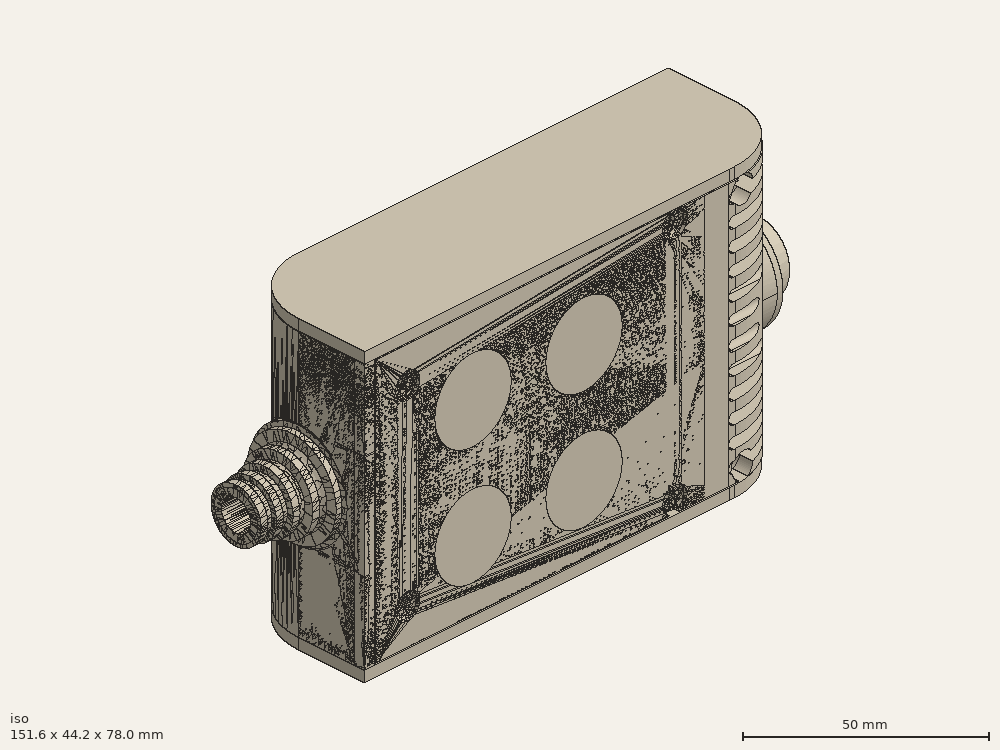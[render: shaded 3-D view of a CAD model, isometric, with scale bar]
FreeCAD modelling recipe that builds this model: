
FCSTD DOCUMENT  (FreeCAD 0.19R0.19.2)
Label: enclosure_193FCStd
License: All rights reserved
LicenseURL: http://en.wikipedia.org/wiki/All_rights_reserved
objects: Part::Revolution×152, Part::MultiFuse×146, Part::Feature×146, Sketcher::SketchObject×84, Part::Cut×70, Part::Cylinder×70, Part::Extrusion×67, Part::Fillet×58, Part::Box×36, App::MeasureDistance×4, PartDesign::Body×2, Image::ImagePlane×1
note: 831 computed .brp shape members not serialized (recipe doc carries the construction recipe); baked Part::Feature solids carry a one-line shape summary decoded from their .brp

FEATURE [Sketcher::SketchObject] Sketch  label="topSketch"
  FullyConstrained = true
  sketch-geometry (20):
    g0: LineSegment StartX=5.21097e-06 StartY=3 StartZ=0 EndX=5.21097e-06 EndY=19 EndZ=0
    g1: ArcOfCircle CenterX=19 CenterY=19 CenterZ=0 NormalX=0 NormalY=0 NormalZ=1 AngleXU=0 Radius=19 StartAngle=1.5708 EndAngle=3.14159
    g2: ArcOfCircle CenterX=19 CenterY=19 CenterZ=0 NormalX=0 NormalY=0 NormalZ=1 AngleXU=0 Radius=16 StartAngle=1.5708 EndAngle=3.14159
    g3: LineSegment StartX=114 StartY=35 StartZ=0 EndX=19 EndY=35 EndZ=0
    g4: LineSegment StartX=5.21097e-06 StartY=3 StartZ=0 EndX=5.21097e-06 EndY=0 EndZ=0
    g5: LineSegment StartX=3 StartY=0 StartZ=0 EndX=5.21097e-06 EndY=0 EndZ=0
    g6: LineSegment StartX=3 StartY=19 StartZ=0 EndX=3 EndY=0 EndZ=0
    g7: LineSegment StartX=19 StartY=38 StartZ=0 EndX=124 EndY=38 EndZ=0
    g8: Circle CenterX=119 CenterY=35 CenterZ=0 NormalX=0 NormalY=0 NormalZ=1 AngleXU=0 Radius=1
    g9: Circle CenterX=121 CenterY=35 CenterZ=0 NormalX=0 NormalY=0 NormalZ=1 AngleXU=0 Radius=1
    g10: Circle CenterX=121 CenterY=33 CenterZ=0 NormalX=0 NormalY=0 NormalZ=1 AngleXU=0 Radius=1
    g11: BSplineCurve PolesCount=3 KnotsCount=2 Degree=2 IsPeriodic=0
    g12: GeomPoint X=119 Y=35 Z=0
    g13: GeomPoint X=121 Y=33 Z=0
    g14: LineSegment StartX=119 StartY=35 StartZ=0 EndX=114 EndY=35 EndZ=0
    g15: ArcOfCircle CenterX=105 CenterY=19 CenterZ=0 NormalX=0 NormalY=0 NormalZ=1 AngleXU=0 Radius=19 StartAngle=5.7297 EndAngle=6.28319
    g16: ArcOfCircle CenterX=105 CenterY=19 CenterZ=0 NormalX=0 NormalY=0 NormalZ=1 AngleXU=0 Radius=16 StartAngle=5.60905 EndAngle=6.28319
    g17: LineSegment StartX=121 StartY=33 StartZ=0 EndX=121 EndY=19 EndZ=0
    g18: LineSegment StartX=124 StartY=38 StartZ=0 EndX=124 EndY=19 EndZ=0
    g19: LineSegment StartX=117.5 StartY=9.01251 StartZ=0 EndX=121.163 EndY=9.0125 EndZ=0
  constraints (46):
    c: Vertical(g0)
    c: Block(g0)
    c: Coincident(g1,g0)
    c: Block(g1)
    c: Coincident(g2,g1)
    c: Block(g2)
    c: Coincident(g3,g2)
    c: Horizontal(g3)
    c: Tangent(g3,g2)
    c: Coincident(g4,g0)
    c: Distance(g4) = 3
    c: Vertical(g4)
    c: Coincident(g5,g4)
    c: Horizontal(g5)
    c: Coincident(g6,g2)
    c: Coincident(g6,g5)
    c: Vertical(g6)
    c: Horizontal(g7)
    c: Distance(g7) = 105
    c: Coincident(g7,g1)
    c: Block(g3)
    c: Weight(g8) = 1
    c: Equal(g8,g9)
    c: Equal(g8,g10)
    c: InternalAlignment(g8,g11)
    c: InternalAlignment(g9,g11)
    c: InternalAlignment(g10,g11)
    c: InternalAlignment(g12,g11)
    c: InternalAlignment(g13,g11)
    c: Block(g11)
    c: Coincident(g14,g11)
    c: Coincident(g14,g3)
    c: Horizontal(g14)
    c: Block(g15)
    c: Coincident(g16,g15)
    c: Block(g16)
    c: Coincident(g17,g11)
    c: Coincident(g17,g16)
    c: Vertical(g17)
    c: Distance(g17) = 14
    c: Coincident(g18,g7)
    c: Coincident(g18,g15)
    c: Vertical(g18)
    c: Distance(g18) = 19
    c: Coincident(g19,g16)
    c: Coincident(g19,g15)
FEATURE [Sketcher::SketchObject] Sketch001  label="bottomSketch"
  FullyConstrained = true
  sketch-geometry (32):
    g0: LineSegment StartX=3.3 StartY=-6.03275e-07 StartZ=0 EndX=98 EndY=-6.03275e-07 EndZ=0
    g1: ArcOfCircle CenterX=98 CenterY=19 CenterZ=0 NormalX=0 NormalY=0 NormalZ=1 AngleXU=0 Radius=19 StartAngle=4.71239 EndAngle=5.71103
    g2: LineSegment StartX=6.3 StartY=8 StartZ=0 EndX=3.3 EndY=8 EndZ=0
    g3: LineSegment StartX=3.3 StartY=8 StartZ=0 EndX=3.3 EndY=-6.03275e-07 EndZ=0
    g4: ArcOfCircle CenterX=8.3 CenterY=5 CenterZ=0 NormalX=0 NormalY=0 NormalZ=1 AngleXU=0 Radius=2 StartAngle=3.14159 EndAngle=4.71239
    g5: LineSegment StartX=6.3 StartY=8 StartZ=0 EndX=6.3 EndY=5 EndZ=0
    g6: ArcOfCircle CenterX=98 CenterY=19 CenterZ=0 NormalX=0 NormalY=0 NormalZ=1 AngleXU=0 Radius=12.7 StartAngle=4.71239 EndAngle=6.28319
    g7: LineSegment StartX=94.7 StartY=3 StartZ=0 EndX=8.3 EndY=3 EndZ=0
    g8-g12: Circle x5 (B-spline internal-alignment scaffolding for g13; pole/knot coordinates omitted)
    g13: BSplineCurve PolesCount=5 KnotsCount=3 Degree=3 IsPeriodic=0
    g14: GeomPoint X=98 Y=6.3 Z=0
    g15: GeomPoint X=96.3938 Y=4.71946 Z=0
    g16: GeomPoint X=94.7 Y=3 Z=0
    g17-g23: Circle x7 (B-spline internal-alignment scaffolding for g24; pole/knot coordinates omitted)
    g24: BSplineCurve PolesCount=7 KnotsCount=5 Degree=3 IsPeriodic=0
    g25-g29: GeomPoint x5 (B-spline internal-alignment scaffolding for g24; pole/knot coordinates omitted)
    g30: ArcOfCircle CenterX=98 CenterY=19 CenterZ=0 NormalX=0 NormalY=0 NormalZ=1 AngleXU=0 Radius=15.7 StartAngle=5.81226 EndAngle=6.28319
    g31: LineSegment StartX=110.7 StartY=19 StartZ=0 EndX=113.7 EndY=19 EndZ=0
  constraints (41):
    c: Horizontal(g0)
    c: Coincident(g1,g0)
    c: Block(g1)
    c: Horizontal(g2)
    c: Distance(g2) = 3
    c: Coincident(g3,g2)
    c: Vertical(g3)
    c: Coincident(g3,g0)
    c: Block(g4)
    c: Block(g2)
    c: Coincident(g5,g2)
    c: Coincident(g5,g4)
    c: Vertical(g5)
    c: Coincident(g6,g1)
    c: Block(g6)
    c: Coincident(g7,g4)
    c: Horizontal(g7)
    c: Block(g0)
    c: Block(g7)
    c: Block(g3)
    c: Coincident(g13,g6)
    c: Weight(g8) = 1
    c: Equal(g8, g9-g12) x4
    c: Coincident(g13,g7)
    c: InternalAlignment(g8-g12 -> g13) x5
    c: InternalAlignment(g14,g13)
    c: InternalAlignment(g15,g13)
    c: InternalAlignment(g16,g13)
    c: Block(g13)
    c: Weight(g17) = 1
    c: Equal(g17, g18-g23) x6
    c: Coincident(g24,g1)
    c: InternalAlignment(g17-g23 -> g24) x7
    c: InternalAlignment(g25-g29 -> g24) x5
    c: Block(g24)
    c: Coincident(g30,g24)
    c: Coincident(g31,g6)
    c: Coincident(g31,g30)
    c: Horizontal(g31)
    c: Block(g31)
    c: Block(g30)
FEATURE [Part::Extrusion] Extrude  label="top"
  Base = -> Sketch
  Dir = (0,0,1)
  DirMode = 2
  FaceMakerClass = Part::FaceMakerBullseye
  LengthFwd = 72
  LengthRev = 0
  Solid = true
  Symmetric = false
FEATURE [Part::Extrusion] Extrude001  label="bottom"
  Base = -> Sketch001
  Dir = (0,0,1)
  DirMode = 2
  FaceMakerClass = Part::FaceMakerBullseye
  LengthFwd = 71.4
  LengthRev = 0
  Placement = pos=(0,0,0.3) rot=(0,0,1;0rad)
  Solid = true
  Symmetric = false
FEATURE [Sketcher::SketchObject] Sketch002  label="topSketch001"
  FullyConstrained = true
  sketch-geometry (8):
    g0: ArcOfCircle CenterX=19 CenterY=19.0975 CenterZ=0 NormalX=0 NormalY=0 NormalZ=1 AngleXU=0 Radius=18.9025 StartAngle=1.5708 EndAngle=3.14674
    g1: LineSegment StartX=0.0977805 StartY=19.0003 StartZ=0 EndX=0.0977805 EndY=0.000251602 EndZ=0
    g2: LineSegment StartX=19 StartY=38 StartZ=0 EndX=124 EndY=38 EndZ=0
    g3: LineSegment StartX=0.0977805 StartY=0.000251602 StartZ=0 EndX=105.098 EndY=0.000251602 EndZ=0
    g4: LineSegment StartX=124 StartY=38 StartZ=0 EndX=125.616 EndY=38 EndZ=0
    g5: LineSegment StartX=105.098 StartY=0.000251602 StartZ=0 EndX=106.713 EndY=0.000251602 EndZ=0
    g6: ArcOfCircle CenterX=106.616 CenterY=19 CenterZ=0 NormalX=0 NormalY=0 NormalZ=1 AngleXU=0 Radius=19 StartAngle=4.71754 EndAngle=6.28319
    g7: LineSegment StartX=125.616 StartY=38 StartZ=0 EndX=125.616 EndY=19 EndZ=0
  constraints (21):
    c: Block(g0)
    c: Coincident(g1,g0)
    c: Vertical(g1)
    c: Horizontal(g2)
    c: Distance(g2) = 105
    c: Coincident(g2,g0)
    c: Distance(g1) = 19
    c: Coincident(g3,g1)
    c: Horizontal(g3)
    c: Distance(g3) = 105
    c: Coincident(g4,g2)
    c: Horizontal(g4)
    c: Distance(g4) = 1.61553
    c: Horizontal(g5)
    c: Equal(g4,g5) = 1.61553
    c: Coincident(g5,g3)
    c: Block(g6)
    c: Coincident(g6,g5)
    c: Coincident(g7,g4)
    c: Coincident(g7,g6)
    c: Vertical(g7)
FEATURE [Part::Extrusion] Extrude002  label="sideA"
  Base = -> Sketch002
  Dir = (0,0,1)
  DirMode = 2
  FaceMakerClass = Part::FaceMakerBullseye
  LengthFwd = 3
  LengthRev = 0
  Placement = pos=(0,0,-3) rot=(0,0,1;0rad)
  Solid = true
  Symmetric = false
FEATURE [Sketcher::SketchObject] Sketch003  label="topSketch002"
  FullyConstrained = true
  sketch-geometry (6):
    g0: LineSegment StartX=19 StartY=38 StartZ=0 EndX=117 EndY=38 EndZ=0
    g1: ArcOfCircle CenterX=19 CenterY=19 CenterZ=0 NormalX=0 NormalY=0 NormalZ=1 AngleXU=0 Radius=19 StartAngle=1.5708 EndAngle=3.14159
    g2: LineSegment StartX=117 StartY=38 StartZ=0 EndX=117 EndY=19 EndZ=0
    g3: LineSegment StartX=98 StartY=1.0161e-12 StartZ=0 EndX=5.22862e-06 EndY=1.0161e-12 EndZ=0
    g4: LineSegment StartX=5.22862e-06 StartY=19 StartZ=0 EndX=5.22862e-06 EndY=1.0161e-12 EndZ=0
    g5: ArcOfCircle CenterX=98 CenterY=19 CenterZ=0 NormalX=0 NormalY=0 NormalZ=1 AngleXU=0 Radius=19 StartAngle=4.71239 EndAngle=6.28319
  constraints (16):
    c: Horizontal(g0)
    c: Distance(g0) = 98
    c: Coincident(g1,g0)
    c: Block(g1)
    c: Coincident(g2,g0)
    c: Vertical(g2)
    c: Distance(g2) = 19
    c: Horizontal(g3)
    c: Coincident(g4,g1)
    c: Vertical(g4)
    c: Coincident(g3,g4)
    c: Block(g3)
    c: Coincident(g5,g2)
    c: Coincident(g5,g3)
    c: Block(g0)
    c: Block(g5)
FEATURE [Sketcher::SketchObject] Sketch004
  FullyConstrained = true
  MapMode = 3
  Placement = pos=(0,0,0) rot=(1,0,0;1.5708rad)
  Support = -> [Extrude]
  sketch-geometry (8):
    g0: Circle CenterX=80.351 CenterY=-67.6202 CenterZ=0 NormalX=0 NormalY=0 NormalZ=1 AngleXU=0 Radius=2
    g1: Circle CenterX=80.351 CenterY=-67.6202 CenterZ=0 NormalX=0 NormalY=0 NormalZ=1 AngleXU=0 Radius=3
    g2: Circle CenterX=80.351 CenterY=-4.92017 CenterZ=0 NormalX=0 NormalY=0 NormalZ=1 AngleXU=0 Radius=2
    g3: Circle CenterX=80.351 CenterY=-4.92017 CenterZ=0 NormalX=0 NormalY=0 NormalZ=1 AngleXU=0 Radius=3
    g4: Circle CenterX=23.851 CenterY=-4.92017 CenterZ=0 NormalX=0 NormalY=0 NormalZ=1 AngleXU=0 Radius=2
    g5: Circle CenterX=23.851 CenterY=-4.92017 CenterZ=0 NormalX=0 NormalY=0 NormalZ=1 AngleXU=0 Radius=3
    g6: Circle CenterX=23.851 CenterY=-67.6202 CenterZ=0 NormalX=0 NormalY=0 NormalZ=1 AngleXU=0 Radius=2
    g7: Circle CenterX=23.851 CenterY=-67.6202 CenterZ=0 NormalX=0 NormalY=0 NormalZ=1 AngleXU=0 Radius=3
  constraints (8):
    c: Block(g3)
    c: Block(g2)
    c: Block(g1)
    c: Block(g0)
    c: Block(g6)
    c: Block(g7)
    c: Block(g4)
    c: Block(g5)
FEATURE [Part::Extrusion] Extrude004
  Base = -> Sketch004
  Dir = (0,-1,2e-16)
  DirMode = 2
  FaceMakerClass = Part::FaceMakerBullseye
  LengthFwd = 6
  LengthRev = 0
  Placement = pos=(0,9,0) rot=(0,0,1;0rad)
  Solid = true
  Symmetric = false
FEATURE [Sketcher::SketchObject] Sketch005
  FullyConstrained = true
  MapMode = 3
  Placement = pos=(0,0,0) rot=(1,0,0;1.5708rad)
  Support = -> [Extrude]
  sketch-geometry (8):
    g0: Circle CenterX=80.351 CenterY=-67.6202 CenterZ=0 NormalX=0 NormalY=0 NormalZ=1 AngleXU=0 Radius=3
    g1: Circle CenterX=80.351 CenterY=-4.92017 CenterZ=0 NormalX=0 NormalY=0 NormalZ=1 AngleXU=0 Radius=3
    g2: Circle CenterX=23.851 CenterY=-4.92017 CenterZ=0 NormalX=0 NormalY=0 NormalZ=1 AngleXU=0 Radius=3
    g3: Circle CenterX=23.851 CenterY=-67.6202 CenterZ=0 NormalX=0 NormalY=0 NormalZ=1 AngleXU=0 Radius=3
    g4: Circle CenterX=23.851 CenterY=-67.6202 CenterZ=0 NormalX=0 NormalY=0 NormalZ=1 AngleXU=0 Radius=5
    g5: Circle CenterX=80.351 CenterY=-67.6202 CenterZ=0 NormalX=0 NormalY=0 NormalZ=1 AngleXU=0 Radius=5
    g6: Circle CenterX=23.851 CenterY=-4.92017 CenterZ=0 NormalX=0 NormalY=0 NormalZ=1 AngleXU=0 Radius=5
    g7: Circle CenterX=80.351 CenterY=-4.92017 CenterZ=0 NormalX=0 NormalY=0 NormalZ=1 AngleXU=0 Radius=5
  constraints (8):
    c: Block(g1)
    c: Block(g0)
    c: Block(g3)
    c: Block(g2)
    c: Block(g5)
    c: Block(g4)
    c: Block(g6)
    c: Block(g7)
FEATURE [Part::Extrusion] Extrude005
  Base = -> Sketch005
  Dir = (0,-1,2e-16)
  DirMode = 2
  FaceMakerClass = Part::FaceMakerBullseye
  LengthFwd = 2
  LengthRev = 0
  Solid = true
  Symmetric = false
FEATURE [Sketcher::SketchObject] Sketch006
  FullyConstrained = true
  MapMode = 3
  Placement = pos=(0,0,0) rot=(1,0,0;1.5708rad)
  sketch-geometry (8):
    g0: Circle CenterX=80.351 CenterY=-67.6202 CenterZ=0 NormalX=0 NormalY=0 NormalZ=1 AngleXU=0 Radius=3
    g1: Circle CenterX=80.351 CenterY=-4.92017 CenterZ=0 NormalX=0 NormalY=0 NormalZ=1 AngleXU=0 Radius=3
    g2: Circle CenterX=23.851 CenterY=-4.92017 CenterZ=0 NormalX=0 NormalY=0 NormalZ=1 AngleXU=0 Radius=3
    g3: Circle CenterX=23.851 CenterY=-67.6202 CenterZ=0 NormalX=0 NormalY=0 NormalZ=1 AngleXU=0 Radius=3
    g4: Circle CenterX=23.851 CenterY=-67.6202 CenterZ=0 NormalX=0 NormalY=0 NormalZ=1 AngleXU=0 Radius=5
    g5: Circle CenterX=80.351 CenterY=-67.6202 CenterZ=0 NormalX=0 NormalY=0 NormalZ=1 AngleXU=0 Radius=5
    g6: Circle CenterX=23.851 CenterY=-4.92017 CenterZ=0 NormalX=0 NormalY=0 NormalZ=1 AngleXU=0 Radius=5
    g7: Circle CenterX=80.351 CenterY=-4.92017 CenterZ=0 NormalX=0 NormalY=0 NormalZ=1 AngleXU=0 Radius=5
  constraints (8):
    c: Block(g1)
    c: Block(g0)
    c: Block(g3)
    c: Block(g2)
    c: Block(g5)
    c: Block(g4)
    c: Block(g6)
    c: Block(g7)
FEATURE [Part::Extrusion] Extrude007
  Base = -> Sketch006
  Dir = (0,-1,2e-16)
  DirMode = 2
  FaceMakerClass = Part::FaceMakerBullseye
  LengthFwd = 2
  LengthRev = 0
  Solid = true
  Symmetric = false
FEATURE [Part::Fillet] Fillet
  Base = -> Extrude007
  Edges = 4 edges r=1.99: [Edge6,Edge12,Edge18,Edge24]
FEATURE [Part::Cut] Cut
  Base = -> Extrude005
  Placement = pos=(0,5,0) rot=(0,0,1;0rad)
  Tool = -> Fillet
FEATURE [Part::MultiFuse] Fusion  label="pCBScrews"
  Placement = pos=(-2.5,0,72.3) rot=(0,0,1;0rad)
  Shapes = -> [Extrude004,Cut]
FEATURE [App::MeasureDistance] Distance  label="Distance: 0.69 mm"
  Distance = 0.685967
  P1 = (24.0138,2.9647,0.3)
  P2 = (23.8901,3,-0.373787)
FEATURE [App::MeasureDistance] Distance001  label="Distance: 0.53 mm"
  Distance = 0.533607
  P1 = (80.2939,3,72.2334)
  P2 = (80.281,2.99661,71.7)
FEATURE [Part::Fillet] Fillet001
  Base = -> Extrude001
  Edges = 1 edges r=2.4: [Edge17]
FEATURE [Part::Fillet] Fillet002  label="bottom001"
  Base = -> Fillet001
  Edges = 1 edges r=2.4: [Edge36]
FEATURE [Part::Fillet] Fillet003  label="top001"
  Base = -> Extrude
  Edges = 1 edges r=2: [Edge1]
FEATURE [Sketcher::SketchObject] Sketch007
  FullyConstrained = true
  sketch-geometry (16):
    g0: LineSegment StartX=4 StartY=0 StartZ=0 EndX=4 EndY=2.4 EndZ=0
    g1: LineSegment StartX=4 StartY=2.4 StartZ=0 EndX=7 EndY=2.4 EndZ=0
    g2: LineSegment StartX=4 StartY=0 StartZ=0 EndX=5.7 EndY=0 EndZ=0
    g3: LineSegment StartX=5.7 StartY=0 StartZ=0 EndX=5.7 EndY=-5.6 EndZ=0
    g4-g8: Circle x5 (B-spline internal-alignment scaffolding for g9; pole/knot coordinates omitted)
    g9: BSplineCurve PolesCount=5 KnotsCount=3 Degree=3 IsPeriodic=0
    g10: GeomPoint X=7 Y=2.4 Z=0
    g11: GeomPoint X=10.4582 Y=-1.55472 Z=0
    g12: GeomPoint X=14 Y=-5.6 Z=0
    g13: LineSegment StartX=14 StartY=-5.6 StartZ=0 EndX=14 EndY=-14.1 EndZ=0
    g14: LineSegment StartX=14 StartY=-14.1 StartZ=0 EndX=6.5 EndY=-14.1 EndZ=0
    g15: LineSegment StartX=5.7 StartY=-5.6 StartZ=0 EndX=6.5 EndY=-14.1 EndZ=0
  constraints (28):
    c: Distance(g0) = 2.4
    c: Vertical(g0)
    c: Block(g0)
    c: Coincident(g1,g0)
    c: Horizontal(g1)
    c: Distance(g1) = 3
    c: Coincident(g2,g0)
    c: Horizontal(g2)
    c: Distance(g2) = 1.7
    c: Coincident(g3,g2)
    c: Vertical(g3)
    c: Distance(g3) = 5.6
    c: Coincident(g9,g1)
    c: Weight(g4) = 1
    c: Equal(g4, g5-g8) x4
    c: InternalAlignment(g4-g8 -> g9) x5
    c: InternalAlignment(g10,g9)
    c: InternalAlignment(g11,g9)
    c: InternalAlignment(g12,g9)
    c: Block(g9)
    c: Coincident(g13,g9)
    c: Vertical(g13)
    c: Distance(g13) = 8.5
    c: Coincident(g14,g13)
    c: Horizontal(g14)
    c: Distance(g14) = 7.5
    c: Coincident(g15,g3)
    c: Coincident(g15,g14)
FEATURE [Part::Feature] Face
  shape: bbox 10 x 16.5 x 2e-07 mm, 1 faces, 0 solids (baked)
FEATURE [Part::Revolution] Revolve  label="plugHousing"
  Angle = 360
  Axis = (0,1,0)
  Base = (0,0,0)
  FaceMakerClass = Part::FaceMakerBullseye
  Placement = pos=(0,0,36.15) rot=(0,0,1;0rad)
  Solid = false
  Source = -> Face
  Symmetric = false
FEATURE [Part::Feature] Face001
  shape: bbox 10 x 16.5 x 2e-07 mm, 1 faces, 0 solids (baked)
FEATURE [Part::Revolution] Revolve001  label="plugHousing001"
  Angle = 360
  Axis = (0,1,0)
  Base = (0,0,0)
  FaceMakerClass = Part::FaceMakerBullseye
  Placement = pos=(0,0,36.15) rot=(0,0,1;0rad)
  Solid = false
  Source = -> Face001
  Symmetric = false
FEATURE [Part::MultiFuse] Fusion001  label="plugHousing002"
  Placement = pos=(0,0,0) rot=(0,0,1;1.5708rad)
  Shapes = -> [Revolve001,Revolve]
FEATURE [Part::Feature] Face002
  shape: bbox 10 x 16.5 x 2e-07 mm, 1 faces, 0 solids (baked)
FEATURE [Part::Revolution] Revolve003  label="plugHousing005"
  Angle = 360
  Axis = (0,1,0)
  Base = (0,0,0)
  FaceMakerClass = Part::FaceMakerBullseye
  Placement = pos=(0,0,36.15) rot=(0,0,1;0rad)
  Solid = false
  Source = -> Face002
  Symmetric = false
FEATURE [Part::Feature] Face003
  shape: bbox 10 x 16.5 x 2e-07 mm, 1 faces, 0 solids (baked)
FEATURE [Part::Revolution] Revolve002  label="plugHousing003"
  Angle = 360
  Axis = (0,1,0)
  Base = (0,0,0)
  FaceMakerClass = Part::FaceMakerBullseye
  Placement = pos=(0,0,36.15) rot=(0,0,1;0rad)
  Solid = false
  Source = -> Face003
  Symmetric = false
FEATURE [Part::MultiFuse] Fusion002  label="plugHousing004"
  Placement = pos=(0,0,0) rot=(0,0,1;1.5708rad)
  Shapes = -> [Revolve002,Revolve003]
FEATURE [Part::MultiFuse] Fusion003  label="plugHousing006"
  Placement = pos=(0,19,0) rot=(0,0,1;3.14159rad)
  Shapes = -> [Fusion002,Fusion001]
FEATURE [Part::Feature] Face004
  shape: bbox 10 x 16.5 x 2e-07 mm, 1 faces, 0 solids (baked)
FEATURE [Part::Revolution] Revolve006  label="plugHousing010"
  Angle = 360
  Axis = (0,1,0)
  Base = (0,0,0)
  FaceMakerClass = Part::FaceMakerBullseye
  Placement = pos=(0,0,36.15) rot=(0,0,1;0rad)
  Solid = false
  Source = -> Face004
  Symmetric = false
FEATURE [Part::Feature] Face005
  shape: bbox 10 x 16.5 x 2e-07 mm, 1 faces, 0 solids (baked)
FEATURE [Part::Revolution] Revolve007  label="plugHousing011"
  Angle = 360
  Axis = (0,1,0)
  Base = (0,0,0)
  FaceMakerClass = Part::FaceMakerBullseye
  Placement = pos=(0,0,36.15) rot=(0,0,1;0rad)
  Solid = false
  Source = -> Face005
  Symmetric = false
FEATURE [Part::Feature] Face006
  shape: bbox 10 x 16.5 x 2e-07 mm, 1 faces, 0 solids (baked)
FEATURE [Part::Revolution] Revolve004  label="plugHousing007"
  Angle = 360
  Axis = (0,1,0)
  Base = (0,0,0)
  FaceMakerClass = Part::FaceMakerBullseye
  Placement = pos=(0,0,36.15) rot=(0,0,1;0rad)
  Solid = false
  Source = -> Face006
  Symmetric = false
FEATURE [Part::MultiFuse] Fusion004  label="plugHousing009"
  Placement = pos=(0,0,0) rot=(0,0,1;1.5708rad)
  Shapes = -> [Revolve004,Revolve007]
FEATURE [Part::Feature] Face007
  shape: bbox 10 x 16.5 x 2e-07 mm, 1 faces, 0 solids (baked)
FEATURE [Part::Revolution] Revolve005  label="plugHousing008"
  Angle = 360
  Axis = (0,1,0)
  Base = (0,0,0)
  FaceMakerClass = Part::FaceMakerBullseye
  Placement = pos=(0,0,36.15) rot=(0,0,1;0rad)
  Solid = false
  Source = -> Face007
  Symmetric = false
FEATURE [Part::MultiFuse] Fusion005  label="plugHousing012"
  Placement = pos=(0,0,0) rot=(0,0,1;1.5708rad)
  Shapes = -> [Revolve006,Revolve005]
FEATURE [Part::MultiFuse] Fusion006  label="plugHousing013"
  Placement = pos=(0,19,0) rot=(0,0,1;3.14159rad)
  Shapes = -> [Fusion005,Fusion004]
FEATURE [Part::MultiFuse] Fusion007  label="plugHousing014"
  Placement = pos=(122.621,0,-0.15) rot=(0,0,1;0rad)
  Shapes = -> [Fusion003,Fusion006]
FEATURE [Part::Cylinder] Cylinder002
  Angle = 360
  AttacherType = Attacher::AttachEngine3D
  Height = 20
  Placement = pos=(0,0,36.15) rot=(0,0,1;0rad)
  Radius = 4
FEATURE [Part::Cylinder] Cylinder003
  Angle = 360
  AttacherType = Attacher::AttachEngine3D
  Height = 10
  Placement = pos=(0,0,36.15) rot=(0,0,1;0rad)
  Radius = 4
FEATURE [Part::MultiFuse] Fusion009  label="removeToCreateHoleForPlugHousing"
  Placement = pos=(70,19,36.15) rot=(0,1,0;1.5708rad)
  Shapes = -> [Cylinder002,Cylinder003]
FEATURE [Part::Cylinder] Cylinder004
  Angle = 360
  AttacherType = Attacher::AttachEngine3D
  Height = 20
  Placement = pos=(0,0,36.15) rot=(0,0,1;0rad)
  Radius = 4
FEATURE [Part::Cylinder] Cylinder005
  Angle = 360
  AttacherType = Attacher::AttachEngine3D
  Height = 10
  Placement = pos=(0,0,36.15) rot=(0,0,1;0rad)
  Radius = 4
FEATURE [Part::MultiFuse] Fusion010  label="removeToCreateHoleForPlugHousing001"
  Placement = pos=(70,19,36.15) rot=(0,1,0;1.5708rad)
  Shapes = -> [Cylinder004,Cylinder005]
FEATURE [Part::Cut] Cut001
  Base = -> Fillet003
  Tool = -> Fusion010
FEATURE [Part::Cut] Cut002  label="Bottom"
  Base = -> Fillet002
  Tool = -> Fusion009
FEATURE [Part::Feature] Face008
  shape: bbox 10 x 16.5 x 2e-07 mm, 1 faces, 0 solids (baked)
FEATURE [Part::Revolution] Revolve011  label="plugHousing021"
  Angle = 360
  Axis = (0,1,0)
  Base = (0,0,0)
  FaceMakerClass = Part::FaceMakerBullseye
  Placement = pos=(0,0,36.15) rot=(0,0,1;0rad)
  Solid = false
  Source = -> Face008
  Symmetric = false
FEATURE [Part::Feature] Face009
  shape: bbox 10 x 16.5 x 2e-07 mm, 1 faces, 0 solids (baked)
FEATURE [Part::Revolution] Revolve012  label="plugHousing022"
  Angle = 360
  Axis = (0,1,0)
  Base = (0,0,0)
  FaceMakerClass = Part::FaceMakerBullseye
  Placement = pos=(0,0,36.15) rot=(0,0,1;0rad)
  Solid = false
  Source = -> Face009
  Symmetric = false
FEATURE [Part::Feature] Face010 .. Face013  x4 (patterned run collapsed; names and placements below)
  shape: bbox 10 x 16.5 x 2e-07 mm, 1 faces, 0 solids (baked)
FEATURE [Part::Revolution] Revolve015  label="plugHousing027"
  Angle = 360
  Axis = (0,1,0)
  Base = (0,0,0)
  FaceMakerClass = Part::FaceMakerBullseye
  Placement = pos=(0,0,36.15) rot=(0,0,1;0rad)
  Solid = false
  Source = -> Face013
  Symmetric = false
FEATURE [Part::Feature] Face014
  shape: bbox 10 x 16.5 x 2e-07 mm, 1 faces, 0 solids (baked)
FEATURE [Part::Feature] Face015
  shape: bbox 10 x 16.5 x 2e-07 mm, 1 faces, 0 solids (baked)
FEATURE [Part::Feature] Face016
  shape: bbox 10 x 16.5 x 2e-07 mm, 1 faces, 0 solids (baked)
FEATURE [Part::Revolution] Revolve019  label="plugHousing033"
  Angle = 360
  Axis = (0,1,0)
  Base = (0,0,0)
  FaceMakerClass = Part::FaceMakerBullseye
  Placement = pos=(0,0,36.15) rot=(0,0,1;0rad)
  Solid = false
  Source = -> Face016
  Symmetric = false
FEATURE [Part::Feature] Face017
  shape: bbox 10 x 16.5 x 2e-07 mm, 1 faces, 0 solids (baked)
FEATURE [Part::Revolution] Revolve020  label="plugHousing034"
  Angle = 360
  Axis = (0,1,0)
  Base = (0,0,0)
  FaceMakerClass = Part::FaceMakerBullseye
  Placement = pos=(0,0,36.15) rot=(0,0,1;0rad)
  Solid = false
  Source = -> Face017
  Symmetric = false
FEATURE [Part::Feature] Face018
  shape: bbox 10 x 16.5 x 2e-07 mm, 1 faces, 0 solids (baked)
FEATURE [Part::Revolution] Revolve016  label="plugHousing030"
  Angle = 360
  Axis = (0,1,0)
  Base = (0,0,0)
  FaceMakerClass = Part::FaceMakerBullseye
  Placement = pos=(0,0,36.15) rot=(0,0,1;0rad)
  Solid = false
  Source = -> Face018
  Symmetric = false
FEATURE [Part::MultiFuse] Fusion020  label="plugHousing038"
  Placement = pos=(0,0,0) rot=(0,0,1;1.5708rad)
  Shapes = -> [Revolve016,Revolve020]
FEATURE [Part::Feature] Face019
  shape: bbox 10 x 16.5 x 2e-07 mm, 1 faces, 0 solids (baked)
FEATURE [Part::Feature] Face020
  shape: bbox 10 x 16.5 x 2e-07 mm, 1 faces, 0 solids (baked)
FEATURE [Part::Revolution] Revolve017  label="plugHousing031"
  Angle = 360
  Axis = (0,1,0)
  Base = (0,0,0)
  FaceMakerClass = Part::FaceMakerBullseye
  Placement = pos=(0,0,36.15) rot=(0,0,1;0rad)
  Solid = false
  Source = -> Face020
  Symmetric = false
FEATURE [Part::MultiFuse] Fusion021  label="plugHousing039"
  Placement = pos=(0,0,0) rot=(0,0,1;1.5708rad)
  Shapes = -> [Revolve019,Revolve017]
FEATURE [Part::MultiFuse] Fusion023  label="plugHousing041"
  Placement = pos=(0,19,0) rot=(0,0,1;3.14159rad)
  Shapes = -> [Fusion021,Fusion020]
FEATURE [Part::Revolution] Revolve022  label="plugHousing043"
  Angle = 360
  Axis = (0,1,0)
  Base = (0,0,0)
  FaceMakerClass = Part::FaceMakerBullseye
  Placement = pos=(0,0,36.15) rot=(0,0,1;0rad)
  Solid = false
  Source = -> Face019
  Symmetric = false
FEATURE [Part::Feature] Face021
  shape: bbox 10 x 16.5 x 2e-07 mm, 1 faces, 0 solids (baked)
FEATURE [Part::Revolution] Revolve023  label="plugHousing044"
  Angle = 360
  Axis = (0,1,0)
  Base = (0,0,0)
  FaceMakerClass = Part::FaceMakerBullseye
  Placement = pos=(0,0,36.15) rot=(0,0,1;0rad)
  Solid = false
  Source = -> Face021
  Symmetric = false
FEATURE [Part::Feature] Face022
  shape: bbox 10 x 16.5 x 2e-07 mm, 1 faces, 0 solids (baked)
FEATURE [Part::Revolution] Revolve018  label="plugHousing032"
  Angle = 360
  Axis = (0,1,0)
  Base = (0,0,0)
  FaceMakerClass = Part::FaceMakerBullseye
  Placement = pos=(0,0,36.15) rot=(0,0,1;0rad)
  Solid = false
  Source = -> Face022
  Symmetric = false
FEATURE [Part::MultiFuse] Fusion022  label="plugHousing040"
  Placement = pos=(0,0,0) rot=(0,0,1;1.5708rad)
  Shapes = -> [Revolve018,Revolve023]
FEATURE [Part::Feature] Face023
  shape: bbox 10 x 16.5 x 2e-07 mm, 1 faces, 0 solids (baked)
FEATURE [Part::Revolution] Revolve021  label="plugHousing035"
  Angle = 360
  Axis = (0,1,0)
  Base = (0,0,0)
  FaceMakerClass = Part::FaceMakerBullseye
  Placement = pos=(0,0,36.15) rot=(0,0,1;0rad)
  Solid = false
  Source = -> Face023
  Symmetric = false
FEATURE [Part::MultiFuse] Fusion018  label="plugHousing036"
  Placement = pos=(0,0,0) rot=(0,0,1;1.5708rad)
  Shapes = -> [Revolve022,Revolve021]
FEATURE [Part::MultiFuse] Fusion019  label="plugHousing037"
  Placement = pos=(0,19,0) rot=(0,0,1;3.14159rad)
  Shapes = -> [Fusion018,Fusion022]
FEATURE [Part::MultiFuse] Fusion024  label="plugHousing042"
  Placement = pos=(122.621,0,-0.15) rot=(0,0,1;0rad)
  Shapes = -> [Fusion023,Fusion019]
FEATURE [Part::Cylinder] Cylinder006
  Angle = 360
  AttacherType = Attacher::AttachEngine3D
  Height = 20
  Placement = pos=(0,0,36.15) rot=(0,0,1;0rad)
  Radius = 14.3
FEATURE [Part::Cylinder] Cylinder007
  Angle = 360
  AttacherType = Attacher::AttachEngine3D
  Height = 10
  Placement = pos=(0,0,36.15) rot=(0,0,1;0rad)
  Radius = 4
FEATURE [Part::MultiFuse] Fusion026  label="removeToCreteHoleForPlugHousing"
  Placement = pos=(70,19,36) rot=(0,1,0;1.5708rad)
  Shapes = -> [Cylinder006,Cylinder007]
FEATURE [Part::Box] Box001  label="Cube001"
  AttacherType = Attacher::AttachEngine3D
  Height = 28
  Length = 3
  Placement = pos=(110.7,19,22) rot=(0,0,1;0rad)
  Width = 15.7
FEATURE [Part::Cut] Cut003  label="top002"
  Base = -> Cut001
  Tool = -> Fusion007
FEATURE [Part::Revolution] Revolve008  label="plugHousing015"
  Angle = 360
  Axis = (0,1,0)
  Base = (0,0,0)
  FaceMakerClass = Part::FaceMakerBullseye
  Placement = pos=(0,0,36.15) rot=(0,0,1;0rad)
  Solid = false
  Source = -> Face010
  Symmetric = false
FEATURE [Part::MultiFuse] Fusion013  label="plugHousing020"
  Placement = pos=(0,0,0) rot=(0,0,1;1.5708rad)
  Shapes = -> [Revolve008,Revolve012]
FEATURE [Part::Cut] Cut004  label="top003"
  Base = -> Cut003
  Placement = pos=(1,0,0) rot=(0,0,1;0rad)
  Tool = -> Fusion026
FEATURE [Part::Cylinder] Cylinder008
  Angle = 360
  AttacherType = Attacher::AttachEngine3D
  Height = 20
  Placement = pos=(0,0,36.15) rot=(0,0,1;0rad)
  Radius = 10.3
FEATURE [Part::Cylinder] Cylinder009
  Angle = 360
  AttacherType = Attacher::AttachEngine3D
  Height = 10
  Placement = pos=(0,0,36.15) rot=(0,0,1;0rad)
  Radius = 4
FEATURE [Part::MultiFuse] Fusion027  label="removeToCreteHoleForPlugHousing001"
  Placement = pos=(70,19,36) rot=(0,1,0;1.5708rad)
  Shapes = -> [Cylinder008,Cylinder009]
FEATURE [Part::Cut] Cut005  label="plugHousingTab"
  Base = -> Box001
  Tool = -> Fusion027
FEATURE [Part::MultiFuse] Fusion028  label="plugHousing045"
  Shapes = -> [Fusion024,Cut005]
FEATURE [Part::Box] Box002  label="Cube002"
  AttacherType = Attacher::AttachEngine3D
  Height = 28.8
  Length = 3
  Placement = pos=(107.3,28,21.6) rot=(0,0,1;0rad)
  Width = 7
FEATURE [Part::Box] Box003  label="Cube003"
  AttacherType = Attacher::AttachEngine3D
  Height = 3
  Length = 6.4
  Placement = pos=(107.3,28,18.6) rot=(0,0,1;0rad)
  Width = 7
FEATURE [Part::Box] Box004  label="Cube004"
  AttacherType = Attacher::AttachEngine3D
  Height = 3
  Length = 6.4
  Placement = pos=(107.3,28,50.4) rot=(0,0,1;0rad)
  Width = 7
FEATURE [Part::MultiFuse] Fusion029  label="plugHousingBracketHolder"
  Shapes = -> [Box004,Box002,Box003]
FEATURE [Part::Cylinder] Cylinder010
  Angle = 360
  AttacherType = Attacher::AttachEngine3D
  Height = 20
  Placement = pos=(0,0,36.15) rot=(0,0,1;0rad)
  Radius = 14.3
FEATURE [Part::Cylinder] Cylinder011
  Angle = 360
  AttacherType = Attacher::AttachEngine3D
  Height = 10
  Placement = pos=(0,0,36.15) rot=(0,0,1;0rad)
  Radius = 4
FEATURE [Part::MultiFuse] Fusion030  label="removeToCreteHoleForPlugHousing002"
  Placement = pos=(70,19,36) rot=(0,1,0;1.5708rad)
  Shapes = -> [Cylinder010,Cylinder011]
FEATURE [Part::Cut] Cut006  label="plugHousingBracketHolder001"
  Base = -> Fusion029
  Tool = -> Fusion030
FEATURE [Part::Cylinder] Cylinder012
  Angle = 360
  AttacherType = Attacher::AttachEngine3D
  Height = 20
  Placement = pos=(0,0,36.15) rot=(0,0,1;0rad)
  Radius = 7
FEATURE [Part::Cylinder] Cylinder013
  Angle = 360
  AttacherType = Attacher::AttachEngine3D
  Height = 10
  Placement = pos=(0,0,36.15) rot=(0,0,1;0rad)
  Radius = 4
FEATURE [Part::MultiFuse] Fusion032  label="removeToCreteHoleForPlugHousing003"
  Placement = pos=(70,19,36) rot=(0,1,0;1.5708rad)
  Shapes = -> [Cylinder012,Cylinder013]
FEATURE [Part::Cut] Cut007  label="bottom002"
  Base = -> Cut002
  Tool = -> Fusion032
FEATURE [Sketcher::SketchObject] Sketch008
  FullyConstrained = true
  sketch-geometry (54):
    g0: LineSegment StartX=-4.2 StartY=0 StartZ=0 EndX=-6.2 EndY=0 EndZ=0
    g1: LineSegment StartX=-14 StartY=-18 StartZ=0 EndX=-14 EndY=-26.5 EndZ=0
    g2: LineSegment StartX=-4.2 StartY=0 StartZ=0 EndX=-4.2 EndY=-13.4877 EndZ=0
    g3: Circle CenterX=-4.2 CenterY=-13.4877 CenterZ=0 NormalX=0 NormalY=0 NormalZ=1 AngleXU=0 Radius=1
    g4: Circle CenterX=-4.2 CenterY=-26.5 CenterZ=0 NormalX=0 NormalY=0 NormalZ=1 AngleXU=0 Radius=1
    g5: Circle CenterX=-8.2 CenterY=-26.5 CenterZ=0 NormalX=0 NormalY=0 NormalZ=1 AngleXU=0 Radius=1
    g6: BSplineCurve PolesCount=3 KnotsCount=2 Degree=2 IsPeriodic=0
    g7: GeomPoint X=-4.2 Y=-13.4877 Z=0
    g8: GeomPoint X=-8.2 Y=-26.5 Z=0
    g9: LineSegment StartX=-14 StartY=-26.5 StartZ=0 EndX=-8.2 EndY=-26.5 EndZ=0
    g10: LineSegment StartX=-10.15 StartY=-12 StartZ=0 EndX=-10.15 EndY=-14 EndZ=0
    g11: LineSegment StartX=-12.8401 StartY=-16 StartZ=0 EndX=-10.1571 EndY=-16 EndZ=0
    g12: LineSegment StartX=-10.15 StartY=-14 StartZ=0 EndX=-8.70761 EndY=-14 EndZ=0
    g13: LineSegment StartX=-12.8401 StartY=-16 StartZ=0 EndX=-12.8401 EndY=-17.6958 EndZ=0
    g14: LineSegment StartX=-10.15 StartY=-12 StartZ=0 EndX=-7.79258 EndY=-12 EndZ=0
    g15: Circle CenterX=-6.2215 CenterY=-2 CenterZ=0 NormalX=0 NormalY=0 NormalZ=1 AngleXU=0 Radius=1
    g16: Circle CenterX=-6.22762 CenterY=-2.58724 CenterZ=0 NormalX=0 NormalY=0 NormalZ=1 AngleXU=0 Radius=1
    g17: Circle CenterX=-6.32538 CenterY=-4 CenterZ=0 NormalX=0 NormalY=0 NormalZ=1 AngleXU=0 Radius=1
    g18: BSplineCurve PolesCount=3 KnotsCount=2 Degree=2 IsPeriodic=0
    g19: GeomPoint X=-6.2215 Y=-2 Z=0
    g20: GeomPoint X=-6.32538 Y=-4 Z=0
    g21: Circle CenterX=-6.48644 CenterY=-5.99526 CenterZ=0 NormalX=0 NormalY=0 NormalZ=1 AngleXU=0 Radius=1
    g22: Circle CenterX=-6.58486 CenterY=-6.99526 CenterZ=0 NormalX=0 NormalY=0 NormalZ=1 AngleXU=0 Radius=1
    g23: Circle CenterX=-6.77343 CenterY=-8 CenterZ=0 NormalX=0 NormalY=0 NormalZ=1 AngleXU=0 Radius=1
    g24: BSplineCurve PolesCount=3 KnotsCount=2 Degree=2 IsPeriodic=0
    g25: GeomPoint X=-6.48644 Y=-5.99526 Z=0
    g26: GeomPoint X=-6.77343 Y=-8 Z=0
    g27: Circle CenterX=-7.19003 CenterY=-10 CenterZ=0 NormalX=0 NormalY=0 NormalZ=1 AngleXU=0 Radius=1
    g28: Circle CenterX=-7.44407 CenterY=-11.0915 CenterZ=0 NormalX=0 NormalY=0 NormalZ=1 AngleXU=0 Radius=1
    g29: Circle CenterX=-7.79258 CenterY=-12 CenterZ=0 NormalX=0 NormalY=0 NormalZ=1 AngleXU=0 Radius=1
    g30: BSplineCurve PolesCount=3 KnotsCount=2 Degree=2 IsPeriodic=0
    g31: GeomPoint X=-7.19003 Y=-10 Z=0
    g32: GeomPoint X=-7.79258 Y=-12 Z=0
    g33: Circle CenterX=-8.70761 CenterY=-14 CenterZ=0 NormalX=0 NormalY=0 NormalZ=1 AngleXU=0 Radius=1
    g34: Circle CenterX=-9.33087 CenterY=-15.1837 CenterZ=0 NormalX=0 NormalY=0 NormalZ=1 AngleXU=0 Radius=1
    g35: Circle CenterX=-10.1571 CenterY=-16 CenterZ=0 NormalX=0 NormalY=0 NormalZ=1 AngleXU=0 Radius=1
    g36: BSplineCurve PolesCount=3 KnotsCount=2 Degree=2 IsPeriodic=0
    g37: GeomPoint X=-8.70761 Y=-14 Z=0
    g38: GeomPoint X=-10.1571 Y=-16 Z=0
    g39: Circle CenterX=-12.8401 CenterY=-17.6958 CenterZ=0 NormalX=0 NormalY=0 NormalZ=1 AngleXU=0 Radius=1
    g40: Circle CenterX=-13.3521 CenterY=-17.9027 CenterZ=0 NormalX=0 NormalY=0 NormalZ=1 AngleXU=0 Radius=1
    g41: Circle CenterX=-14 CenterY=-18 CenterZ=0 NormalX=0 NormalY=0 NormalZ=1 AngleXU=0 Radius=1
    g42: BSplineCurve PolesCount=3 KnotsCount=2 Degree=2 IsPeriodic=0
    g43: GeomPoint X=-12.8401 Y=-17.6958 Z=0
    g44: GeomPoint X=-14 Y=-18 Z=0
    g45: LineSegment StartX=-6.2 StartY=0 StartZ=0 EndX=-7.2 EndY=0 EndZ=0
    g46: LineSegment StartX=-7.2 StartY=0 StartZ=0 EndX=-7.2 EndY=-2 EndZ=0
    g47: LineSegment StartX=-7.2 StartY=-2 StartZ=0 EndX=-6.2215 EndY=-2 EndZ=0
    g48: LineSegment StartX=-6.32538 StartY=-4 StartZ=0 EndX=-7.65538 EndY=-4 EndZ=0
    g49: LineSegment StartX=-7.65538 StartY=-4 StartZ=0 EndX=-7.65538 EndY=-5.99526 EndZ=0
    g50: LineSegment StartX=-7.65538 StartY=-5.99526 StartZ=0 EndX=-6.48644 EndY=-5.99526 EndZ=0
    g51: LineSegment StartX=-6.77343 StartY=-8 StartZ=0 EndX=-8.43343 EndY=-8 EndZ=0
    g52: LineSegment StartX=-8.43343 StartY=-8 StartZ=0 EndX=-8.43343 EndY=-10 EndZ=0
    g53: LineSegment StartX=-8.43343 StartY=-10 StartZ=0 EndX=-7.19003 EndY=-10 EndZ=0
  constraints (112):
    c: Horizontal(g0)
    c: Distance(g0) = 2
    c: Block(g0)
    c: Vertical(g1)
    c: Coincident(g2,g0)
    c: Vertical(g2)
    c: Block(g2)
    c: Coincident(g6,g2)
    c: Weight(g3) = 1
    c: Equal(g3,g4)
    c: Equal(g3,g5)
    c: InternalAlignment(g3,g6)
    c: InternalAlignment(g4,g6)
    c: InternalAlignment(g5,g6)
    c: InternalAlignment(g7,g6)
    c: InternalAlignment(g8,g6)
    c: Block(g6)
    c: Coincident(g9,g1)
    c: Coincident(g9,g6)
    c: Horizontal(g9)
    c: Vertical(g10)
    c: Block(g10)
    c: Horizontal(g11)
    c: Block(g11)
    c: Coincident(g12,g10)
    c: Horizontal(g12)
    c: Block(g12)
    c: Coincident(g13,g11)
    c: Vertical(g13)
    c: Block(g13)
    c: Coincident(g14,g10)
    c: Horizontal(g14)
    c: Block(g14)
    c: Block(g9)
    c: Block(g1)
    c: Weight(g15) = 1
    c: Equal(g15,g16)
    c: Equal(g15,g17)
    c: InternalAlignment(g15,g18)
    c: InternalAlignment(g16,g18)
    c: InternalAlignment(g17,g18)
    c: InternalAlignment(g19,g18)
    c: InternalAlignment(g20,g18)
    c: Weight(g21) = 1
    c: Equal(g21,g22)
    c: Equal(g21,g23)
    c: InternalAlignment(g21,g24)
    c: InternalAlignment(g22,g24)
    c: InternalAlignment(g23,g24)
    c: InternalAlignment(g25,g24)
    c: InternalAlignment(g26,g24)
    c: Weight(g27) = 1
    c: Equal(g27,g28)
    c: Equal(g27,g29)
    c: Coincident(g30,g14)
    c: InternalAlignment(g27,g30)
    c: InternalAlignment(g28,g30)
    c: InternalAlignment(g29,g30)
    c: InternalAlignment(g31,g30)
    c: InternalAlignment(g32,g30)
    c: Coincident(g36,g12)
    c: Weight(g33) = 1
    c: Equal(g33,g34)
    c: Equal(g33,g35)
    c: Coincident(g36,g11)
    c: InternalAlignment(g33,g36)
    c: InternalAlignment(g34,g36)
    c: InternalAlignment(g35,g36)
    c: InternalAlignment(g37,g36)
    c: InternalAlignment(g38,g36)
    c: Coincident(g42,g13)
    c: Weight(g39) = 1
    c: Equal(g39,g40)
    c: Equal(g39,g41)
    c: Coincident(g42,g1)
    c: InternalAlignment(g39,g42)
    c: InternalAlignment(g40,g42)
    c: InternalAlignment(g41,g42)
    c: InternalAlignment(g43,g42)
    c: InternalAlignment(g44,g42)
    c: Block(g18)
    c: Block(g24)
    c: Block(g30)
    c: Block(g36)
    c: Block(g42)
    c: Horizontal(g45)
    c: Coincident(g45,g0)
    c: Vertical(g46)
    c: Coincident(g46,g45)
    c: Coincident(g47,g46)
    c: Coincident(g47,g18)
    c: Horizontal(g47)
    c: Block(g46)
    c: Coincident(g48,g18)
    c: Horizontal(g48)
    c: Distance(g48) = 1.33
    c: Vertical(g49)
    c: Coincident(g49,g48)
    c: Coincident(g50,g49)
    c: Coincident(g50,g24)
    c: Horizontal(g50)
    c: Tangent(g50,g22)
    c: Horizontal(g51)
    c: Coincident(g51,g24)
    c: Block(g51)
    c: Vertical(g52)
    c: Block(g52)
    c: Coincident(g52,g51)
    c: Coincident(g53,g52)
    c: Coincident(g53,g30)
    c: Horizontal(g53)
    c: Distance(g1) = 8.5
FEATURE [Part::Feature] Face024
  shape: bbox 9.8 x 26.5 x 2e-07 mm, 1 faces, 0 solids (baked)
FEATURE [Part::Revolution] Revolve024
  Angle = 360
  Axis = (0,1,0)
  Base = (0,0,0)
  FaceMakerClass = Part::FaceMakerBullseye
  Placement = pos=(0,0,0) rot=(0,0,1;1.5708rad)
  Solid = false
  Source = -> Face024
  Symmetric = false
FEATURE [Part::Feature] Face025
  shape: bbox 9.8 x 26.5 x 2e-07 mm, 1 faces, 0 solids (baked)
FEATURE [Part::Revolution] Revolve025
  Angle = 360
  Axis = (0,1,0)
  Base = (0,0,0)
  FaceMakerClass = Part::FaceMakerBullseye
  Placement = pos=(0,0,0) rot=(0,0,1;1.5708rad)
  Solid = false
  Source = -> Face025
  Symmetric = false
FEATURE [Part::MultiFuse] Fusion033
  Placement = pos=(-18,19,36) rot=(0,0,1;0rad)
  Shapes = -> [Revolve025,Revolve024]
FEATURE [Part::Cylinder] Cylinder014
  Angle = 360
  AttacherType = Attacher::AttachEngine3D
  Height = 20
  Placement = pos=(0,0,36.15) rot=(0,0,1;0rad)
  Radius = 14.3
FEATURE [Part::Cylinder] Cylinder015
  Angle = 360
  AttacherType = Attacher::AttachEngine3D
  Height = 10
  Placement = pos=(0,0,36.15) rot=(0,0,1;0rad)
  Radius = 4
FEATURE [Part::MultiFuse] Fusion034  label="removeToCreteHoleForPlugHousing004"
  Placement = pos=(-42,19,36) rot=(0,1,0;1.5708rad)
  Shapes = -> [Cylinder014,Cylinder015]
FEATURE [Part::Cut] Cut008  label="top004"
  Base = -> Cut004
  Placement = pos=(-1,0,0) rot=(0,0,1;0rad)
  Tool = -> Fusion034
FEATURE [Part::Box] Box005  label="Cube005"
  AttacherType = Attacher::AttachEngine3D
  Height = 28
  Length = 3
  Placement = pos=(110.7,19,22) rot=(0,0,1;0rad)
  Width = 15.7
FEATURE [Part::Cylinder] Cylinder016
  Angle = 360
  AttacherType = Attacher::AttachEngine3D
  Height = 10
  Placement = pos=(0,0,36.15) rot=(0,0,1;0rad)
  Radius = 4
FEATURE [Part::Cylinder] Cylinder017
  Angle = 360
  AttacherType = Attacher::AttachEngine3D
  Height = 20
  Placement = pos=(0,0,36.15) rot=(0,0,1;0rad)
  Radius = 10.3
FEATURE [Part::MultiFuse] Fusion035  label="removeToCreteHoleForPlugHousing005"
  Placement = pos=(70,19,36) rot=(0,1,0;1.5708rad)
  Shapes = -> [Cylinder017,Cylinder016]
FEATURE [Part::Cut] Cut009  label="plugHousingTab001"
  Base = -> Box005
  Placement = pos=(-107.4,-14,0) rot=(0,0,1;0rad)
  Tool = -> Fusion035
FEATURE [Part::Box] Box006  label="Cube006"
  AttacherType = Attacher::AttachEngine3D
  Height = 28
  Length = 3
  Placement = pos=(110.7,19,22) rot=(0,0,1;0rad)
  Width = 15.7
FEATURE [Part::Cylinder] Cylinder018
  Angle = 360
  AttacherType = Attacher::AttachEngine3D
  Height = 10
  Placement = pos=(0,0,36.15) rot=(0,0,1;0rad)
  Radius = 4
FEATURE [Part::Cylinder] Cylinder019
  Angle = 360
  AttacherType = Attacher::AttachEngine3D
  Height = 20
  Placement = pos=(0,0,36.15) rot=(0,0,1;0rad)
  Radius = 10.3
FEATURE [Part::MultiFuse] Fusion036  label="removeToCreteHoleForPlugHousing006"
  Placement = pos=(70,19,36) rot=(0,1,0;1.5708rad)
  Shapes = -> [Cylinder019,Cylinder018]
FEATURE [Part::Cut] Cut010  label="plugHousingTab002"
  Base = -> Box006
  Placement = pos=(-107.4,-14,0) rot=(0,0,1;0rad)
  Tool = -> Fusion036
FEATURE [Part::MultiFuse] Fusion037
  Placement = pos=(9.6,23,0) rot=(0,0,1;3.14159rad)
  Shapes = -> [Cut009,Cut010]
FEATURE [Part::Box] Box  label="Cube"
  AttacherType = Attacher::AttachEngine3D
  Height = 10
  Length = 3
  Placement = pos=(3.3,4,12) rot=(0,0,1;0rad)
  Width = 10
FEATURE [Part::Fillet] Fillet004
  Base = -> Fusion028
  Edges = 1 edges r=2: [Edge25]
FEATURE [Part::Fillet] Fillet005  label="plugHousing046"
  Base = -> Fillet004
  Edges = 1 edges r=2: [Edge8]
FEATURE [Part::Fillet] Fillet006
  Base = -> Box
  Edges = 1 edges r=2: [Edge11]
FEATURE [Part::Box] Box007  label="Cube007"
  AttacherType = Attacher::AttachEngine3D
  Height = 10
  Length = 3
  Placement = pos=(3.3,4,50) rot=(0,0,1;0rad)
  Width = 10
FEATURE [Part::Fillet] Fillet007
  Base = -> Box007
  Edges = 1 edges r=2: [Edge12]
FEATURE [Part::Box] Box008  label="Cube008"
  AttacherType = Attacher::AttachEngine3D
  Height = 28
  Length = 4
  Placement = pos=(5,0,22) rot=(0,0,1;0rad)
  Width = 10
FEATURE [Part::Fillet] Fillet008
  Base = -> Box008
  Edges = 1 edges r=1: [Edge7]
FEATURE [Part::Fillet] Fillet009
  Base = -> Fillet008
  Edges = 1 edges r=2: [Edge5]
FEATURE [Part::Fillet] Fillet010
  Base = -> Fillet009
  Edges = 1 edges r=2: [Edge2]
FEATURE [Sketcher::SketchObject] Sketch009  label="topSketch003"
  FullyConstrained = true
  sketch-geometry (4):
    g0: LineSegment StartX=16.8446 StartY=31.512 StartZ=0 EndX=16.3251 EndY=34.4666 EndZ=0
    g1: ArcOfCircle CenterX=19 CenterY=19.2524 CenterZ=0 NormalX=0 NormalY=0 NormalZ=1 AngleXU=0 Radius=15.4476 StartAngle=1.74483 EndAngle=2.72717
    g2: ArcOfCircle CenterX=19 CenterY=19.2524 CenterZ=0 NormalX=0 NormalY=0 NormalZ=1 AngleXU=0 Radius=12.4476 StartAngle=1.74483 EndAngle=2.73189
    g3: LineSegment StartX=4.86004 StartY=25.4725 StartZ=0 EndX=7.58253 EndY=24.2107 EndZ=0
  constraints (7):
    c: Block(g0)
    c: Coincident(g1,g0)
    c: Coincident(g2,g0)
    c: Coincident(g3,g1)
    c: Coincident(g3,g2)
    c: Block(g1)
    c: Block(g2)
FEATURE [Part::Extrusion] Extrude008
  Base = -> Sketch009
  Dir = (0,0,1)
  DirMode = 2
  FaceMakerClass = Part::FaceMakerBullseye
  LengthFwd = 10
  LengthRev = 0
  Placement = pos=(0,0,31) rot=(0,0,1;0rad)
  Solid = true
  Symmetric = false
FEATURE [Part::Cylinder] Cylinder020
  Angle = 360
  AttacherType = Attacher::AttachEngine3D
  Height = 20
  Placement = pos=(0,0,36.15) rot=(0,0,1;0rad)
  Radius = 8.2
FEATURE [Part::Cylinder] Cylinder021
  Angle = 360
  AttacherType = Attacher::AttachEngine3D
  Height = 10
  Placement = pos=(0,0,36.15) rot=(0,0,1;0rad)
  Radius = 4
FEATURE [Part::MultiFuse] Fusion038  label="removeToCreteHoleForPlugHousing007"
  Placement = pos=(-42,19,36) rot=(0,1,0;1.5708rad)
  Shapes = -> [Cylinder020,Cylinder021]
FEATURE [Part::Cut] Cut011
  Base = -> Extrude008
  Tool = -> Fusion038
FEATURE [Part::Fillet] Fillet011
  Base = -> Cut011
  Edges = 1 edges r=2: [Edge1]
FEATURE [Part::Fillet] Fillet012
  Base = -> Fillet011
  Edges = 1 edges r=2.5: [Edge1]
FEATURE [Part::Fillet] Fillet013
  Base = -> Fillet012
  Edges = 1 edges r=2.5: [Edge2]
FEATURE [Part::Box] Box010  label="Cube010"
  AttacherType = Attacher::AttachEngine3D
  Height = 16
  Length = 8
  Placement = pos=(12.7,31.52,28) rot=(0,0,1;0rad)
  Width = 4
FEATURE [Sketcher::SketchObject] Sketch010  label="topSketch004"
  FullyConstrained = true
  sketch-geometry (4):
    g0: LineSegment StartX=16.8446 StartY=31.512 StartZ=0 EndX=16.3251 EndY=34.4666 EndZ=0
    g1: ArcOfCircle CenterX=19 CenterY=19.2524 CenterZ=0 NormalX=0 NormalY=0 NormalZ=1 AngleXU=0 Radius=15.4476 StartAngle=1.74483 EndAngle=2.72717
    g2: ArcOfCircle CenterX=19 CenterY=19.2524 CenterZ=0 NormalX=0 NormalY=0 NormalZ=1 AngleXU=0 Radius=12.4476 StartAngle=1.74483 EndAngle=2.73189
    g3: LineSegment StartX=4.86004 StartY=25.4725 StartZ=0 EndX=7.58253 EndY=24.2107 EndZ=0
  constraints (7):
    c: Block(g0)
    c: Coincident(g1,g0)
    c: Coincident(g2,g0)
    c: Coincident(g3,g1)
    c: Coincident(g3,g2)
    c: Block(g1)
    c: Block(g2)
FEATURE [Part::Cylinder] Cylinder022
  Angle = 360
  AttacherType = Attacher::AttachEngine3D
  Height = 10
  Placement = pos=(0,0,36.15) rot=(0,0,1;0rad)
  Radius = 4
FEATURE [Sketcher::SketchObject] Sketch011  label="topSketch005"
  FullyConstrained = true
  sketch-geometry (4):
    g0: LineSegment StartX=16.8446 StartY=31.512 StartZ=0 EndX=16.3251 EndY=34.4666 EndZ=0
    g1: ArcOfCircle CenterX=19 CenterY=19.2524 CenterZ=0 NormalX=0 NormalY=0 NormalZ=1 AngleXU=0 Radius=15.4476 StartAngle=1.74483 EndAngle=2.72717
    g2: ArcOfCircle CenterX=19 CenterY=19.2524 CenterZ=0 NormalX=0 NormalY=0 NormalZ=1 AngleXU=0 Radius=12.4476 StartAngle=1.74483 EndAngle=2.73189
    g3: LineSegment StartX=4.86004 StartY=25.4725 StartZ=0 EndX=7.58253 EndY=24.2107 EndZ=0
  constraints (7):
    c: Block(g0)
    c: Coincident(g1,g0)
    c: Coincident(g2,g0)
    c: Coincident(g3,g1)
    c: Coincident(g3,g2)
    c: Block(g1)
    c: Block(g2)
FEATURE [Part::Extrusion] Extrude010
  Base = -> Sketch011
  Dir = (0,0,1)
  DirMode = 2
  FaceMakerClass = Part::FaceMakerBullseye
  LengthFwd = 10.6
  LengthRev = 0
  Placement = pos=(0,0,31) rot=(0,0,1;0rad)
  Solid = true
  Symmetric = false
FEATURE [Part::Cylinder] Cylinder023
  Angle = 360
  AttacherType = Attacher::AttachEngine3D
  Height = 20
  Placement = pos=(0,0,36.15) rot=(0,0,1;0rad)
  Radius = 8.2
FEATURE [Part::MultiFuse] Fusion039  label="removeToCreteHoleForPlugHousing008"
  Placement = pos=(-42,19,36) rot=(0,1,0;1.5708rad)
  Shapes = -> [Cylinder023,Cylinder022]
FEATURE [Part::Cut] Cut012
  Base = -> Extrude010
  Placement = pos=(0,0,-0.3) rot=(0,0,1;0rad)
  Tool = -> Fusion039
FEATURE [Part::Cut] Cut013
  Base = -> Box010
  Tool = -> Cut012
FEATURE [Part::Fillet] Fillet014
  Base = -> Cut013
  Edges = 1 edges r=0.7: [Edge13]
FEATURE [Part::Fillet] Fillet015
  Base = -> Fillet014
  Edges = 1 edges r=0.7: [Edge13]
FEATURE [Part::Fillet] Fillet016
  Base = -> Fillet015
  Edges = 1 edges r=0.7: [Edge16]
FEATURE [Part::Fillet] Fillet017
  Base = -> Fillet016
  Edges = 1 edges r=0.7: [Edge11]
FEATURE [Part::Fillet] Fillet018
  Base = -> Fillet017
  Edges = 1 edges r=0.7: [Edge10]
FEATURE [Part::Fillet] Fillet019
  Base = -> Fillet018
  Edges = 1 edges r=1.2: [Edge5]
FEATURE [Part::Fillet] Fillet020
  Base = -> Fillet019
  Edges = 1 edges r=1.2: [Edge12]
FEATURE [Part::Fillet] Fillet021
  Base = -> Fillet020
  Edges = 1 edges r=2: [Edge1]
  Placement = pos=(0.3,0,0) rot=(0,0,1;0rad)
FEATURE [Part::MultiFuse] Fusion040  label="top005"
  Shapes = -> [Cut008,Fillet021]
FEATURE [Part::MultiFuse] Fusion041  label="wireHolder"
  Shapes = -> [Fusion033,Fillet013]
FEATURE [Part::MultiFuse] Fusion042
  Shapes = -> [Fillet007,Fusion041]
FEATURE [Part::MultiFuse] Fusion043  label="wireHolder001"
  Shapes = -> [Fusion042,Fillet010]
FEATURE [Part::MultiFuse] Fusion044  label="wireHolder002"
  Shapes = -> [Fillet006,Fusion037,Fusion043]
FEATURE [Part::Feature] Face026
  shape: bbox 11 x 6 x 2e-07 mm, 1 faces, 0 solids (baked)
FEATURE [Part::Revolution] Revolve026
  Angle = 360
  Axis = (0,1,0)
  Base = (0,0,0)
  FaceMakerClass = Part::FaceMakerBullseye
  Placement = pos=(30.3,-1,19.7) rot=(0,0,1;0rad)
  Solid = false
  Source = -> Face026
  Symmetric = false
FEATURE [Sketcher::SketchObject] Sketch013  label="topSketch006"
  FullyConstrained = true
  sketch-geometry (13):
    g0: LineSegment StartX=117 StartY=19 StartZ=0 EndX=117 EndY=38 EndZ=0
    g1: ArcOfCircle CenterX=98 CenterY=19 CenterZ=0 NormalX=0 NormalY=0 NormalZ=1 AngleXU=0 Radius=19 StartAngle=5.7297 EndAngle=6.28319
    g2: LineSegment StartX=0 StartY=3 StartZ=0 EndX=0 EndY=19 EndZ=0
    g3: LineSegment StartX=19 StartY=38 StartZ=0 EndX=117 EndY=38 EndZ=0
    g4: ArcOfCircle CenterX=19 CenterY=19 CenterZ=0 NormalX=0 NormalY=0 NormalZ=1 AngleXU=0 Radius=19 StartAngle=1.5708 EndAngle=3.14159
    g5: ArcOfCircle CenterX=19 CenterY=19 CenterZ=0 NormalX=0 NormalY=0 NormalZ=1 AngleXU=0 Radius=16 StartAngle=1.5708 EndAngle=3.14159
    g6: ArcOfCircle CenterX=98 CenterY=19 CenterZ=0 NormalX=0 NormalY=0 NormalZ=1 AngleXU=0 Radius=16 StartAngle=5.60905 EndAngle=6.28319
    g7: LineSegment StartX=114 StartY=19 StartZ=0 EndX=114 EndY=35 EndZ=0
    g8: LineSegment StartX=110.5 StartY=9.01251 StartZ=0 EndX=114.163 EndY=9.01251 EndZ=0
    g9: LineSegment StartX=114 StartY=35 StartZ=0 EndX=19 EndY=35 EndZ=0
    g10: LineSegment StartX=0 StartY=3 StartZ=0 EndX=0 EndY=0 EndZ=0
    g11: LineSegment StartX=3 StartY=0 StartZ=0 EndX=0 EndY=0 EndZ=0
    g12: LineSegment StartX=3 StartY=19 StartZ=0 EndX=3 EndY=0 EndZ=0
  constraints (33):
    c: Vertical(g0)
    c: Distance(g0) = 19
    c: Block(g0)
    c: Coincident(g1,g0)
    c: Block(g1)
    c: Vertical(g2)
    c: Block(g2)
    c: Coincident(g3,g0)
    c: Horizontal(g3)
    c: Distance(g3) = 98
    c: Coincident(g4,g3)
    c: Coincident(g4,g2)
    c: Block(g4)
    c: Coincident(g5,g4)
    c: Coincident(g6,g1)
    c: Block(g6)
    c: Block(g5)
    c: Coincident(g7,g6)
    c: Vertical(g7)
    c: Coincident(g8,g6)
    c: Coincident(g8,g1)
    c: Coincident(g9,g7)
    c: Coincident(g9,g5)
    c: Horizontal(g9)
    c: Tangent(g9,g5)
    c: Coincident(g10,g2)
    c: Distance(g10) = 3
    c: Vertical(g10)
    c: Coincident(g11,g10)
    c: Horizontal(g11)
    c: Coincident(g12,g5)
    c: Coincident(g12,g11)
    c: Vertical(g12)
FEATURE [Part::Extrusion] Extrude011  label="top006"
  Base = -> Sketch013
  Dir = (0,0,1)
  DirMode = 2
  FaceMakerClass = Part::FaceMakerBullseye
  LengthFwd = 72
  LengthRev = 0
  Solid = true
  Symmetric = false
FEATURE [Sketcher::SketchObject] Sketch014
  FullyConstrained = true
  MapMode = 3
  Placement = pos=(0,0,0) rot=(1,0,0;1.5708rad)
  Support = -> [Extrude011]
  sketch-geometry (8):
    g0: Circle CenterX=80.351 CenterY=-67.6202 CenterZ=0 NormalX=0 NormalY=0 NormalZ=1 AngleXU=0 Radius=2
    g1: Circle CenterX=80.351 CenterY=-67.6202 CenterZ=0 NormalX=0 NormalY=0 NormalZ=1 AngleXU=0 Radius=3
    g2: Circle CenterX=80.351 CenterY=-4.92017 CenterZ=0 NormalX=0 NormalY=0 NormalZ=1 AngleXU=0 Radius=2
    g3: Circle CenterX=80.351 CenterY=-4.92017 CenterZ=0 NormalX=0 NormalY=0 NormalZ=1 AngleXU=0 Radius=3
    g4: Circle CenterX=23.851 CenterY=-4.92017 CenterZ=0 NormalX=0 NormalY=0 NormalZ=1 AngleXU=0 Radius=2
    g5: Circle CenterX=23.851 CenterY=-4.92017 CenterZ=0 NormalX=0 NormalY=0 NormalZ=1 AngleXU=0 Radius=3
    g6: Circle CenterX=23.851 CenterY=-67.6202 CenterZ=0 NormalX=0 NormalY=0 NormalZ=1 AngleXU=0 Radius=2
    g7: Circle CenterX=23.851 CenterY=-67.6202 CenterZ=0 NormalX=0 NormalY=0 NormalZ=1 AngleXU=0 Radius=3
  constraints (8):
    c: Block(g3)
    c: Block(g2)
    c: Block(g1)
    c: Block(g0)
    c: Block(g6)
    c: Block(g7)
    c: Block(g4)
    c: Block(g5)
FEATURE [Part::Feature] Face027
  shape: bbox 11 x 6 x 2e-07 mm, 1 faces, 0 solids (baked)
FEATURE [Part::Revolution] Revolve027
  Angle = 360
  Axis = (0,1,0)
  Base = (0,0,0)
  FaceMakerClass = Part::FaceMakerBullseye
  Placement = pos=(30.3,-1,51.7) rot=(0,0,1;0rad)
  Solid = false
  Source = -> Face027
  Symmetric = false
FEATURE [Part::Feature] Face028
  shape: bbox 11 x 6 x 2e-07 mm, 1 faces, 0 solids (baked)
FEATURE [Part::Revolution] Revolve028
  Angle = 360
  Axis = (0,1,0)
  Base = (0,0,0)
  FaceMakerClass = Part::FaceMakerBullseye
  Placement = pos=(62.3,-1,19.7) rot=(0,0,1;0rad)
  Solid = false
  Source = -> Face028
  Symmetric = false
FEATURE [Part::Feature] Face029
  shape: bbox 11 x 6 x 2e-07 mm, 1 faces, 0 solids (baked)
FEATURE [Part::Revolution] Revolve029
  Angle = 360
  Axis = (0,1,0)
  Base = (0,0,0)
  FaceMakerClass = Part::FaceMakerBullseye
  Placement = pos=(62.3,-1,51.7) rot=(0,0,1;0rad)
  Solid = false
  Source = -> Face029
  Symmetric = false
FEATURE [Part::Feature] Wire
  shape: bbox 11 x 5.2 x 2e-07 mm, 0 faces, 0 solids (baked)
FEATURE [Part::Revolution] Revolve030
  Angle = 360
  Axis = (0,1,0)
  Base = (0,0,0)
  FaceMakerClass = Part::FaceMakerBullseye
  Placement = pos=(30.3,38,19.7) rot=(0,0,1;0rad)
  Solid = true
  Source = -> Wire
  Symmetric = false
FEATURE [Part::Feature] Wire001
  shape: bbox 11 x 5.2 x 2e-07 mm, 0 faces, 0 solids (baked)
FEATURE [Part::Revolution] Revolve031
  Angle = 360
  Axis = (0,1,0)
  Base = (0,0,0)
  FaceMakerClass = Part::FaceMakerBullseye
  Placement = pos=(30.3,38,51.7) rot=(0,0,1;0rad)
  Solid = true
  Source = -> Wire001
  Symmetric = false
FEATURE [Part::Feature] Wire002
  shape: bbox 11 x 5.2 x 2e-07 mm, 0 faces, 0 solids (baked)
FEATURE [Part::Revolution] Revolve032
  Angle = 360
  Axis = (0,1,0)
  Base = (0,0,0)
  FaceMakerClass = Part::FaceMakerBullseye
  Placement = pos=(62.3,38,51.7) rot=(0,0,1;0rad)
  Solid = true
  Source = -> Wire002
  Symmetric = false
FEATURE [Part::Feature] Wire003
  shape: bbox 11 x 5.2 x 2e-07 mm, 0 faces, 0 solids (baked)
FEATURE [Part::Revolution] Revolve033
  Angle = 360
  Axis = (0,1,0)
  Base = (0,0,0)
  FaceMakerClass = Part::FaceMakerBullseye
  Placement = pos=(62.3,38,19.7) rot=(0,0,1;0rad)
  Solid = true
  Source = -> Wire003
  Symmetric = false
FEATURE [Part::MultiFuse] Fusion045  label="altRandScrewHousing"
  Shapes = -> [Revolve029,Revolve027,Revolve028,Revolve026]
FEATURE [Part::MultiFuse] Fusion046  label="fanScrewHousing"
  Shapes = -> [Revolve033,Revolve032,Revolve031,Revolve030]
FEATURE [Sketcher::SketchObject] Sketch015
  FullyConstrained = true
  sketch-geometry (17):
    g0: Circle CenterX=-3.5 CenterY=23.5 CenterZ=0 NormalX=0 NormalY=0 NormalZ=1 AngleXU=0 Radius=1
    g1: Circle CenterX=-1 CenterY=15.25 CenterZ=0 NormalX=0 NormalY=0 NormalZ=1 AngleXU=0 Radius=1
    g2: Circle CenterX=-3.5 CenterY=7 CenterZ=0 NormalX=0 NormalY=0 NormalZ=1 AngleXU=0 Radius=1
    g3: BSplineCurve PolesCount=3 KnotsCount=2 Degree=2 IsPeriodic=0
    g4: GeomPoint X=-3.5 Y=23.5 Z=0
    g5: GeomPoint X=-3.5 Y=7 Z=0
    g6: Circle CenterX=-4.8 CenterY=30.5 CenterZ=0 NormalX=0 NormalY=0 NormalZ=1 AngleXU=0 Radius=1
    g7: Circle CenterX=-3.5 CenterY=30.5 CenterZ=0 NormalX=0 NormalY=0 NormalZ=1 AngleXU=0 Radius=1
    g8: Circle CenterX=-3.5 CenterY=29.2 CenterZ=0 NormalX=0 NormalY=0 NormalZ=1 AngleXU=0 Radius=1
    g9: BSplineCurve PolesCount=3 KnotsCount=2 Degree=2 IsPeriodic=0
    g10: GeomPoint X=-4.8 Y=30.5 Z=0
    g11: GeomPoint X=-3.5 Y=29.2 Z=0
    g12: LineSegment StartX=-3.5 StartY=29.2 StartZ=0 EndX=-3.5 EndY=23.5 EndZ=0
    g13: LineSegment StartX=-4.8 StartY=30.5 StartZ=0 EndX=0 EndY=30.5 EndZ=0
    g14: LineSegment StartX=-3.5 StartY=0.3 StartZ=0 EndX=0 EndY=0.3 EndZ=0
    g15: LineSegment StartX=-3.5 StartY=0.3 StartZ=0 EndX=-3.5 EndY=7 EndZ=0
    g16: LineSegment StartX=0 StartY=0.3 StartZ=0 EndX=0 EndY=30.5 EndZ=0
  constraints (33):
    c: Weight(g0) = 1
    c: Equal(g0,g1)
    c: Equal(g0,g2)
    c: InternalAlignment(g0,g3)
    c: InternalAlignment(g1,g3)
    c: InternalAlignment(g2,g3)
    c: InternalAlignment(g4,g3)
    c: InternalAlignment(g5,g3)
    c: Block(g3)
    c: Weight(g6) = 1
    c: Equal(g6,g7)
    c: Equal(g6,g8)
    c: InternalAlignment(g6,g9)
    c: InternalAlignment(g7,g9)
    c: InternalAlignment(g8,g9)
    c: InternalAlignment(g10,g9)
    c: InternalAlignment(g11,g9)
    c: Block(g9)
    c: Coincident(g12,g9)
    c: Coincident(g12,g3)
    c: Vertical(g12)
    c: Coincident(g13,g9)
    c: Horizontal(g13)
    c: Distance(g13) = 4.8
    c: Horizontal(g14)
    c: Block(g14)
    c: Coincident(g15,g14)
    c: Coincident(g15,g3)
    c: Vertical(g15)
    c: Coincident(g16,g14)
    c: Coincident(g16,g13)
    c: Vertical(g16)
    c: Tangent(g16,g1)
FEATURE [Sketcher::SketchObject] Sketch016
  FullyConstrained = true
  sketch-geometry (16):
    g0: Circle CenterX=-3.5 CenterY=23.5 CenterZ=0 NormalX=0 NormalY=0 NormalZ=1 AngleXU=0 Radius=1
    g1: Circle CenterX=-1 CenterY=15.25 CenterZ=0 NormalX=0 NormalY=0 NormalZ=1 AngleXU=0 Radius=1
    g2: Circle CenterX=-3.5 CenterY=7 CenterZ=0 NormalX=0 NormalY=0 NormalZ=1 AngleXU=0 Radius=1
    g3: BSplineCurve PolesCount=3 KnotsCount=2 Degree=2 IsPeriodic=0
    g4: GeomPoint X=-3.5 Y=23.5 Z=0
    g5: GeomPoint X=-3.5 Y=7 Z=0
    g6: LineSegment StartX=-3.5 StartY=28.2 StartZ=0 EndX=-3.5 EndY=23.5 EndZ=0
    g7: LineSegment StartX=0 StartY=29.5 StartZ=0 EndX=0 EndY=30 EndZ=0
    g8: LineSegment StartX=-3.5 StartY=28.2 StartZ=0 EndX=-3.5 EndY=30 EndZ=0
    g9: LineSegment StartX=0 StartY=30 StartZ=0 EndX=0 EndY=30.5 EndZ=0
    g10: LineSegment StartX=0 StartY=30.5 StartZ=0 EndX=-3.5 EndY=30.5 EndZ=0
    g11: LineSegment StartX=-3.5 StartY=30.5 StartZ=0 EndX=-3.5 EndY=30 EndZ=0
    g12: LineSegment StartX=0 StartY=29.5 StartZ=0 EndX=0 EndY=5 EndZ=0
    g13: LineSegment StartX=-3.5 StartY=0.3 StartZ=0 EndX=-3.5 EndY=7 EndZ=0
    g14: LineSegment StartX=-3.5 StartY=0.3 StartZ=0 EndX=0 EndY=0.3 EndZ=0
    g15: LineSegment StartX=0 StartY=5 StartZ=0 EndX=0 EndY=0.3 EndZ=0
  constraints (39):
    c: Weight(g0) = 1
    c: Equal(g0,g1)
    c: Equal(g0,g2)
    c: InternalAlignment(g0,g3)
    c: InternalAlignment(g1,g3)
    c: InternalAlignment(g2,g3)
    c: InternalAlignment(g4,g3)
    c: InternalAlignment(g5,g3)
    c: Block(g3)
    c: Coincident(g6,g3)
    c: Vertical(g6)
    c: Vertical(g7)
    c: Distance(g7) = 0.5
    c: Coincident(g8,g6)
    c: Vertical(g8)
    c: Block(g6)
    c: Block(g7)
    c: Vertical(g9)
    c: Equal(g7,g9) = 0.5
    c: Block(g9)
    c: Coincident(g9,g7)
    c: Horizontal(g10)
    c: Coincident(g10,g9)
    c: Coincident(g11,g10)
    c: Coincident(g11,g8)
    c: Vertical(g11)
    c: Block(g11)
    c: Coincident(g12,g7)
    c: Vertical(g12)
    c: Coincident(g13,g3)
    c: Vertical(g13)
    c: Distance(g13) = 6.7
    c: Coincident(g14,g13)
    c: Horizontal(g14)
    c: Block(g14)
    c: Coincident(g15,g12)
    c: Coincident(g15,g14)
    c: Vertical(g15)
    c: Block(g15)
FEATURE [Sketcher::SketchObject] Sketch017
  FullyConstrained = true
  sketch-geometry (11):
    g0: LineSegment StartX=-3.5 StartY=1e-16 StartZ=0 EndX=-1.6 EndY=1e-16 EndZ=0
    g1: LineSegment StartX=-1.6 StartY=1e-16 StartZ=0 EndX=-1.6 EndY=1.5 EndZ=0
    g2: LineSegment StartX=-3.5 StartY=1.5 StartZ=0 EndX=-1.6 EndY=1.5 EndZ=0
    g3: LineSegment StartX=-3.5 StartY=1e-16 StartZ=0 EndX=-4.8 EndY=1e-16 EndZ=0
    g4: Circle CenterX=-3.5 CenterY=1.3 CenterZ=0 NormalX=0 NormalY=0 NormalZ=1 AngleXU=0 Radius=1
    g5: Circle CenterX=-3.5 CenterY=1e-16 CenterZ=0 NormalX=0 NormalY=0 NormalZ=1 AngleXU=0 Radius=1
    g6: Circle CenterX=-4.8 CenterY=1e-16 CenterZ=0 NormalX=0 NormalY=0 NormalZ=1 AngleXU=0 Radius=1
    g7: BSplineCurve PolesCount=3 KnotsCount=2 Degree=2 IsPeriodic=0
    g8: GeomPoint X=-3.5 Y=1.3 Z=0
    g9: GeomPoint X=-4.8 Y=1e-16 Z=0
    g10: LineSegment StartX=-3.5 StartY=1.3 StartZ=0 EndX=-3.5 EndY=1.5 EndZ=0
  constraints (24):
    c: Horizontal(g0)
    c: Distance(g0) = 1.9
    c: Block(g0)
    c: Coincident(g1,g0)
    c: Vertical(g1)
    c: Coincident(g2,g1)
    c: Horizontal(g2)
    c: Coincident(g3,g0)
    c: Horizontal(g3)
    c: Distance(g3) = 1.3
    c: Weight(g4) = 1
    c: Equal(g4,g5)
    c: Coincident(g5,g0)
    c: Equal(g4,g6)
    c: Coincident(g7,g3)
    c: InternalAlignment(g4,g7)
    c: InternalAlignment(g5,g7)
    c: InternalAlignment(g6,g7)
    c: InternalAlignment(g8,g7)
    c: InternalAlignment(g9,g7)
    c: Coincident(g10,g7)
    c: Coincident(g10,g2)
    c: Vertical(g10)
    c: Block(g10)
FEATURE [Part::Feature] Face035
  shape: bbox 3.2 x 1.5 x 2e-07 mm, 1 faces, 0 solids (baked)
FEATURE [Part::Revolution] Revolve039  label="backCaseScrewRetainer"
  Angle = 360
  Axis = (0,1,0)
  Base = (0,0,0)
  FaceMakerClass = Part::FaceMakerBullseye
  Placement = pos=(12.5,3,62) rot=(0,0,1;0rad)
  Solid = false
  Source = -> Face035
  Symmetric = false
FEATURE [Part::Feature] Face036
  shape: bbox 3.2 x 1.5 x 2e-07 mm, 1 faces, 0 solids (baked)
FEATURE [Part::Feature] Face039
  shape: bbox 4.8 x 30.2 x 2e-07 mm, 1 faces, 0 solids (baked)
FEATURE [Part::Revolution] Revolve043  label="frontCaseScrewPost002"
  Angle = 360
  Axis = (0,1,0)
  Base = (0,0,0)
  FaceMakerClass = Part::FaceMakerBullseye
  Placement = pos=(89.5,4.5,3.5) rot=(0,0,1;0rad)
  Solid = false
  Source = -> Face039
  Symmetric = false
FEATURE [Part::Feature] Face042
  shape: bbox 4.8 x 30.2 x 2e-07 mm, 1 faces, 0 solids (baked)
FEATURE [Part::Revolution] Revolve046  label="frontCaseScrewPost003"
  Angle = 360
  Axis = (0,1,0)
  Base = (0,0,0)
  FaceMakerClass = Part::FaceMakerBullseye
  Placement = pos=(89.5,4.5,68.5) rot=(0,0,1;0rad)
  Solid = false
  Source = -> Face042
  Symmetric = false
FEATURE [Part::Feature] Face043
  shape: bbox 3.2 x 1.5 x 2e-07 mm, 1 faces, 0 solids (baked)
FEATURE [Part::Revolution] Revolve047  label="frontCaseScrewRetainer002"
  Angle = 360
  Axis = (0,1,0)
  Base = (0,0,0)
  FaceMakerClass = Part::FaceMakerBullseye
  Placement = pos=(89.5,3,68.5) rot=(0,0,1;0rad)
  Solid = false
  Source = -> Face043
  Symmetric = false
FEATURE [Part::Feature] Face044
  shape: bbox 3.2 x 1.5 x 2e-07 mm, 1 faces, 0 solids (baked)
FEATURE [Part::Revolution] Revolve048  label="frontCaseScrewRetainer003"
  Angle = 360
  Axis = (0,1,0)
  Base = (0,0,0)
  FaceMakerClass = Part::FaceMakerBullseye
  Placement = pos=(89.5,3,3.5) rot=(0,0,1;0rad)
  Solid = false
  Source = -> Face044
  Symmetric = false
FEATURE [App::MeasureDistance] Distance002  label="Distance: 1.67 mm"
  Distance = 1.66921
  P1 = (99.2361,4.7524,71.7)
  P2 = (99.2347,6.42161,71.7)
FEATURE [Sketcher::SketchObject] Sketch018
  FullyConstrained = true
  sketch-geometry (7):
    g0: LineSegment StartX=0 StartY=0 StartZ=0 EndX=0 EndY=6 EndZ=0
    g1: Circle CenterX=0 CenterY=0 CenterZ=0 NormalX=0 NormalY=0 NormalZ=1 AngleXU=0 Radius=1
    g2: Circle CenterX=8 CenterY=6 CenterZ=0 NormalX=0 NormalY=0 NormalZ=1 AngleXU=0 Radius=1
    g3: BSplineCurve PolesCount=3 KnotsCount=2 Degree=2 IsPeriodic=0
    g4: GeomPoint X=0 Y=0 Z=0
    g5: GeomPoint X=8 Y=6 Z=0
    g6: LineSegment StartX=0 StartY=6 StartZ=0 EndX=8 EndY=6 EndZ=0
  constraints (14):
    c: Coincident(g0,g-1)
    c: Distance(g0) = 6
    c: Vertical(g0)
    c: Coincident(g3,g0)
    c: Weight(g1) = 1
    c: Equal(g1,g2)
    c: InternalAlignment(g1,g3)
    c: InternalAlignment(g2,g3)
    c: InternalAlignment(g4,g3)
    c: InternalAlignment(g5,g3)
    c: Block(g3)
    c: Coincident(g6,g0)
    c: Coincident(g6,g3)
    c: Horizontal(g6)
FEATURE [Part::Extrusion] Extrude012  label="caseScrewPillarBracket"
  Base = -> Sketch018
  Dir = (0,0,1)
  DirMode = 2
  FaceMakerClass = Part::FaceMakerBullseye
  LengthFwd = 2.4
  LengthRev = 0
  Placement = pos=(15.76,29,8.8) rot=(0,1,0;0rad)
  Solid = true
  Symmetric = false
FEATURE [Sketcher::SketchObject] Sketch019
  FullyConstrained = true
  sketch-geometry (7):
    g0: LineSegment StartX=0 StartY=0 StartZ=0 EndX=0 EndY=6 EndZ=0
    g1: Circle CenterX=0 CenterY=0 CenterZ=0 NormalX=0 NormalY=0 NormalZ=1 AngleXU=0 Radius=1
    g2: Circle CenterX=8 CenterY=6 CenterZ=0 NormalX=0 NormalY=0 NormalZ=1 AngleXU=0 Radius=1
    g3: BSplineCurve PolesCount=3 KnotsCount=2 Degree=2 IsPeriodic=0
    g4: GeomPoint X=0 Y=0 Z=0
    g5: GeomPoint X=8 Y=6 Z=0
    g6: LineSegment StartX=0 StartY=6 StartZ=0 EndX=8 EndY=6 EndZ=0
  constraints (14):
    c: Coincident(g0,g-1)
    c: Distance(g0) = 6
    c: Vertical(g0)
    c: Coincident(g3,g0)
    c: Weight(g1) = 1
    c: Equal(g1,g2)
    c: InternalAlignment(g1,g3)
    c: InternalAlignment(g2,g3)
    c: InternalAlignment(g4,g3)
    c: InternalAlignment(g5,g3)
    c: Block(g3)
    c: Coincident(g6,g0)
    c: Coincident(g6,g3)
    c: Horizontal(g6)
FEATURE [Part::Extrusion] Extrude013  label="caseScrewPillarBracket001"
  Base = -> Sketch019
  Dir = (0,0,1)
  DirMode = 2
  FaceMakerClass = Part::FaceMakerBullseye
  LengthFwd = 2.4
  LengthRev = 0
  Placement = pos=(15.76,29,60.8) rot=(0,0,1;0rad)
  Solid = true
  Symmetric = false
FEATURE [Sketcher::SketchObject] Sketch020
  FullyConstrained = true
  sketch-geometry (7):
    g0: LineSegment StartX=0 StartY=0 StartZ=0 EndX=0 EndY=6 EndZ=0
    g1: Circle CenterX=0 CenterY=0 CenterZ=0 NormalX=0 NormalY=0 NormalZ=1 AngleXU=0 Radius=1
    g2: Circle CenterX=8 CenterY=6 CenterZ=0 NormalX=0 NormalY=0 NormalZ=1 AngleXU=0 Radius=1
    g3: BSplineCurve PolesCount=3 KnotsCount=2 Degree=2 IsPeriodic=0
    g4: GeomPoint X=0 Y=0 Z=0
    g5: GeomPoint X=8 Y=6 Z=0
    g6: LineSegment StartX=0 StartY=6 StartZ=0 EndX=8 EndY=6 EndZ=0
  constraints (14):
    c: Coincident(g0,g-1)
    c: Distance(g0) = 6
    c: Vertical(g0)
    c: Coincident(g3,g0)
    c: Weight(g1) = 1
    c: Equal(g1,g2)
    c: InternalAlignment(g1,g3)
    c: InternalAlignment(g2,g3)
    c: InternalAlignment(g4,g3)
    c: InternalAlignment(g5,g3)
    c: Block(g3)
    c: Coincident(g6,g0)
    c: Coincident(g6,g3)
    c: Horizontal(g6)
FEATURE [Part::Extrusion] Extrude014  label="caseScrewPillarBracket002"
  Base = -> Sketch020
  Dir = (0,0,1)
  DirMode = 2
  FaceMakerClass = Part::FaceMakerBullseye
  LengthFwd = 2.4
  LengthRev = 0
  Placement = pos=(13.7,29,13.26) rot=(0,-1,0;1.5708rad)
  Solid = true
  Symmetric = false
FEATURE [Sketcher::SketchObject] Sketch021
  FullyConstrained = true
  sketch-geometry (7):
    g0: LineSegment StartX=0 StartY=0 StartZ=0 EndX=0 EndY=6 EndZ=0
    g1: Circle CenterX=0 CenterY=0 CenterZ=0 NormalX=0 NormalY=0 NormalZ=1 AngleXU=0 Radius=1
    g2: Circle CenterX=8 CenterY=6 CenterZ=0 NormalX=0 NormalY=0 NormalZ=1 AngleXU=0 Radius=1
    g3: BSplineCurve PolesCount=3 KnotsCount=2 Degree=2 IsPeriodic=0
    g4: GeomPoint X=0 Y=0 Z=0
    g5: GeomPoint X=8 Y=6 Z=0
    g6: LineSegment StartX=0 StartY=6 StartZ=0 EndX=8 EndY=6 EndZ=0
  constraints (14):
    c: Coincident(g0,g-1)
    c: Distance(g0) = 6
    c: Vertical(g0)
    c: Coincident(g3,g0)
    c: Weight(g1) = 1
    c: Equal(g1,g2)
    c: InternalAlignment(g1,g3)
    c: InternalAlignment(g2,g3)
    c: InternalAlignment(g4,g3)
    c: InternalAlignment(g5,g3)
    c: Block(g3)
    c: Coincident(g6,g0)
    c: Coincident(g6,g3)
    c: Horizontal(g6)
FEATURE [Part::Extrusion] Extrude015  label="caseScrewPillarBracket003"
  Base = -> Sketch021
  Dir = (0,0,1)
  DirMode = 2
  FaceMakerClass = Part::FaceMakerBullseye
  LengthFwd = 2.4
  LengthRev = 0
  Placement = pos=(11.3,29,58.74) rot=(0,1,0;1.5708rad)
  Solid = true
  Symmetric = false
FEATURE [Sketcher::SketchObject] Sketch022
  FullyConstrained = true
  sketch-geometry (7):
    g0: LineSegment StartX=0 StartY=0 StartZ=0 EndX=0 EndY=6 EndZ=0
    g1: Circle CenterX=0 CenterY=0 CenterZ=0 NormalX=0 NormalY=0 NormalZ=1 AngleXU=0 Radius=1
    g2: Circle CenterX=8 CenterY=6 CenterZ=0 NormalX=0 NormalY=0 NormalZ=1 AngleXU=0 Radius=1
    g3: BSplineCurve PolesCount=3 KnotsCount=2 Degree=2 IsPeriodic=0
    g4: GeomPoint X=0 Y=0 Z=0
    g5: GeomPoint X=8 Y=6 Z=0
    g6: LineSegment StartX=0 StartY=6 StartZ=0 EndX=8 EndY=6 EndZ=0
  constraints (14):
    c: Coincident(g0,g-1)
    c: Distance(g0) = 6
    c: Vertical(g0)
    c: Coincident(g3,g0)
    c: Weight(g1) = 1
    c: Equal(g1,g2)
    c: InternalAlignment(g1,g3)
    c: InternalAlignment(g2,g3)
    c: InternalAlignment(g4,g3)
    c: InternalAlignment(g5,g3)
    c: Block(g3)
    c: Coincident(g6,g0)
    c: Coincident(g6,g3)
    c: Horizontal(g6)
FEATURE [Part::Extrusion] Extrude016  label="caseScrewPillarBracket004"
  Base = -> Sketch022
  Dir = (0,0,1)
  DirMode = 2
  FaceMakerClass = Part::FaceMakerBullseye
  LengthFwd = 2.4
  LengthRev = 0
  Placement = pos=(88.3,29,65.23) rot=(0,1,0;1.5708rad)
  Solid = true
  Symmetric = false
FEATURE [Sketcher::SketchObject] Sketch023
  FullyConstrained = true
  sketch-geometry (7):
    g0: LineSegment StartX=0 StartY=0 StartZ=0 EndX=0 EndY=6 EndZ=0
    g1: Circle CenterX=0 CenterY=0 CenterZ=0 NormalX=0 NormalY=0 NormalZ=1 AngleXU=0 Radius=1
    g2: Circle CenterX=8 CenterY=6 CenterZ=0 NormalX=0 NormalY=0 NormalZ=1 AngleXU=0 Radius=1
    g3: BSplineCurve PolesCount=3 KnotsCount=2 Degree=2 IsPeriodic=0
    g4: GeomPoint X=0 Y=0 Z=0
    g5: GeomPoint X=8 Y=6 Z=0
    g6: LineSegment StartX=0 StartY=6 StartZ=0 EndX=8 EndY=6 EndZ=0
  constraints (14):
    c: Coincident(g0,g-1)
    c: Distance(g0) = 6
    c: Vertical(g0)
    c: Coincident(g3,g0)
    c: Weight(g1) = 1
    c: Equal(g1,g2)
    c: InternalAlignment(g1,g3)
    c: InternalAlignment(g2,g3)
    c: InternalAlignment(g4,g3)
    c: InternalAlignment(g5,g3)
    c: Block(g3)
    c: Coincident(g6,g0)
    c: Coincident(g6,g3)
    c: Horizontal(g6)
FEATURE [Part::Extrusion] Extrude017  label="caseScrewPillarBracket005"
  Base = -> Sketch023
  Dir = (0,0,1)
  DirMode = 2
  FaceMakerClass = Part::FaceMakerBullseye
  LengthFwd = 2.4
  LengthRev = 0
  Placement = pos=(90.7,29,6.77) rot=(0,-1,0;1.5708rad)
  Solid = true
  Symmetric = false
FEATURE [Sketcher::SketchObject] Sketch024
  FullyConstrained = true
  sketch-geometry (7):
    g0: LineSegment StartX=0 StartY=0 StartZ=0 EndX=0 EndY=6 EndZ=0
    g1: Circle CenterX=0 CenterY=0 CenterZ=0 NormalX=0 NormalY=0 NormalZ=1 AngleXU=0 Radius=1
    g2: Circle CenterX=8 CenterY=6 CenterZ=0 NormalX=0 NormalY=0 NormalZ=1 AngleXU=0 Radius=1
    g3: BSplineCurve PolesCount=3 KnotsCount=2 Degree=2 IsPeriodic=0
    g4: GeomPoint X=0 Y=0 Z=0
    g5: GeomPoint X=8 Y=6 Z=0
    g6: LineSegment StartX=0 StartY=6 StartZ=0 EndX=8 EndY=6 EndZ=0
  constraints (14):
    c: Coincident(g0,g-1)
    c: Distance(g0) = 6
    c: Vertical(g0)
    c: Coincident(g3,g0)
    c: Weight(g1) = 1
    c: Equal(g1,g2)
    c: InternalAlignment(g1,g3)
    c: InternalAlignment(g2,g3)
    c: InternalAlignment(g4,g3)
    c: InternalAlignment(g5,g3)
    c: Block(g3)
    c: Coincident(g6,g0)
    c: Coincident(g6,g3)
    c: Horizontal(g6)
FEATURE [Part::Extrusion] Extrude018  label="caseScrewPillarBracket006"
  Base = -> Sketch024
  Dir = (0,0,1)
  DirMode = 2
  FaceMakerClass = Part::FaceMakerBullseye
  LengthFwd = 2.4
  LengthRev = 0
  Placement = pos=(103.7,29,6.77) rot=(0,-1,0;1.5708rad)
  Solid = true
  Symmetric = false
FEATURE [Sketcher::SketchObject] Sketch025
  FullyConstrained = true
  sketch-geometry (7):
    g0: LineSegment StartX=0 StartY=0 StartZ=0 EndX=0 EndY=6 EndZ=0
    g1: Circle CenterX=0 CenterY=0 CenterZ=0 NormalX=0 NormalY=0 NormalZ=1 AngleXU=0 Radius=1
    g2: Circle CenterX=8 CenterY=6 CenterZ=0 NormalX=0 NormalY=0 NormalZ=1 AngleXU=0 Radius=1
    g3: BSplineCurve PolesCount=3 KnotsCount=2 Degree=2 IsPeriodic=0
    g4: GeomPoint X=0 Y=0 Z=0
    g5: GeomPoint X=8 Y=6 Z=0
    g6: LineSegment StartX=0 StartY=6 StartZ=0 EndX=8 EndY=6 EndZ=0
  constraints (14):
    c: Coincident(g0,g-1)
    c: Distance(g0) = 6
    c: Vertical(g0)
    c: Coincident(g3,g0)
    c: Weight(g1) = 1
    c: Equal(g1,g2)
    c: InternalAlignment(g1,g3)
    c: InternalAlignment(g2,g3)
    c: InternalAlignment(g4,g3)
    c: InternalAlignment(g5,g3)
    c: Block(g3)
    c: Coincident(g6,g0)
    c: Coincident(g6,g3)
    c: Horizontal(g6)
FEATURE [Part::Extrusion] Extrude019  label="caseScrewPillarBracket007"
  Base = -> Sketch025
  Dir = (0,0,1)
  DirMode = 2
  FaceMakerClass = Part::FaceMakerBullseye
  LengthFwd = 2.4
  LengthRev = 0
  Placement = pos=(101.3,29,65.23) rot=(0,1,0;1.5708rad)
  Solid = true
  Symmetric = false
FEATURE [Part::Box] Box011  label="frontCaseScrewPillarBracket"
  AttacherType = Attacher::AttachEngine3D
  Height = 2.4
  Length = 16
  Placement = pos=(87,28,2.3) rot=(0,0,1;0rad)
  Width = 7
FEATURE [Part::Box] Box012  label="frontCaseScrewPillarBracket001"
  AttacherType = Attacher::AttachEngine3D
  Height = 2.4
  Length = 16
  Placement = pos=(87,28,67.3) rot=(0,0,1;0rad)
  Width = 7
FEATURE [Sketcher::SketchObject] Sketch026
  FullyConstrained = true
  sketch-geometry (17):
    g0: Circle CenterX=-3.5 CenterY=23.5 CenterZ=0 NormalX=0 NormalY=0 NormalZ=1 AngleXU=0 Radius=1
    g1: Circle CenterX=-1 CenterY=15.25 CenterZ=0 NormalX=0 NormalY=0 NormalZ=1 AngleXU=0 Radius=1
    g2: Circle CenterX=-3.5 CenterY=7 CenterZ=0 NormalX=0 NormalY=0 NormalZ=1 AngleXU=0 Radius=1
    g3: BSplineCurve PolesCount=3 KnotsCount=2 Degree=2 IsPeriodic=0
    g4: GeomPoint X=-3.5 Y=23.5 Z=0
    g5: GeomPoint X=-3.5 Y=7 Z=0
    g6: Circle CenterX=-4.8 CenterY=30.5 CenterZ=0 NormalX=0 NormalY=0 NormalZ=1 AngleXU=0 Radius=1
    g7: Circle CenterX=-3.5 CenterY=30.5 CenterZ=0 NormalX=0 NormalY=0 NormalZ=1 AngleXU=0 Radius=1
    g8: Circle CenterX=-3.5 CenterY=29.2 CenterZ=0 NormalX=0 NormalY=0 NormalZ=1 AngleXU=0 Radius=1
    g9: BSplineCurve PolesCount=3 KnotsCount=2 Degree=2 IsPeriodic=0
    g10: GeomPoint X=-4.8 Y=30.5 Z=0
    g11: GeomPoint X=-3.5 Y=29.2 Z=0
    g12: LineSegment StartX=-3.5 StartY=29.2 StartZ=0 EndX=-3.5 EndY=23.5 EndZ=0
    g13: LineSegment StartX=-4.8 StartY=30.5 StartZ=0 EndX=0 EndY=30.5 EndZ=0
    g14: LineSegment StartX=-3.5 StartY=5 StartZ=0 EndX=-3.5 EndY=7 EndZ=0
    g15: LineSegment StartX=0 StartY=5 StartZ=0 EndX=0 EndY=30.5 EndZ=0
    g16: LineSegment StartX=-3.5 StartY=5 StartZ=0 EndX=0 EndY=5 EndZ=0
  constraints (33):
    c: Weight(g0) = 1
    c: Equal(g0,g1)
    c: Equal(g0,g2)
    c: InternalAlignment(g0,g3)
    c: InternalAlignment(g1,g3)
    c: InternalAlignment(g2,g3)
    c: InternalAlignment(g4,g3)
    c: InternalAlignment(g5,g3)
    c: Block(g3)
    c: Weight(g6) = 1
    c: Equal(g6,g7)
    c: Equal(g6,g8)
    c: InternalAlignment(g6,g9)
    c: InternalAlignment(g7,g9)
    c: InternalAlignment(g8,g9)
    c: InternalAlignment(g10,g9)
    c: InternalAlignment(g11,g9)
    c: Block(g9)
    c: Coincident(g12,g9)
    c: Coincident(g12,g3)
    c: Vertical(g12)
    c: Coincident(g13,g9)
    c: Horizontal(g13)
    c: Distance(g13) = 4.8
    c: Coincident(g14,g3)
    c: Vertical(g14)
    c: Coincident(g15,g13)
    c: Vertical(g15)
    c: Tangent(g15,g1)
    c: Distance(g14) = 2
    c: Coincident(g16,g14)
    c: Horizontal(g16)
    c: Coincident(g15,g16)
FEATURE [Part::Feature] Face050
  shape: bbox 4.8 x 25.5 x 2e-07 mm, 1 faces, 0 solids (baked)
FEATURE [Part::Revolution] Revolve054  label="moreFrontCaseScrewPost001"
  Angle = 360
  Axis = (0,1,0)
  Base = (0,0,0)
  FaceMakerClass = Part::FaceMakerBullseye
  Placement = pos=(102.5,4.5,3.5) rot=(0,0,1;0rad)
  Solid = false
  Source = -> Face050
  Symmetric = false
FEATURE [Part::Feature] Face051
  shape: bbox 4.8 x 25.5 x 2e-07 mm, 1 faces, 0 solids (baked)
FEATURE [Part::Revolution] Revolve055  label="moreFrontCaseScrewPost002"
  Angle = 360
  Axis = (0,1,0)
  Base = (0,0,0)
  FaceMakerClass = Part::FaceMakerBullseye
  Placement = pos=(102.5,4.5,68.5) rot=(0,0,1;0rad)
  Solid = false
  Source = -> Face051
  Symmetric = false
FEATURE [Sketcher::SketchObject] Sketch027
  FullyConstrained = true
  sketch-geometry (10):
    g0: LineSegment StartX=-1.6 StartY=4.7 StartZ=0 EndX=-1.6 EndY=1.7 EndZ=0
    g1: LineSegment StartX=-3.5 StartY=4.7 StartZ=0 EndX=-1.6 EndY=4.7 EndZ=0
    g2: LineSegment StartX=-1.6 StartY=1.7 StartZ=0 EndX=-1.6 EndY=1.5 EndZ=0
    g3: LineSegment StartX=-1.6 StartY=1.5 StartZ=0 EndX=-5.2 EndY=1.5 EndZ=0
    g4: Circle CenterX=-3.5 CenterY=4.7 CenterZ=0 NormalX=0 NormalY=0 NormalZ=1 AngleXU=0 Radius=1
    g5: Circle CenterX=-3.59627 CenterY=2.99743 CenterZ=0 NormalX=0 NormalY=0 NormalZ=1 AngleXU=0 Radius=1
    g6: Circle CenterX=-5.2 CenterY=1.5 CenterZ=0 NormalX=0 NormalY=0 NormalZ=1 AngleXU=0 Radius=1
    g7: BSplineCurve PolesCount=3 KnotsCount=2 Degree=2 IsPeriodic=0
    g8: GeomPoint X=-3.5 Y=4.7 Z=0
    g9: GeomPoint X=-5.2 Y=1.5 Z=0
  constraints (23):
    c: Vertical(g0)
    c: Distance(g0) = 3
    c: Coincident(g1,g0)
    c: Horizontal(g1)
    c: Block(g0)
    c: Block(g1)
    c: Coincident(g2,g0)
    c: Vertical(g2)
    c: Distance(g2) = 0.2
    c: Coincident(g3,g2)
    c: Horizontal(g3)
    c: Block(g3)
    c: Coincident(g7,g1)
    c: Weight(g4) = 1
    c: Equal(g4,g5)
    c: Equal(g4,g6)
    c: Coincident(g7,g3)
    c: InternalAlignment(g4,g7)
    c: InternalAlignment(g5,g7)
    c: InternalAlignment(g6,g7)
    c: InternalAlignment(g8,g7)
    c: InternalAlignment(g9,g7)
    c: Block(g7)
FEATURE [Sketcher::SketchObject] Sketch028
  FullyConstrained = true
  sketch-geometry (18):
    g0: LineSegment StartX=0 StartY=3e-16 StartZ=0 EndX=0 EndY=1.7 EndZ=0
    g1: LineSegment StartX=-3.5 StartY=0 StartZ=0 EndX=-3.5 EndY=0.9 EndZ=0
    g2: Circle CenterX=-2.7 CenterY=1.7 CenterZ=0 NormalX=0 NormalY=0 NormalZ=1 AngleXU=0 Radius=1
    g3: Circle CenterX=-3.5 CenterY=1.7 CenterZ=0 NormalX=0 NormalY=0 NormalZ=1 AngleXU=0 Radius=1
    g4: Circle CenterX=-3.5 CenterY=0.9 CenterZ=0 NormalX=0 NormalY=0 NormalZ=1 AngleXU=0 Radius=1
    g5: BSplineCurve PolesCount=3 KnotsCount=2 Degree=2 IsPeriodic=0
    g6: GeomPoint X=-2.7 Y=1.7 Z=0
    g7: GeomPoint X=-3.5 Y=0.9 Z=0
    g8: LineSegment StartX=-3.5 StartY=0 StartZ=0 EndX=-3.5 EndY=-7 EndZ=0
    g9: LineSegment StartX=0 StartY=3e-16 StartZ=0 EndX=0 EndY=-7 EndZ=0
    g10: LineSegment StartX=-3.5 StartY=-7 StartZ=0 EndX=0 EndY=-7 EndZ=0
    g11: LineSegment StartX=-2.7 StartY=1.7 StartZ=0 EndX=-1.6 EndY=1.7 EndZ=0
    g12: LineSegment StartX=0 StartY=1.7 StartZ=0 EndX=0 EndY=4.5 EndZ=0
    g13: LineSegment StartX=0 StartY=4.5 StartZ=0 EndX=0 EndY=10.8 EndZ=0
    g14: LineSegment StartX=0 StartY=10.8 StartZ=0 EndX=-2 EndY=10.8 EndZ=0
    g15: LineSegment StartX=-1.6 StartY=4.7 StartZ=0 EndX=-1.6 EndY=1.7 EndZ=0
    g16: LineSegment StartX=-1.6 StartY=4.7 StartZ=0 EndX=-2 EndY=4.7 EndZ=0
    g17: LineSegment StartX=-2 StartY=4.7 StartZ=0 EndX=-2 EndY=10.8 EndZ=0
  constraints (44):
    c: Vertical(g0)
    c: Vertical(g1)
    c: Distance(g1) = 0.9
    c: Block(g0)
    c: Distance(g0) = 1.7
    c: Weight(g2) = 1
    c: Equal(g2,g3)
    c: Equal(g2,g4)
    c: Coincident(g5,g1)
    c: InternalAlignment(g2,g5)
    c: InternalAlignment(g3,g5)
    c: InternalAlignment(g4,g5)
    c: InternalAlignment(g6,g5)
    c: InternalAlignment(g7,g5)
    c: Block(g5)
    c: Coincident(g8,g1)
    c: Vertical(g8)
    c: Distance(g8) = 7
    c: Vertical(g9)
    c: Equal(g8,g9) = 7
    c: Coincident(g9,g0)
    c: Coincident(g10,g8)
    c: Coincident(g10,g9)
    c: Horizontal(g10)
    c: Coincident(g11,g5)
    c: Horizontal(g11)
    c: Coincident(g12,g0)
    c: Vertical(g12)
    c: Distance(g12) = 2.8
    c: Coincident(g13,g12)
    c: Vertical(g13)
    c: Distance(g13) = 6.3
    c: Coincident(g14,g13)
    c: Horizontal(g14)
    c: Distance(g14) = 2
    c: Vertical(g15)
    c: Distance(g15) = 3
    c: Block(g11)
    c: Coincident(g15,g11)
    c: Coincident(g16,g15)
    c: Horizontal(g16)
    c: Coincident(g17,g16)
    c: Coincident(g17,g14)
    c: Vertical(g17)
FEATURE [Part::Revolution] Revolve040  label="backCaseScrewRetainer001"
  Angle = 360
  Axis = (0,1,0)
  Base = (0,0,0)
  FaceMakerClass = Part::FaceMakerBullseye
  Placement = pos=(12.5,3,10) rot=(0,0,1;0rad)
  Solid = false
  Source = -> Face036
  Symmetric = false
FEATURE [Part::Feature] Face055
  shape: bbox 3.5 x 30.2 x 2e-07 mm, 1 faces, 0 solids (baked)
FEATURE [Part::Revolution] Revolve059  label="backCaseScrewPost"
  Angle = 360
  Axis = (0,1,0)
  Base = (0,0,0)
  FaceMakerClass = Part::FaceMakerBullseye
  Placement = pos=(12.5,4.5,10) rot=(0,0,1;0rad)
  Solid = false
  Source = -> Face055
  Symmetric = false
FEATURE [Part::Feature] Face056
  shape: bbox 3.5 x 30.2 x 2e-07 mm, 1 faces, 0 solids (baked)
FEATURE [Part::Revolution] Revolve060  label="backCaseScrewPost001"
  Angle = 360
  Axis = (0,1,0)
  Base = (0,0,0)
  FaceMakerClass = Part::FaceMakerBullseye
  Placement = pos=(12.5,4.5,62) rot=(0,0,1;0rad)
  Solid = false
  Source = -> Face056
  Symmetric = false
FEATURE [Part::Feature] Face057
  shape: bbox 3.5 x 17.8 x 2e-07 mm, 1 faces, 0 solids (baked)
FEATURE [Part::Revolution] Revolve061  label="removeToCreateScrewAndThreadedInsertHole"
  Angle = 360
  Axis = (0,1,0)
  Base = (0,0,0)
  FaceMakerClass = Part::FaceMakerBullseye
  Placement = pos=(12.5,0,10) rot=(0,0,1;0rad)
  Solid = false
  Source = -> Face057
  Symmetric = false
FEATURE [Part::Feature] Face058
  shape: bbox 3.5 x 17.8 x 2e-07 mm, 1 faces, 0 solids (baked)
FEATURE [Part::Revolution] Revolve062  label="removeToCreateScrewAndThreadedInsertHole001"
  Angle = 360
  Axis = (0,1,0)
  Base = (0,0,0)
  FaceMakerClass = Part::FaceMakerBullseye
  Placement = pos=(12.5,0,62) rot=(0,0,1;0rad)
  Solid = false
  Source = -> Face058
  Symmetric = false
FEATURE [Part::Feature] Face059
  shape: bbox 3.5 x 17.8 x 2e-07 mm, 1 faces, 0 solids (baked)
FEATURE [Part::Revolution] Revolve063  label="removeToCreateScrewAndThreadedInsertHole002"
  Angle = 360
  Axis = (0,1,0)
  Base = (0,0,0)
  FaceMakerClass = Part::FaceMakerBullseye
  Placement = pos=(89.5,0,68.5) rot=(0,0,1;0rad)
  Solid = false
  Source = -> Face059
  Symmetric = false
FEATURE [Part::Feature] Face060
  shape: bbox 3.5 x 17.8 x 2e-07 mm, 1 faces, 0 solids (baked)
FEATURE [Part::Revolution] Revolve064  label="removeToCreateScrewAndThreadedInsertHole003"
  Angle = 360
  Axis = (0,1,0)
  Base = (0,0,0)
  FaceMakerClass = Part::FaceMakerBullseye
  Placement = pos=(89.5,0,3.5) rot=(0,0,1;0rad)
  Solid = false
  Source = -> Face060
  Symmetric = false
FEATURE [Part::Feature] Face061
  shape: bbox 3.5 x 17.8 x 2e-07 mm, 1 faces, 0 solids (baked)
FEATURE [Part::Revolution] Revolve065  label="removeToCreateScrewAndThreadedInsertHole004"
  Angle = 360
  Axis = (0,1,0)
  Base = (0,0,0)
  FaceMakerClass = Part::FaceMakerBullseye
  Placement = pos=(102.5,4.7,3.5) rot=(0,0,1;0rad)
  Solid = false
  Source = -> Face061
  Symmetric = false
FEATURE [Part::Feature] Face062
  shape: bbox 3.5 x 17.8 x 2e-07 mm, 1 faces, 0 solids (baked)
FEATURE [Part::Revolution] Revolve066  label="removeToCreateScrewAndThreadedInsertHole005"
  Angle = 360
  Axis = (0,1,0)
  Base = (0,0,0)
  FaceMakerClass = Part::FaceMakerBullseye
  Placement = pos=(102.5,4.7,68.5) rot=(0,0,1;0rad)
  Solid = false
  Source = -> Face062
  Symmetric = false
FEATURE [Part::MultiFuse] Fusion047  label="makeHoles"
  Shapes = -> [Revolve066,Revolve065,Revolve064,Revolve063,Revolve062,Revolve061]
FEATURE [Part::Feature] Face063
  shape: bbox 3.6 x 3.2 x 2e-07 mm, 1 faces, 0 solids (baked)
FEATURE [Part::Revolution] Revolve067  label="moreFrontCaseScrewRetainer002"
  Angle = 360
  Axis = (0,1,0)
  Base = (0,0,0)
  FaceMakerClass = Part::FaceMakerBullseye
  Placement = pos=(102.5,4.5,68.5) rot=(0,0,1;0rad)
  Solid = false
  Source = -> Face063
  Symmetric = false
FEATURE [Part::Feature] Face064
  shape: bbox 3.6 x 3.2 x 2e-07 mm, 1 faces, 0 solids (baked)
FEATURE [Part::Revolution] Revolve068  label="moreFrontCaseScrewRetainer003"
  Angle = 360
  Axis = (0,1,0)
  Base = (0,0,0)
  FaceMakerClass = Part::FaceMakerBullseye
  Placement = pos=(102.5,4.5,3.5) rot=(0,0,1;0rad)
  Solid = false
  Source = -> Face064
  Symmetric = false
FEATURE [Part::Feature] Face065
  shape: bbox 3.5 x 17.8 x 2e-07 mm, 1 faces, 0 solids (baked)
FEATURE [Part::Revolution] Revolve069  label="removeToCreateScrewAndThreadedInsertHole006"
  Angle = 360
  Axis = (0,1,0)
  Base = (0,0,0)
  FaceMakerClass = Part::FaceMakerBullseye
  Placement = pos=(12.5,0,10) rot=(0,0,1;0rad)
  Solid = false
  Source = -> Face065
  Symmetric = false
FEATURE [Part::Feature] Face066
  shape: bbox 3.5 x 17.8 x 2e-07 mm, 1 faces, 0 solids (baked)
FEATURE [Part::Revolution] Revolve070  label="removeToCreateScrewAndThreadedInsertHole007"
  Angle = 360
  Axis = (0,1,0)
  Base = (0,0,0)
  FaceMakerClass = Part::FaceMakerBullseye
  Placement = pos=(12.5,0,62) rot=(0,0,1;0rad)
  Solid = false
  Source = -> Face066
  Symmetric = false
FEATURE [Part::Feature] Face067
  shape: bbox 3.5 x 17.8 x 2e-07 mm, 1 faces, 0 solids (baked)
FEATURE [Part::Revolution] Revolve071  label="removeToCreateScrewAndThreadedInsertHole008"
  Angle = 360
  Axis = (0,1,0)
  Base = (0,0,0)
  FaceMakerClass = Part::FaceMakerBullseye
  Placement = pos=(89.5,0,68.5) rot=(0,0,1;0rad)
  Solid = false
  Source = -> Face067
  Symmetric = false
FEATURE [Part::Feature] Face068
  shape: bbox 3.5 x 17.8 x 2e-07 mm, 1 faces, 0 solids (baked)
FEATURE [Part::Revolution] Revolve072  label="removeToCreateScrewAndThreadedInsertHole009"
  Angle = 360
  Axis = (0,1,0)
  Base = (0,0,0)
  FaceMakerClass = Part::FaceMakerBullseye
  Placement = pos=(89.5,0,3.5) rot=(0,0,1;0rad)
  Solid = false
  Source = -> Face068
  Symmetric = false
FEATURE [Part::Feature] Face069
  shape: bbox 3.5 x 17.8 x 2e-07 mm, 1 faces, 0 solids (baked)
FEATURE [Part::Feature] Face070
  shape: bbox 3.5 x 17.8 x 2e-07 mm, 1 faces, 0 solids (baked)
FEATURE [Part::Revolution] Revolve073  label="removeToCreateScrewAndThreadedInsertHole010"
  Angle = 360
  Axis = (0,1,0)
  Base = (0,0,0)
  FaceMakerClass = Part::FaceMakerBullseye
  Placement = pos=(102.5,4.7,3.5) rot=(0,0,1;0rad)
  Solid = false
  Source = -> Face069
  Symmetric = false
FEATURE [Part::Revolution] Revolve074  label="removeToCreateScrewAndThreadedInsertHole011"
  Angle = 360
  Axis = (0,1,0)
  Base = (0,0,0)
  FaceMakerClass = Part::FaceMakerBullseye
  Placement = pos=(102.5,4.7,68.5) rot=(0,0,1;0rad)
  Solid = false
  Source = -> Face070
  Symmetric = false
FEATURE [Part::MultiFuse] Fusion048  label="makeHoles001"
  Shapes = -> [Revolve074,Revolve073,Revolve072,Revolve071,Revolve070,Revolve069]
FEATURE [Part::MultiFuse] Fusion049  label="caseScrewRetainers"
  Shapes = -> [Revolve067,Revolve068,Revolve048,Revolve047,Revolve039,Revolve040]
FEATURE [Part::Cut] Cut015  label="caseScrewRetainers001"
  Base = -> Fusion049
  Tool = -> Fusion048
FEATURE [Part::MultiFuse] Fusion050  label="casePillars"
  Shapes = -> [Revolve055,Revolve054,Revolve043,Revolve046,Revolve059,Revolve060]
FEATURE [Part::Feature] Face071 .. Face076  x6 (patterned run collapsed; names and placements below)
  shape: bbox 3.5 x 17.8 x 2e-07 mm, 1 faces, 0 solids (baked)
FEATURE [Part::Revolution] Revolve075  label="removeToCreateScrewAndThreadedInsertHole012"
  Angle = 360
  Axis = (0,1,0)
  Base = (0,0,0)
  FaceMakerClass = Part::FaceMakerBullseye
  Placement = pos=(12.5,0,10) rot=(0,0,1;0rad)
  Solid = false
  Source = -> Face071
  Symmetric = false
FEATURE [Part::Revolution] Revolve076  label="removeToCreateScrewAndThreadedInsertHole013"
  Angle = 360
  Axis = (0,1,0)
  Base = (0,0,0)
  FaceMakerClass = Part::FaceMakerBullseye
  Placement = pos=(12.5,0,62) rot=(0,0,1;0rad)
  Solid = false
  Source = -> Face072
  Symmetric = false
FEATURE [Part::Revolution] Revolve077  label="removeToCreateScrewAndThreadedInsertHole014"
  Angle = 360
  Axis = (0,1,0)
  Base = (0,0,0)
  FaceMakerClass = Part::FaceMakerBullseye
  Placement = pos=(89.5,0,68.5) rot=(0,0,1;0rad)
  Solid = false
  Source = -> Face073
  Symmetric = false
FEATURE [Part::Revolution] Revolve078  label="removeToCreateScrewAndThreadedInsertHole015"
  Angle = 360
  Axis = (0,1,0)
  Base = (0,0,0)
  FaceMakerClass = Part::FaceMakerBullseye
  Placement = pos=(89.5,0,3.5) rot=(0,0,1;0rad)
  Solid = false
  Source = -> Face074
  Symmetric = false
FEATURE [Part::Revolution] Revolve079  label="removeToCreateScrewAndThreadedInsertHole016"
  Angle = 360
  Axis = (0,1,0)
  Base = (0,0,0)
  FaceMakerClass = Part::FaceMakerBullseye
  Placement = pos=(102.5,4.7,3.5) rot=(0,0,1;0rad)
  Solid = false
  Source = -> Face075
  Symmetric = false
FEATURE [Part::Revolution] Revolve080  label="removeToCreateScrewAndThreadedInsertHole017"
  Angle = 360
  Axis = (0,1,0)
  Base = (0,0,0)
  FaceMakerClass = Part::FaceMakerBullseye
  Placement = pos=(102.5,4.7,68.5) rot=(0,0,1;0rad)
  Solid = false
  Source = -> Face076
  Symmetric = false
FEATURE [Part::MultiFuse] Fusion051  label="makeHoles002"
  Shapes = -> [Revolve080,Revolve079,Revolve078,Revolve077,Revolve076,Revolve075]
FEATURE [Part::Cut] Cut016  label="caesPillars"
  Base = -> Fusion050
  Tool = -> Fusion051
FEATURE [Part::Revolution] Revolve009  label="plugHousing016"
  Angle = 360
  Axis = (0,1,0)
  Base = (0,0,0)
  FaceMakerClass = Part::FaceMakerBullseye
  Placement = pos=(0,0,36.15) rot=(0,0,1;0rad)
  Solid = false
  Source = -> Face012
  Symmetric = false
FEATURE [Part::MultiFuse] Fusion014  label="plugHousing023"
  Placement = pos=(0,0,0) rot=(0,0,1;1.5708rad)
  Shapes = -> [Revolve011,Revolve009]
FEATURE [Part::Revolution] Revolve010  label="plugHousing017"
  Angle = 360
  Axis = (0,1,0)
  Base = (0,0,0)
  FaceMakerClass = Part::FaceMakerBullseye
  Placement = pos=(0,0,36.15) rot=(0,0,1;0rad)
  Solid = false
  Source = -> Face014
  Symmetric = false
FEATURE [Part::MultiFuse] Fusion015  label="plugHousing024"
  Placement = pos=(0,0,0) rot=(0,0,1;1.5708rad)
  Shapes = -> [Revolve010,Revolve015]
FEATURE [Part::Revolution] Revolve014  label="plugHousing026"
  Angle = 360
  Axis = (0,1,0)
  Base = (0,0,0)
  FaceMakerClass = Part::FaceMakerBullseye
  Placement = pos=(0,0,36.15) rot=(0,0,1;0rad)
  Solid = false
  Source = -> Face011
  Symmetric = false
FEATURE [Part::Revolution] Revolve013  label="plugHousing025"
  Angle = 360
  Axis = (0,1,0)
  Base = (0,0,0)
  FaceMakerClass = Part::FaceMakerBullseye
  Placement = pos=(0,0,36.15) rot=(0,0,1;0rad)
  Solid = false
  Source = -> Face015
  Symmetric = false
FEATURE [Part::MultiFuse] Fusion016  label="plugHousing028"
  Placement = pos=(0,19,0) rot=(0,0,1;3.14159rad)
  Shapes = -> [Fusion014,Fusion013]
FEATURE [Part::MultiFuse] Fusion011  label="plugHousing018"
  Placement = pos=(0,0,0) rot=(0,0,1;1.5708rad)
  Shapes = -> [Revolve014,Revolve013]
FEATURE [Part::MultiFuse] Fusion012  label="plugHousing019"
  Placement = pos=(0,19,0) rot=(0,0,1;3.14159rad)
  Shapes = -> [Fusion011,Fusion015]
FEATURE [Part::MultiFuse] Fusion017  label="plugHousing029"
  Placement = pos=(122.621,0,-0.15) rot=(0,0,1;0rad)
  Shapes = -> [Fusion016,Fusion012]
FEATURE [Part::MultiFuse] Fusion052  label="casePillarRetainers"
  Shapes = -> [Extrude012,Extrude013,Extrude014,Extrude015,Extrude016,Extrude017,Extrude018,Extrude019,Box011,Box012]
FEATURE [Part::Feature] Face077
  shape: bbox 3.5 x 17.8 x 2e-07 mm, 1 faces, 0 solids (baked)
FEATURE [Part::Revolution] Revolve081  label="removeToCreateScrewAndThreadedInsertHole018"
  Angle = 360
  Axis = (0,1,0)
  Base = (0,0,0)
  FaceMakerClass = Part::FaceMakerBullseye
  Placement = pos=(62.3,30.3,19.7) rot=(0,0,1;0rad)
  Solid = false
  Source = -> Face077
  Symmetric = false
FEATURE [Part::Feature] Face078
  shape: bbox 3.5 x 17.8 x 2e-07 mm, 1 faces, 0 solids (baked)
FEATURE [Part::Revolution] Revolve082  label="removeToCreateScrewAndThreadedInsertHole019"
  Angle = 360
  Axis = (0,1,0)
  Base = (0,0,0)
  FaceMakerClass = Part::FaceMakerBullseye
  Placement = pos=(62.3,30.3,51.7) rot=(0,0,1;0rad)
  Solid = false
  Source = -> Face078
  Symmetric = false
FEATURE [Part::Feature] Face079
  shape: bbox 3.5 x 17.8 x 2e-07 mm, 1 faces, 0 solids (baked)
FEATURE [Part::Revolution] Revolve083  label="removeToCreateScrewAndThreadedInsertHole020"
  Angle = 360
  Axis = (0,1,0)
  Base = (0,0,0)
  FaceMakerClass = Part::FaceMakerBullseye
  Placement = pos=(30.3,30.3,19.7) rot=(0,0,1;0rad)
  Solid = false
  Source = -> Face079
  Symmetric = false
FEATURE [Part::Feature] Face080
  shape: bbox 3.5 x 17.8 x 2e-07 mm, 1 faces, 0 solids (baked)
FEATURE [Part::Revolution] Revolve084  label="removeToCreateScrewAndThreadedInsertHole021"
  Angle = 360
  Axis = (0,1,0)
  Base = (0,0,0)
  FaceMakerClass = Part::FaceMakerBullseye
  Placement = pos=(30.3,30.3,51.7) rot=(0,0,1;0rad)
  Solid = false
  Source = -> Face080
  Symmetric = false
FEATURE [Part::MultiFuse] Fusion053  label="createThreadedInsertHolesForFan"
  Shapes = -> [Revolve081,Revolve082,Revolve083,Revolve084]
FEATURE [Part::Cut] Cut017  label="fanScrewHousing001"
  Base = -> Fusion046
  Tool = -> Fusion053
FEATURE [Part::Feature] Face081
  shape: bbox 3.5 x 17.8 x 2e-07 mm, 1 faces, 0 solids (baked)
FEATURE [Part::Revolution] Revolve085  label="removeToCreateScrewAndThreadedInsertHole022"
  Angle = 360
  Axis = (0,1,0)
  Base = (0,0,0)
  FaceMakerClass = Part::FaceMakerBullseye
  Placement = pos=(62.3,30.3,19.7) rot=(0,0,1;0rad)
  Solid = false
  Source = -> Face081
  Symmetric = false
FEATURE [Part::Feature] Face082
  shape: bbox 3.5 x 17.8 x 2e-07 mm, 1 faces, 0 solids (baked)
FEATURE [Part::Revolution] Revolve086  label="removeToCreateScrewAndThreadedInsertHole023"
  Angle = 360
  Axis = (0,1,0)
  Base = (0,0,0)
  FaceMakerClass = Part::FaceMakerBullseye
  Placement = pos=(62.3,30.3,51.7) rot=(0,0,1;0rad)
  Solid = false
  Source = -> Face082
  Symmetric = false
FEATURE [Part::Feature] Face083
  shape: bbox 3.5 x 17.8 x 2e-07 mm, 1 faces, 0 solids (baked)
FEATURE [Part::Revolution] Revolve087  label="removeToCreateScrewAndThreadedInsertHole024"
  Angle = 360
  Axis = (0,1,0)
  Base = (0,0,0)
  FaceMakerClass = Part::FaceMakerBullseye
  Placement = pos=(30.3,30.3,19.7) rot=(0,0,1;0rad)
  Solid = false
  Source = -> Face083
  Symmetric = false
FEATURE [Part::Feature] Face084
  shape: bbox 3.5 x 17.8 x 2e-07 mm, 1 faces, 0 solids (baked)
FEATURE [Part::Revolution] Revolve088  label="removeToCreateScrewAndThreadedInsertHole025"
  Angle = 360
  Axis = (0,1,0)
  Base = (0,0,0)
  FaceMakerClass = Part::FaceMakerBullseye
  Placement = pos=(30.3,30.3,51.7) rot=(0,0,1;0rad)
  Solid = false
  Source = -> Face084
  Symmetric = false
FEATURE [Part::MultiFuse] Fusion054  label="createThreadedInsertHolesForFan001"
  Shapes = -> [Revolve085,Revolve086,Revolve087,Revolve088]
FEATURE [Part::Cut] Cut018  label="top007"
  Base = -> Fusion040
  Tool = -> Fusion054
FEATURE [Sketcher::SketchObject] Sketch029
  FullyConstrained = false
  Placement = pos=(0,0,0) rot=(1,0,0;1.5708rad)
  sketch-geometry (24):
    g0: ArcOfCircle CenterX=-4 CenterY=-10.5 CenterZ=0 NormalX=0 NormalY=0 NormalZ=1 AngleXU=0 Radius=1.5 StartAngle=6e-16 EndAngle=3.14159
    g1: ArcOfCircle CenterX=-34.2 CenterY=-10.5 CenterZ=0 NormalX=0 NormalY=0 NormalZ=1 AngleXU=0 Radius=1.5 StartAngle=0 EndAngle=3.14159
    g2: ArcOfCircle CenterX=-34.2 CenterY=-27.7 CenterZ=0 NormalX=0 NormalY=0 NormalZ=1 AngleXU=0 Radius=1.5 StartAngle=3.14159 EndAngle=6.28319
    g3: ArcOfCircle CenterX=-4 CenterY=-27.7 CenterZ=0 NormalX=0 NormalY=0 NormalZ=1 AngleXU=0 Radius=1.5 StartAngle=3.1416 EndAngle=6.28319
    g4: ArcOfCircle CenterX=-10 CenterY=-4.3 CenterZ=0 NormalX=0 NormalY=0 NormalZ=1 AngleXU=0 Radius=1.5 StartAngle=2e-16 EndAngle=3.14159
    g5: ArcOfCircle CenterX=-16.1 CenterY=-1.8 CenterZ=0 NormalX=0 NormalY=0 NormalZ=1 AngleXU=0 Radius=1.5 StartAngle=5e-16 EndAngle=3.14159
    g6: ArcOfCircle CenterX=-22.1 CenterY=-1.8 CenterZ=0 NormalX=0 NormalY=0 NormalZ=1 AngleXU=0 Radius=1.5 StartAngle=5e-16 EndAngle=3.14159
    g7: ArcOfCircle CenterX=-28.2 CenterY=-4.3 CenterZ=0 NormalX=0 NormalY=0 NormalZ=1 AngleXU=0 Radius=1.5 StartAngle=2e-16 EndAngle=3.14159
    g8: ArcOfCircle CenterX=-10 CenterY=-33.9 CenterZ=0 NormalX=0 NormalY=0 NormalZ=1 AngleXU=0 Radius=1.5 StartAngle=3.14159 EndAngle=6.28319
    g9: ArcOfCircle CenterX=-16.1 CenterY=-36.4 CenterZ=0 NormalX=0 NormalY=0 NormalZ=1 AngleXU=0 Radius=1.5 StartAngle=3.14159 EndAngle=6.28319
    g10: ArcOfCircle CenterX=-22.1 CenterY=-36.4 CenterZ=0 NormalX=0 NormalY=0 NormalZ=1 AngleXU=0 Radius=1.5 StartAngle=3.14159 EndAngle=6.28319
    g11: ArcOfCircle CenterX=-28.2 CenterY=-33.9 CenterZ=0 NormalX=0 NormalY=0 NormalZ=1 AngleXU=0 Radius=1.5 StartAngle=3.14159 EndAngle=6.28319
    g12: LineSegment StartX=-35.7 StartY=-10.5 StartZ=0 EndX=-35.7 EndY=-27.7 EndZ=0
    g13: LineSegment StartX=-32.7 StartY=-10.5 StartZ=0 EndX=-32.7 EndY=-27.7 EndZ=0
    g14: LineSegment StartX=-29.7 StartY=-33.9 StartZ=0 EndX=-29.7 EndY=-4.3 EndZ=0
    g15: LineSegment StartX=-26.7 StartY=-33.9 StartZ=0 EndX=-26.7 EndY=-4.3 EndZ=0
    g16: LineSegment StartX=-2.5 StartY=-10.5 StartZ=0 EndX=-2.5 EndY=-27.7 EndZ=0
    g17: LineSegment StartX=-8.5 StartY=-4.3 StartZ=0 EndX=-8.5 EndY=-33.9 EndZ=0
    g18: LineSegment StartX=-5.5 StartY=-10.5 StartZ=0 EndX=-5.5 EndY=-27.7 EndZ=0
    g19: LineSegment StartX=-11.5 StartY=-4.3 StartZ=0 EndX=-11.5 EndY=-33.9 EndZ=0
    g20: LineSegment StartX=-14.6 StartY=-1.8 StartZ=0 EndX=-14.6 EndY=-36.4 EndZ=0
    g21: LineSegment StartX=-17.6 StartY=-1.8 StartZ=0 EndX=-17.6 EndY=-36.4 EndZ=0
    g22: LineSegment StartX=-20.6 StartY=-36.4 StartZ=0 EndX=-20.6 EndY=-1.8 EndZ=0
    g23: LineSegment StartX=-23.6 StartY=-1.8 StartZ=0 EndX=-23.6 EndY=-36.4 EndZ=0
  constraints (48):
    c: Block(g0)
    c: Block(g1)
    c: Block(g2)
    c: Block(g3)
    c: Block(g4)
    c: Block(g5)
    c: Block(g6)
    c: Block(g7)
    c: Block(g8)
    c: Block(g9)
    c: Block(g10)
    c: Block(g11)
    c: Coincident(g12,g1)
    c: Coincident(g12,g2)
    c: Vertical(g12)
    c: Coincident(g13,g1)
    c: Coincident(g13,g2)
    c: Vertical(g13)
    c: Coincident(g14,g11)
    c: Coincident(g14,g7)
    c: Vertical(g14)
    c: Coincident(g15,g11)
    c: Coincident(g15,g7)
    c: Vertical(g15)
    c: Coincident(g16,g0)
    c: Coincident(g16,g3)
    c: Vertical(g16)
    c: Coincident(g17,g4)
    c: Coincident(g17,g8)
    c: Vertical(g17)
    c: Coincident(g18,g0)
    c: Coincident(g18,g3)
    c: Vertical(g18)
    c: Coincident(g19,g4)
    c: Coincident(g19,g8)
    c: Vertical(g19)
    c: Coincident(g20,g5)
    c: Coincident(g20,g9)
    c: Vertical(g20)
    c: Coincident(g21,g5)
    c: Coincident(g21,g9)
    c: Vertical(g21)
    c: Coincident(g22,g10)
    c: Coincident(g22,g6)
    c: Vertical(g22)
    c: Coincident(g23,g6)
    c: Coincident(g23,g10)
    c: Vertical(g23)
FEATURE [Part::Extrusion] Extrude020  label="removeToCreateFanGrillHoles"
  Base = -> Sketch029
  Dir = (0,-1,6e-16)
  DirMode = 2
  FaceMakerClass = Part::FaceMakerBullseye
  LengthFwd = 10
  LengthRev = 0
  Placement = pos=(65.4,44,54.82) rot=(0,0,1;0rad)
  Solid = true
  Symmetric = false
FEATURE [Part::MultiFuse] Fusion055  label="top008"
  Shapes = -> [Cut017,Cut018]
FEATURE [Part::Cut] Cut019  label="top009"
  Base = -> Fusion055
  Tool = -> Extrude020
FEATURE [App::MeasureDistance] Distance003  label="Distance: 71.95 mm"
  Distance = 71.9513
  P1 = (117,38,72)
  P2 = (117,38,0.0487319)
FEATURE [Sketcher::SketchObject] Sketch030
  FullyConstrained = true
  Placement = pos=(117,19,0) rot=(0.57735,0.57735,0.57735;2.0944rad)
  sketch-geometry (48):
    g0: LineSegment StartX=-49.19 StartY=69.25 StartZ=0 EndX=-49.19 EndY=66.25 EndZ=0
    g1: LineSegment StartX=-49.19 StartY=63.5 StartZ=0 EndX=-49.19 EndY=60.5 EndZ=0
    g2: LineSegment StartX=-49.19 StartY=57.75 StartZ=0 EndX=-49.19 EndY=54.75 EndZ=0
    g3: LineSegment StartX=-49.19 StartY=52 StartZ=0 EndX=-49.19 EndY=49 EndZ=0
    g4: LineSegment StartX=-49.19 StartY=46.25 StartZ=0 EndX=-49.19 EndY=43.25 EndZ=0
    g5: LineSegment StartX=-49.19 StartY=40.5 StartZ=0 EndX=-49.19 EndY=37.5 EndZ=0
    g6: LineSegment StartX=-49.19 StartY=34.5 StartZ=0 EndX=-49.19 EndY=31.5 EndZ=0
    g7: LineSegment StartX=-49.19 StartY=28.75 StartZ=0 EndX=-49.19 EndY=25.75 EndZ=0
    g8: LineSegment StartX=-49.19 StartY=23 StartZ=0 EndX=-49.19 EndY=20 EndZ=0
    g9: LineSegment StartX=-49.19 StartY=17.25 StartZ=0 EndX=-49.19 EndY=14.25 EndZ=0
    g10: LineSegment StartX=-49.19 StartY=11.5 StartZ=0 EndX=-49.19 EndY=8.5 EndZ=0
    g11: LineSegment StartX=-49.19 StartY=5.75 StartZ=0 EndX=-49.19 EndY=2.75 EndZ=0
    g12: ArcOfCircle CenterX=-1.5 CenterY=67.75 CenterZ=0 NormalX=0 NormalY=0 NormalZ=1 AngleXU=0 Radius=1.5 StartAngle=4.71239 EndAngle=7.85398
    g13: ArcOfCircle CenterX=-1.5 CenterY=62 CenterZ=0 NormalX=0 NormalY=0 NormalZ=1 AngleXU=0 Radius=1.5 StartAngle=4.71239 EndAngle=7.85398
    g14: ArcOfCircle CenterX=-1.5 CenterY=56.25 CenterZ=0 NormalX=0 NormalY=0 NormalZ=1 AngleXU=0 Radius=1.5 StartAngle=4.71239 EndAngle=7.85398
    g15: ArcOfCircle CenterX=-11.49 CenterY=50.5 CenterZ=0 NormalX=0 NormalY=0 NormalZ=1 AngleXU=0 Radius=1.5 StartAngle=4.71239 EndAngle=7.85398
    g16: ArcOfCircle CenterX=-16.28 CenterY=44.75 CenterZ=0 NormalX=0 NormalY=0 NormalZ=1 AngleXU=0 Radius=1.5 StartAngle=4.71239 EndAngle=7.85398
    g17: ArcOfCircle CenterX=-18.2337 CenterY=39 CenterZ=0 NormalX=0 NormalY=0 NormalZ=1 AngleXU=0 Radius=1.5 StartAngle=4.71485 EndAngle=7.85398
    g18: ArcOfCircle CenterX=-16.2837 CenterY=27.25 CenterZ=0 NormalX=0 NormalY=0 NormalZ=1 AngleXU=0 Radius=1.5 StartAngle=4.71485 EndAngle=7.85398
    g19: ArcOfCircle CenterX=-18.2337 CenterY=33 CenterZ=0 NormalX=0 NormalY=0 NormalZ=1 AngleXU=0 Radius=1.5 StartAngle=4.71485 EndAngle=7.85398
    g20: ArcOfCircle CenterX=-11.49 CenterY=21.5 CenterZ=0 NormalX=0 NormalY=0 NormalZ=1 AngleXU=0 Radius=1.5 StartAngle=4.71239 EndAngle=7.85398
    g21: ArcOfCircle CenterX=-1.5 CenterY=4.25 CenterZ=0 NormalX=0 NormalY=0 NormalZ=1 AngleXU=0 Radius=1.5 StartAngle=4.71239 EndAngle=7.85398
    g22: ArcOfCircle CenterX=-1.5 CenterY=10 CenterZ=0 NormalX=0 NormalY=0 NormalZ=1 AngleXU=0 Radius=1.5 StartAngle=4.71239 EndAngle=7.85398
    g23: ArcOfCircle CenterX=-1.5 CenterY=15.75 CenterZ=0 NormalX=0 NormalY=0 NormalZ=1 AngleXU=0 Radius=1.5 StartAngle=4.71239 EndAngle=7.85398
    g24: LineSegment StartX=-49.19 StartY=69.25 StartZ=0 EndX=-1.5 EndY=69.25 EndZ=0
    g25: LineSegment StartX=-49.19 StartY=66.25 StartZ=0 EndX=-1.5 EndY=66.25 EndZ=0
    g26: LineSegment StartX=-49.19 StartY=63.5 StartZ=0 EndX=-1.5 EndY=63.5 EndZ=0
    g27: LineSegment StartX=-49.19 StartY=60.5 StartZ=0 EndX=-1.5 EndY=60.5 EndZ=0
    g28: LineSegment StartX=-49.19 StartY=57.75 StartZ=0 EndX=-1.5 EndY=57.75 EndZ=0
    g29: LineSegment StartX=-49.19 StartY=54.75 StartZ=0 EndX=-1.5 EndY=54.75 EndZ=0
    g30: LineSegment StartX=-49.19 StartY=52 StartZ=0 EndX=-11.49 EndY=52 EndZ=0
    g31: LineSegment StartX=-49.19 StartY=49 StartZ=0 EndX=-11.49 EndY=49 EndZ=0
    g32: LineSegment StartX=-49.19 StartY=46.25 StartZ=0 EndX=-16.28 EndY=46.25 EndZ=0
    g33: LineSegment StartX=-49.19 StartY=43.25 StartZ=0 EndX=-16.28 EndY=43.25 EndZ=0
    g34: LineSegment StartX=-49.19 StartY=40.5 StartZ=0 EndX=-18.2337 EndY=40.5 EndZ=0
    g35: LineSegment StartX=-49.19 StartY=37.5 StartZ=0 EndX=-18.23 EndY=37.5 EndZ=0
    g36: LineSegment StartX=-49.19 StartY=34.5 StartZ=0 EndX=-18.2337 EndY=34.5 EndZ=0
    g37: LineSegment StartX=-49.19 StartY=31.5 StartZ=0 EndX=-18.23 EndY=31.5 EndZ=0
    g38: LineSegment StartX=-49.19 StartY=28.75 StartZ=0 EndX=-16.2837 EndY=28.75 EndZ=0
    g39: LineSegment StartX=-49.19 StartY=25.75 StartZ=0 EndX=-16.28 EndY=25.75 EndZ=0
    g40: LineSegment StartX=-49.19 StartY=23 StartZ=0 EndX=-11.49 EndY=23 EndZ=0
    g41: LineSegment StartX=-49.19 StartY=20 StartZ=0 EndX=-11.49 EndY=20 EndZ=0
    g42: LineSegment StartX=-49.19 StartY=17.25 StartZ=0 EndX=-1.5 EndY=17.25 EndZ=0
    g43: LineSegment StartX=-49.19 StartY=14.25 StartZ=0 EndX=-1.5 EndY=14.25 EndZ=0
    g44: LineSegment StartX=-49.19 StartY=11.5 StartZ=0 EndX=-1.5 EndY=11.5 EndZ=0
    g45: LineSegment StartX=-49.19 StartY=8.5 StartZ=0 EndX=-1.5 EndY=8.5 EndZ=0
    g46: LineSegment StartX=-49.19 StartY=5.75 StartZ=0 EndX=-1.5 EndY=5.75 EndZ=0
    g47: LineSegment StartX=-49.19 StartY=2.75 StartZ=0 EndX=-1.5 EndY=2.75 EndZ=0
  constraints (120):
    c: Vertical(g0)
    c: Distance(g0) = 3
    c: Block(g0)
    c: Vertical(g1)
    c: Distance(g1) = 3
    c: Vertical(g2)
    c: Equal(g0,g2) = 3
    c: Block(g2)
    c: Vertical(g3)
    c: Equal(g1,g3) = 3
    c: Vertical(g4)
    c: Equal(g0,g4) = 3
    c: Block(g4)
    c: Vertical(g5)
    c: Equal(g1,g5) = 3
    c: Vertical(g6)
    c: Equal(g0,g6) = 3
    c: Block(g6)
    c: Vertical(g7)
    c: Equal(g1,g7) = 3
    c: Vertical(g8)
    c: Equal(g0,g8) = 3
    c: Block(g8)
    c: Vertical(g9)
    c: Equal(g1,g9) = 3
    c: Vertical(g10)
    c: Equal(g0,g10) = 3
    c: Block(g10)
    c: Vertical(g11)
    c: Equal(g1,g11) = 3
    c: Block(g12)
    c: Block(g13)
    c: Block(g14)
    c: Block(g15)
    c: Block(g16)
    c: Block(g17)
    c: Block(g18)
    c: Block(g19)
    c: Block(g20)
    c: Block(g21)
    c: Block(g22)
    c: Block(g23)
    c: Block(g11)
    c: Block(g9)
    c: Block(g7)
    c: Block(g5)
    c: Block(g3)
    c: Block(g1)
    c: Coincident(g24,g0)
    c: Coincident(g24,g12)
    c: Horizontal(g24)
    c: Coincident(g25,g0)
    c: Coincident(g25,g12)
    c: Horizontal(g25)
    c: Coincident(g26,g1)
    c: Coincident(g26,g13)
    c: Horizontal(g26)
    c: Coincident(g27,g1)
    c: Coincident(g27,g13)
    c: Horizontal(g27)
    c: Coincident(g28,g2)
    c: Coincident(g28,g14)
    c: Horizontal(g28)
    c: Coincident(g29,g2)
    c: Coincident(g29,g14)
    c: Horizontal(g29)
    c: Coincident(g30,g3)
    c: Coincident(g30,g15)
    c: Horizontal(g30)
    c: Coincident(g31,g3)
    c: Coincident(g31,g15)
    c: Horizontal(g31)
    c: Coincident(g32,g4)
    c: Coincident(g32,g16)
    c: Horizontal(g32)
    c: Coincident(g33,g4)
    c: Coincident(g33,g16)
    c: Horizontal(g33)
    c: Coincident(g34,g5)
    c: Coincident(g34,g17)
    c: Horizontal(g34)
    c: Coincident(g35,g5)
    c: Coincident(g35,g17)
    c: Horizontal(g35)
    c: Coincident(g36,g6)
    c: Coincident(g36,g19)
    c: Horizontal(g36)
    c: Coincident(g37,g6)
    c: Coincident(g37,g19)
    c: Horizontal(g37)
    c: Coincident(g38,g7)
    c: Coincident(g38,g18)
    c: Horizontal(g38)
    c: Coincident(g39,g7)
    c: Coincident(g39,g18)
    c: Horizontal(g39)
    c: Coincident(g40,g8)
    c: Coincident(g40,g20)
    c: Horizontal(g40)
    c: Coincident(g41,g8)
    c: Coincident(g41,g20)
    c: Horizontal(g41)
    c: Coincident(g42,g9)
    c: Coincident(g42,g23)
    c: Horizontal(g42)
    c: Coincident(g43,g9)
    c: Coincident(g43,g23)
    c: Horizontal(g43)
    c: Coincident(g44,g10)
    c: Coincident(g44,g22)
    c: Horizontal(g44)
    c: Coincident(g45,g10)
    c: Coincident(g45,g22)
    c: Horizontal(g45)
    c: Coincident(g46,g11)
    c: Coincident(g46,g21)
    c: Horizontal(g46)
    c: Coincident(g47,g11)
    c: Coincident(g47,g21)
    c: Horizontal(g47)
FEATURE [Sketcher::SketchObject] Sketch031
  FullyConstrained = true
  Placement = pos=(117,19,0) rot=(0.57735,0.57735,0.57735;2.0944rad)
  sketch-geometry (24):
    g0: ArcOfCircle CenterX=-49.19 CenterY=67.75 CenterZ=0 NormalX=0 NormalY=0 NormalZ=1 AngleXU=0 Radius=1.5 StartAngle=1.5708 EndAngle=4.71239
    g1: ArcOfCircle CenterX=-49.19 CenterY=62 CenterZ=0 NormalX=0 NormalY=0 NormalZ=1 AngleXU=0 Radius=1.5 StartAngle=1.5708 EndAngle=4.71239
    g2: ArcOfCircle CenterX=-49.19 CenterY=56.25 CenterZ=0 NormalX=0 NormalY=0 NormalZ=1 AngleXU=0 Radius=1.5 StartAngle=1.5708 EndAngle=4.71239
    g3: ArcOfCircle CenterX=-49.19 CenterY=50.5 CenterZ=0 NormalX=0 NormalY=0 NormalZ=1 AngleXU=0 Radius=1.5 StartAngle=1.5708 EndAngle=4.71239
    g4: ArcOfCircle CenterX=-49.19 CenterY=44.75 CenterZ=0 NormalX=0 NormalY=0 NormalZ=1 AngleXU=0 Radius=1.5 StartAngle=1.5708 EndAngle=4.71239
    g5: ArcOfCircle CenterX=-49.19 CenterY=39 CenterZ=0 NormalX=0 NormalY=0 NormalZ=1 AngleXU=0 Radius=1.5 StartAngle=1.5708 EndAngle=4.71239
    g6: ArcOfCircle CenterX=-49.19 CenterY=33 CenterZ=0 NormalX=0 NormalY=0 NormalZ=1 AngleXU=0 Radius=1.5 StartAngle=1.5708 EndAngle=4.71239
    g7: ArcOfCircle CenterX=-49.19 CenterY=27.25 CenterZ=0 NormalX=0 NormalY=0 NormalZ=1 AngleXU=0 Radius=1.5 StartAngle=1.5708 EndAngle=4.71239
    g8: ArcOfCircle CenterX=-49.19 CenterY=21.5 CenterZ=0 NormalX=0 NormalY=0 NormalZ=1 AngleXU=0 Radius=1.5 StartAngle=1.5708 EndAngle=4.71239
    g9: ArcOfCircle CenterX=-49.19 CenterY=15.75 CenterZ=0 NormalX=0 NormalY=0 NormalZ=1 AngleXU=0 Radius=1.5 StartAngle=1.5708 EndAngle=4.71239
    g10: ArcOfCircle CenterX=-49.19 CenterY=10 CenterZ=0 NormalX=0 NormalY=0 NormalZ=1 AngleXU=0 Radius=1.5 StartAngle=1.5708 EndAngle=4.71239
    g11: ArcOfCircle CenterX=-49.19 CenterY=4.25 CenterZ=0 NormalX=0 NormalY=0 NormalZ=1 AngleXU=0 Radius=1.5 StartAngle=1.5708 EndAngle=4.71239
    g12: LineSegment StartX=-49.19 StartY=69.25 StartZ=0 EndX=-49.19 EndY=66.25 EndZ=0
    g13: LineSegment StartX=-49.19 StartY=63.5 StartZ=0 EndX=-49.19 EndY=60.5 EndZ=0
    g14: LineSegment StartX=-49.19 StartY=57.75 StartZ=0 EndX=-49.19 EndY=54.75 EndZ=0
    g15: LineSegment StartX=-49.19 StartY=52 StartZ=0 EndX=-49.19 EndY=49 EndZ=0
    g16: LineSegment StartX=-49.19 StartY=46.25 StartZ=0 EndX=-49.19 EndY=43.25 EndZ=0
    g17: LineSegment StartX=-49.19 StartY=40.5 StartZ=0 EndX=-49.19 EndY=37.5 EndZ=0
    g18: LineSegment StartX=-49.19 StartY=34.5 StartZ=0 EndX=-49.19 EndY=31.5 EndZ=0
    g19: LineSegment StartX=-49.19 StartY=28.75 StartZ=0 EndX=-49.19 EndY=25.75 EndZ=0
    g20: LineSegment StartX=-49.19 StartY=23 StartZ=0 EndX=-49.19 EndY=20 EndZ=0
    g21: LineSegment StartX=-49.19 StartY=17.25 StartZ=0 EndX=-49.19 EndY=14.25 EndZ=0
    g22: LineSegment StartX=-49.19 StartY=11.5 StartZ=0 EndX=-49.19 EndY=8.5 EndZ=0
    g23: LineSegment StartX=-49.19 StartY=5.75 StartZ=0 EndX=-49.19 EndY=2.75 EndZ=0
  constraints (48):
    c: Block(g0)
    c: Block(g1)
    c: Block(g2)
    c: Block(g3)
    c: Block(g4)
    c: Block(g5)
    c: Block(g6)
    c: Block(g7)
    c: Block(g8)
    c: Block(g9)
    c: Block(g10)
    c: Block(g11)
    c: Coincident(g12,g0)
    c: Coincident(g12,g0)
    c: Vertical(g12)
    c: Vertical(g13)
    c: Coincident(g13,g1)
    c: Vertical(g14)
    c: Coincident(g14,g2)
    c: Vertical(g15)
    c: Coincident(g15,g3)
    c: Vertical(g16)
    c: Coincident(g16,g4)
    c: Vertical(g17)
    c: Coincident(g17,g5)
    c: Vertical(g18)
    c: Coincident(g18,g6)
    c: Vertical(g19)
    c: Coincident(g19,g7)
    c: Vertical(g20)
    c: Coincident(g20,g8)
    c: Vertical(g21)
    c: Coincident(g21,g9)
    c: Vertical(g22)
    c: Coincident(g22,g10)
    c: Vertical(g23)
    c: Coincident(g23,g11)
    c: Block(g23)
    c: Block(g22)
    c: Block(g21)
    c: Block(g20)
    c: Block(g13)
    c: Block(g14)
    c: Block(g15)
    c: Block(g16)
    c: Block(g17)
    c: Block(g18)
    c: Block(g19)
FEATURE [Part::Extrusion] Extrude022
  Base = -> Sketch030
  Dir = (1,-2e-16,2e-16)
  DirMode = 2
  FaceMakerClass = Part::FaceMakerBullseye
  LengthFwd = 19
  LengthRev = 0
  Placement = pos=(-19,0,0) rot=(0,0,1;0rad)
  Solid = true
  Symmetric = false
FEATURE [Part::Fillet] Fillet022
  Base = -> Extrude022
  Edges = 24 edges r=1.49: [Edge6,Edge11,Edge18,Edge23,Edge30,Edge35,Edge42,Edge47,Edge54,Edge59,Edge66,Edge71,Edge78,Edge83,Edge90,Edge95,Edge102,Edge107,Edge114,Edge119,Edge126,Edge131,Edge138,Edge143]
FEATURE [Part::Cut] Cut020  label="top010"
  Base = -> Cut019
  Tool = -> Fillet022
FEATURE [Sketcher::SketchObject] Sketch032
  FullyConstrained = true
  Placement = pos=(117,19,0) rot=(0.57735,0.57735,0.57735;2.0944rad)
  sketch-geometry (48):
    g0: LineSegment StartX=-49.19 StartY=69.25 StartZ=0 EndX=-49.19 EndY=66.25 EndZ=0
    g1: LineSegment StartX=-49.19 StartY=63.5 StartZ=0 EndX=-49.19 EndY=60.5 EndZ=0
    g2: LineSegment StartX=-49.19 StartY=57.75 StartZ=0 EndX=-49.19 EndY=54.75 EndZ=0
    g3: LineSegment StartX=-49.19 StartY=52 StartZ=0 EndX=-49.19 EndY=49 EndZ=0
    g4: LineSegment StartX=-49.19 StartY=46.25 StartZ=0 EndX=-49.19 EndY=43.25 EndZ=0
    g5: LineSegment StartX=-49.19 StartY=40.5 StartZ=0 EndX=-49.19 EndY=37.5 EndZ=0
    g6: LineSegment StartX=-49.19 StartY=34.5 StartZ=0 EndX=-49.19 EndY=31.5 EndZ=0
    g7: LineSegment StartX=-49.19 StartY=28.75 StartZ=0 EndX=-49.19 EndY=25.75 EndZ=0
    g8: LineSegment StartX=-49.19 StartY=23 StartZ=0 EndX=-49.19 EndY=20 EndZ=0
    g9: LineSegment StartX=-49.19 StartY=17.25 StartZ=0 EndX=-49.19 EndY=14.25 EndZ=0
    g10: LineSegment StartX=-49.19 StartY=11.5 StartZ=0 EndX=-49.19 EndY=8.5 EndZ=0
    g11: LineSegment StartX=-49.19 StartY=5.75 StartZ=0 EndX=-49.19 EndY=2.75 EndZ=0
    g12: ArcOfCircle CenterX=-1.5 CenterY=67.75 CenterZ=0 NormalX=0 NormalY=0 NormalZ=1 AngleXU=0 Radius=1.5 StartAngle=4.71239 EndAngle=7.85398
    g13: ArcOfCircle CenterX=-1.5 CenterY=62 CenterZ=0 NormalX=0 NormalY=0 NormalZ=1 AngleXU=0 Radius=1.5 StartAngle=4.71239 EndAngle=7.85398
    g14: ArcOfCircle CenterX=-1.5 CenterY=56.25 CenterZ=0 NormalX=0 NormalY=0 NormalZ=1 AngleXU=0 Radius=1.5 StartAngle=4.71239 EndAngle=7.85398
    g15: ArcOfCircle CenterX=-11.49 CenterY=50.5 CenterZ=0 NormalX=0 NormalY=0 NormalZ=1 AngleXU=0 Radius=1.5 StartAngle=4.71239 EndAngle=7.85398
    g16: ArcOfCircle CenterX=-16.28 CenterY=44.75 CenterZ=0 NormalX=0 NormalY=0 NormalZ=1 AngleXU=0 Radius=1.5 StartAngle=4.71239 EndAngle=7.85398
    g17: ArcOfCircle CenterX=-18.2337 CenterY=39 CenterZ=0 NormalX=0 NormalY=0 NormalZ=1 AngleXU=0 Radius=1.5 StartAngle=4.71485 EndAngle=7.85398
    g18: ArcOfCircle CenterX=-16.2837 CenterY=27.25 CenterZ=0 NormalX=0 NormalY=0 NormalZ=1 AngleXU=0 Radius=1.5 StartAngle=4.71485 EndAngle=7.85398
    g19: ArcOfCircle CenterX=-18.2337 CenterY=33 CenterZ=0 NormalX=0 NormalY=0 NormalZ=1 AngleXU=0 Radius=1.5 StartAngle=4.71485 EndAngle=7.85398
    g20: ArcOfCircle CenterX=-11.49 CenterY=21.5 CenterZ=0 NormalX=0 NormalY=0 NormalZ=1 AngleXU=0 Radius=1.5 StartAngle=4.71239 EndAngle=7.85398
    g21: ArcOfCircle CenterX=-1.5 CenterY=4.25 CenterZ=0 NormalX=0 NormalY=0 NormalZ=1 AngleXU=0 Radius=1.5 StartAngle=4.71239 EndAngle=7.85398
    g22: ArcOfCircle CenterX=-1.5 CenterY=10 CenterZ=0 NormalX=0 NormalY=0 NormalZ=1 AngleXU=0 Radius=1.5 StartAngle=4.71239 EndAngle=7.85398
    g23: ArcOfCircle CenterX=-1.5 CenterY=15.75 CenterZ=0 NormalX=0 NormalY=0 NormalZ=1 AngleXU=0 Radius=1.5 StartAngle=4.71239 EndAngle=7.85398
    g24: LineSegment StartX=-49.19 StartY=69.25 StartZ=0 EndX=-1.5 EndY=69.25 EndZ=0
    g25: LineSegment StartX=-49.19 StartY=66.25 StartZ=0 EndX=-1.5 EndY=66.25 EndZ=0
    g26: LineSegment StartX=-49.19 StartY=63.5 StartZ=0 EndX=-1.5 EndY=63.5 EndZ=0
    g27: LineSegment StartX=-49.19 StartY=60.5 StartZ=0 EndX=-1.5 EndY=60.5 EndZ=0
    g28: LineSegment StartX=-49.19 StartY=57.75 StartZ=0 EndX=-1.5 EndY=57.75 EndZ=0
    g29: LineSegment StartX=-49.19 StartY=54.75 StartZ=0 EndX=-1.5 EndY=54.75 EndZ=0
    g30: LineSegment StartX=-49.19 StartY=52 StartZ=0 EndX=-11.49 EndY=52 EndZ=0
    g31: LineSegment StartX=-49.19 StartY=49 StartZ=0 EndX=-11.49 EndY=49 EndZ=0
    g32: LineSegment StartX=-49.19 StartY=46.25 StartZ=0 EndX=-16.28 EndY=46.25 EndZ=0
    g33: LineSegment StartX=-49.19 StartY=43.25 StartZ=0 EndX=-16.28 EndY=43.25 EndZ=0
    g34: LineSegment StartX=-49.19 StartY=40.5 StartZ=0 EndX=-18.2337 EndY=40.5 EndZ=0
    g35: LineSegment StartX=-49.19 StartY=37.5 StartZ=0 EndX=-18.23 EndY=37.5 EndZ=0
    g36: LineSegment StartX=-49.19 StartY=34.5 StartZ=0 EndX=-18.2337 EndY=34.5 EndZ=0
    g37: LineSegment StartX=-49.19 StartY=31.5 StartZ=0 EndX=-18.23 EndY=31.5 EndZ=0
    g38: LineSegment StartX=-49.19 StartY=28.75 StartZ=0 EndX=-16.2837 EndY=28.75 EndZ=0
    g39: LineSegment StartX=-49.19 StartY=25.75 StartZ=0 EndX=-16.28 EndY=25.75 EndZ=0
    g40: LineSegment StartX=-49.19 StartY=23 StartZ=0 EndX=-11.49 EndY=23 EndZ=0
    g41: LineSegment StartX=-49.19 StartY=20 StartZ=0 EndX=-11.49 EndY=20 EndZ=0
    g42: LineSegment StartX=-49.19 StartY=17.25 StartZ=0 EndX=-1.5 EndY=17.25 EndZ=0
    g43: LineSegment StartX=-49.19 StartY=14.25 StartZ=0 EndX=-1.5 EndY=14.25 EndZ=0
    g44: LineSegment StartX=-49.19 StartY=11.5 StartZ=0 EndX=-1.5 EndY=11.5 EndZ=0
    g45: LineSegment StartX=-49.19 StartY=8.5 StartZ=0 EndX=-1.5 EndY=8.5 EndZ=0
    g46: LineSegment StartX=-49.19 StartY=5.75 StartZ=0 EndX=-1.5 EndY=5.75 EndZ=0
    g47: LineSegment StartX=-49.19 StartY=2.75 StartZ=0 EndX=-1.5 EndY=2.75 EndZ=0
  constraints (120):
    c: Vertical(g0)
    c: Distance(g0) = 3
    c: Block(g0)
    c: Vertical(g1)
    c: Distance(g1) = 3
    c: Vertical(g2)
    c: Equal(g0,g2) = 3
    c: Block(g2)
    c: Vertical(g3)
    c: Equal(g1,g3) = 3
    c: Vertical(g4)
    c: Equal(g0,g4) = 3
    c: Block(g4)
    c: Vertical(g5)
    c: Equal(g1,g5) = 3
    c: Vertical(g6)
    c: Equal(g0,g6) = 3
    c: Block(g6)
    c: Vertical(g7)
    c: Equal(g1,g7) = 3
    c: Vertical(g8)
    c: Equal(g0,g8) = 3
    c: Block(g8)
    c: Vertical(g9)
    c: Equal(g1,g9) = 3
    c: Vertical(g10)
    c: Equal(g0,g10) = 3
    c: Block(g10)
    c: Vertical(g11)
    c: Equal(g1,g11) = 3
    c: Block(g12)
    c: Block(g13)
    c: Block(g14)
    c: Block(g15)
    c: Block(g16)
    c: Block(g17)
    c: Block(g18)
    c: Block(g19)
    c: Block(g20)
    c: Block(g21)
    c: Block(g22)
    c: Block(g23)
    c: Block(g11)
    c: Block(g9)
    c: Block(g7)
    c: Block(g5)
    c: Block(g3)
    c: Block(g1)
    c: Coincident(g24,g0)
    c: Coincident(g24,g12)
    c: Horizontal(g24)
    c: Coincident(g25,g0)
    c: Coincident(g25,g12)
    c: Horizontal(g25)
    c: Coincident(g26,g1)
    c: Coincident(g26,g13)
    c: Horizontal(g26)
    c: Coincident(g27,g1)
    c: Coincident(g27,g13)
    c: Horizontal(g27)
    c: Coincident(g28,g2)
    c: Coincident(g28,g14)
    c: Horizontal(g28)
    c: Coincident(g29,g2)
    c: Coincident(g29,g14)
    c: Horizontal(g29)
    c: Coincident(g30,g3)
    c: Coincident(g30,g15)
    c: Horizontal(g30)
    c: Coincident(g31,g3)
    c: Coincident(g31,g15)
    c: Horizontal(g31)
    c: Coincident(g32,g4)
    c: Coincident(g32,g16)
    c: Horizontal(g32)
    c: Coincident(g33,g4)
    c: Coincident(g33,g16)
    c: Horizontal(g33)
    c: Coincident(g34,g5)
    c: Coincident(g34,g17)
    c: Horizontal(g34)
    c: Coincident(g35,g5)
    c: Coincident(g35,g17)
    c: Horizontal(g35)
    c: Coincident(g36,g6)
    c: Coincident(g36,g19)
    c: Horizontal(g36)
    c: Coincident(g37,g6)
    c: Coincident(g37,g19)
    c: Horizontal(g37)
    c: Coincident(g38,g7)
    c: Coincident(g38,g18)
    c: Horizontal(g38)
    c: Coincident(g39,g7)
    c: Coincident(g39,g18)
    c: Horizontal(g39)
    c: Coincident(g40,g8)
    c: Coincident(g40,g20)
    c: Horizontal(g40)
    c: Coincident(g41,g8)
    c: Coincident(g41,g20)
    c: Horizontal(g41)
    c: Coincident(g42,g9)
    c: Coincident(g42,g23)
    c: Horizontal(g42)
    c: Coincident(g43,g9)
    c: Coincident(g43,g23)
    c: Horizontal(g43)
    c: Coincident(g44,g10)
    c: Coincident(g44,g22)
    c: Horizontal(g44)
    c: Coincident(g45,g10)
    c: Coincident(g45,g22)
    c: Horizontal(g45)
    c: Coincident(g46,g11)
    c: Coincident(g46,g21)
    c: Horizontal(g46)
    c: Coincident(g47,g11)
    c: Coincident(g47,g21)
    c: Horizontal(g47)
FEATURE [Part::Extrusion] Extrude023
  Base = -> Sketch032
  Dir = (1,-2e-16,2e-16)
  DirMode = 2
  FaceMakerClass = Part::FaceMakerBullseye
  LengthFwd = 19
  LengthRev = 0
  Placement = pos=(-19,0,0) rot=(0,0,1;0rad)
  Solid = true
  Symmetric = false
FEATURE [Part::Fillet] Fillet023
  Base = -> Extrude023
  Edges = <same value as first occurrence — deduplicated (x6 in doc)>
  Placement = pos=(0,0.05,0) rot=(0,0,1;0rad)
FEATURE [Part::Cut] Cut014  label="bottom003"
  Base = -> Cut007
  Tool = -> Fusion047
FEATURE [Part::Cut] Cut021  label="bottom004"
  Base = -> Cut014
  Tool = -> Fillet023
FEATURE [Sketcher::SketchObject] Sketch033
  FullyConstrained = true
  Placement = pos=(117,19,0) rot=(0.57735,0.57735,0.57735;2.0944rad)
  sketch-geometry (8):
    g0: LineSegment StartX=-49.19 StartY=69.25 StartZ=0 EndX=-49.19 EndY=66.25 EndZ=0
    g1: LineSegment StartX=-49.19 StartY=5.75 StartZ=0 EndX=-49.19 EndY=2.75 EndZ=0
    g2: ArcOfCircle CenterX=-1.5 CenterY=67.75 CenterZ=0 NormalX=0 NormalY=0 NormalZ=1 AngleXU=0 Radius=1.5 StartAngle=4.71239 EndAngle=7.85398
    g3: ArcOfCircle CenterX=-1.5 CenterY=4.25 CenterZ=0 NormalX=0 NormalY=0 NormalZ=1 AngleXU=0 Radius=1.5 StartAngle=4.71239 EndAngle=7.85398
    g4: LineSegment StartX=-49.19 StartY=69.25 StartZ=0 EndX=-1.5 EndY=69.25 EndZ=0
    g5: LineSegment StartX=-49.19 StartY=66.25 StartZ=0 EndX=-1.5 EndY=66.25 EndZ=0
    g6: LineSegment StartX=-49.19 StartY=5.75 StartZ=0 EndX=-1.5 EndY=5.75 EndZ=0
    g7: LineSegment StartX=-49.19 StartY=2.75 StartZ=0 EndX=-1.5 EndY=2.75 EndZ=0
  constraints (19):
    c: Vertical(g0)
    c: Distance(g0) = 3
    c: Block(g0)
    c: Vertical(g1)
    c: Block(g2)
    c: Block(g3)
    c: Block(g1)
    c: Coincident(g4,g0)
    c: Coincident(g4,g2)
    c: Horizontal(g4)
    c: Coincident(g5,g0)
    c: Coincident(g5,g2)
    c: Horizontal(g5)
    c: Coincident(g6,g1)
    c: Coincident(g6,g3)
    c: Horizontal(g6)
    c: Coincident(g7,g1)
    c: Coincident(g7,g3)
    c: Horizontal(g7)
FEATURE [Sketcher::SketchObject] Sketch034
  FullyConstrained = true
  Placement = pos=(117,19,0) rot=(0.57735,0.57735,0.57735;2.0944rad)
  sketch-geometry (8):
    g0: LineSegment StartX=-49.19 StartY=63.5 StartZ=0 EndX=-49.19 EndY=60.5 EndZ=0
    g1: LineSegment StartX=-49.19 StartY=11.5 StartZ=0 EndX=-49.19 EndY=8.5 EndZ=0
    g2: ArcOfCircle CenterX=-1.5 CenterY=62 CenterZ=0 NormalX=0 NormalY=0 NormalZ=1 AngleXU=0 Radius=1.5 StartAngle=4.71239 EndAngle=7.85398
    g3: ArcOfCircle CenterX=-1.5 CenterY=10 CenterZ=0 NormalX=0 NormalY=0 NormalZ=1 AngleXU=0 Radius=1.5 StartAngle=4.71239 EndAngle=7.85398
    g4: LineSegment StartX=-49.19 StartY=63.5 StartZ=0 EndX=-1.5 EndY=63.5 EndZ=0
    g5: LineSegment StartX=-49.19 StartY=60.5 StartZ=0 EndX=-1.5 EndY=60.5 EndZ=0
    g6: LineSegment StartX=-49.19 StartY=11.5 StartZ=0 EndX=-1.5 EndY=11.5 EndZ=0
    g7: LineSegment StartX=-49.19 StartY=8.5 StartZ=0 EndX=-1.5 EndY=8.5 EndZ=0
  constraints (19):
    c: Vertical(g0)
    c: Distance(g0) = 3
    c: Vertical(g1)
    c: Block(g1)
    c: Block(g2)
    c: Block(g3)
    c: Block(g0)
    c: Coincident(g4,g0)
    c: Coincident(g4,g2)
    c: Horizontal(g4)
    c: Coincident(g5,g0)
    c: Coincident(g5,g2)
    c: Horizontal(g5)
    c: Coincident(g6,g1)
    c: Coincident(g6,g3)
    c: Horizontal(g6)
    c: Coincident(g7,g1)
    c: Coincident(g7,g3)
    c: Horizontal(g7)
FEATURE [Part::Extrusion] Extrude024
  Base = -> Sketch033
  Dir = (1,0,0)
  DirMode = 2
  FaceMakerClass = Part::FaceMakerBullseye
  LengthFwd = 10
  LengthRev = 0
  Solid = true
  Symmetric = false
FEATURE [Part::Extrusion] Extrude025
  Base = -> Sketch034
  Dir = (1,0,0)
  DirMode = 2
  FaceMakerClass = Part::FaceMakerBullseye
  LengthFwd = 10
  LengthRev = 0
  Solid = true
  Symmetric = false
FEATURE [Part::Fillet] Fillet024  label="removeFromtMoreFrontCaseScrewRetainers"
  Base = -> Extrude024
  Edges = 4 edges r=1.49: [Edge6,Edge11,Edge18,Edge23]
  Placement = pos=(-11,0,0) rot=(0,0,1;0rad)
FEATURE [Part::Fillet] Fillet025  label="removeFromtMoreFrontCaseScrewRetainers001"
  Base = -> Extrude025
  Edges = 4 edges r=1.49: [Edge6,Edge11,Edge18,Edge23]
  Placement = pos=(-19,0,0) rot=(0,0,1;0rad)
FEATURE [Part::Cut] Cut022
  Base = -> Cut015
  Tool = -> Fillet025
FEATURE [Part::Cut] Cut023  label="screwRetainers"
  Base = -> Cut022
  Tool = -> Fillet024
FEATURE [Part::MultiFuse] Fusion056  label="bottom005"
  Shapes = -> [Fusion044,Cut021]
FEATURE [Part::MultiFuse] Fusion057  label="casePillars001"
  Shapes = -> [Cut016,Fusion052]
FEATURE [Part::MultiFuse] Fusion058  label="bottom006"
  Shapes = -> [Fusion056,Cut023]
FEATURE [Part::MultiFuse] Fusion059  label="bottom007"
  Shapes = -> [Fusion058,Fillet005]
FEATURE [Part::MultiFuse] Fusion060  label="bottom008"
  Shapes = -> [Fusion059,Fusion]
FEATURE [Part::MultiFuse] Fusion061  label="top011"
  Shapes = -> [Cut006,Cut020]
FEATURE [Part::MultiFuse] Fusion062  label="top012"
  Shapes = -> [Fusion057,Fusion061]
FEATURE [Sketcher::SketchObject] Sketch035  label="topSketch007"
  FullyConstrained = true
  sketch-geometry (6):
    g0: LineSegment StartX=19 StartY=38 StartZ=0 EndX=117 EndY=38 EndZ=0
    g1: ArcOfCircle CenterX=19 CenterY=19 CenterZ=0 NormalX=0 NormalY=0 NormalZ=1 AngleXU=0 Radius=19 StartAngle=1.5708 EndAngle=3.14159
    g2: LineSegment StartX=117 StartY=38 StartZ=0 EndX=117 EndY=19 EndZ=0
    g3: LineSegment StartX=98 StartY=1.0161e-12 StartZ=0 EndX=5.22862e-06 EndY=1.0161e-12 EndZ=0
    g4: LineSegment StartX=5.22862e-06 StartY=19 StartZ=0 EndX=5.22862e-06 EndY=1.0161e-12 EndZ=0
    g5: ArcOfCircle CenterX=98 CenterY=19 CenterZ=0 NormalX=0 NormalY=0 NormalZ=1 AngleXU=0 Radius=19 StartAngle=4.71239 EndAngle=6.28319
  constraints (16):
    c: Horizontal(g0)
    c: Distance(g0) = 98
    c: Coincident(g1,g0)
    c: Block(g1)
    c: Coincident(g2,g0)
    c: Vertical(g2)
    c: Distance(g2) = 19
    c: Horizontal(g3)
    c: Coincident(g4,g1)
    c: Vertical(g4)
    c: Coincident(g3,g4)
    c: Block(g3)
    c: Coincident(g5,g2)
    c: Coincident(g5,g3)
    c: Block(g0)
    c: Block(g5)
FEATURE [Part::Extrusion] Extrude026  label="sideA001"
  Base = -> Sketch035
  Dir = (0,0,1)
  DirMode = 2
  FaceMakerClass = Part::FaceMakerBullseye
  LengthFwd = 3
  LengthRev = 0
  Placement = pos=(0,0,-2.7) rot=(0,0,1;0rad)
  Solid = true
  Symmetric = false
FEATURE [Sketcher::SketchObject] Sketch036  label="topSketch008"
  FullyConstrained = true
  sketch-geometry (6):
    g0: LineSegment StartX=19 StartY=38 StartZ=0 EndX=117 EndY=38 EndZ=0
    g1: ArcOfCircle CenterX=19 CenterY=19 CenterZ=0 NormalX=0 NormalY=0 NormalZ=1 AngleXU=0 Radius=19 StartAngle=1.5708 EndAngle=3.14159
    g2: LineSegment StartX=117 StartY=38 StartZ=0 EndX=117 EndY=19 EndZ=0
    g3: LineSegment StartX=98 StartY=1.0161e-12 StartZ=0 EndX=5.22862e-06 EndY=1.0161e-12 EndZ=0
    g4: LineSegment StartX=5.22862e-06 StartY=19 StartZ=0 EndX=5.22862e-06 EndY=1.0161e-12 EndZ=0
    g5: ArcOfCircle CenterX=98 CenterY=19 CenterZ=0 NormalX=0 NormalY=0 NormalZ=1 AngleXU=0 Radius=19 StartAngle=4.71239 EndAngle=6.28319
  constraints (16):
    c: Horizontal(g0)
    c: Distance(g0) = 98
    c: Coincident(g1,g0)
    c: Block(g1)
    c: Coincident(g2,g0)
    c: Vertical(g2)
    c: Distance(g2) = 19
    c: Horizontal(g3)
    c: Coincident(g4,g1)
    c: Vertical(g4)
    c: Coincident(g3,g4)
    c: Block(g3)
    c: Coincident(g5,g2)
    c: Coincident(g5,g3)
    c: Block(g0)
    c: Block(g5)
FEATURE [Part::Extrusion] Extrude027  label="sideB001"
  Base = -> Sketch036
  Dir = (0,0,1)
  DirMode = 2
  FaceMakerClass = Part::FaceMakerBullseye
  LengthFwd = 3
  LengthRev = 0
  Placement = pos=(0,0,71.7) rot=(0,0,1;0rad)
  Solid = true
  Symmetric = false
FEATURE [Part::MultiFuse] Fusion064  label="removeFromBottom"
  Shapes = -> [Extrude026,Extrude027]
FEATURE [Part::Cut] Cut024  label="bottom009"
  Base = -> Fusion060
  Tool = -> Fusion064
FEATURE [Sketcher::SketchObject] Sketch037  label="topSketch009"
  FullyConstrained = true
  sketch-geometry (8):
    g0: ArcOfCircle CenterX=19 CenterY=19.1201 CenterZ=0 NormalX=0 NormalY=0 NormalZ=1 AngleXU=0 Radius=18.8799 StartAngle=1.5708 EndAngle=3.14793
    g1: LineSegment StartX=0.120501 StartY=19.0004 StartZ=0 EndX=0.120501 EndY=0.000382114 EndZ=0
    g2: LineSegment StartX=19 StartY=38 StartZ=0 EndX=124 EndY=38 EndZ=0
    g3: LineSegment StartX=0.120501 StartY=0.000382114 StartZ=0 EndX=105.121 EndY=0.000382114 EndZ=0
    g4: LineSegment StartX=124 StartY=38 StartZ=0 EndX=125.616 EndY=38 EndZ=0
    g5: LineSegment StartX=105.121 StartY=0.000382114 StartZ=0 EndX=106.736 EndY=0.000382114 EndZ=0
    g6: ArcOfCircle CenterX=106.616 CenterY=19 CenterZ=0 NormalX=0 NormalY=0 NormalZ=1 AngleXU=0 Radius=19 StartAngle=4.71873 EndAngle=6.28319
    g7: LineSegment StartX=125.616 StartY=38 StartZ=0 EndX=125.616 EndY=19 EndZ=0
  constraints (21):
    c: Block(g0)
    c: Coincident(g1,g0)
    c: Vertical(g1)
    c: Horizontal(g2)
    c: Distance(g2) = 105
    c: Coincident(g2,g0)
    c: Distance(g1) = 19
    c: Coincident(g3,g1)
    c: Horizontal(g3)
    c: Distance(g3) = 105
    c: Coincident(g4,g2)
    c: Horizontal(g4)
    c: Distance(g4) = 1.61553
    c: Horizontal(g5)
    c: Equal(g4,g5) = 1.61553
    c: Coincident(g5,g3)
    c: Block(g6)
    c: Coincident(g6,g5)
    c: Coincident(g7,g4)
    c: Coincident(g7,g6)
    c: Vertical(g7)
FEATURE [Part::Extrusion] Extrude028  label="sideB"
  Base = -> Sketch037
  Dir = (0,0,1)
  DirMode = 2
  FaceMakerClass = Part::FaceMakerBullseye
  LengthFwd = 3
  LengthRev = 0
  Placement = pos=(0,0,72) rot=(0,0,1;0rad)
  Solid = true
  Symmetric = false
FEATURE [Sketcher::SketchObject] Sketch038  label="topSketch010"
  FullyConstrained = true
  sketch-geometry (22):
    g0: LineSegment StartX=5.21097e-06 StartY=3 StartZ=0 EndX=5.21097e-06 EndY=19 EndZ=0
    g1: ArcOfCircle CenterX=19 CenterY=19 CenterZ=0 NormalX=0 NormalY=0 NormalZ=1 AngleXU=0 Radius=19 StartAngle=1.5708 EndAngle=3.14159
    g2: ArcOfCircle CenterX=19 CenterY=19 CenterZ=0 NormalX=0 NormalY=0 NormalZ=1 AngleXU=0 Radius=16 StartAngle=1.5708 EndAngle=3.14159
    g3: LineSegment StartX=114 StartY=35 StartZ=0 EndX=19 EndY=35 EndZ=0
    g4: LineSegment StartX=5.21097e-06 StartY=3 StartZ=0 EndX=5.21097e-06 EndY=0 EndZ=0
    g5: LineSegment StartX=3 StartY=0 StartZ=0 EndX=5.21097e-06 EndY=0 EndZ=0
    g6: LineSegment StartX=3 StartY=19 StartZ=0 EndX=3 EndY=0 EndZ=0
    g7: LineSegment StartX=19 StartY=38 StartZ=0 EndX=124 EndY=38 EndZ=0
    g8: Circle CenterX=119 CenterY=35 CenterZ=0 NormalX=0 NormalY=0 NormalZ=1 AngleXU=0 Radius=1
    g9: Circle CenterX=121 CenterY=35 CenterZ=0 NormalX=0 NormalY=0 NormalZ=1 AngleXU=0 Radius=1
    g10: Circle CenterX=121 CenterY=33 CenterZ=0 NormalX=0 NormalY=0 NormalZ=1 AngleXU=0 Radius=1
    g11: BSplineCurve PolesCount=3 KnotsCount=2 Degree=2 IsPeriodic=0
    g12: GeomPoint X=119 Y=35 Z=0
    g13: GeomPoint X=121 Y=33 Z=0
    g14: LineSegment StartX=119 StartY=35 StartZ=0 EndX=114 EndY=35 EndZ=0
    g15: ArcOfCircle CenterX=105 CenterY=19 CenterZ=0 NormalX=0 NormalY=0 NormalZ=1 AngleXU=0 Radius=16 StartAngle=5.60905 EndAngle=6.28319
    g16: LineSegment StartX=121 StartY=33 StartZ=0 EndX=121 EndY=19 EndZ=0
    g17: LineSegment StartX=117.5 StartY=9.01251 StartZ=0 EndX=121.163 EndY=9.0125 EndZ=0
    g18: ArcOfCircle CenterX=105 CenterY=19 CenterZ=0 NormalX=0 NormalY=0 NormalZ=1 AngleXU=0 Radius=20.6155 StartAngle=5.7297 EndAngle=6.28319
    g19: LineSegment StartX=121.163 StartY=9.0125 StartZ=0 EndX=122.538 EndY=8.16329 EndZ=0
    g20: LineSegment StartX=124 StartY=38 StartZ=0 EndX=125.616 EndY=38 EndZ=0
    g21: LineSegment StartX=125.616 StartY=19 StartZ=0 EndX=125.616 EndY=38 EndZ=0
  constraints (49):
    c: Vertical(g0)
    c: Block(g0)
    c: Coincident(g1,g0)
    c: Block(g1)
    c: Coincident(g2,g1)
    c: Block(g2)
    c: Coincident(g3,g2)
    c: Horizontal(g3)
    c: Tangent(g3,g2)
    c: Coincident(g4,g0)
    c: Distance(g4) = 3
    c: Vertical(g4)
    c: Coincident(g5,g4)
    c: Horizontal(g5)
    c: Coincident(g6,g2)
    c: Coincident(g6,g5)
    c: Vertical(g6)
    c: Horizontal(g7)
    c: Distance(g7) = 105
    c: Coincident(g7,g1)
    c: Block(g3)
    c: Weight(g8) = 1
    c: Equal(g8,g9)
    c: Equal(g8,g10)
    c: InternalAlignment(g8,g11)
    c: InternalAlignment(g9,g11)
    c: InternalAlignment(g10,g11)
    c: InternalAlignment(g12,g11)
    c: InternalAlignment(g13,g11)
    c: Block(g11)
    c: Coincident(g14,g11)
    c: Coincident(g14,g3)
    c: Horizontal(g14)
    c: Block(g15)
    c: Coincident(g16,g11)
    c: Coincident(g16,g15)
    c: Vertical(g16)
    c: Distance(g16) = 14
    c: Coincident(g17,g15)
    c: Block(g18)
    c: Coincident(g19,g18)
    c: Coincident(g20,g7)
    c: Horizontal(g20)
    c: Vertical(g21)
    c: Coincident(g20,g21)
    c: Block(g20)
    c: Block(g21)
    c: Block(g19)
    c: Block(g17)
FEATURE [Part::Extrusion] Extrude029
  Base = -> Sketch038
  Dir = (0,0,1)
  DirMode = 2
  FaceMakerClass = Part::FaceMakerBullseye
  LengthFwd = 72
  LengthRev = 0
  Solid = true
  Symmetric = false
FEATURE [Part::Feature] Face085
  shape: bbox 4.8 x 25.5 x 2e-07 mm, 1 faces, 0 solids (baked)
FEATURE [Part::Revolution] Revolve089  label="moreFrontCaseScrewPost003"
  Angle = 360
  Axis = (0,1,0)
  Base = (0,0,0)
  FaceMakerClass = Part::FaceMakerBullseye
  Placement = pos=(109.5,4.5,3.5) rot=(0,0,1;0rad)
  Solid = false
  Source = -> Face085
  Symmetric = false
FEATURE [Part::Feature] Face086
  shape: bbox 4.8 x 25.5 x 2e-07 mm, 1 faces, 0 solids (baked)
FEATURE [Part::Revolution] Revolve090  label="moreFrontCaseScrewPost004"
  Angle = 360
  Axis = (0,1,0)
  Base = (0,0,0)
  FaceMakerClass = Part::FaceMakerBullseye
  Placement = pos=(109.5,4.5,68.5) rot=(0,0,1;0rad)
  Solid = false
  Source = -> Face086
  Symmetric = false
FEATURE [Part::Fillet] Fillet026  label="top013"
  Base = -> Extrude029
  Edges = 1 edges r=2: [Edge35]
FEATURE [Sketcher::SketchObject] Sketch039
  FullyConstrained = true
  sketch-geometry (7):
    g0: LineSegment StartX=0 StartY=0 StartZ=0 EndX=0 EndY=6 EndZ=0
    g1: Circle CenterX=0 CenterY=0 CenterZ=0 NormalX=0 NormalY=0 NormalZ=1 AngleXU=0 Radius=1
    g2: Circle CenterX=8 CenterY=6 CenterZ=0 NormalX=0 NormalY=0 NormalZ=1 AngleXU=0 Radius=1
    g3: BSplineCurve PolesCount=3 KnotsCount=2 Degree=2 IsPeriodic=0
    g4: GeomPoint X=0 Y=0 Z=0
    g5: GeomPoint X=8 Y=6 Z=0
    g6: LineSegment StartX=0 StartY=6 StartZ=0 EndX=8 EndY=6 EndZ=0
  constraints (14):
    c: Coincident(g0,g-1)
    c: Distance(g0) = 6
    c: Vertical(g0)
    c: Coincident(g3,g0)
    c: Weight(g1) = 1
    c: Equal(g1,g2)
    c: InternalAlignment(g1,g3)
    c: InternalAlignment(g2,g3)
    c: InternalAlignment(g4,g3)
    c: InternalAlignment(g5,g3)
    c: Block(g3)
    c: Coincident(g6,g0)
    c: Coincident(g6,g3)
    c: Horizontal(g6)
FEATURE [Sketcher::SketchObject] Sketch040
  FullyConstrained = true
  sketch-geometry (7):
    g0: LineSegment StartX=0 StartY=0 StartZ=0 EndX=0 EndY=6 EndZ=0
    g1: Circle CenterX=0 CenterY=0 CenterZ=0 NormalX=0 NormalY=0 NormalZ=1 AngleXU=0 Radius=1
    g2: Circle CenterX=8 CenterY=6 CenterZ=0 NormalX=0 NormalY=0 NormalZ=1 AngleXU=0 Radius=1
    g3: BSplineCurve PolesCount=3 KnotsCount=2 Degree=2 IsPeriodic=0
    g4: GeomPoint X=0 Y=0 Z=0
    g5: GeomPoint X=8 Y=6 Z=0
    g6: LineSegment StartX=0 StartY=6 StartZ=0 EndX=8 EndY=6 EndZ=0
  constraints (14):
    c: Coincident(g0,g-1)
    c: Distance(g0) = 6
    c: Vertical(g0)
    c: Coincident(g3,g0)
    c: Weight(g1) = 1
    c: Equal(g1,g2)
    c: InternalAlignment(g1,g3)
    c: InternalAlignment(g2,g3)
    c: InternalAlignment(g4,g3)
    c: InternalAlignment(g5,g3)
    c: Block(g3)
    c: Coincident(g6,g0)
    c: Coincident(g6,g3)
    c: Horizontal(g6)
FEATURE [Sketcher::SketchObject] Sketch041
  FullyConstrained = true
  sketch-geometry (7):
    g0: LineSegment StartX=0 StartY=0 StartZ=0 EndX=0 EndY=6 EndZ=0
    g1: Circle CenterX=0 CenterY=0 CenterZ=0 NormalX=0 NormalY=0 NormalZ=1 AngleXU=0 Radius=1
    g2: Circle CenterX=8 CenterY=6 CenterZ=0 NormalX=0 NormalY=0 NormalZ=1 AngleXU=0 Radius=1
    g3: BSplineCurve PolesCount=3 KnotsCount=2 Degree=2 IsPeriodic=0
    g4: GeomPoint X=0 Y=0 Z=0
    g5: GeomPoint X=8 Y=6 Z=0
    g6: LineSegment StartX=0 StartY=6 StartZ=0 EndX=8 EndY=6 EndZ=0
  constraints (14):
    c: Coincident(g0,g-1)
    c: Distance(g0) = 6
    c: Vertical(g0)
    c: Coincident(g3,g0)
    c: Weight(g1) = 1
    c: Equal(g1,g2)
    c: InternalAlignment(g1,g3)
    c: InternalAlignment(g2,g3)
    c: InternalAlignment(g4,g3)
    c: InternalAlignment(g5,g3)
    c: Block(g3)
    c: Coincident(g6,g0)
    c: Coincident(g6,g3)
    c: Horizontal(g6)
FEATURE [Sketcher::SketchObject] Sketch042
  FullyConstrained = true
  sketch-geometry (7):
    g0: LineSegment StartX=0 StartY=0 StartZ=0 EndX=0 EndY=6 EndZ=0
    g1: Circle CenterX=0 CenterY=0 CenterZ=0 NormalX=0 NormalY=0 NormalZ=1 AngleXU=0 Radius=1
    g2: Circle CenterX=8 CenterY=6 CenterZ=0 NormalX=0 NormalY=0 NormalZ=1 AngleXU=0 Radius=1
    g3: BSplineCurve PolesCount=3 KnotsCount=2 Degree=2 IsPeriodic=0
    g4: GeomPoint X=0 Y=0 Z=0
    g5: GeomPoint X=8 Y=6 Z=0
    g6: LineSegment StartX=0 StartY=6 StartZ=0 EndX=8 EndY=6 EndZ=0
  constraints (14):
    c: Coincident(g0,g-1)
    c: Distance(g0) = 6
    c: Vertical(g0)
    c: Coincident(g3,g0)
    c: Weight(g1) = 1
    c: Equal(g1,g2)
    c: InternalAlignment(g1,g3)
    c: InternalAlignment(g2,g3)
    c: InternalAlignment(g4,g3)
    c: InternalAlignment(g5,g3)
    c: Block(g3)
    c: Coincident(g6,g0)
    c: Coincident(g6,g3)
    c: Horizontal(g6)
FEATURE [Part::Extrusion] Extrude030  label="caseScrewPillarBracket008"
  Base = -> Sketch039
  Dir = (0,0,1)
  DirMode = 2
  FaceMakerClass = Part::FaceMakerBullseye
  LengthFwd = 2.4
  LengthRev = 0
  Placement = pos=(15.76,29,8.8) rot=(0,1,0;0rad)
  Solid = true
  Symmetric = false
FEATURE [Part::Extrusion] Extrude031  label="caseScrewPillarBracket009"
  Base = -> Sketch040
  Dir = (0,0,1)
  DirMode = 2
  FaceMakerClass = Part::FaceMakerBullseye
  LengthFwd = 2.4
  LengthRev = 0
  Placement = pos=(15.76,29,60.8) rot=(0,0,1;0rad)
  Solid = true
  Symmetric = false
FEATURE [Part::Extrusion] Extrude032  label="caseScrewPillarBracket010"
  Base = -> Sketch041
  Dir = (0,0,1)
  DirMode = 2
  FaceMakerClass = Part::FaceMakerBullseye
  LengthFwd = 2.4
  LengthRev = 0
  Placement = pos=(13.7,29,13.26) rot=(0,-1,0;1.5708rad)
  Solid = true
  Symmetric = false
FEATURE [Part::Extrusion] Extrude033  label="caseScrewPillarBracket011"
  Base = -> Sketch042
  Dir = (0,0,1)
  DirMode = 2
  FaceMakerClass = Part::FaceMakerBullseye
  LengthFwd = 2.4
  LengthRev = 0
  Placement = pos=(11.3,29,58.74) rot=(0,1,0;1.5708rad)
  Solid = true
  Symmetric = false
FEATURE [Sketcher::SketchObject] Sketch043
  FullyConstrained = true
  sketch-geometry (7):
    g0: LineSegment StartX=0 StartY=0 StartZ=0 EndX=0 EndY=6 EndZ=0
    g1: Circle CenterX=0 CenterY=0 CenterZ=0 NormalX=0 NormalY=0 NormalZ=1 AngleXU=0 Radius=1
    g2: Circle CenterX=8 CenterY=6 CenterZ=0 NormalX=0 NormalY=0 NormalZ=1 AngleXU=0 Radius=1
    g3: BSplineCurve PolesCount=3 KnotsCount=2 Degree=2 IsPeriodic=0
    g4: GeomPoint X=0 Y=0 Z=0
    g5: GeomPoint X=8 Y=6 Z=0
    g6: LineSegment StartX=0 StartY=6 StartZ=0 EndX=8 EndY=6 EndZ=0
  constraints (14):
    c: Coincident(g0,g-1)
    c: Distance(g0) = 6
    c: Vertical(g0)
    c: Coincident(g3,g0)
    c: Weight(g1) = 1
    c: Equal(g1,g2)
    c: InternalAlignment(g1,g3)
    c: InternalAlignment(g2,g3)
    c: InternalAlignment(g4,g3)
    c: InternalAlignment(g5,g3)
    c: Block(g3)
    c: Coincident(g6,g0)
    c: Coincident(g6,g3)
    c: Horizontal(g6)
FEATURE [Part::Extrusion] Extrude034  label="caseScrewPillarBracket012"
  Base = -> Sketch043
  Dir = (0,0,1)
  DirMode = 2
  FaceMakerClass = Part::FaceMakerBullseye
  LengthFwd = 2.4
  LengthRev = 0
  Placement = pos=(88.3,29,65.23) rot=(0,1,0;1.5708rad)
  Solid = true
  Symmetric = false
FEATURE [Sketcher::SketchObject] Sketch044
  FullyConstrained = true
  sketch-geometry (7):
    g0: LineSegment StartX=0 StartY=0 StartZ=0 EndX=0 EndY=6 EndZ=0
    g1: Circle CenterX=0 CenterY=0 CenterZ=0 NormalX=0 NormalY=0 NormalZ=1 AngleXU=0 Radius=1
    g2: Circle CenterX=8 CenterY=6 CenterZ=0 NormalX=0 NormalY=0 NormalZ=1 AngleXU=0 Radius=1
    g3: BSplineCurve PolesCount=3 KnotsCount=2 Degree=2 IsPeriodic=0
    g4: GeomPoint X=0 Y=0 Z=0
    g5: GeomPoint X=8 Y=6 Z=0
    g6: LineSegment StartX=0 StartY=6 StartZ=0 EndX=8 EndY=6 EndZ=0
  constraints (14):
    c: Coincident(g0,g-1)
    c: Distance(g0) = 6
    c: Vertical(g0)
    c: Coincident(g3,g0)
    c: Weight(g1) = 1
    c: Equal(g1,g2)
    c: InternalAlignment(g1,g3)
    c: InternalAlignment(g2,g3)
    c: InternalAlignment(g4,g3)
    c: InternalAlignment(g5,g3)
    c: Block(g3)
    c: Coincident(g6,g0)
    c: Coincident(g6,g3)
    c: Horizontal(g6)
FEATURE [Part::Extrusion] Extrude035  label="caseScrewPillarBracket013"
  Base = -> Sketch044
  Dir = (0,0,1)
  DirMode = 2
  FaceMakerClass = Part::FaceMakerBullseye
  LengthFwd = 2.4
  LengthRev = 0
  Placement = pos=(90.7,29,6.77) rot=(0,-1,0;1.5708rad)
  Solid = true
  Symmetric = false
FEATURE [Sketcher::SketchObject] Sketch045
  FullyConstrained = true
  sketch-geometry (7):
    g0: LineSegment StartX=0 StartY=0 StartZ=0 EndX=0 EndY=6 EndZ=0
    g1: Circle CenterX=0 CenterY=0 CenterZ=0 NormalX=0 NormalY=0 NormalZ=1 AngleXU=0 Radius=1
    g2: Circle CenterX=8 CenterY=6 CenterZ=0 NormalX=0 NormalY=0 NormalZ=1 AngleXU=0 Radius=1
    g3: BSplineCurve PolesCount=3 KnotsCount=2 Degree=2 IsPeriodic=0
    g4: GeomPoint X=0 Y=0 Z=0
    g5: GeomPoint X=8 Y=6 Z=0
    g6: LineSegment StartX=0 StartY=6 StartZ=0 EndX=8 EndY=6 EndZ=0
  constraints (14):
    c: Coincident(g0,g-1)
    c: Distance(g0) = 6
    c: Vertical(g0)
    c: Coincident(g3,g0)
    c: Weight(g1) = 1
    c: Equal(g1,g2)
    c: InternalAlignment(g1,g3)
    c: InternalAlignment(g2,g3)
    c: InternalAlignment(g4,g3)
    c: InternalAlignment(g5,g3)
    c: Block(g3)
    c: Coincident(g6,g0)
    c: Coincident(g6,g3)
    c: Horizontal(g6)
FEATURE [Sketcher::SketchObject] Sketch046
  FullyConstrained = true
  sketch-geometry (7):
    g0: LineSegment StartX=0 StartY=0 StartZ=0 EndX=0 EndY=6 EndZ=0
    g1: Circle CenterX=0 CenterY=0 CenterZ=0 NormalX=0 NormalY=0 NormalZ=1 AngleXU=0 Radius=1
    g2: Circle CenterX=8 CenterY=6 CenterZ=0 NormalX=0 NormalY=0 NormalZ=1 AngleXU=0 Radius=1
    g3: BSplineCurve PolesCount=3 KnotsCount=2 Degree=2 IsPeriodic=0
    g4: GeomPoint X=0 Y=0 Z=0
    g5: GeomPoint X=8 Y=6 Z=0
    g6: LineSegment StartX=0 StartY=6 StartZ=0 EndX=8 EndY=6 EndZ=0
  constraints (14):
    c: Coincident(g0,g-1)
    c: Distance(g0) = 6
    c: Vertical(g0)
    c: Coincident(g3,g0)
    c: Weight(g1) = 1
    c: Equal(g1,g2)
    c: InternalAlignment(g1,g3)
    c: InternalAlignment(g2,g3)
    c: InternalAlignment(g4,g3)
    c: InternalAlignment(g5,g3)
    c: Block(g3)
    c: Coincident(g6,g0)
    c: Coincident(g6,g3)
    c: Horizontal(g6)
FEATURE [Part::Extrusion] Extrude036  label="caseScrewPillarBracket014"
  Base = -> Sketch045
  Dir = (0,0,1)
  DirMode = 2
  FaceMakerClass = Part::FaceMakerBullseye
  LengthFwd = 2.4
  LengthRev = 0
  Placement = pos=(110.7,29,6.77) rot=(0,-1,0;1.5708rad)
  Solid = true
  Symmetric = false
FEATURE [Part::Extrusion] Extrude037  label="caseScrewPillarBracket015"
  Base = -> Sketch046
  Dir = (0,0,1)
  DirMode = 2
  FaceMakerClass = Part::FaceMakerBullseye
  LengthFwd = 2.4
  LengthRev = 0
  Placement = pos=(108.3,29,65.23) rot=(0,1,0;1.5708rad)
  Solid = true
  Symmetric = false
FEATURE [Part::Box] Box013  label="frontCaseScrewPillarBracket002"
  AttacherType = Attacher::AttachEngine3D
  Height = 2.4
  Length = 22
  Placement = pos=(87,28,2.3) rot=(0,0,1;0rad)
  Width = 7
FEATURE [Part::Box] Box014  label="frontCaseScrewPillarBracket003"
  AttacherType = Attacher::AttachEngine3D
  Height = 2.4
  Length = 22
  Placement = pos=(87,28,67.3) rot=(0,0,1;0rad)
  Width = 7
FEATURE [Part::Feature] Face087
  shape: bbox 4.8 x 30.2 x 2e-07 mm, 1 faces, 0 solids (baked)
FEATURE [Part::Revolution] Revolve091  label="frontCaseScrewPost004"
  Angle = 360
  Axis = (0,1,0)
  Base = (0,0,0)
  FaceMakerClass = Part::FaceMakerBullseye
  Placement = pos=(89.5,4.5,3.5) rot=(0,0,1;0rad)
  Solid = false
  Source = -> Face087
  Symmetric = false
FEATURE [Part::Feature] Face088
  shape: bbox 4.8 x 30.2 x 2e-07 mm, 1 faces, 0 solids (baked)
FEATURE [Part::Revolution] Revolve092  label="frontCaseScrewPost005"
  Angle = 360
  Axis = (0,1,0)
  Base = (0,0,0)
  FaceMakerClass = Part::FaceMakerBullseye
  Placement = pos=(89.5,4.5,68.5) rot=(0,0,1;0rad)
  Solid = false
  Source = -> Face088
  Symmetric = false
FEATURE [Part::Feature] Face089
  shape: bbox 3.5 x 30.2 x 2e-07 mm, 1 faces, 0 solids (baked)
FEATURE [Part::Revolution] Revolve093  label="backCaseScrewPost002"
  Angle = 360
  Axis = (0,1,0)
  Base = (0,0,0)
  FaceMakerClass = Part::FaceMakerBullseye
  Placement = pos=(12.5,4.5,10) rot=(0,0,1;0rad)
  Solid = false
  Source = -> Face089
  Symmetric = false
FEATURE [Part::Feature] Face090
  shape: bbox 3.5 x 30.2 x 2e-07 mm, 1 faces, 0 solids (baked)
FEATURE [Part::Revolution] Revolve094  label="backCaseScrewPost003"
  Angle = 360
  Axis = (0,1,0)
  Base = (0,0,0)
  FaceMakerClass = Part::FaceMakerBullseye
  Placement = pos=(12.5,4.5,62) rot=(0,0,1;0rad)
  Solid = false
  Source = -> Face090
  Symmetric = false
FEATURE [Part::Box] Box015  label="Cube011"
  AttacherType = Attacher::AttachEngine3D
  Height = 28.8
  Length = 3
  Placement = pos=(107.3,28,21.6) rot=(0,0,1;0rad)
  Width = 7
FEATURE [Part::Box] Box016  label="Cube012"
  AttacherType = Attacher::AttachEngine3D
  Height = 3
  Length = 7.4
  Placement = pos=(107.3,28,18.6) rot=(0,0,1;0rad)
  Width = 7
FEATURE [Part::Box] Box017  label="Cube013"
  AttacherType = Attacher::AttachEngine3D
  Height = 3
  Length = 7.4
  Placement = pos=(107.3,28,50.4) rot=(0,0,1;0rad)
  Width = 7
FEATURE [Part::Cylinder] Cylinder024
  Angle = 360
  AttacherType = Attacher::AttachEngine3D
  Height = 20
  Placement = pos=(0,0,36.15) rot=(0,0,1;0rad)
  Radius = 14.3
FEATURE [Part::Cylinder] Cylinder025
  Angle = 360
  AttacherType = Attacher::AttachEngine3D
  Height = 10
  Placement = pos=(0,0,36.15) rot=(0,0,1;0rad)
  Radius = 4
FEATURE [Part::MultiFuse] Fusion066  label="removeToCreteHoleForPlugHousing009"
  Placement = pos=(70,19,36) rot=(0,1,0;1.5708rad)
  Shapes = -> [Cylinder024,Cylinder025]
FEATURE [Part::MultiFuse] Fusion065  label="plugHousingBracketHolder002"
  Shapes = -> [Box017,Box015,Box016]
FEATURE [Part::Cut] Cut025  label="plugHousingBracketHolder003"
  Base = -> Fusion065
  Placement = pos=(7,0,0) rot=(0,0,1;0rad)
  Tool = -> Fusion066
FEATURE [Sketcher::SketchObject] Sketch047
  FullyConstrained = false
  Placement = pos=(0,0,0) rot=(1,0,0;1.5708rad)
  sketch-geometry (24):
    g0: ArcOfCircle CenterX=-4 CenterY=-10.5 CenterZ=0 NormalX=0 NormalY=0 NormalZ=1 AngleXU=0 Radius=1.5 StartAngle=6e-16 EndAngle=3.14159
    g1: ArcOfCircle CenterX=-34.2 CenterY=-10.5 CenterZ=0 NormalX=0 NormalY=0 NormalZ=1 AngleXU=0 Radius=1.5 StartAngle=0 EndAngle=3.14159
    g2: ArcOfCircle CenterX=-34.2 CenterY=-27.7 CenterZ=0 NormalX=0 NormalY=0 NormalZ=1 AngleXU=0 Radius=1.5 StartAngle=3.14159 EndAngle=6.28319
    g3: ArcOfCircle CenterX=-4 CenterY=-27.7 CenterZ=0 NormalX=0 NormalY=0 NormalZ=1 AngleXU=0 Radius=1.5 StartAngle=3.1416 EndAngle=6.28319
    g4: ArcOfCircle CenterX=-10 CenterY=-4.3 CenterZ=0 NormalX=0 NormalY=0 NormalZ=1 AngleXU=0 Radius=1.5 StartAngle=2e-16 EndAngle=3.14159
    g5: ArcOfCircle CenterX=-16.1 CenterY=-1.8 CenterZ=0 NormalX=0 NormalY=0 NormalZ=1 AngleXU=0 Radius=1.5 StartAngle=5e-16 EndAngle=3.14159
    g6: ArcOfCircle CenterX=-22.1 CenterY=-1.8 CenterZ=0 NormalX=0 NormalY=0 NormalZ=1 AngleXU=0 Radius=1.5 StartAngle=5e-16 EndAngle=3.14159
    g7: ArcOfCircle CenterX=-28.2 CenterY=-4.3 CenterZ=0 NormalX=0 NormalY=0 NormalZ=1 AngleXU=0 Radius=1.5 StartAngle=2e-16 EndAngle=3.14159
    g8: ArcOfCircle CenterX=-10 CenterY=-33.9 CenterZ=0 NormalX=0 NormalY=0 NormalZ=1 AngleXU=0 Radius=1.5 StartAngle=3.14159 EndAngle=6.28319
    g9: ArcOfCircle CenterX=-16.1 CenterY=-36.4 CenterZ=0 NormalX=0 NormalY=0 NormalZ=1 AngleXU=0 Radius=1.5 StartAngle=3.14159 EndAngle=6.28319
    g10: ArcOfCircle CenterX=-22.1 CenterY=-36.4 CenterZ=0 NormalX=0 NormalY=0 NormalZ=1 AngleXU=0 Radius=1.5 StartAngle=3.14159 EndAngle=6.28319
    g11: ArcOfCircle CenterX=-28.2 CenterY=-33.9 CenterZ=0 NormalX=0 NormalY=0 NormalZ=1 AngleXU=0 Radius=1.5 StartAngle=3.14159 EndAngle=6.28319
    g12: LineSegment StartX=-35.7 StartY=-10.5 StartZ=0 EndX=-35.7 EndY=-27.7 EndZ=0
    g13: LineSegment StartX=-32.7 StartY=-10.5 StartZ=0 EndX=-32.7 EndY=-27.7 EndZ=0
    g14: LineSegment StartX=-29.7 StartY=-33.9 StartZ=0 EndX=-29.7 EndY=-4.3 EndZ=0
    g15: LineSegment StartX=-26.7 StartY=-33.9 StartZ=0 EndX=-26.7 EndY=-4.3 EndZ=0
    g16: LineSegment StartX=-2.5 StartY=-10.5 StartZ=0 EndX=-2.5 EndY=-27.7 EndZ=0
    g17: LineSegment StartX=-8.5 StartY=-4.3 StartZ=0 EndX=-8.5 EndY=-33.9 EndZ=0
    g18: LineSegment StartX=-5.5 StartY=-10.5 StartZ=0 EndX=-5.5 EndY=-27.7 EndZ=0
    g19: LineSegment StartX=-11.5 StartY=-4.3 StartZ=0 EndX=-11.5 EndY=-33.9 EndZ=0
    g20: LineSegment StartX=-14.6 StartY=-1.8 StartZ=0 EndX=-14.6 EndY=-36.4 EndZ=0
    g21: LineSegment StartX=-17.6 StartY=-1.8 StartZ=0 EndX=-17.6 EndY=-36.4 EndZ=0
    g22: LineSegment StartX=-20.6 StartY=-36.4 StartZ=0 EndX=-20.6 EndY=-1.8 EndZ=0
    g23: LineSegment StartX=-23.6 StartY=-1.8 StartZ=0 EndX=-23.6 EndY=-36.4 EndZ=0
  constraints (48):
    c: Block(g0)
    c: Block(g1)
    c: Block(g2)
    c: Block(g3)
    c: Block(g4)
    c: Block(g5)
    c: Block(g6)
    c: Block(g7)
    c: Block(g8)
    c: Block(g9)
    c: Block(g10)
    c: Block(g11)
    c: Coincident(g12,g1)
    c: Coincident(g12,g2)
    c: Vertical(g12)
    c: Coincident(g13,g1)
    c: Coincident(g13,g2)
    c: Vertical(g13)
    c: Coincident(g14,g11)
    c: Coincident(g14,g7)
    c: Vertical(g14)
    c: Coincident(g15,g11)
    c: Coincident(g15,g7)
    c: Vertical(g15)
    c: Coincident(g16,g0)
    c: Coincident(g16,g3)
    c: Vertical(g16)
    c: Coincident(g17,g4)
    c: Coincident(g17,g8)
    c: Vertical(g17)
    c: Coincident(g18,g0)
    c: Coincident(g18,g3)
    c: Vertical(g18)
    c: Coincident(g19,g4)
    c: Coincident(g19,g8)
    c: Vertical(g19)
    c: Coincident(g20,g5)
    c: Coincident(g20,g9)
    c: Vertical(g20)
    c: Coincident(g21,g5)
    c: Coincident(g21,g9)
    c: Vertical(g21)
    c: Coincident(g22,g10)
    c: Coincident(g22,g6)
    c: Vertical(g22)
    c: Coincident(g23,g6)
    c: Coincident(g23,g10)
    c: Vertical(g23)
FEATURE [Part::Extrusion] Extrude038  label="removeToCreateFanGrillHoles001"
  Base = -> Sketch047
  Dir = (0,-1,6e-16)
  DirMode = 2
  FaceMakerClass = Part::FaceMakerBullseye
  LengthFwd = 10
  LengthRev = 0
  Placement = pos=(65.4,44,54.82) rot=(0,0,1;0rad)
  Solid = true
  Symmetric = false
FEATURE [Part::Feature] Wire004
  shape: bbox 11 x 5.2 x 2e-07 mm, 0 faces, 0 solids (baked)
FEATURE [Part::Revolution] Revolve095
  Angle = 360
  Axis = (0,1,0)
  Base = (0,0,0)
  FaceMakerClass = Part::FaceMakerBullseye
  Placement = pos=(30.3,38,19.7) rot=(0,0,1;0rad)
  Solid = true
  Source = -> Wire004
  Symmetric = false
FEATURE [Part::Feature] Wire005
  shape: bbox 11 x 5.2 x 2e-07 mm, 0 faces, 0 solids (baked)
FEATURE [Part::Revolution] Revolve096
  Angle = 360
  Axis = (0,1,0)
  Base = (0,0,0)
  FaceMakerClass = Part::FaceMakerBullseye
  Placement = pos=(30.3,38,51.7) rot=(0,0,1;0rad)
  Solid = true
  Source = -> Wire005
  Symmetric = false
FEATURE [Part::Feature] Wire006
  shape: bbox 11 x 5.2 x 2e-07 mm, 0 faces, 0 solids (baked)
FEATURE [Part::Revolution] Revolve097
  Angle = 360
  Axis = (0,1,0)
  Base = (0,0,0)
  FaceMakerClass = Part::FaceMakerBullseye
  Placement = pos=(62.3,38,51.7) rot=(0,0,1;0rad)
  Solid = true
  Source = -> Wire006
  Symmetric = false
FEATURE [Part::Feature] Wire007
  shape: bbox 11 x 5.2 x 2e-07 mm, 0 faces, 0 solids (baked)
FEATURE [Part::Revolution] Revolve098
  Angle = 360
  Axis = (0,1,0)
  Base = (0,0,0)
  FaceMakerClass = Part::FaceMakerBullseye
  Placement = pos=(62.3,38,19.7) rot=(0,0,1;0rad)
  Solid = true
  Source = -> Wire007
  Symmetric = false
FEATURE [Part::MultiFuse] Fusion067  label="fanScrewHousing002"
  Shapes = -> [Revolve098,Revolve097,Revolve096,Revolve095]
FEATURE [Part::Feature] Face091 .. Face094  x4 (patterned run collapsed; names and placements below)
  shape: bbox 3.5 x 17.8 x 2e-07 mm, 1 faces, 0 solids (baked)
FEATURE [Part::Revolution] Revolve099  label="removeToCreateScrewAndThreadedInsertHole026"
  Angle = 360
  Axis = (0,1,0)
  Base = (0,0,0)
  FaceMakerClass = Part::FaceMakerBullseye
  Placement = pos=(62.3,30.3,19.7) rot=(0,0,1;0rad)
  Solid = false
  Source = -> Face091
  Symmetric = false
FEATURE [Part::Revolution] Revolve100  label="removeToCreateScrewAndThreadedInsertHole027"
  Angle = 360
  Axis = (0,1,0)
  Base = (0,0,0)
  FaceMakerClass = Part::FaceMakerBullseye
  Placement = pos=(62.3,30.3,51.7) rot=(0,0,1;0rad)
  Solid = false
  Source = -> Face092
  Symmetric = false
FEATURE [Part::Revolution] Revolve101  label="removeToCreateScrewAndThreadedInsertHole028"
  Angle = 360
  Axis = (0,1,0)
  Base = (0,0,0)
  FaceMakerClass = Part::FaceMakerBullseye
  Placement = pos=(30.3,30.3,19.7) rot=(0,0,1;0rad)
  Solid = false
  Source = -> Face093
  Symmetric = false
FEATURE [Part::Revolution] Revolve102  label="removeToCreateScrewAndThreadedInsertHole029"
  Angle = 360
  Axis = (0,1,0)
  Base = (0,0,0)
  FaceMakerClass = Part::FaceMakerBullseye
  Placement = pos=(30.3,30.3,51.7) rot=(0,0,1;0rad)
  Solid = false
  Source = -> Face094
  Symmetric = false
FEATURE [Part::MultiFuse] Fusion068  label="createThreadedInsertHolesForFan002"
  Shapes = -> [Revolve099,Revolve100,Revolve101,Revolve102]
FEATURE [Part::Cut] Cut026  label="fanScrewHousing003"
  Base = -> Fusion067
  Tool = -> Fusion068
FEATURE [Sketcher::SketchObject] Sketch048
  FullyConstrained = false
  Placement = pos=(0,0,0) rot=(1,0,0;1.5708rad)
  sketch-geometry (24):
    g0: ArcOfCircle CenterX=-4 CenterY=-10.5 CenterZ=0 NormalX=0 NormalY=0 NormalZ=1 AngleXU=0 Radius=1.5 StartAngle=6e-16 EndAngle=3.14159
    g1: ArcOfCircle CenterX=-34.2 CenterY=-10.5 CenterZ=0 NormalX=0 NormalY=0 NormalZ=1 AngleXU=0 Radius=1.5 StartAngle=0 EndAngle=3.14159
    g2: ArcOfCircle CenterX=-34.2 CenterY=-27.7 CenterZ=0 NormalX=0 NormalY=0 NormalZ=1 AngleXU=0 Radius=1.5 StartAngle=3.14159 EndAngle=6.28319
    g3: ArcOfCircle CenterX=-4 CenterY=-27.7 CenterZ=0 NormalX=0 NormalY=0 NormalZ=1 AngleXU=0 Radius=1.5 StartAngle=3.1416 EndAngle=6.28319
    g4: ArcOfCircle CenterX=-10 CenterY=-4.3 CenterZ=0 NormalX=0 NormalY=0 NormalZ=1 AngleXU=0 Radius=1.5 StartAngle=2e-16 EndAngle=3.14159
    g5: ArcOfCircle CenterX=-16.1 CenterY=-1.8 CenterZ=0 NormalX=0 NormalY=0 NormalZ=1 AngleXU=0 Radius=1.5 StartAngle=5e-16 EndAngle=3.14159
    g6: ArcOfCircle CenterX=-22.1 CenterY=-1.8 CenterZ=0 NormalX=0 NormalY=0 NormalZ=1 AngleXU=0 Radius=1.5 StartAngle=5e-16 EndAngle=3.14159
    g7: ArcOfCircle CenterX=-28.2 CenterY=-4.3 CenterZ=0 NormalX=0 NormalY=0 NormalZ=1 AngleXU=0 Radius=1.5 StartAngle=2e-16 EndAngle=3.14159
    g8: ArcOfCircle CenterX=-10 CenterY=-33.9 CenterZ=0 NormalX=0 NormalY=0 NormalZ=1 AngleXU=0 Radius=1.5 StartAngle=3.14159 EndAngle=6.28319
    g9: ArcOfCircle CenterX=-16.1 CenterY=-36.4 CenterZ=0 NormalX=0 NormalY=0 NormalZ=1 AngleXU=0 Radius=1.5 StartAngle=3.14159 EndAngle=6.28319
    g10: ArcOfCircle CenterX=-22.1 CenterY=-36.4 CenterZ=0 NormalX=0 NormalY=0 NormalZ=1 AngleXU=0 Radius=1.5 StartAngle=3.14159 EndAngle=6.28319
    g11: ArcOfCircle CenterX=-28.2 CenterY=-33.9 CenterZ=0 NormalX=0 NormalY=0 NormalZ=1 AngleXU=0 Radius=1.5 StartAngle=3.14159 EndAngle=6.28319
    g12: LineSegment StartX=-35.7 StartY=-10.5 StartZ=0 EndX=-35.7 EndY=-27.7 EndZ=0
    g13: LineSegment StartX=-32.7 StartY=-10.5 StartZ=0 EndX=-32.7 EndY=-27.7 EndZ=0
    g14: LineSegment StartX=-29.7 StartY=-33.9 StartZ=0 EndX=-29.7 EndY=-4.3 EndZ=0
    g15: LineSegment StartX=-26.7 StartY=-33.9 StartZ=0 EndX=-26.7 EndY=-4.3 EndZ=0
    g16: LineSegment StartX=-2.5 StartY=-10.5 StartZ=0 EndX=-2.5 EndY=-27.7 EndZ=0
    g17: LineSegment StartX=-8.5 StartY=-4.3 StartZ=0 EndX=-8.5 EndY=-33.9 EndZ=0
    g18: LineSegment StartX=-5.5 StartY=-10.5 StartZ=0 EndX=-5.5 EndY=-27.7 EndZ=0
    g19: LineSegment StartX=-11.5 StartY=-4.3 StartZ=0 EndX=-11.5 EndY=-33.9 EndZ=0
    g20: LineSegment StartX=-14.6 StartY=-1.8 StartZ=0 EndX=-14.6 EndY=-36.4 EndZ=0
    g21: LineSegment StartX=-17.6 StartY=-1.8 StartZ=0 EndX=-17.6 EndY=-36.4 EndZ=0
    g22: LineSegment StartX=-20.6 StartY=-36.4 StartZ=0 EndX=-20.6 EndY=-1.8 EndZ=0
    g23: LineSegment StartX=-23.6 StartY=-1.8 StartZ=0 EndX=-23.6 EndY=-36.4 EndZ=0
  constraints (48):
    c: Block(g0)
    c: Block(g1)
    c: Block(g2)
    c: Block(g3)
    c: Block(g4)
    c: Block(g5)
    c: Block(g6)
    c: Block(g7)
    c: Block(g8)
    c: Block(g9)
    c: Block(g10)
    c: Block(g11)
    c: Coincident(g12,g1)
    c: Coincident(g12,g2)
    c: Vertical(g12)
    c: Coincident(g13,g1)
    c: Coincident(g13,g2)
    c: Vertical(g13)
    c: Coincident(g14,g11)
    c: Coincident(g14,g7)
    c: Vertical(g14)
    c: Coincident(g15,g11)
    c: Coincident(g15,g7)
    c: Vertical(g15)
    c: Coincident(g16,g0)
    c: Coincident(g16,g3)
    c: Vertical(g16)
    c: Coincident(g17,g4)
    c: Coincident(g17,g8)
    c: Vertical(g17)
    c: Coincident(g18,g0)
    c: Coincident(g18,g3)
    c: Vertical(g18)
    c: Coincident(g19,g4)
    c: Coincident(g19,g8)
    c: Vertical(g19)
    c: Coincident(g20,g5)
    c: Coincident(g20,g9)
    c: Vertical(g20)
    c: Coincident(g21,g5)
    c: Coincident(g21,g9)
    c: Vertical(g21)
    c: Coincident(g22,g10)
    c: Coincident(g22,g6)
    c: Vertical(g22)
    c: Coincident(g23,g6)
    c: Coincident(g23,g10)
    c: Vertical(g23)
FEATURE [Part::Extrusion] Extrude039  label="removeToCreateFanGrillHoles002"
  Base = -> Sketch048
  Dir = (0,-1,6e-16)
  DirMode = 2
  FaceMakerClass = Part::FaceMakerBullseye
  LengthFwd = 10
  LengthRev = 0
  Placement = pos=(65.4,44,54.82) rot=(0,0,1;0rad)
  Solid = true
  Symmetric = false
FEATURE [Part::Cut] Cut027  label="fanScrewHousing004"
  Base = -> Cut026
  Tool = -> Extrude038
FEATURE [Part::Cut] Cut028  label="top014"
  Base = -> Fillet026
  Tool = -> Extrude039
FEATURE [Part::Feature] Face095 .. Face098  x4 (patterned run collapsed; names and placements below)
  shape: bbox 3.5 x 17.8 x 2e-07 mm, 1 faces, 0 solids (baked)
FEATURE [Part::Revolution] Revolve103  label="removeToCreateScrewAndThreadedInsertHole030"
  Angle = 360
  Axis = (0,1,0)
  Base = (0,0,0)
  FaceMakerClass = Part::FaceMakerBullseye
  Placement = pos=(62.3,30.3,19.7) rot=(0,0,1;0rad)
  Solid = false
  Source = -> Face095
  Symmetric = false
FEATURE [Part::Revolution] Revolve104  label="removeToCreateScrewAndThreadedInsertHole031"
  Angle = 360
  Axis = (0,1,0)
  Base = (0,0,0)
  FaceMakerClass = Part::FaceMakerBullseye
  Placement = pos=(62.3,30.3,51.7) rot=(0,0,1;0rad)
  Solid = false
  Source = -> Face096
  Symmetric = false
FEATURE [Part::Revolution] Revolve105  label="removeToCreateScrewAndThreadedInsertHole032"
  Angle = 360
  Axis = (0,1,0)
  Base = (0,0,0)
  FaceMakerClass = Part::FaceMakerBullseye
  Placement = pos=(30.3,30.3,19.7) rot=(0,0,1;0rad)
  Solid = false
  Source = -> Face097
  Symmetric = false
FEATURE [Part::Revolution] Revolve106  label="removeToCreateScrewAndThreadedInsertHole033"
  Angle = 360
  Axis = (0,1,0)
  Base = (0,0,0)
  FaceMakerClass = Part::FaceMakerBullseye
  Placement = pos=(30.3,30.3,51.7) rot=(0,0,1;0rad)
  Solid = false
  Source = -> Face098
  Symmetric = false
FEATURE [Part::MultiFuse] Fusion069  label="createThreadedInsertHolesForFan003"
  Shapes = -> [Revolve103,Revolve104,Revolve105,Revolve106]
FEATURE [Part::Cut] Cut029  label="top015"
  Base = -> Cut028
  Tool = -> Fusion054
FEATURE [Part::Cut] Cut030  label="fanScrewHousing005"
  Base = -> Cut027
  Tool = -> Fusion069
FEATURE [Part::Cylinder] Cylinder026  label="removeToCreteHoleForPlugHousing010"
  Angle = 360
  AttacherType = Attacher::AttachEngine3D
  Height = 20
  Placement = pos=(-2,19,36) rot=(0,1,0;1.5708rad)
  Radius = 14.3
FEATURE [Part::Box] Box018  label="removeToCreteHoleForPlugHousing011"
  AttacherType = Attacher::AttachEngine3D
  Height = 28.6
  Length = 10
  Placement = pos=(-2,0,21.7) rot=(0,0,1;0rad)
  Width = 19
FEATURE [Part::Box] Box019  label="wireHolderBottomCaseBit"
  AttacherType = Attacher::AttachEngine3D
  Height = 28
  Length = 3
  Placement = pos=(0,0,22) rot=(0,0,1;0rad)
  Width = 21
FEATURE [Part::Cylinder] Cylinder027  label="removeToCreteHoleForPlugHousing012"
  Angle = 360
  AttacherType = Attacher::AttachEngine3D
  Height = 20
  Placement = pos=(-2,19,36) rot=(0,1,0;1.5708rad)
  Radius = 14.3
FEATURE [Part::Cut] Cut031  label="wireHolderBottomCaseBit001"
  Base = -> Box019
  Tool = -> Cylinder027
FEATURE [Part::MultiFuse] Fusion070  label="removeToCreteHoleForPlugHousing013"
  Shapes = -> [Box018,Cylinder026]
FEATURE [Part::Cut] Cut032  label="top016"
  Base = -> Cut029
  Tool = -> Fusion070
FEATURE [Part::Cylinder] Cylinder028
  Angle = 360
  AttacherType = Attacher::AttachEngine3D
  Height = 20
  Placement = pos=(0,0,36.15) rot=(0,0,1;0rad)
  Radius = 14.3
FEATURE [Part::Cylinder] Cylinder029
  Angle = 360
  AttacherType = Attacher::AttachEngine3D
  Height = 10
  Placement = pos=(0,0,36.15) rot=(0,0,1;0rad)
  Radius = 4
FEATURE [Part::MultiFuse] Fusion071  label="removeToCreteHoleForPlugHousing014"
  Placement = pos=(70,19,36) rot=(0,1,0;1.5708rad)
  Shapes = -> [Cylinder028,Cylinder029]
FEATURE [Sketcher::SketchObject] Sketch049  label="topSketch011"
  FullyConstrained = true
  sketch-geometry (4):
    g0: ArcOfCircle CenterX=105 CenterY=19 CenterZ=0 NormalX=0 NormalY=0 NormalZ=1 AngleXU=0 Radius=20.6155 StartAngle=5.54125 EndAngle=6.28319
    g1: ArcOfCircle CenterX=105 CenterY=19 CenterZ=0 NormalX=0 NormalY=0 NormalZ=1 AngleXU=0 Radius=13 StartAngle=5.54125 EndAngle=6.28319
    g2: LineSegment StartX=118 StartY=19 StartZ=0 EndX=125.616 EndY=19 EndZ=0
    g3: LineSegment StartX=114.583 StartY=10.2157 StartZ=0 EndX=120.197 EndY=5.06982 EndZ=0
  constraints (7):
    c: Block(g0)
    c: Block(g1)
    c: Coincident(g2,g1)
    c: Coincident(g2,g0)
    c: Horizontal(g2)
    c: Coincident(g3,g1)
    c: Coincident(g3,g0)
FEATURE [Part::Box] Box020  label="removeToCreteHoleForPlugHousing015"
  AttacherType = Attacher::AttachEngine3D
  Height = 28.6
  Length = 20
  Placement = pos=(106.15,0,21.7) rot=(0,0,1;0rad)
  Width = 19
FEATURE [Part::MultiFuse] Fusion072  label="removeToCreteHoleForPlugHousing016"
  Shapes = -> [Box020,Fusion071]
FEATURE [Part::Cut] Cut033  label="removeToCreteHoleForPlugHousing017"
  Base = -> Cut032
  Tool = -> Fusion072
FEATURE [Part::Cylinder] Cylinder030
  Angle = 360
  AttacherType = Attacher::AttachEngine3D
  Height = 20
  Placement = pos=(0,0,36.15) rot=(0,0,1;0rad)
  Radius = 14.3
FEATURE [Part::Cylinder] Cylinder031
  Angle = 360
  AttacherType = Attacher::AttachEngine3D
  Height = 10
  Placement = pos=(0,0,36.15) rot=(0,0,1;0rad)
  Radius = 4
FEATURE [Part::Box] Box021  label="removeToCreteHoleForPlugHousing019"
  AttacherType = Attacher::AttachEngine3D
  Height = 28.6
  Length = 20
  Placement = pos=(106.15,0,21.7) rot=(0,0,1;0rad)
  Width = 19
FEATURE [Part::MultiFuse] Fusion074  label="removeToCreteHoleForPlugHousing020"
  Placement = pos=(70,19,36) rot=(0,1,0;1.5708rad)
  Shapes = -> [Cylinder030,Cylinder031]
FEATURE [Part::MultiFuse] Fusion073  label="removeToCreteHoleForPlugHousing018"
  Placement = pos=(0,0,28.3) rot=(0,0,1;0rad)
  Shapes = -> [Box021,Fusion074]
FEATURE [Part::Cylinder] Cylinder032
  Angle = 360
  AttacherType = Attacher::AttachEngine3D
  Height = 20
  Placement = pos=(0,0,36.15) rot=(0,0,1;0rad)
  Radius = 14.3
FEATURE [Part::Cylinder] Cylinder033
  Angle = 360
  AttacherType = Attacher::AttachEngine3D
  Height = 10
  Placement = pos=(0,0,36.15) rot=(0,0,1;0rad)
  Radius = 4
FEATURE [Part::Box] Box022  label="removeToCreteHoleForPlugHousing021"
  AttacherType = Attacher::AttachEngine3D
  Height = 28.6
  Length = 20
  Placement = pos=(106.15,0,21.7) rot=(0,0,1;0rad)
  Width = 19
FEATURE [Part::MultiFuse] Fusion076  label="removeToCreteHoleForPlugHousing023"
  Placement = pos=(70,19,36) rot=(0,1,0;1.5708rad)
  Shapes = -> [Cylinder032,Cylinder033]
FEATURE [Part::MultiFuse] Fusion075  label="removeToCreteHoleForPlugHousing022"
  Placement = pos=(0,0,-28.3) rot=(0,0,1;0rad)
  Shapes = -> [Box022,Fusion076]
FEATURE [Part::MultiFuse] Fusion077  label="removeToCreatePlugHousingBottomBit"
  Shapes = -> [Fusion075,Fusion073]
FEATURE [Part::Cylinder] Cylinder034
  Angle = 360
  AttacherType = Attacher::AttachEngine3D
  Height = 20
  Placement = pos=(0,0,36.15) rot=(0,0,1;0rad)
  Radius = 14
FEATURE [Part::Cylinder] Cylinder035
  Angle = 360
  AttacherType = Attacher::AttachEngine3D
  Height = 10
  Placement = pos=(0,0,36.15) rot=(0,0,1;0rad)
  Radius = 4
FEATURE [Part::MultiFuse] Fusion078  label="removeToCreteHoleForPlugHousing024"
  Placement = pos=(70,19,36) rot=(0,1,0;1.5708rad)
  Shapes = -> [Cylinder034,Cylinder035]
FEATURE [Part::MultiFuse] Fusion079  label="removeToCreatePlugHousingBottomBit001"
  Shapes = -> [Fusion078,Fusion077]
FEATURE [Part::Extrusion] Extrude040  label="bottomPlugHousingBit"
  Base = -> Sketch049
  Dir = (0,0,1)
  DirMode = 2
  FaceMakerClass = Part::FaceMakerBullseye
  LengthFwd = 72
  LengthRev = 0
  Solid = true
  Symmetric = false
FEATURE [Part::Cut] Cut034  label="bottomPlugHousingBit001"
  Base = -> Extrude040
  Placement = pos=(-0.09,0,0) rot=(0,0,1;0rad)
  Tool = -> Fusion079
FEATURE [Part::Box] Box023  label="Cube014"
  AttacherType = Attacher::AttachEngine3D
  Height = 16
  Length = 8
  Placement = pos=(12.7,31.52,28) rot=(0,0,1;0rad)
  Width = 4
FEATURE [Part::Cylinder] Cylinder036
  Angle = 360
  AttacherType = Attacher::AttachEngine3D
  Height = 10
  Placement = pos=(0,0,36.15) rot=(0,0,1;0rad)
  Radius = 4
FEATURE [Part::Cylinder] Cylinder037
  Angle = 360
  AttacherType = Attacher::AttachEngine3D
  Height = 20
  Placement = pos=(0,0,36.15) rot=(0,0,1;0rad)
  Radius = 8.2
FEATURE [Part::MultiFuse] Fusion080  label="removeToCreteHoleForPlugHousing025"
  Placement = pos=(-42,19,36) rot=(0,1,0;1.5708rad)
  Shapes = -> [Cylinder037,Cylinder036]
FEATURE [Sketcher::SketchObject] Sketch050  label="topSketch012"
  FullyConstrained = true
  sketch-geometry (4):
    g0: LineSegment StartX=16.8446 StartY=31.512 StartZ=0 EndX=16.3251 EndY=34.4666 EndZ=0
    g1: ArcOfCircle CenterX=19 CenterY=19.2524 CenterZ=0 NormalX=0 NormalY=0 NormalZ=1 AngleXU=0 Radius=15.4476 StartAngle=1.74483 EndAngle=2.72717
    g2: ArcOfCircle CenterX=19 CenterY=19.2524 CenterZ=0 NormalX=0 NormalY=0 NormalZ=1 AngleXU=0 Radius=12.4476 StartAngle=1.74483 EndAngle=2.73189
    g3: LineSegment StartX=4.86004 StartY=25.4725 StartZ=0 EndX=7.58253 EndY=24.2107 EndZ=0
  constraints (7):
    c: Block(g0)
    c: Coincident(g1,g0)
    c: Coincident(g2,g0)
    c: Coincident(g3,g1)
    c: Coincident(g3,g2)
    c: Block(g1)
    c: Block(g2)
FEATURE [Part::Extrusion] Extrude041
  Base = -> Sketch050
  Dir = (0,0,1)
  DirMode = 2
  FaceMakerClass = Part::FaceMakerBullseye
  LengthFwd = 10.6
  LengthRev = 0
  Placement = pos=(0,0,31) rot=(0,0,1;0rad)
  Solid = true
  Symmetric = false
FEATURE [Part::Cut] Cut035
  Base = -> Extrude041
  Placement = pos=(0,0,-0.3) rot=(0,0,1;0rad)
  Tool = -> Fusion080
FEATURE [Part::Cut] Cut036
  Base = -> Box023
  Tool = -> Cut035
FEATURE [Part::Fillet] Fillet027
  Base = -> Cut036
  Edges = 1 edges r=0.7: [Edge13]
FEATURE [Part::Fillet] Fillet028
  Base = -> Fillet027
  Edges = 1 edges r=0.7: [Edge13]
FEATURE [Part::Fillet] Fillet029
  Base = -> Fillet028
  Edges = 1 edges r=0.7: [Edge16]
FEATURE [Part::Fillet] Fillet030
  Base = -> Fillet029
  Edges = 1 edges r=0.7: [Edge11]
FEATURE [Part::Fillet] Fillet031
  Base = -> Fillet030
  Edges = 1 edges r=0.7: [Edge10]
FEATURE [Part::Fillet] Fillet032
  Base = -> Fillet031
  Edges = 1 edges r=1.2: [Edge5]
FEATURE [Part::Fillet] Fillet033
  Base = -> Fillet032
  Edges = 1 edges r=1.2: [Edge12]
FEATURE [Part::Fillet] Fillet034  label="wireHousingRetainer"
  Base = -> Fillet033
  Edges = 1 edges r=2: [Edge1]
  Placement = pos=(0.3,0,0) rot=(0,0,1;0rad)
FEATURE [Part::Feature] Face099
  shape: bbox 3.5 x 17.8 x 2e-07 mm, 1 faces, 0 solids (baked)
FEATURE [Part::Revolution] Revolve107  label="removeToCreateScrewAndThreadedInsertHole034"
  Angle = 360
  Axis = (0,1,0)
  Base = (0,0,0)
  FaceMakerClass = Part::FaceMakerBullseye
  Placement = pos=(12.5,0,10) rot=(0,0,1;0rad)
  Solid = false
  Source = -> Face099
  Symmetric = false
FEATURE [Part::Feature] Face100
  shape: bbox 3.5 x 17.8 x 2e-07 mm, 1 faces, 0 solids (baked)
FEATURE [Part::Revolution] Revolve108  label="removeToCreateScrewAndThreadedInsertHole035"
  Angle = 360
  Axis = (0,1,0)
  Base = (0,0,0)
  FaceMakerClass = Part::FaceMakerBullseye
  Placement = pos=(12.5,0,62) rot=(0,0,1;0rad)
  Solid = false
  Source = -> Face100
  Symmetric = false
FEATURE [Part::Feature] Face101
  shape: bbox 3.5 x 17.8 x 2e-07 mm, 1 faces, 0 solids (baked)
FEATURE [Part::Revolution] Revolve109  label="removeToCreateScrewAndThreadedInsertHole036"
  Angle = 360
  Axis = (0,1,0)
  Base = (0,0,0)
  FaceMakerClass = Part::FaceMakerBullseye
  Placement = pos=(89.5,0,68.5) rot=(0,0,1;0rad)
  Solid = false
  Source = -> Face101
  Symmetric = false
FEATURE [Part::Feature] Face102
  shape: bbox 3.5 x 17.8 x 2e-07 mm, 1 faces, 0 solids (baked)
FEATURE [Part::Revolution] Revolve110  label="removeToCreateScrewAndThreadedInsertHole037"
  Angle = 360
  Axis = (0,1,0)
  Base = (0,0,0)
  FaceMakerClass = Part::FaceMakerBullseye
  Placement = pos=(89.5,0,3.5) rot=(0,0,1;0rad)
  Solid = false
  Source = -> Face102
  Symmetric = false
FEATURE [Part::Feature] Face103
  shape: bbox 3.5 x 17.8 x 2e-07 mm, 1 faces, 0 solids (baked)
FEATURE [Part::Revolution] Revolve111  label="removeToCreateScrewAndThreadedInsertHole038"
  Angle = 360
  Axis = (0,1,0)
  Base = (0,0,0)
  FaceMakerClass = Part::FaceMakerBullseye
  Placement = pos=(109.5,4.7,3.5) rot=(0,0,1;0rad)
  Solid = false
  Source = -> Face103
  Symmetric = false
FEATURE [Part::Feature] Face104
  shape: bbox 3.5 x 17.8 x 2e-07 mm, 1 faces, 0 solids (baked)
FEATURE [Part::Revolution] Revolve112  label="removeToCreateScrewAndThreadedInsertHole039"
  Angle = 360
  Axis = (0,1,0)
  Base = (0,0,0)
  FaceMakerClass = Part::FaceMakerBullseye
  Placement = pos=(109.5,4.7,68.5) rot=(0,0,1;0rad)
  Solid = false
  Source = -> Face104
  Symmetric = false
FEATURE [Part::MultiFuse] Fusion081  label="removeToCreateScrewAndThreadedInsertHole040"
  Shapes = -> [Revolve107,Revolve108,Revolve109,Revolve110,Revolve111,Revolve112]
FEATURE [Part::MultiFuse] Fusion082  label="casePillars002"
  Shapes = -> [Revolve094,Revolve092,Revolve090,Revolve089,Revolve091,Revolve093]
FEATURE [Part::Cut] Cut037  label="casePillars003"
  Base = -> Fusion082
  Tool = -> Fusion081
FEATURE [Sketcher::SketchObject] Sketch051
  FullyConstrained = true
  Placement = pos=(117,19,0) rot=(0.57735,0.57735,0.57735;2.0944rad)
  sketch-geometry (48):
    g0: LineSegment StartX=-49.19 StartY=69.25 StartZ=0 EndX=-49.19 EndY=66.25 EndZ=0
    g1: LineSegment StartX=-49.19 StartY=63.5 StartZ=0 EndX=-49.19 EndY=60.5 EndZ=0
    g2: LineSegment StartX=-49.19 StartY=57.75 StartZ=0 EndX=-49.19 EndY=54.75 EndZ=0
    g3: LineSegment StartX=-49.19 StartY=52 StartZ=0 EndX=-49.19 EndY=49 EndZ=0
    g4: LineSegment StartX=-49.19 StartY=46.25 StartZ=0 EndX=-49.19 EndY=43.25 EndZ=0
    g5: LineSegment StartX=-49.19 StartY=40.5 StartZ=0 EndX=-49.19 EndY=37.5 EndZ=0
    g6: LineSegment StartX=-49.19 StartY=34.5 StartZ=0 EndX=-49.19 EndY=31.5 EndZ=0
    g7: LineSegment StartX=-49.19 StartY=28.75 StartZ=0 EndX=-49.19 EndY=25.75 EndZ=0
    g8: LineSegment StartX=-49.19 StartY=23 StartZ=0 EndX=-49.19 EndY=20 EndZ=0
    g9: LineSegment StartX=-49.19 StartY=17.25 StartZ=0 EndX=-49.19 EndY=14.25 EndZ=0
    g10: LineSegment StartX=-49.19 StartY=11.5 StartZ=0 EndX=-49.19 EndY=8.5 EndZ=0
    g11: LineSegment StartX=-49.19 StartY=5.75 StartZ=0 EndX=-49.19 EndY=2.75 EndZ=0
    g12: ArcOfCircle CenterX=-1.5 CenterY=67.75 CenterZ=0 NormalX=0 NormalY=0 NormalZ=1 AngleXU=0 Radius=1.5 StartAngle=4.71239 EndAngle=7.85398
    g13: ArcOfCircle CenterX=-1.5 CenterY=62 CenterZ=0 NormalX=0 NormalY=0 NormalZ=1 AngleXU=0 Radius=1.5 StartAngle=4.71239 EndAngle=7.85398
    g14: ArcOfCircle CenterX=-1.5 CenterY=56.25 CenterZ=0 NormalX=0 NormalY=0 NormalZ=1 AngleXU=0 Radius=1.5 StartAngle=4.71239 EndAngle=7.85398
    g15: ArcOfCircle CenterX=-11.49 CenterY=50.5 CenterZ=0 NormalX=0 NormalY=0 NormalZ=1 AngleXU=0 Radius=1.5 StartAngle=4.71239 EndAngle=7.85398
    g16: ArcOfCircle CenterX=-16.28 CenterY=44.75 CenterZ=0 NormalX=0 NormalY=0 NormalZ=1 AngleXU=0 Radius=1.5 StartAngle=4.71239 EndAngle=7.85398
    g17: ArcOfCircle CenterX=-18.2337 CenterY=39 CenterZ=0 NormalX=0 NormalY=0 NormalZ=1 AngleXU=0 Radius=1.5 StartAngle=4.71485 EndAngle=7.85398
    g18: ArcOfCircle CenterX=-16.2837 CenterY=27.25 CenterZ=0 NormalX=0 NormalY=0 NormalZ=1 AngleXU=0 Radius=1.5 StartAngle=4.71485 EndAngle=7.85398
    g19: ArcOfCircle CenterX=-18.2337 CenterY=33 CenterZ=0 NormalX=0 NormalY=0 NormalZ=1 AngleXU=0 Radius=1.5 StartAngle=4.71485 EndAngle=7.85398
    g20: ArcOfCircle CenterX=-11.49 CenterY=21.5 CenterZ=0 NormalX=0 NormalY=0 NormalZ=1 AngleXU=0 Radius=1.5 StartAngle=4.71239 EndAngle=7.85398
    g21: ArcOfCircle CenterX=-1.5 CenterY=4.25 CenterZ=0 NormalX=0 NormalY=0 NormalZ=1 AngleXU=0 Radius=1.5 StartAngle=4.71239 EndAngle=7.85398
    g22: ArcOfCircle CenterX=-1.5 CenterY=10 CenterZ=0 NormalX=0 NormalY=0 NormalZ=1 AngleXU=0 Radius=1.5 StartAngle=4.71239 EndAngle=7.85398
    g23: ArcOfCircle CenterX=-1.5 CenterY=15.75 CenterZ=0 NormalX=0 NormalY=0 NormalZ=1 AngleXU=0 Radius=1.5 StartAngle=4.71239 EndAngle=7.85398
    g24: LineSegment StartX=-49.19 StartY=69.25 StartZ=0 EndX=-1.5 EndY=69.25 EndZ=0
    g25: LineSegment StartX=-49.19 StartY=66.25 StartZ=0 EndX=-1.5 EndY=66.25 EndZ=0
    g26: LineSegment StartX=-49.19 StartY=63.5 StartZ=0 EndX=-1.5 EndY=63.5 EndZ=0
    g27: LineSegment StartX=-49.19 StartY=60.5 StartZ=0 EndX=-1.5 EndY=60.5 EndZ=0
    g28: LineSegment StartX=-49.19 StartY=57.75 StartZ=0 EndX=-1.5 EndY=57.75 EndZ=0
    g29: LineSegment StartX=-49.19 StartY=54.75 StartZ=0 EndX=-1.5 EndY=54.75 EndZ=0
    g30: LineSegment StartX=-49.19 StartY=52 StartZ=0 EndX=-11.49 EndY=52 EndZ=0
    g31: LineSegment StartX=-49.19 StartY=49 StartZ=0 EndX=-11.49 EndY=49 EndZ=0
    g32: LineSegment StartX=-49.19 StartY=46.25 StartZ=0 EndX=-16.28 EndY=46.25 EndZ=0
    g33: LineSegment StartX=-49.19 StartY=43.25 StartZ=0 EndX=-16.28 EndY=43.25 EndZ=0
    g34: LineSegment StartX=-49.19 StartY=40.5 StartZ=0 EndX=-18.2337 EndY=40.5 EndZ=0
    g35: LineSegment StartX=-49.19 StartY=37.5 StartZ=0 EndX=-18.23 EndY=37.5 EndZ=0
    g36: LineSegment StartX=-49.19 StartY=34.5 StartZ=0 EndX=-18.2337 EndY=34.5 EndZ=0
    g37: LineSegment StartX=-49.19 StartY=31.5 StartZ=0 EndX=-18.23 EndY=31.5 EndZ=0
    g38: LineSegment StartX=-49.19 StartY=28.75 StartZ=0 EndX=-16.2837 EndY=28.75 EndZ=0
    g39: LineSegment StartX=-49.19 StartY=25.75 StartZ=0 EndX=-16.28 EndY=25.75 EndZ=0
    g40: LineSegment StartX=-49.19 StartY=23 StartZ=0 EndX=-11.49 EndY=23 EndZ=0
    g41: LineSegment StartX=-49.19 StartY=20 StartZ=0 EndX=-11.49 EndY=20 EndZ=0
    g42: LineSegment StartX=-49.19 StartY=17.25 StartZ=0 EndX=-1.5 EndY=17.25 EndZ=0
    g43: LineSegment StartX=-49.19 StartY=14.25 StartZ=0 EndX=-1.5 EndY=14.25 EndZ=0
    g44: LineSegment StartX=-49.19 StartY=11.5 StartZ=0 EndX=-1.5 EndY=11.5 EndZ=0
    g45: LineSegment StartX=-49.19 StartY=8.5 StartZ=0 EndX=-1.5 EndY=8.5 EndZ=0
    g46: LineSegment StartX=-49.19 StartY=5.75 StartZ=0 EndX=-1.5 EndY=5.75 EndZ=0
    g47: LineSegment StartX=-49.19 StartY=2.75 StartZ=0 EndX=-1.5 EndY=2.75 EndZ=0
  constraints (120):
    c: Vertical(g0)
    c: Distance(g0) = 3
    c: Block(g0)
    c: Vertical(g1)
    c: Distance(g1) = 3
    c: Vertical(g2)
    c: Equal(g0,g2) = 3
    c: Block(g2)
    c: Vertical(g3)
    c: Equal(g1,g3) = 3
    c: Vertical(g4)
    c: Equal(g0,g4) = 3
    c: Block(g4)
    c: Vertical(g5)
    c: Equal(g1,g5) = 3
    c: Vertical(g6)
    c: Equal(g0,g6) = 3
    c: Block(g6)
    c: Vertical(g7)
    c: Equal(g1,g7) = 3
    c: Vertical(g8)
    c: Equal(g0,g8) = 3
    c: Block(g8)
    c: Vertical(g9)
    c: Equal(g1,g9) = 3
    c: Vertical(g10)
    c: Equal(g0,g10) = 3
    c: Block(g10)
    c: Vertical(g11)
    c: Equal(g1,g11) = 3
    c: Block(g12)
    c: Block(g13)
    c: Block(g14)
    c: Block(g15)
    c: Block(g16)
    c: Block(g17)
    c: Block(g18)
    c: Block(g19)
    c: Block(g20)
    c: Block(g21)
    c: Block(g22)
    c: Block(g23)
    c: Block(g11)
    c: Block(g9)
    c: Block(g7)
    c: Block(g5)
    c: Block(g3)
    c: Block(g1)
    c: Coincident(g24,g0)
    c: Coincident(g24,g12)
    c: Horizontal(g24)
    c: Coincident(g25,g0)
    c: Coincident(g25,g12)
    c: Horizontal(g25)
    c: Coincident(g26,g1)
    c: Coincident(g26,g13)
    c: Horizontal(g26)
    c: Coincident(g27,g1)
    c: Coincident(g27,g13)
    c: Horizontal(g27)
    c: Coincident(g28,g2)
    c: Coincident(g28,g14)
    c: Horizontal(g28)
    c: Coincident(g29,g2)
    c: Coincident(g29,g14)
    c: Horizontal(g29)
    c: Coincident(g30,g3)
    c: Coincident(g30,g15)
    c: Horizontal(g30)
    c: Coincident(g31,g3)
    c: Coincident(g31,g15)
    c: Horizontal(g31)
    c: Coincident(g32,g4)
    c: Coincident(g32,g16)
    c: Horizontal(g32)
    c: Coincident(g33,g4)
    c: Coincident(g33,g16)
    c: Horizontal(g33)
    c: Coincident(g34,g5)
    c: Coincident(g34,g17)
    c: Horizontal(g34)
    c: Coincident(g35,g5)
    c: Coincident(g35,g17)
    c: Horizontal(g35)
    c: Coincident(g36,g6)
    c: Coincident(g36,g19)
    c: Horizontal(g36)
    c: Coincident(g37,g6)
    c: Coincident(g37,g19)
    c: Horizontal(g37)
    c: Coincident(g38,g7)
    c: Coincident(g38,g18)
    c: Horizontal(g38)
    c: Coincident(g39,g7)
    c: Coincident(g39,g18)
    c: Horizontal(g39)
    c: Coincident(g40,g8)
    c: Coincident(g40,g20)
    c: Horizontal(g40)
    c: Coincident(g41,g8)
    c: Coincident(g41,g20)
    c: Horizontal(g41)
    c: Coincident(g42,g9)
    c: Coincident(g42,g23)
    c: Horizontal(g42)
    c: Coincident(g43,g9)
    c: Coincident(g43,g23)
    c: Horizontal(g43)
    c: Coincident(g44,g10)
    c: Coincident(g44,g22)
    c: Horizontal(g44)
    c: Coincident(g45,g10)
    c: Coincident(g45,g22)
    c: Horizontal(g45)
    c: Coincident(g46,g11)
    c: Coincident(g46,g21)
    c: Horizontal(g46)
    c: Coincident(g47,g11)
    c: Coincident(g47,g21)
    c: Horizontal(g47)
FEATURE [Part::Extrusion] Extrude042
  Base = -> Sketch051
  Dir = (1,-2e-16,2e-16)
  DirMode = 2
  FaceMakerClass = Part::FaceMakerBullseye
  LengthFwd = 19
  LengthRev = 0
  Placement = pos=(-19,0,0) rot=(0,0,1;0rad)
  Solid = true
  Symmetric = false
FEATURE [Part::Fillet] Fillet035  label="removeToCreateVentalationHoles"
  Base = -> Extrude042
  Edges = <same value as first occurrence — deduplicated (x6 in doc)>
  Placement = pos=(7,0,0) rot=(0,0,1;0rad)
FEATURE [Part::Cut] Cut038  label="top017"
  Base = -> Cut033
  Tool = -> Fillet035
FEATURE [Sketcher::SketchObject] Sketch052  label="bottomSketch001"
  FullyConstrained = true
  sketch-geometry (45):
    g0: LineSegment StartX=6.29999 StartY=8 StartZ=0 EndX=3.29999 EndY=8 EndZ=0
    g1: LineSegment StartX=3.29999 StartY=8 StartZ=0 EndX=3.29999 EndY=-6.03275e-07 EndZ=0
    g2: ArcOfCircle CenterX=8.29999 CenterY=5 CenterZ=0 NormalX=0 NormalY=0 NormalZ=1 AngleXU=0 Radius=2 StartAngle=3.14159 EndAngle=4.71239
    g3: LineSegment StartX=6.29999 StartY=8 StartZ=0 EndX=6.29999 EndY=5 EndZ=0
    g4: ArcOfCircle CenterX=105 CenterY=19 CenterZ=0 NormalX=0 NormalY=0 NormalZ=1 AngleXU=0 Radius=12.7 StartAngle=4.71239 EndAngle=5.94289
    g5-g11: Circle x7 (B-spline internal-alignment scaffolding for g12; pole/knot coordinates omitted)
    g12: BSplineCurve PolesCount=7 KnotsCount=5 Degree=3 IsPeriodic=0
    g13-g17: GeomPoint x5 (B-spline internal-alignment scaffolding for g12; pole/knot coordinates omitted)
    g18: ArcOfCircle CenterX=105 CenterY=19 CenterZ=0 NormalX=0 NormalY=0 NormalZ=1 AngleXU=0 Radius=15.7 StartAngle=5.81226 EndAngle=6.28319
    g19: BSplineCurve PolesCount=5 KnotsCount=3 Degree=3 IsPeriodic=0
    g20: LineSegment StartX=8.29999 StartY=3 StartZ=0 EndX=101.7 EndY=3 EndZ=0
    g21: LineSegment StartX=3.29999 StartY=-6.03275e-07 StartZ=0 EndX=105 EndY=-6.03275e-07 EndZ=0
    g22: LineSegment StartX=120.974 StartY=8.71251 StartZ=0 EndX=122.332 EndY=7.83778 EndZ=0
    g23: LineSegment StartX=105 StartY=-6.03274e-07 StartZ=0 EndX=113 EndY=-6.03274e-07 EndZ=0
    g24: ArcOfCircle CenterX=105 CenterY=19 CenterZ=0 NormalX=0 NormalY=0 NormalZ=1 AngleXU=0 Radius=20.6155 StartAngle=5.11091 EndAngle=5.71103
    g25: ArcOfCircle CenterX=117.7 CenterY=19 CenterZ=0 NormalX=0 NormalY=0 NormalZ=1 AngleXU=0 Radius=3 StartAngle=1.2e-15 EndAngle=2.10468
    g26: Circle CenterX=116.345 CenterY=16.3232 CenterZ=0 NormalX=0 NormalY=0 NormalZ=1 AngleXU=0 Radius=1
    g27: Circle CenterX=117.24 CenterY=15.7584 CenterZ=0 NormalX=0 NormalY=0 NormalZ=1 AngleXU=0 Radius=1
    g28: Circle CenterX=116.972 CenterY=14.7612 CenterZ=0 NormalX=0 NormalY=0 NormalZ=1 AngleXU=0 Radius=1
    g29: BSplineCurve PolesCount=3 KnotsCount=2 Degree=2 IsPeriodic=0
    g30: GeomPoint X=116.345 Y=16.3232 Z=0
    g31: GeomPoint X=116.972 Y=14.7612 Z=0
    g32: Circle CenterX=115.828 CenterY=17.157 CenterZ=0 NormalX=0 NormalY=0 NormalZ=1 AngleXU=0 Radius=1
    g33: Circle CenterX=115.841 CenterY=16.639 CenterZ=0 NormalX=0 NormalY=0 NormalZ=1 AngleXU=0 Radius=1
    g34: Circle CenterX=116.345 CenterY=16.3232 CenterZ=0 NormalX=0 NormalY=0 NormalZ=1 AngleXU=0 Radius=1
    g35: BSplineCurve PolesCount=3 KnotsCount=2 Degree=2 IsPeriodic=0
    g36: GeomPoint X=115.828 Y=17.157 Z=0
    g37: GeomPoint X=116.345 Y=16.3232 Z=0
    g38: LineSegment StartX=115.828 StartY=17.157 StartZ=0 EndX=115.828 EndY=20.8307 EndZ=0
    g39: Circle CenterX=115.828 CenterY=20.8307 CenterZ=0 NormalX=0 NormalY=0 NormalZ=1 AngleXU=0 Radius=1
    g40: Circle CenterX=115.831 CenterY=21.3396 CenterZ=0 NormalX=0 NormalY=0 NormalZ=1 AngleXU=0 Radius=1
    g41: Circle CenterX=116.173 CenterY=21.5825 CenterZ=0 NormalX=0 NormalY=0 NormalZ=1 AngleXU=0 Radius=1
    g42: BSplineCurve PolesCount=3 KnotsCount=2 Degree=2 IsPeriodic=0
    g43: GeomPoint X=115.828 Y=20.8307 Z=0
    g44: GeomPoint X=116.173 Y=21.5825 Z=0
  constraints (70):
    c: Horizontal(g0)
    c: Distance(g0) = 3
    c: Coincident(g1,g0)
    c: Vertical(g1)
    c: Block(g2)
    c: Block(g0)
    c: Coincident(g3,g0)
    c: Coincident(g3,g2)
    c: Vertical(g3)
    c: Block(g1)
    c: Block(g4)
    c: Coincident(g19,g4)
    c: Block(g19)
    c: Equal(g5, g6-g11) x6
    c: InternalAlignment(g5-g11 -> g12) x7
    c: InternalAlignment(g13-g17 -> g12) x5
    c: Block(g12)
    c: Coincident(g18,g12)
    c: Block(g18)
    c: Coincident(g20,g2)
    c: Coincident(g20,g19)
    c: Horizontal(g20)
    c: Distance(g20) = 93.4
    c: Coincident(g21,g1)
    c: Horizontal(g21)
    c: Distance(g21) = 101.7
    c: Horizontal(g23)
    c: Distance(g23) = 8
    c: Coincident(g24,g23)
    c: Block(g23)
    c: Coincident(g22,g24)
    c: Block(g24)
    c: Block(g22)
    c: Distance(g22) = 1.61553
    c: Coincident(g25,g18)
    c: Block(g25)
    c: Weight(g26) = 1
    c: Equal(g26,g27)
    c: Equal(g26,g28)
    c: Coincident(g29,g4)
    c: InternalAlignment(g26,g29)
    c: InternalAlignment(g27,g29)
    c: InternalAlignment(g28,g29)
    c: InternalAlignment(g30,g29)
    c: InternalAlignment(g31,g29)
    c: Block(g29)
    c: Weight(g32) = 1
    c: Equal(g32,g33)
    c: Equal(g32,g34)
    c: Coincident(g35,g29)
    c: InternalAlignment(g32,g35)
    c: InternalAlignment(g33,g35)
    c: InternalAlignment(g34,g35)
    c: InternalAlignment(g36,g35)
    c: InternalAlignment(g37,g35)
    c: Block(g35)
    c: Coincident(g38,g35)
    c: Vertical(g38)
    c: Block(g38)
    c: Coincident(g42,g38)
    c: Weight(g39) = 1
    c: Equal(g39,g40)
    c: Equal(g39,g41)
    c: Coincident(g42,g25)
    c: InternalAlignment(g39,g42)
    c: InternalAlignment(g40,g42)
    c: InternalAlignment(g41,g42)
    c: InternalAlignment(g43,g42)
    c: InternalAlignment(g44,g42)
    c: Block(g42)
FEATURE [Part::Extrusion] Extrude043  label="bottom010"
  Base = -> Sketch052
  Dir = (0,0,1)
  DirMode = 2
  FaceMakerClass = Part::FaceMakerBullseye
  LengthFwd = 71.4
  LengthRev = 0
  Placement = pos=(0,0,0.3) rot=(0,0,1;0rad)
  Solid = true
  Symmetric = false
FEATURE [Sketcher::SketchObject] Sketch053  label="topSketch013"
  FullyConstrained = true
  sketch-geometry (22):
    g0: LineSegment StartX=5.21097e-06 StartY=3 StartZ=0 EndX=5.21097e-06 EndY=19 EndZ=0
    g1: ArcOfCircle CenterX=19 CenterY=19 CenterZ=0 NormalX=0 NormalY=0 NormalZ=1 AngleXU=0 Radius=19 StartAngle=1.5708 EndAngle=3.14159
    g2: ArcOfCircle CenterX=19 CenterY=19 CenterZ=0 NormalX=0 NormalY=0 NormalZ=1 AngleXU=0 Radius=16 StartAngle=1.5708 EndAngle=3.14159
    g3: LineSegment StartX=114 StartY=35 StartZ=0 EndX=19 EndY=35 EndZ=0
    g4: LineSegment StartX=5.21097e-06 StartY=3 StartZ=0 EndX=5.21097e-06 EndY=0 EndZ=0
    g5: LineSegment StartX=3 StartY=0 StartZ=0 EndX=5.21097e-06 EndY=0 EndZ=0
    g6: LineSegment StartX=3 StartY=19 StartZ=0 EndX=3 EndY=0 EndZ=0
    g7: LineSegment StartX=19 StartY=38 StartZ=0 EndX=124 EndY=38 EndZ=0
    g8: Circle CenterX=119 CenterY=35 CenterZ=0 NormalX=0 NormalY=0 NormalZ=1 AngleXU=0 Radius=1
    g9: Circle CenterX=121 CenterY=35 CenterZ=0 NormalX=0 NormalY=0 NormalZ=1 AngleXU=0 Radius=1
    g10: Circle CenterX=121 CenterY=33 CenterZ=0 NormalX=0 NormalY=0 NormalZ=1 AngleXU=0 Radius=1
    g11: BSplineCurve PolesCount=3 KnotsCount=2 Degree=2 IsPeriodic=0
    g12: GeomPoint X=119 Y=35 Z=0
    g13: GeomPoint X=121 Y=33 Z=0
    g14: LineSegment StartX=119 StartY=35 StartZ=0 EndX=114 EndY=35 EndZ=0
    g15: ArcOfCircle CenterX=105 CenterY=19 CenterZ=0 NormalX=0 NormalY=0 NormalZ=1 AngleXU=0 Radius=16 StartAngle=5.60905 EndAngle=6.28319
    g16: LineSegment StartX=121 StartY=33 StartZ=0 EndX=121 EndY=19 EndZ=0
    g17: LineSegment StartX=117.5 StartY=9.01251 StartZ=0 EndX=121.163 EndY=9.0125 EndZ=0
    g18: ArcOfCircle CenterX=105 CenterY=19 CenterZ=0 NormalX=0 NormalY=0 NormalZ=1 AngleXU=0 Radius=20.6155 StartAngle=5.7297 EndAngle=6.28319
    g19: LineSegment StartX=121.163 StartY=9.0125 StartZ=0 EndX=122.538 EndY=8.16329 EndZ=0
    g20: LineSegment StartX=124 StartY=38 StartZ=0 EndX=125.616 EndY=38 EndZ=0
    g21: LineSegment StartX=125.616 StartY=19 StartZ=0 EndX=125.616 EndY=38 EndZ=0
  constraints (50):
    c: Vertical(g0)
    c: Block(g0)
    c: Coincident(g1,g0)
    c: Block(g1)
    c: Coincident(g2,g1)
    c: Block(g2)
    c: Coincident(g3,g2)
    c: Horizontal(g3)
    c: Tangent(g3,g2)
    c: Coincident(g4,g0)
    c: Distance(g4) = 3
    c: Vertical(g4)
    c: Coincident(g5,g4)
    c: Horizontal(g5)
    c: Coincident(g6,g2)
    c: Coincident(g6,g5)
    c: Vertical(g6)
    c: Horizontal(g7)
    c: Distance(g7) = 105
    c: Coincident(g7,g1)
    c: Block(g3)
    c: Weight(g8) = 1
    c: Equal(g8,g9)
    c: Equal(g8,g10)
    c: InternalAlignment(g8,g11)
    c: InternalAlignment(g9,g11)
    c: InternalAlignment(g10,g11)
    c: InternalAlignment(g12,g11)
    c: InternalAlignment(g13,g11)
    c: Block(g11)
    c: Coincident(g14,g11)
    c: Coincident(g14,g3)
    c: Horizontal(g14)
    c: Block(g15)
    c: Coincident(g16,g11)
    c: Coincident(g16,g15)
    c: Vertical(g16)
    c: Distance(g16) = 14
    c: Coincident(g17,g15)
    c: Block(g18)
    c: Coincident(g19,g18)
    c: Coincident(g20,g7)
    c: Horizontal(g20)
    c: Vertical(g21)
    c: Coincident(g20,g21)
    c: Block(g20)
    c: Block(g21)
    c: Block(g19)
    c: Block(g17)
    c: Distance(g20) = 1.61553
FEATURE [Part::Extrusion] Extrude044
  Base = -> Sketch053
  Dir = (0,0,1)
  DirMode = 2
  FaceMakerClass = Part::FaceMakerBullseye
  LengthFwd = 72
  LengthRev = 0
  Solid = true
  Symmetric = false
FEATURE [Part::Fillet] Fillet036  label="top018"
  Base = -> Extrude044
  Edges = 1 edges r=2: [Edge41]
FEATURE [Sketcher::SketchObject] Sketch054
  FullyConstrained = false
  Placement = pos=(0,0,0) rot=(1,0,0;1.5708rad)
  sketch-geometry (24):
    g0: ArcOfCircle CenterX=-4 CenterY=-10.5 CenterZ=0 NormalX=0 NormalY=0 NormalZ=1 AngleXU=0 Radius=1.5 StartAngle=6e-16 EndAngle=3.14159
    g1: ArcOfCircle CenterX=-34.2 CenterY=-10.5 CenterZ=0 NormalX=0 NormalY=0 NormalZ=1 AngleXU=0 Radius=1.5 StartAngle=0 EndAngle=3.14159
    g2: ArcOfCircle CenterX=-34.2 CenterY=-27.7 CenterZ=0 NormalX=0 NormalY=0 NormalZ=1 AngleXU=0 Radius=1.5 StartAngle=3.14159 EndAngle=6.28319
    g3: ArcOfCircle CenterX=-4 CenterY=-27.7 CenterZ=0 NormalX=0 NormalY=0 NormalZ=1 AngleXU=0 Radius=1.5 StartAngle=3.1416 EndAngle=6.28319
    g4: ArcOfCircle CenterX=-10 CenterY=-4.3 CenterZ=0 NormalX=0 NormalY=0 NormalZ=1 AngleXU=0 Radius=1.5 StartAngle=2e-16 EndAngle=3.14159
    g5: ArcOfCircle CenterX=-16.1 CenterY=-1.8 CenterZ=0 NormalX=0 NormalY=0 NormalZ=1 AngleXU=0 Radius=1.5 StartAngle=5e-16 EndAngle=3.14159
    g6: ArcOfCircle CenterX=-22.1 CenterY=-1.8 CenterZ=0 NormalX=0 NormalY=0 NormalZ=1 AngleXU=0 Radius=1.5 StartAngle=5e-16 EndAngle=3.14159
    g7: ArcOfCircle CenterX=-28.2 CenterY=-4.3 CenterZ=0 NormalX=0 NormalY=0 NormalZ=1 AngleXU=0 Radius=1.5 StartAngle=2e-16 EndAngle=3.14159
    g8: ArcOfCircle CenterX=-10 CenterY=-33.9 CenterZ=0 NormalX=0 NormalY=0 NormalZ=1 AngleXU=0 Radius=1.5 StartAngle=3.14159 EndAngle=6.28319
    g9: ArcOfCircle CenterX=-16.1 CenterY=-36.4 CenterZ=0 NormalX=0 NormalY=0 NormalZ=1 AngleXU=0 Radius=1.5 StartAngle=3.14159 EndAngle=6.28319
    g10: ArcOfCircle CenterX=-22.1 CenterY=-36.4 CenterZ=0 NormalX=0 NormalY=0 NormalZ=1 AngleXU=0 Radius=1.5 StartAngle=3.14159 EndAngle=6.28319
    g11: ArcOfCircle CenterX=-28.2 CenterY=-33.9 CenterZ=0 NormalX=0 NormalY=0 NormalZ=1 AngleXU=0 Radius=1.5 StartAngle=3.14159 EndAngle=6.28319
    g12: LineSegment StartX=-35.7 StartY=-10.5 StartZ=0 EndX=-35.7 EndY=-27.7 EndZ=0
    g13: LineSegment StartX=-32.7 StartY=-10.5 StartZ=0 EndX=-32.7 EndY=-27.7 EndZ=0
    g14: LineSegment StartX=-29.7 StartY=-33.9 StartZ=0 EndX=-29.7 EndY=-4.3 EndZ=0
    g15: LineSegment StartX=-26.7 StartY=-33.9 StartZ=0 EndX=-26.7 EndY=-4.3 EndZ=0
    g16: LineSegment StartX=-2.5 StartY=-10.5 StartZ=0 EndX=-2.5 EndY=-27.7 EndZ=0
    g17: LineSegment StartX=-8.5 StartY=-4.3 StartZ=0 EndX=-8.5 EndY=-33.9 EndZ=0
    g18: LineSegment StartX=-5.5 StartY=-10.5 StartZ=0 EndX=-5.5 EndY=-27.7 EndZ=0
    g19: LineSegment StartX=-11.5 StartY=-4.3 StartZ=0 EndX=-11.5 EndY=-33.9 EndZ=0
    g20: LineSegment StartX=-14.6 StartY=-1.8 StartZ=0 EndX=-14.6 EndY=-36.4 EndZ=0
    g21: LineSegment StartX=-17.6 StartY=-1.8 StartZ=0 EndX=-17.6 EndY=-36.4 EndZ=0
    g22: LineSegment StartX=-20.6 StartY=-36.4 StartZ=0 EndX=-20.6 EndY=-1.8 EndZ=0
    g23: LineSegment StartX=-23.6 StartY=-1.8 StartZ=0 EndX=-23.6 EndY=-36.4 EndZ=0
  constraints (48):
    c: Block(g0)
    c: Block(g1)
    c: Block(g2)
    c: Block(g3)
    c: Block(g4)
    c: Block(g5)
    c: Block(g6)
    c: Block(g7)
    c: Block(g8)
    c: Block(g9)
    c: Block(g10)
    c: Block(g11)
    c: Coincident(g12,g1)
    c: Coincident(g12,g2)
    c: Vertical(g12)
    c: Coincident(g13,g1)
    c: Coincident(g13,g2)
    c: Vertical(g13)
    c: Coincident(g14,g11)
    c: Coincident(g14,g7)
    c: Vertical(g14)
    c: Coincident(g15,g11)
    c: Coincident(g15,g7)
    c: Vertical(g15)
    c: Coincident(g16,g0)
    c: Coincident(g16,g3)
    c: Vertical(g16)
    c: Coincident(g17,g4)
    c: Coincident(g17,g8)
    c: Vertical(g17)
    c: Coincident(g18,g0)
    c: Coincident(g18,g3)
    c: Vertical(g18)
    c: Coincident(g19,g4)
    c: Coincident(g19,g8)
    c: Vertical(g19)
    c: Coincident(g20,g5)
    c: Coincident(g20,g9)
    c: Vertical(g20)
    c: Coincident(g21,g5)
    c: Coincident(g21,g9)
    c: Vertical(g21)
    c: Coincident(g22,g10)
    c: Coincident(g22,g6)
    c: Vertical(g22)
    c: Coincident(g23,g6)
    c: Coincident(g23,g10)
    c: Vertical(g23)
FEATURE [Part::Extrusion] Extrude045  label="removeToCreateFanGrillHoles003"
  Base = -> Sketch054
  Dir = (0,-1,6e-16)
  DirMode = 2
  FaceMakerClass = Part::FaceMakerBullseye
  LengthFwd = 10
  LengthRev = 0
  Placement = pos=(65.4,44,54.82) rot=(0,0,1;0rad)
  Solid = true
  Symmetric = false
FEATURE [Part::Feature] Face105 .. Face108  x4 (patterned run collapsed; names and placements below)
  shape: bbox 3.5 x 17.8 x 2e-07 mm, 1 faces, 0 solids (baked)
FEATURE [Part::Revolution] Revolve113  label="removeToCreateScrewAndThreadedInsertHole041"
  Angle = 360
  Axis = (0,1,0)
  Base = (0,0,0)
  FaceMakerClass = Part::FaceMakerBullseye
  Placement = pos=(62.3,30.3,19.7) rot=(0,0,1;0rad)
  Solid = false
  Source = -> Face105
  Symmetric = false
FEATURE [Part::Revolution] Revolve114  label="removeToCreateScrewAndThreadedInsertHole042"
  Angle = 360
  Axis = (0,1,0)
  Base = (0,0,0)
  FaceMakerClass = Part::FaceMakerBullseye
  Placement = pos=(62.3,30.3,51.7) rot=(0,0,1;0rad)
  Solid = false
  Source = -> Face106
  Symmetric = false
FEATURE [Part::Revolution] Revolve115  label="removeToCreateScrewAndThreadedInsertHole043"
  Angle = 360
  Axis = (0,1,0)
  Base = (0,0,0)
  FaceMakerClass = Part::FaceMakerBullseye
  Placement = pos=(30.3,30.3,19.7) rot=(0,0,1;0rad)
  Solid = false
  Source = -> Face107
  Symmetric = false
FEATURE [Part::Revolution] Revolve116  label="removeToCreateScrewAndThreadedInsertHole044"
  Angle = 360
  Axis = (0,1,0)
  Base = (0,0,0)
  FaceMakerClass = Part::FaceMakerBullseye
  Placement = pos=(30.3,30.3,51.7) rot=(0,0,1;0rad)
  Solid = false
  Source = -> Face108
  Symmetric = false
FEATURE [Part::MultiFuse] Fusion083  label="createThreadedInsertHolesForFan004"
  Shapes = -> [Revolve113,Revolve114,Revolve115,Revolve116]
FEATURE [Part::Box] Box024  label="removeToCreteHoleForPlugHousing026"
  AttacherType = Attacher::AttachEngine3D
  Height = 28.6
  Length = 10
  Placement = pos=(-2,0,21.7) rot=(0,0,1;0rad)
  Width = 19
FEATURE [Part::Cylinder] Cylinder038  label="removeToCreteHoleForPlugHousing027"
  Angle = 360
  AttacherType = Attacher::AttachEngine3D
  Height = 20
  Placement = pos=(-2,19,36) rot=(0,1,0;1.5708rad)
  Radius = 14.3
FEATURE [Part::MultiFuse] Fusion084  label="removeToCreteHoleForPlugHousing028"
  Shapes = -> [Box024,Cylinder038]
FEATURE [Part::Cylinder] Cylinder039
  Angle = 360
  AttacherType = Attacher::AttachEngine3D
  Height = 20
  Placement = pos=(0,0,36.15) rot=(0,0,1;0rad)
  Radius = 14.3
FEATURE [Part::Cylinder] Cylinder040
  Angle = 360
  AttacherType = Attacher::AttachEngine3D
  Height = 10
  Placement = pos=(0,0,36.15) rot=(0,0,1;0rad)
  Radius = 4
FEATURE [Part::Box] Box025  label="removeToCreteHoleForPlugHousing030"
  AttacherType = Attacher::AttachEngine3D
  Height = 28.6
  Length = 20
  Placement = pos=(106.15,0,21.7) rot=(0,0,1;0rad)
  Width = 19
FEATURE [Part::MultiFuse] Fusion086  label="removeToCreteHoleForPlugHousing031"
  Placement = pos=(70,19,36) rot=(0,1,0;1.5708rad)
  Shapes = -> [Cylinder039,Cylinder040]
FEATURE [Part::MultiFuse] Fusion085  label="removeToCreteHoleForPlugHousing029"
  Shapes = -> [Box025,Fusion086]
FEATURE [Sketcher::SketchObject] Sketch055
  FullyConstrained = true
  Placement = pos=(117,19,0) rot=(0.57735,0.57735,0.57735;2.0944rad)
  sketch-geometry (48):
    g0: LineSegment StartX=-49.19 StartY=69.25 StartZ=0 EndX=-49.19 EndY=66.25 EndZ=0
    g1: LineSegment StartX=-49.19 StartY=63.5 StartZ=0 EndX=-49.19 EndY=60.5 EndZ=0
    g2: LineSegment StartX=-49.19 StartY=57.75 StartZ=0 EndX=-49.19 EndY=54.75 EndZ=0
    g3: LineSegment StartX=-49.19 StartY=52 StartZ=0 EndX=-49.19 EndY=49 EndZ=0
    g4: LineSegment StartX=-49.19 StartY=46.25 StartZ=0 EndX=-49.19 EndY=43.25 EndZ=0
    g5: LineSegment StartX=-49.19 StartY=40.5 StartZ=0 EndX=-49.19 EndY=37.5 EndZ=0
    g6: LineSegment StartX=-49.19 StartY=34.5 StartZ=0 EndX=-49.19 EndY=31.5 EndZ=0
    g7: LineSegment StartX=-49.19 StartY=28.75 StartZ=0 EndX=-49.19 EndY=25.75 EndZ=0
    g8: LineSegment StartX=-49.19 StartY=23 StartZ=0 EndX=-49.19 EndY=20 EndZ=0
    g9: LineSegment StartX=-49.19 StartY=17.25 StartZ=0 EndX=-49.19 EndY=14.25 EndZ=0
    g10: LineSegment StartX=-49.19 StartY=11.5 StartZ=0 EndX=-49.19 EndY=8.5 EndZ=0
    g11: LineSegment StartX=-49.19 StartY=5.75 StartZ=0 EndX=-49.19 EndY=2.75 EndZ=0
    g12: ArcOfCircle CenterX=-1.5 CenterY=67.75 CenterZ=0 NormalX=0 NormalY=0 NormalZ=1 AngleXU=0 Radius=1.5 StartAngle=4.71239 EndAngle=7.85398
    g13: ArcOfCircle CenterX=-1.5 CenterY=62 CenterZ=0 NormalX=0 NormalY=0 NormalZ=1 AngleXU=0 Radius=1.5 StartAngle=4.71239 EndAngle=7.85398
    g14: ArcOfCircle CenterX=-1.5 CenterY=56.25 CenterZ=0 NormalX=0 NormalY=0 NormalZ=1 AngleXU=0 Radius=1.5 StartAngle=4.71239 EndAngle=7.85398
    g15: ArcOfCircle CenterX=-11.49 CenterY=50.5 CenterZ=0 NormalX=0 NormalY=0 NormalZ=1 AngleXU=0 Radius=1.5 StartAngle=4.71239 EndAngle=7.85398
    g16: ArcOfCircle CenterX=-16.28 CenterY=44.75 CenterZ=0 NormalX=0 NormalY=0 NormalZ=1 AngleXU=0 Radius=1.5 StartAngle=4.71239 EndAngle=7.85398
    g17: ArcOfCircle CenterX=-18.2337 CenterY=39 CenterZ=0 NormalX=0 NormalY=0 NormalZ=1 AngleXU=0 Radius=1.5 StartAngle=4.71485 EndAngle=7.85398
    g18: ArcOfCircle CenterX=-16.2837 CenterY=27.25 CenterZ=0 NormalX=0 NormalY=0 NormalZ=1 AngleXU=0 Radius=1.5 StartAngle=4.71485 EndAngle=7.85398
    g19: ArcOfCircle CenterX=-18.2337 CenterY=33 CenterZ=0 NormalX=0 NormalY=0 NormalZ=1 AngleXU=0 Radius=1.5 StartAngle=4.71485 EndAngle=7.85398
    g20: ArcOfCircle CenterX=-11.49 CenterY=21.5 CenterZ=0 NormalX=0 NormalY=0 NormalZ=1 AngleXU=0 Radius=1.5 StartAngle=4.71239 EndAngle=7.85398
    g21: ArcOfCircle CenterX=-1.5 CenterY=4.25 CenterZ=0 NormalX=0 NormalY=0 NormalZ=1 AngleXU=0 Radius=1.5 StartAngle=4.71239 EndAngle=7.85398
    g22: ArcOfCircle CenterX=-1.5 CenterY=10 CenterZ=0 NormalX=0 NormalY=0 NormalZ=1 AngleXU=0 Radius=1.5 StartAngle=4.71239 EndAngle=7.85398
    g23: ArcOfCircle CenterX=-1.5 CenterY=15.75 CenterZ=0 NormalX=0 NormalY=0 NormalZ=1 AngleXU=0 Radius=1.5 StartAngle=4.71239 EndAngle=7.85398
    g24: LineSegment StartX=-49.19 StartY=69.25 StartZ=0 EndX=-1.5 EndY=69.25 EndZ=0
    g25: LineSegment StartX=-49.19 StartY=66.25 StartZ=0 EndX=-1.5 EndY=66.25 EndZ=0
    g26: LineSegment StartX=-49.19 StartY=63.5 StartZ=0 EndX=-1.5 EndY=63.5 EndZ=0
    g27: LineSegment StartX=-49.19 StartY=60.5 StartZ=0 EndX=-1.5 EndY=60.5 EndZ=0
    g28: LineSegment StartX=-49.19 StartY=57.75 StartZ=0 EndX=-1.5 EndY=57.75 EndZ=0
    g29: LineSegment StartX=-49.19 StartY=54.75 StartZ=0 EndX=-1.5 EndY=54.75 EndZ=0
    g30: LineSegment StartX=-49.19 StartY=52 StartZ=0 EndX=-11.49 EndY=52 EndZ=0
    g31: LineSegment StartX=-49.19 StartY=49 StartZ=0 EndX=-11.49 EndY=49 EndZ=0
    g32: LineSegment StartX=-49.19 StartY=46.25 StartZ=0 EndX=-16.28 EndY=46.25 EndZ=0
    g33: LineSegment StartX=-49.19 StartY=43.25 StartZ=0 EndX=-16.28 EndY=43.25 EndZ=0
    g34: LineSegment StartX=-49.19 StartY=40.5 StartZ=0 EndX=-18.2337 EndY=40.5 EndZ=0
    g35: LineSegment StartX=-49.19 StartY=37.5 StartZ=0 EndX=-18.23 EndY=37.5 EndZ=0
    g36: LineSegment StartX=-49.19 StartY=34.5 StartZ=0 EndX=-18.2337 EndY=34.5 EndZ=0
    g37: LineSegment StartX=-49.19 StartY=31.5 StartZ=0 EndX=-18.23 EndY=31.5 EndZ=0
    g38: LineSegment StartX=-49.19 StartY=28.75 StartZ=0 EndX=-16.2837 EndY=28.75 EndZ=0
    g39: LineSegment StartX=-49.19 StartY=25.75 StartZ=0 EndX=-16.28 EndY=25.75 EndZ=0
    g40: LineSegment StartX=-49.19 StartY=23 StartZ=0 EndX=-11.49 EndY=23 EndZ=0
    g41: LineSegment StartX=-49.19 StartY=20 StartZ=0 EndX=-11.49 EndY=20 EndZ=0
    g42: LineSegment StartX=-49.19 StartY=17.25 StartZ=0 EndX=-1.5 EndY=17.25 EndZ=0
    g43: LineSegment StartX=-49.19 StartY=14.25 StartZ=0 EndX=-1.5 EndY=14.25 EndZ=0
    g44: LineSegment StartX=-49.19 StartY=11.5 StartZ=0 EndX=-1.5 EndY=11.5 EndZ=0
    g45: LineSegment StartX=-49.19 StartY=8.5 StartZ=0 EndX=-1.5 EndY=8.5 EndZ=0
    g46: LineSegment StartX=-49.19 StartY=5.75 StartZ=0 EndX=-1.5 EndY=5.75 EndZ=0
    g47: LineSegment StartX=-49.19 StartY=2.75 StartZ=0 EndX=-1.5 EndY=2.75 EndZ=0
  constraints (120):
    c: Vertical(g0)
    c: Distance(g0) = 3
    c: Block(g0)
    c: Vertical(g1)
    c: Distance(g1) = 3
    c: Vertical(g2)
    c: Equal(g0,g2) = 3
    c: Block(g2)
    c: Vertical(g3)
    c: Equal(g1,g3) = 3
    c: Vertical(g4)
    c: Equal(g0,g4) = 3
    c: Block(g4)
    c: Vertical(g5)
    c: Equal(g1,g5) = 3
    c: Vertical(g6)
    c: Equal(g0,g6) = 3
    c: Block(g6)
    c: Vertical(g7)
    c: Equal(g1,g7) = 3
    c: Vertical(g8)
    c: Equal(g0,g8) = 3
    c: Block(g8)
    c: Vertical(g9)
    c: Equal(g1,g9) = 3
    c: Vertical(g10)
    c: Equal(g0,g10) = 3
    c: Block(g10)
    c: Vertical(g11)
    c: Equal(g1,g11) = 3
    c: Block(g12)
    c: Block(g13)
    c: Block(g14)
    c: Block(g15)
    c: Block(g16)
    c: Block(g17)
    c: Block(g18)
    c: Block(g19)
    c: Block(g20)
    c: Block(g21)
    c: Block(g22)
    c: Block(g23)
    c: Block(g11)
    c: Block(g9)
    c: Block(g7)
    c: Block(g5)
    c: Block(g3)
    c: Block(g1)
    c: Coincident(g24,g0)
    c: Coincident(g24,g12)
    c: Horizontal(g24)
    c: Coincident(g25,g0)
    c: Coincident(g25,g12)
    c: Horizontal(g25)
    c: Coincident(g26,g1)
    c: Coincident(g26,g13)
    c: Horizontal(g26)
    c: Coincident(g27,g1)
    c: Coincident(g27,g13)
    c: Horizontal(g27)
    c: Coincident(g28,g2)
    c: Coincident(g28,g14)
    c: Horizontal(g28)
    c: Coincident(g29,g2)
    c: Coincident(g29,g14)
    c: Horizontal(g29)
    c: Coincident(g30,g3)
    c: Coincident(g30,g15)
    c: Horizontal(g30)
    c: Coincident(g31,g3)
    c: Coincident(g31,g15)
    c: Horizontal(g31)
    c: Coincident(g32,g4)
    c: Coincident(g32,g16)
    c: Horizontal(g32)
    c: Coincident(g33,g4)
    c: Coincident(g33,g16)
    c: Horizontal(g33)
    c: Coincident(g34,g5)
    c: Coincident(g34,g17)
    c: Horizontal(g34)
    c: Coincident(g35,g5)
    c: Coincident(g35,g17)
    c: Horizontal(g35)
    c: Coincident(g36,g6)
    c: Coincident(g36,g19)
    c: Horizontal(g36)
    c: Coincident(g37,g6)
    c: Coincident(g37,g19)
    c: Horizontal(g37)
    c: Coincident(g38,g7)
    c: Coincident(g38,g18)
    c: Horizontal(g38)
    c: Coincident(g39,g7)
    c: Coincident(g39,g18)
    c: Horizontal(g39)
    c: Coincident(g40,g8)
    c: Coincident(g40,g20)
    c: Horizontal(g40)
    c: Coincident(g41,g8)
    c: Coincident(g41,g20)
    c: Horizontal(g41)
    c: Coincident(g42,g9)
    c: Coincident(g42,g23)
    c: Horizontal(g42)
    c: Coincident(g43,g9)
    c: Coincident(g43,g23)
    c: Horizontal(g43)
    c: Coincident(g44,g10)
    c: Coincident(g44,g22)
    c: Horizontal(g44)
    c: Coincident(g45,g10)
    c: Coincident(g45,g22)
    c: Horizontal(g45)
    c: Coincident(g46,g11)
    c: Coincident(g46,g21)
    c: Horizontal(g46)
    c: Coincident(g47,g11)
    c: Coincident(g47,g21)
    c: Horizontal(g47)
FEATURE [Part::Extrusion] Extrude046
  Base = -> Sketch055
  Dir = (1,0,0)
  DirMode = 2
  FaceMakerClass = Part::FaceMakerBullseye
  LengthFwd = 23
  LengthRev = 0
  Placement = pos=(-19,0,0) rot=(0,0,1;0rad)
  Solid = true
  Symmetric = false
FEATURE [Part::Fillet] Fillet038  label="removeToCreateVentalationHoles001"
  Base = -> Extrude046
  Edges = <same value as first occurrence — deduplicated (x6 in doc)>
  Placement = pos=(7,0,0) rot=(0,0,1;0rad)
FEATURE [Sketcher::SketchObject] Sketch056  label="topSketch014"
  FullyConstrained = true
  sketch-geometry (22):
    g0: LineSegment StartX=5.21097e-06 StartY=3 StartZ=0 EndX=5.21097e-06 EndY=19 EndZ=0
    g1: ArcOfCircle CenterX=19 CenterY=19 CenterZ=0 NormalX=0 NormalY=0 NormalZ=1 AngleXU=0 Radius=19 StartAngle=1.5708 EndAngle=3.14159
    g2: ArcOfCircle CenterX=19 CenterY=19 CenterZ=0 NormalX=0 NormalY=0 NormalZ=1 AngleXU=0 Radius=16 StartAngle=1.5708 EndAngle=3.14159
    g3: LineSegment StartX=114 StartY=35 StartZ=0 EndX=19 EndY=35 EndZ=0
    g4: LineSegment StartX=5.21097e-06 StartY=3 StartZ=0 EndX=5.21097e-06 EndY=0 EndZ=0
    g5: LineSegment StartX=3 StartY=0 StartZ=0 EndX=5.21097e-06 EndY=0 EndZ=0
    g6: LineSegment StartX=3 StartY=19 StartZ=0 EndX=3 EndY=0 EndZ=0
    g7: LineSegment StartX=19 StartY=38 StartZ=0 EndX=124 EndY=38 EndZ=0
    g8: Circle CenterX=119 CenterY=35 CenterZ=0 NormalX=0 NormalY=0 NormalZ=1 AngleXU=0 Radius=1
    g9: Circle CenterX=121 CenterY=35 CenterZ=0 NormalX=0 NormalY=0 NormalZ=1 AngleXU=0 Radius=1
    g10: Circle CenterX=121 CenterY=33 CenterZ=0 NormalX=0 NormalY=0 NormalZ=1 AngleXU=0 Radius=1
    g11: BSplineCurve PolesCount=3 KnotsCount=2 Degree=2 IsPeriodic=0
    g12: GeomPoint X=119 Y=35 Z=0
    g13: GeomPoint X=121 Y=33 Z=0
    g14: LineSegment StartX=119 StartY=35 StartZ=0 EndX=114 EndY=35 EndZ=0
    g15: ArcOfCircle CenterX=105 CenterY=19 CenterZ=0 NormalX=0 NormalY=0 NormalZ=1 AngleXU=0 Radius=16 StartAngle=5.60905 EndAngle=6.28319
    g16: LineSegment StartX=121 StartY=33 StartZ=0 EndX=121 EndY=19 EndZ=0
    g17: LineSegment StartX=117.5 StartY=9.01251 StartZ=0 EndX=121.163 EndY=9.0125 EndZ=0
    g18: ArcOfCircle CenterX=105 CenterY=19 CenterZ=0 NormalX=0 NormalY=0 NormalZ=1 AngleXU=0 Radius=20.6155 StartAngle=5.7297 EndAngle=6.28319
    g19: LineSegment StartX=121.163 StartY=9.0125 StartZ=0 EndX=122.538 EndY=8.16329 EndZ=0
    g20: LineSegment StartX=124 StartY=38 StartZ=0 EndX=125.616 EndY=38 EndZ=0
    g21: LineSegment StartX=125.616 StartY=19 StartZ=0 EndX=125.616 EndY=38 EndZ=0
  constraints (49):
    c: Vertical(g0)
    c: Block(g0)
    c: Coincident(g1,g0)
    c: Block(g1)
    c: Coincident(g2,g1)
    c: Block(g2)
    c: Coincident(g3,g2)
    c: Horizontal(g3)
    c: Tangent(g3,g2)
    c: Coincident(g4,g0)
    c: Distance(g4) = 3
    c: Vertical(g4)
    c: Coincident(g5,g4)
    c: Horizontal(g5)
    c: Coincident(g6,g2)
    c: Coincident(g6,g5)
    c: Vertical(g6)
    c: Horizontal(g7)
    c: Distance(g7) = 105
    c: Coincident(g7,g1)
    c: Block(g3)
    c: Weight(g8) = 1
    c: Equal(g8,g9)
    c: Equal(g8,g10)
    c: InternalAlignment(g8,g11)
    c: InternalAlignment(g9,g11)
    c: InternalAlignment(g10,g11)
    c: InternalAlignment(g12,g11)
    c: InternalAlignment(g13,g11)
    c: Block(g11)
    c: Coincident(g14,g11)
    c: Coincident(g14,g3)
    c: Horizontal(g14)
    c: Block(g15)
    c: Coincident(g16,g11)
    c: Coincident(g16,g15)
    c: Vertical(g16)
    c: Distance(g16) = 14
    c: Coincident(g17,g15)
    c: Block(g18)
    c: Coincident(g19,g18)
    c: Coincident(g20,g7)
    c: Horizontal(g20)
    c: Vertical(g21)
    c: Coincident(g20,g21)
    c: Block(g20)
    c: Block(g21)
    c: Block(g19)
    c: Block(g17)
FEATURE [Part::Box] Box026  label="removeToCreteHoleForPlugHousing032"
  AttacherType = Attacher::AttachEngine3D
  Height = 28.6
  Length = 10
  Placement = pos=(-2,0,21.7) rot=(0,0,1;0rad)
  Width = 19
FEATURE [Part::Feature] Face109 .. Face112  x4 (patterned run collapsed; names and placements below)
  shape: bbox 3.5 x 17.8 x 2e-07 mm, 1 faces, 0 solids (baked)
FEATURE [Part::Revolution] Revolve117  label="removeToCreateScrewAndThreadedInsertHole045"
  Angle = 360
  Axis = (0,1,0)
  Base = (0,0,0)
  FaceMakerClass = Part::FaceMakerBullseye
  Placement = pos=(62.3,30.3,19.7) rot=(0,0,1;0rad)
  Solid = false
  Source = -> Face109
  Symmetric = false
FEATURE [Part::Revolution] Revolve118  label="removeToCreateScrewAndThreadedInsertHole046"
  Angle = 360
  Axis = (0,1,0)
  Base = (0,0,0)
  FaceMakerClass = Part::FaceMakerBullseye
  Placement = pos=(62.3,30.3,51.7) rot=(0,0,1;0rad)
  Solid = false
  Source = -> Face110
  Symmetric = false
FEATURE [Part::Revolution] Revolve119  label="removeToCreateScrewAndThreadedInsertHole047"
  Angle = 360
  Axis = (0,1,0)
  Base = (0,0,0)
  FaceMakerClass = Part::FaceMakerBullseye
  Placement = pos=(30.3,30.3,19.7) rot=(0,0,1;0rad)
  Solid = false
  Source = -> Face111
  Symmetric = false
FEATURE [Part::Revolution] Revolve120  label="removeToCreateScrewAndThreadedInsertHole048"
  Angle = 360
  Axis = (0,1,0)
  Base = (0,0,0)
  FaceMakerClass = Part::FaceMakerBullseye
  Placement = pos=(30.3,30.3,51.7) rot=(0,0,1;0rad)
  Solid = false
  Source = -> Face112
  Symmetric = false
FEATURE [Part::MultiFuse] Fusion087  label="createThreadedInsertHolesForFan005"
  Shapes = -> [Revolve117,Revolve118,Revolve119,Revolve120]
FEATURE [Part::Extrusion] Extrude047
  Base = -> Sketch056
  Dir = (0,0,1)
  DirMode = 2
  FaceMakerClass = Part::FaceMakerBullseye
  LengthFwd = 72
  LengthRev = 0
  Solid = true
  Symmetric = false
FEATURE [Part::Fillet] Fillet039  label="top019"
  Base = -> Extrude047
  Edges = 1 edges r=2: [Edge35]
FEATURE [Sketcher::SketchObject] Sketch057
  FullyConstrained = false
  Placement = pos=(0,0,0) rot=(1,0,0;1.5708rad)
  sketch-geometry (24):
    g0: ArcOfCircle CenterX=-4 CenterY=-10.5 CenterZ=0 NormalX=0 NormalY=0 NormalZ=1 AngleXU=0 Radius=1.5 StartAngle=6e-16 EndAngle=3.14159
    g1: ArcOfCircle CenterX=-34.2 CenterY=-10.5 CenterZ=0 NormalX=0 NormalY=0 NormalZ=1 AngleXU=0 Radius=1.5 StartAngle=0 EndAngle=3.14159
    g2: ArcOfCircle CenterX=-34.2 CenterY=-27.7 CenterZ=0 NormalX=0 NormalY=0 NormalZ=1 AngleXU=0 Radius=1.5 StartAngle=3.14159 EndAngle=6.28319
    g3: ArcOfCircle CenterX=-4 CenterY=-27.7 CenterZ=0 NormalX=0 NormalY=0 NormalZ=1 AngleXU=0 Radius=1.5 StartAngle=3.1416 EndAngle=6.28319
    g4: ArcOfCircle CenterX=-10 CenterY=-4.3 CenterZ=0 NormalX=0 NormalY=0 NormalZ=1 AngleXU=0 Radius=1.5 StartAngle=2e-16 EndAngle=3.14159
    g5: ArcOfCircle CenterX=-16.1 CenterY=-1.8 CenterZ=0 NormalX=0 NormalY=0 NormalZ=1 AngleXU=0 Radius=1.5 StartAngle=5e-16 EndAngle=3.14159
    g6: ArcOfCircle CenterX=-22.1 CenterY=-1.8 CenterZ=0 NormalX=0 NormalY=0 NormalZ=1 AngleXU=0 Radius=1.5 StartAngle=5e-16 EndAngle=3.14159
    g7: ArcOfCircle CenterX=-28.2 CenterY=-4.3 CenterZ=0 NormalX=0 NormalY=0 NormalZ=1 AngleXU=0 Radius=1.5 StartAngle=2e-16 EndAngle=3.14159
    g8: ArcOfCircle CenterX=-10 CenterY=-33.9 CenterZ=0 NormalX=0 NormalY=0 NormalZ=1 AngleXU=0 Radius=1.5 StartAngle=3.14159 EndAngle=6.28319
    g9: ArcOfCircle CenterX=-16.1 CenterY=-36.4 CenterZ=0 NormalX=0 NormalY=0 NormalZ=1 AngleXU=0 Radius=1.5 StartAngle=3.14159 EndAngle=6.28319
    g10: ArcOfCircle CenterX=-22.1 CenterY=-36.4 CenterZ=0 NormalX=0 NormalY=0 NormalZ=1 AngleXU=0 Radius=1.5 StartAngle=3.14159 EndAngle=6.28319
    g11: ArcOfCircle CenterX=-28.2 CenterY=-33.9 CenterZ=0 NormalX=0 NormalY=0 NormalZ=1 AngleXU=0 Radius=1.5 StartAngle=3.14159 EndAngle=6.28319
    g12: LineSegment StartX=-35.7 StartY=-10.5 StartZ=0 EndX=-35.7 EndY=-27.7 EndZ=0
    g13: LineSegment StartX=-32.7 StartY=-10.5 StartZ=0 EndX=-32.7 EndY=-27.7 EndZ=0
    g14: LineSegment StartX=-29.7 StartY=-33.9 StartZ=0 EndX=-29.7 EndY=-4.3 EndZ=0
    g15: LineSegment StartX=-26.7 StartY=-33.9 StartZ=0 EndX=-26.7 EndY=-4.3 EndZ=0
    g16: LineSegment StartX=-2.5 StartY=-10.5 StartZ=0 EndX=-2.5 EndY=-27.7 EndZ=0
    g17: LineSegment StartX=-8.5 StartY=-4.3 StartZ=0 EndX=-8.5 EndY=-33.9 EndZ=0
    g18: LineSegment StartX=-5.5 StartY=-10.5 StartZ=0 EndX=-5.5 EndY=-27.7 EndZ=0
    g19: LineSegment StartX=-11.5 StartY=-4.3 StartZ=0 EndX=-11.5 EndY=-33.9 EndZ=0
    g20: LineSegment StartX=-14.6 StartY=-1.8 StartZ=0 EndX=-14.6 EndY=-36.4 EndZ=0
    g21: LineSegment StartX=-17.6 StartY=-1.8 StartZ=0 EndX=-17.6 EndY=-36.4 EndZ=0
    g22: LineSegment StartX=-20.6 StartY=-36.4 StartZ=0 EndX=-20.6 EndY=-1.8 EndZ=0
    g23: LineSegment StartX=-23.6 StartY=-1.8 StartZ=0 EndX=-23.6 EndY=-36.4 EndZ=0
  constraints (48):
    c: Block(g0)
    c: Block(g1)
    c: Block(g2)
    c: Block(g3)
    c: Block(g4)
    c: Block(g5)
    c: Block(g6)
    c: Block(g7)
    c: Block(g8)
    c: Block(g9)
    c: Block(g10)
    c: Block(g11)
    c: Coincident(g12,g1)
    c: Coincident(g12,g2)
    c: Vertical(g12)
    c: Coincident(g13,g1)
    c: Coincident(g13,g2)
    c: Vertical(g13)
    c: Coincident(g14,g11)
    c: Coincident(g14,g7)
    c: Vertical(g14)
    c: Coincident(g15,g11)
    c: Coincident(g15,g7)
    c: Vertical(g15)
    c: Coincident(g16,g0)
    c: Coincident(g16,g3)
    c: Vertical(g16)
    c: Coincident(g17,g4)
    c: Coincident(g17,g8)
    c: Vertical(g17)
    c: Coincident(g18,g0)
    c: Coincident(g18,g3)
    c: Vertical(g18)
    c: Coincident(g19,g4)
    c: Coincident(g19,g8)
    c: Vertical(g19)
    c: Coincident(g20,g5)
    c: Coincident(g20,g9)
    c: Vertical(g20)
    c: Coincident(g21,g5)
    c: Coincident(g21,g9)
    c: Vertical(g21)
    c: Coincident(g22,g10)
    c: Coincident(g22,g6)
    c: Vertical(g22)
    c: Coincident(g23,g6)
    c: Coincident(g23,g10)
    c: Vertical(g23)
FEATURE [Part::Extrusion] Extrude048  label="removeToCreateFanGrillHoles004"
  Base = -> Sketch057
  Dir = (0,-1,6e-16)
  DirMode = 2
  FaceMakerClass = Part::FaceMakerBullseye
  LengthFwd = 10
  LengthRev = 0
  Placement = pos=(65.4,44,54.82) rot=(0,0,1;0rad)
  Solid = true
  Symmetric = false
FEATURE [Part::Cut] Cut040  label="top021"
  Base = -> Fillet039
  Tool = -> Extrude048
FEATURE [Part::Cylinder] Cylinder041  label="removeToCreteHoleForPlugHousing034"
  Angle = 360
  AttacherType = Attacher::AttachEngine3D
  Height = 20
  Placement = pos=(-2,19,36) rot=(0,1,0;1.5708rad)
  Radius = 14.3
FEATURE [Part::MultiFuse] Fusion089  label="removeToCreteHoleForPlugHousing035"
  Shapes = -> [Box026,Cylinder041]
FEATURE [Part::Cylinder] Cylinder042
  Angle = 360
  AttacherType = Attacher::AttachEngine3D
  Height = 20
  Placement = pos=(0,0,36.15) rot=(0,0,1;0rad)
  Radius = 14.3
FEATURE [Part::Cylinder] Cylinder043
  Angle = 360
  AttacherType = Attacher::AttachEngine3D
  Height = 10
  Placement = pos=(0,0,36.15) rot=(0,0,1;0rad)
  Radius = 4
FEATURE [Part::Box] Box027  label="removeToCreteHoleForPlugHousing036"
  AttacherType = Attacher::AttachEngine3D
  Height = 28.6
  Length = 20
  Placement = pos=(106.15,0,21.7) rot=(0,0,1;0rad)
  Width = 19
FEATURE [Part::Cut] Cut041  label="top022"
  Base = -> Cut040
  Tool = -> Fusion087
FEATURE [Part::Cut] Cut039  label="top020"
  Base = -> Cut041
  Tool = -> Fusion089
FEATURE [Part::MultiFuse] Fusion090  label="removeToCreteHoleForPlugHousing037"
  Placement = pos=(70,19,36) rot=(0,1,0;1.5708rad)
  Shapes = -> [Cylinder042,Cylinder043]
FEATURE [Part::MultiFuse] Fusion088  label="removeToCreteHoleForPlugHousing033"
  Shapes = -> [Box027,Fusion090]
FEATURE [Part::Cut] Cut042  label="removeToCreteHoleForPlugHousing038"
  Base = -> Cut039
  Tool = -> Fusion088
FEATURE [Part::MultiFuse] Fusion091  label="removeFromTop"
  Shapes = -> [Fillet038,Fusion085,Fusion084,Fusion083,Extrude045]
FEATURE [Part::Cut] Cut043  label="REAL TOP ====="
  Base = -> Fillet036
  Tool = -> Fusion091
FEATURE [Part::MultiFuse] Fusion092  label="caseScrewPillarBracket016"
  Shapes = -> [Extrude030,Extrude031,Extrude032,Extrude033,Extrude034,Extrude035,Extrude036,Extrude037,Box013,Box014]
FEATURE [Sketcher::SketchObject] Sketch058  label="topSketch015"
  FullyConstrained = true
  sketch-geometry (20):
    g0: LineSegment StartX=5.21097e-06 StartY=3 StartZ=0 EndX=5.21097e-06 EndY=19 EndZ=0
    g1: ArcOfCircle CenterX=19 CenterY=19 CenterZ=0 NormalX=0 NormalY=0 NormalZ=1 AngleXU=0 Radius=19 StartAngle=1.5708 EndAngle=3.14159
    g2: ArcOfCircle CenterX=19 CenterY=19 CenterZ=0 NormalX=0 NormalY=0 NormalZ=1 AngleXU=0 Radius=16 StartAngle=1.5708 EndAngle=3.14159
    g3: LineSegment StartX=114 StartY=35 StartZ=0 EndX=19 EndY=35 EndZ=0
    g4: LineSegment StartX=5.21097e-06 StartY=3 StartZ=0 EndX=5.21097e-06 EndY=0 EndZ=0
    g5: LineSegment StartX=3 StartY=0 StartZ=0 EndX=5.21097e-06 EndY=0 EndZ=0
    g6: LineSegment StartX=3 StartY=19 StartZ=0 EndX=3 EndY=0 EndZ=0
    g7: LineSegment StartX=19 StartY=38 StartZ=0 EndX=124 EndY=38 EndZ=0
    g8: Circle CenterX=119 CenterY=35 CenterZ=0 NormalX=0 NormalY=0 NormalZ=1 AngleXU=0 Radius=1
    g9: Circle CenterX=121 CenterY=35 CenterZ=0 NormalX=0 NormalY=0 NormalZ=1 AngleXU=0 Radius=1
    g10: Circle CenterX=121 CenterY=33 CenterZ=0 NormalX=0 NormalY=0 NormalZ=1 AngleXU=0 Radius=1
    g11: BSplineCurve PolesCount=3 KnotsCount=2 Degree=2 IsPeriodic=0
    g12: GeomPoint X=119 Y=35 Z=0
    g13: GeomPoint X=121 Y=33 Z=0
    g14: LineSegment StartX=119 StartY=35 StartZ=0 EndX=114 EndY=35 EndZ=0
    g15: ArcOfCircle CenterX=105 CenterY=19 CenterZ=0 NormalX=0 NormalY=0 NormalZ=1 AngleXU=0 Radius=19 StartAngle=5.7297 EndAngle=6.28319
    g16: ArcOfCircle CenterX=105 CenterY=19 CenterZ=0 NormalX=0 NormalY=0 NormalZ=1 AngleXU=0 Radius=16 StartAngle=5.60905 EndAngle=6.28319
    g17: LineSegment StartX=121 StartY=33 StartZ=0 EndX=121 EndY=19 EndZ=0
    g18: LineSegment StartX=124 StartY=38 StartZ=0 EndX=124 EndY=19 EndZ=0
    g19: LineSegment StartX=117.5 StartY=9.01251 StartZ=0 EndX=121.163 EndY=9.0125 EndZ=0
  constraints (46):
    c: Vertical(g0)
    c: Block(g0)
    c: Coincident(g1,g0)
    c: Block(g1)
    c: Coincident(g2,g1)
    c: Block(g2)
    c: Coincident(g3,g2)
    c: Horizontal(g3)
    c: Tangent(g3,g2)
    c: Coincident(g4,g0)
    c: Distance(g4) = 3
    c: Vertical(g4)
    c: Coincident(g5,g4)
    c: Horizontal(g5)
    c: Coincident(g6,g2)
    c: Coincident(g6,g5)
    c: Vertical(g6)
    c: Horizontal(g7)
    c: Distance(g7) = 105
    c: Coincident(g7,g1)
    c: Block(g3)
    c: Weight(g8) = 1
    c: Equal(g8,g9)
    c: Equal(g8,g10)
    c: InternalAlignment(g8,g11)
    c: InternalAlignment(g9,g11)
    c: InternalAlignment(g10,g11)
    c: InternalAlignment(g12,g11)
    c: InternalAlignment(g13,g11)
    c: Block(g11)
    c: Coincident(g14,g11)
    c: Coincident(g14,g3)
    c: Horizontal(g14)
    c: Block(g15)
    c: Coincident(g16,g15)
    c: Block(g16)
    c: Coincident(g17,g11)
    c: Coincident(g17,g16)
    c: Vertical(g17)
    c: Distance(g17) = 14
    c: Coincident(g18,g7)
    c: Coincident(g18,g15)
    c: Vertical(g18)
    c: Distance(g18) = 19
    c: Coincident(g19,g16)
    c: Coincident(g19,g15)
FEATURE [Part::Extrusion] Extrude049  label="top023"
  Base = -> Sketch058
  Dir = (0,0,1)
  DirMode = 2
  FaceMakerClass = Part::FaceMakerBullseye
  LengthFwd = 72
  LengthRev = 0
  Solid = true
  Symmetric = false
FEATURE [Sketcher::SketchObject] Sketch059
  FullyConstrained = true
  MapMode = 3
  Placement = pos=(0,0,0) rot=(1,0,0;1.5708rad)
  Support = -> [Extrude049]
  sketch-geometry (8):
    g0: Circle CenterX=80.351 CenterY=-67.6202 CenterZ=0 NormalX=0 NormalY=0 NormalZ=1 AngleXU=0 Radius=2
    g1: Circle CenterX=80.351 CenterY=-67.6202 CenterZ=0 NormalX=0 NormalY=0 NormalZ=1 AngleXU=0 Radius=3
    g2: Circle CenterX=80.351 CenterY=-4.92017 CenterZ=0 NormalX=0 NormalY=0 NormalZ=1 AngleXU=0 Radius=2
    g3: Circle CenterX=80.351 CenterY=-4.92017 CenterZ=0 NormalX=0 NormalY=0 NormalZ=1 AngleXU=0 Radius=3
    g4: Circle CenterX=23.851 CenterY=-4.92017 CenterZ=0 NormalX=0 NormalY=0 NormalZ=1 AngleXU=0 Radius=2
    g5: Circle CenterX=23.851 CenterY=-4.92017 CenterZ=0 NormalX=0 NormalY=0 NormalZ=1 AngleXU=0 Radius=3
    g6: Circle CenterX=23.851 CenterY=-67.6202 CenterZ=0 NormalX=0 NormalY=0 NormalZ=1 AngleXU=0 Radius=2
    g7: Circle CenterX=23.851 CenterY=-67.6202 CenterZ=0 NormalX=0 NormalY=0 NormalZ=1 AngleXU=0 Radius=3
  constraints (8):
    c: Block(g3)
    c: Block(g2)
    c: Block(g1)
    c: Block(g0)
    c: Block(g6)
    c: Block(g7)
    c: Block(g4)
    c: Block(g5)
FEATURE [Sketcher::SketchObject] Sketch060
  FullyConstrained = true
  MapMode = 3
  Placement = pos=(0,0,0) rot=(1,0,0;1.5708rad)
  Support = -> [Extrude049]
  sketch-geometry (8):
    g0: Circle CenterX=80.351 CenterY=-67.6202 CenterZ=0 NormalX=0 NormalY=0 NormalZ=1 AngleXU=0 Radius=3
    g1: Circle CenterX=80.351 CenterY=-4.92017 CenterZ=0 NormalX=0 NormalY=0 NormalZ=1 AngleXU=0 Radius=3
    g2: Circle CenterX=23.851 CenterY=-4.92017 CenterZ=0 NormalX=0 NormalY=0 NormalZ=1 AngleXU=0 Radius=3
    g3: Circle CenterX=23.851 CenterY=-67.6202 CenterZ=0 NormalX=0 NormalY=0 NormalZ=1 AngleXU=0 Radius=3
    g4: Circle CenterX=23.851 CenterY=-67.6202 CenterZ=0 NormalX=0 NormalY=0 NormalZ=1 AngleXU=0 Radius=5
    g5: Circle CenterX=80.351 CenterY=-67.6202 CenterZ=0 NormalX=0 NormalY=0 NormalZ=1 AngleXU=0 Radius=5
    g6: Circle CenterX=23.851 CenterY=-4.92017 CenterZ=0 NormalX=0 NormalY=0 NormalZ=1 AngleXU=0 Radius=5
    g7: Circle CenterX=80.351 CenterY=-4.92017 CenterZ=0 NormalX=0 NormalY=0 NormalZ=1 AngleXU=0 Radius=5
  constraints (8):
    c: Block(g1)
    c: Block(g0)
    c: Block(g3)
    c: Block(g2)
    c: Block(g5)
    c: Block(g4)
    c: Block(g6)
    c: Block(g7)
FEATURE [Sketcher::SketchObject] Sketch061
  FullyConstrained = true
  MapMode = 3
  Placement = pos=(0,0,0) rot=(1,0,0;1.5708rad)
  sketch-geometry (8):
    g0: Circle CenterX=80.351 CenterY=-67.6202 CenterZ=0 NormalX=0 NormalY=0 NormalZ=1 AngleXU=0 Radius=3
    g1: Circle CenterX=80.351 CenterY=-4.92017 CenterZ=0 NormalX=0 NormalY=0 NormalZ=1 AngleXU=0 Radius=3
    g2: Circle CenterX=23.851 CenterY=-4.92017 CenterZ=0 NormalX=0 NormalY=0 NormalZ=1 AngleXU=0 Radius=3
    g3: Circle CenterX=23.851 CenterY=-67.6202 CenterZ=0 NormalX=0 NormalY=0 NormalZ=1 AngleXU=0 Radius=3
    g4: Circle CenterX=23.851 CenterY=-67.6202 CenterZ=0 NormalX=0 NormalY=0 NormalZ=1 AngleXU=0 Radius=5
    g5: Circle CenterX=80.351 CenterY=-67.6202 CenterZ=0 NormalX=0 NormalY=0 NormalZ=1 AngleXU=0 Radius=5
    g6: Circle CenterX=23.851 CenterY=-4.92017 CenterZ=0 NormalX=0 NormalY=0 NormalZ=1 AngleXU=0 Radius=5
    g7: Circle CenterX=80.351 CenterY=-4.92017 CenterZ=0 NormalX=0 NormalY=0 NormalZ=1 AngleXU=0 Radius=5
  constraints (8):
    c: Block(g1)
    c: Block(g0)
    c: Block(g3)
    c: Block(g2)
    c: Block(g5)
    c: Block(g4)
    c: Block(g6)
    c: Block(g7)
FEATURE [Sketcher::SketchObject] Sketch062  label="topSketch016"
  FullyConstrained = true
  sketch-geometry (20):
    g0: LineSegment StartX=5.21097e-06 StartY=3 StartZ=0 EndX=5.21097e-06 EndY=19 EndZ=0
    g1: ArcOfCircle CenterX=19 CenterY=19 CenterZ=0 NormalX=0 NormalY=0 NormalZ=1 AngleXU=0 Radius=19 StartAngle=1.5708 EndAngle=3.14159
    g2: ArcOfCircle CenterX=19 CenterY=19 CenterZ=0 NormalX=0 NormalY=0 NormalZ=1 AngleXU=0 Radius=16 StartAngle=1.5708 EndAngle=3.14159
    g3: LineSegment StartX=114 StartY=35 StartZ=0 EndX=19 EndY=35 EndZ=0
    g4: LineSegment StartX=5.21097e-06 StartY=3 StartZ=0 EndX=5.21097e-06 EndY=0 EndZ=0
    g5: LineSegment StartX=3 StartY=0 StartZ=0 EndX=5.21097e-06 EndY=0 EndZ=0
    g6: LineSegment StartX=3 StartY=19 StartZ=0 EndX=3 EndY=0 EndZ=0
    g7: LineSegment StartX=19 StartY=38 StartZ=0 EndX=124 EndY=38 EndZ=0
    g8: Circle CenterX=119 CenterY=35 CenterZ=0 NormalX=0 NormalY=0 NormalZ=1 AngleXU=0 Radius=1
    g9: Circle CenterX=121 CenterY=35 CenterZ=0 NormalX=0 NormalY=0 NormalZ=1 AngleXU=0 Radius=1
    g10: Circle CenterX=121 CenterY=33 CenterZ=0 NormalX=0 NormalY=0 NormalZ=1 AngleXU=0 Radius=1
    g11: BSplineCurve PolesCount=3 KnotsCount=2 Degree=2 IsPeriodic=0
    g12: GeomPoint X=119 Y=35 Z=0
    g13: GeomPoint X=121 Y=33 Z=0
    g14: LineSegment StartX=119 StartY=35 StartZ=0 EndX=114 EndY=35 EndZ=0
    g15: ArcOfCircle CenterX=105 CenterY=19 CenterZ=0 NormalX=0 NormalY=0 NormalZ=1 AngleXU=0 Radius=19 StartAngle=5.7297 EndAngle=6.28319
    g16: ArcOfCircle CenterX=105 CenterY=19 CenterZ=0 NormalX=0 NormalY=0 NormalZ=1 AngleXU=0 Radius=16 StartAngle=5.60905 EndAngle=6.28319
    g17: LineSegment StartX=121 StartY=33 StartZ=0 EndX=121 EndY=19 EndZ=0
    g18: LineSegment StartX=124 StartY=38 StartZ=0 EndX=124 EndY=19 EndZ=0
    g19: LineSegment StartX=117.5 StartY=9.01251 StartZ=0 EndX=121.163 EndY=9.0125 EndZ=0
  constraints (46):
    c: Vertical(g0)
    c: Block(g0)
    c: Coincident(g1,g0)
    c: Block(g1)
    c: Coincident(g2,g1)
    c: Block(g2)
    c: Coincident(g3,g2)
    c: Horizontal(g3)
    c: Tangent(g3,g2)
    c: Coincident(g4,g0)
    c: Distance(g4) = 3
    c: Vertical(g4)
    c: Coincident(g5,g4)
    c: Horizontal(g5)
    c: Coincident(g6,g2)
    c: Coincident(g6,g5)
    c: Vertical(g6)
    c: Horizontal(g7)
    c: Distance(g7) = 105
    c: Coincident(g7,g1)
    c: Block(g3)
    c: Weight(g8) = 1
    c: Equal(g8,g9)
    c: Equal(g8,g10)
    c: InternalAlignment(g8,g11)
    c: InternalAlignment(g9,g11)
    c: InternalAlignment(g10,g11)
    c: InternalAlignment(g12,g11)
    c: InternalAlignment(g13,g11)
    c: Block(g11)
    c: Coincident(g14,g11)
    c: Coincident(g14,g3)
    c: Horizontal(g14)
    c: Block(g15)
    c: Coincident(g16,g15)
    c: Block(g16)
    c: Coincident(g17,g11)
    c: Coincident(g17,g16)
    c: Vertical(g17)
    c: Distance(g17) = 14
    c: Coincident(g18,g7)
    c: Coincident(g18,g15)
    c: Vertical(g18)
    c: Distance(g18) = 19
    c: Coincident(g19,g16)
    c: Coincident(g19,g15)
FEATURE [Part::Extrusion] Extrude053  label="top024"
  Base = -> Sketch062
  Dir = (0,0,1)
  DirMode = 2
  FaceMakerClass = Part::FaceMakerBullseye
  LengthFwd = 72
  LengthRev = 0
  Solid = true
  Symmetric = false
FEATURE [Sketcher::SketchObject] Sketch063
  FullyConstrained = true
  MapMode = 3
  Placement = pos=(0,0,0) rot=(1,0,0;1.5708rad)
  Support = -> [Extrude053]
  sketch-geometry (8):
    g0: Circle CenterX=80.351 CenterY=-67.6202 CenterZ=0 NormalX=0 NormalY=0 NormalZ=1 AngleXU=0 Radius=2
    g1: Circle CenterX=80.351 CenterY=-67.6202 CenterZ=0 NormalX=0 NormalY=0 NormalZ=1 AngleXU=0 Radius=3
    g2: Circle CenterX=80.351 CenterY=-4.92017 CenterZ=0 NormalX=0 NormalY=0 NormalZ=1 AngleXU=0 Radius=2
    g3: Circle CenterX=80.351 CenterY=-4.92017 CenterZ=0 NormalX=0 NormalY=0 NormalZ=1 AngleXU=0 Radius=3
    g4: Circle CenterX=23.851 CenterY=-4.92017 CenterZ=0 NormalX=0 NormalY=0 NormalZ=1 AngleXU=0 Radius=2
    g5: Circle CenterX=23.851 CenterY=-4.92017 CenterZ=0 NormalX=0 NormalY=0 NormalZ=1 AngleXU=0 Radius=3
    g6: Circle CenterX=23.851 CenterY=-67.6202 CenterZ=0 NormalX=0 NormalY=0 NormalZ=1 AngleXU=0 Radius=2
    g7: Circle CenterX=23.851 CenterY=-67.6202 CenterZ=0 NormalX=0 NormalY=0 NormalZ=1 AngleXU=0 Radius=3
  constraints (8):
    c: Block(g3)
    c: Block(g2)
    c: Block(g1)
    c: Block(g0)
    c: Block(g6)
    c: Block(g7)
    c: Block(g4)
    c: Block(g5)
FEATURE [Part::Extrusion] Extrude054
  Base = -> Sketch063
  Dir = (0,-1,2e-16)
  DirMode = 2
  FaceMakerClass = Part::FaceMakerBullseye
  LengthFwd = 6
  LengthRev = 0
  Placement = pos=(0,9,0) rot=(0,0,1;0rad)
  Solid = true
  Symmetric = false
FEATURE [Sketcher::SketchObject] Sketch064  label="topSketch017"
  FullyConstrained = true
  sketch-geometry (20):
    g0: LineSegment StartX=5.21097e-06 StartY=3 StartZ=0 EndX=5.21097e-06 EndY=19 EndZ=0
    g1: ArcOfCircle CenterX=19 CenterY=19 CenterZ=0 NormalX=0 NormalY=0 NormalZ=1 AngleXU=0 Radius=19 StartAngle=1.5708 EndAngle=3.14159
    g2: ArcOfCircle CenterX=19 CenterY=19 CenterZ=0 NormalX=0 NormalY=0 NormalZ=1 AngleXU=0 Radius=16 StartAngle=1.5708 EndAngle=3.14159
    g3: LineSegment StartX=114 StartY=35 StartZ=0 EndX=19 EndY=35 EndZ=0
    g4: LineSegment StartX=5.21097e-06 StartY=3 StartZ=0 EndX=5.21097e-06 EndY=0 EndZ=0
    g5: LineSegment StartX=3 StartY=0 StartZ=0 EndX=5.21097e-06 EndY=0 EndZ=0
    g6: LineSegment StartX=3 StartY=19 StartZ=0 EndX=3 EndY=0 EndZ=0
    g7: LineSegment StartX=19 StartY=38 StartZ=0 EndX=124 EndY=38 EndZ=0
    g8: Circle CenterX=119 CenterY=35 CenterZ=0 NormalX=0 NormalY=0 NormalZ=1 AngleXU=0 Radius=1
    g9: Circle CenterX=121 CenterY=35 CenterZ=0 NormalX=0 NormalY=0 NormalZ=1 AngleXU=0 Radius=1
    g10: Circle CenterX=121 CenterY=33 CenterZ=0 NormalX=0 NormalY=0 NormalZ=1 AngleXU=0 Radius=1
    g11: BSplineCurve PolesCount=3 KnotsCount=2 Degree=2 IsPeriodic=0
    g12: GeomPoint X=119 Y=35 Z=0
    g13: GeomPoint X=121 Y=33 Z=0
    g14: LineSegment StartX=119 StartY=35 StartZ=0 EndX=114 EndY=35 EndZ=0
    g15: ArcOfCircle CenterX=105 CenterY=19 CenterZ=0 NormalX=0 NormalY=0 NormalZ=1 AngleXU=0 Radius=19 StartAngle=5.7297 EndAngle=6.28319
    g16: ArcOfCircle CenterX=105 CenterY=19 CenterZ=0 NormalX=0 NormalY=0 NormalZ=1 AngleXU=0 Radius=16 StartAngle=5.60905 EndAngle=6.28319
    g17: LineSegment StartX=121 StartY=33 StartZ=0 EndX=121 EndY=19 EndZ=0
    g18: LineSegment StartX=124 StartY=38 StartZ=0 EndX=124 EndY=19 EndZ=0
    g19: LineSegment StartX=117.5 StartY=9.01251 StartZ=0 EndX=121.163 EndY=9.0125 EndZ=0
  constraints (46):
    c: Vertical(g0)
    c: Block(g0)
    c: Coincident(g1,g0)
    c: Block(g1)
    c: Coincident(g2,g1)
    c: Block(g2)
    c: Coincident(g3,g2)
    c: Horizontal(g3)
    c: Tangent(g3,g2)
    c: Coincident(g4,g0)
    c: Distance(g4) = 3
    c: Vertical(g4)
    c: Coincident(g5,g4)
    c: Horizontal(g5)
    c: Coincident(g6,g2)
    c: Coincident(g6,g5)
    c: Vertical(g6)
    c: Horizontal(g7)
    c: Distance(g7) = 105
    c: Coincident(g7,g1)
    c: Block(g3)
    c: Weight(g8) = 1
    c: Equal(g8,g9)
    c: Equal(g8,g10)
    c: InternalAlignment(g8,g11)
    c: InternalAlignment(g9,g11)
    c: InternalAlignment(g10,g11)
    c: InternalAlignment(g12,g11)
    c: InternalAlignment(g13,g11)
    c: Block(g11)
    c: Coincident(g14,g11)
    c: Coincident(g14,g3)
    c: Horizontal(g14)
    c: Block(g15)
    c: Coincident(g16,g15)
    c: Block(g16)
    c: Coincident(g17,g11)
    c: Coincident(g17,g16)
    c: Vertical(g17)
    c: Distance(g17) = 14
    c: Coincident(g18,g7)
    c: Coincident(g18,g15)
    c: Vertical(g18)
    c: Distance(g18) = 19
    c: Coincident(g19,g16)
    c: Coincident(g19,g15)
FEATURE [Sketcher::SketchObject] Sketch065
  FullyConstrained = true
  MapMode = 3
  Placement = pos=(0,0,0) rot=(1,0,0;1.5708rad)
  sketch-geometry (8):
    g0: Circle CenterX=80.351 CenterY=-67.6202 CenterZ=0 NormalX=0 NormalY=0 NormalZ=1 AngleXU=0 Radius=3
    g1: Circle CenterX=80.351 CenterY=-4.92017 CenterZ=0 NormalX=0 NormalY=0 NormalZ=1 AngleXU=0 Radius=3
    g2: Circle CenterX=23.851 CenterY=-4.92017 CenterZ=0 NormalX=0 NormalY=0 NormalZ=1 AngleXU=0 Radius=3
    g3: Circle CenterX=23.851 CenterY=-67.6202 CenterZ=0 NormalX=0 NormalY=0 NormalZ=1 AngleXU=0 Radius=3
    g4: Circle CenterX=23.851 CenterY=-67.6202 CenterZ=0 NormalX=0 NormalY=0 NormalZ=1 AngleXU=0 Radius=5
    g5: Circle CenterX=80.351 CenterY=-67.6202 CenterZ=0 NormalX=0 NormalY=0 NormalZ=1 AngleXU=0 Radius=5
    g6: Circle CenterX=23.851 CenterY=-4.92017 CenterZ=0 NormalX=0 NormalY=0 NormalZ=1 AngleXU=0 Radius=5
    g7: Circle CenterX=80.351 CenterY=-4.92017 CenterZ=0 NormalX=0 NormalY=0 NormalZ=1 AngleXU=0 Radius=5
  constraints (8):
    c: Block(g1)
    c: Block(g0)
    c: Block(g3)
    c: Block(g2)
    c: Block(g5)
    c: Block(g4)
    c: Block(g6)
    c: Block(g7)
FEATURE [Part::Extrusion] Extrude056
  Base = -> Sketch065
  Dir = (0,-1,2e-16)
  DirMode = 2
  FaceMakerClass = Part::FaceMakerBullseye
  LengthFwd = 2
  LengthRev = 0
  Solid = true
  Symmetric = false
FEATURE [Part::Extrusion] Extrude057  label="top025"
  Base = -> Sketch064
  Dir = (0,0,1)
  DirMode = 2
  FaceMakerClass = Part::FaceMakerBullseye
  LengthFwd = 72
  LengthRev = 0
  Solid = true
  Symmetric = false
FEATURE [Sketcher::SketchObject] Sketch066
  FullyConstrained = true
  MapMode = 3
  Placement = pos=(0,0,0) rot=(1,0,0;1.5708rad)
  Support = -> [Extrude057]
  sketch-geometry (8):
    g0: Circle CenterX=80.351 CenterY=-67.6202 CenterZ=0 NormalX=0 NormalY=0 NormalZ=1 AngleXU=0 Radius=3
    g1: Circle CenterX=80.351 CenterY=-4.92017 CenterZ=0 NormalX=0 NormalY=0 NormalZ=1 AngleXU=0 Radius=3
    g2: Circle CenterX=23.851 CenterY=-4.92017 CenterZ=0 NormalX=0 NormalY=0 NormalZ=1 AngleXU=0 Radius=3
    g3: Circle CenterX=23.851 CenterY=-67.6202 CenterZ=0 NormalX=0 NormalY=0 NormalZ=1 AngleXU=0 Radius=3
    g4: Circle CenterX=23.851 CenterY=-67.6202 CenterZ=0 NormalX=0 NormalY=0 NormalZ=1 AngleXU=0 Radius=5
    g5: Circle CenterX=80.351 CenterY=-67.6202 CenterZ=0 NormalX=0 NormalY=0 NormalZ=1 AngleXU=0 Radius=5
    g6: Circle CenterX=23.851 CenterY=-4.92017 CenterZ=0 NormalX=0 NormalY=0 NormalZ=1 AngleXU=0 Radius=5
    g7: Circle CenterX=80.351 CenterY=-4.92017 CenterZ=0 NormalX=0 NormalY=0 NormalZ=1 AngleXU=0 Radius=5
  constraints (8):
    c: Block(g1)
    c: Block(g0)
    c: Block(g3)
    c: Block(g2)
    c: Block(g5)
    c: Block(g4)
    c: Block(g6)
    c: Block(g7)
FEATURE [Part::Extrusion] Extrude055
  Base = -> Sketch066
  Dir = (0,-1,2e-16)
  DirMode = 2
  FaceMakerClass = Part::FaceMakerBullseye
  LengthFwd = 2
  LengthRev = 0
  Solid = true
  Symmetric = false
FEATURE [Part::Fillet] Fillet041
  Base = -> Extrude056
  Edges = 4 edges r=1.99: [Edge6,Edge12,Edge18,Edge24]
FEATURE [Part::Cut] Cut045
  Base = -> Extrude055
  Placement = pos=(0,6,0) rot=(0,0,1;0rad)
  Tool = -> Fillet041
FEATURE [Part::MultiFuse] Fusion095  label="pcbScrewPillars"
  Placement = pos=(-3.2,-1,72.3) rot=(0,0,1;0rad)
  Shapes = -> [Cut045,Extrude054]
FEATURE [Part::Feature] Face113
  shape: bbox 3.2 x 1.5 x 2e-07 mm, 1 faces, 0 solids (baked)
FEATURE [Part::Revolution] Revolve121  label="backCaseScrewRetainer002"
  Angle = 360
  Axis = (0,1,0)
  Base = (0,0,0)
  FaceMakerClass = Part::FaceMakerBullseye
  Placement = pos=(12.5,3,62) rot=(0,0,1;0rad)
  Solid = false
  Source = -> Face113
  Symmetric = false
FEATURE [Part::Feature] Face114
  shape: bbox 3.2 x 1.5 x 2e-07 mm, 1 faces, 0 solids (baked)
FEATURE [Part::Feature] Face115
  shape: bbox 3.2 x 1.5 x 2e-07 mm, 1 faces, 0 solids (baked)
FEATURE [Part::Feature] Face116
  shape: bbox 3.2 x 1.5 x 2e-07 mm, 1 faces, 0 solids (baked)
FEATURE [Part::Revolution] Revolve122  label="frontCaseScrewRetainer004"
  Angle = 360
  Axis = (0,1,0)
  Base = (0,0,0)
  FaceMakerClass = Part::FaceMakerBullseye
  Placement = pos=(89.5,3,68.5) rot=(0,0,1;0rad)
  Solid = false
  Source = -> Face115
  Symmetric = false
FEATURE [Part::Revolution] Revolve123  label="frontCaseScrewRetainer005"
  Angle = 360
  Axis = (0,1,0)
  Base = (0,0,0)
  FaceMakerClass = Part::FaceMakerBullseye
  Placement = pos=(89.5,3,3.5) rot=(0,0,1;0rad)
  Solid = false
  Source = -> Face116
  Symmetric = false
FEATURE [Part::Revolution] Revolve124  label="backCaseScrewRetainer003"
  Angle = 360
  Axis = (0,1,0)
  Base = (0,0,0)
  FaceMakerClass = Part::FaceMakerBullseye
  Placement = pos=(12.5,3,10) rot=(0,0,1;0rad)
  Solid = false
  Source = -> Face114
  Symmetric = false
FEATURE [Part::Feature] Face117
  shape: bbox 3.6 x 3.2 x 2e-07 mm, 1 faces, 0 solids (baked)
FEATURE [Part::Revolution] Revolve125  label="moreFrontCaseScrewRetainer004"
  Angle = 360
  Axis = (0,1,0)
  Base = (0,0,0)
  FaceMakerClass = Part::FaceMakerBullseye
  Placement = pos=(109.5,4.5,68.5) rot=(0,0,1;0rad)
  Solid = false
  Source = -> Face117
  Symmetric = false
FEATURE [Part::Feature] Face118
  shape: bbox 3.6 x 3.2 x 2e-07 mm, 1 faces, 0 solids (baked)
FEATURE [Part::Revolution] Revolve126  label="moreFrontCaseScrewRetainer005"
  Angle = 360
  Axis = (0,1,0)
  Base = (0,0,0)
  FaceMakerClass = Part::FaceMakerBullseye
  Placement = pos=(109.5,4.5,3.5) rot=(0,0,1;0rad)
  Solid = false
  Source = -> Face118
  Symmetric = false
FEATURE [Part::MultiFuse] Fusion096  label="screwRetainers001"
  Shapes = -> [Revolve126,Revolve125,Revolve124,Revolve123,Revolve122,Revolve121]
FEATURE [Part::Feature] Face119
  shape: bbox 10 x 16.5 x 2e-07 mm, 1 faces, 0 solids (baked)
FEATURE [Part::Revolution] Revolve130  label="plugHousing050"
  Angle = 360
  Axis = (0,1,0)
  Base = (0,0,0)
  FaceMakerClass = Part::FaceMakerBullseye
  Placement = pos=(0,0,36.15) rot=(0,0,1;0rad)
  Solid = false
  Source = -> Face119
  Symmetric = false
FEATURE [Part::Feature] Face120
  shape: bbox 10 x 16.5 x 2e-07 mm, 1 faces, 0 solids (baked)
FEATURE [Part::Feature] Face121
  shape: bbox 10 x 16.5 x 2e-07 mm, 1 faces, 0 solids (baked)
FEATURE [Part::Revolution] Revolve127  label="plugHousing047"
  Angle = 360
  Axis = (0,1,0)
  Base = (0,0,0)
  FaceMakerClass = Part::FaceMakerBullseye
  Placement = pos=(0,0,36.15) rot=(0,0,1;0rad)
  Solid = false
  Source = -> Face121
  Symmetric = false
FEATURE [Part::Feature] Face122
  shape: bbox 10 x 16.5 x 2e-07 mm, 1 faces, 0 solids (baked)
FEATURE [Part::Feature] Face123
  shape: bbox 10 x 16.5 x 2e-07 mm, 1 faces, 0 solids (baked)
FEATURE [Part::Revolution] Revolve128  label="plugHousing048"
  Angle = 360
  Axis = (0,1,0)
  Base = (0,0,0)
  FaceMakerClass = Part::FaceMakerBullseye
  Placement = pos=(0,0,36.15) rot=(0,0,1;0rad)
  Solid = false
  Source = -> Face123
  Symmetric = false
FEATURE [Part::MultiFuse] Fusion100  label="plugHousing054"
  Placement = pos=(0,0,0) rot=(0,0,1;1.5708rad)
  Shapes = -> [Revolve130,Revolve128]
FEATURE [Part::Feature] Face124
  shape: bbox 10 x 16.5 x 2e-07 mm, 1 faces, 0 solids (baked)
FEATURE [Part::Feature] Face125
  shape: bbox 10 x 16.5 x 2e-07 mm, 1 faces, 0 solids (baked)
FEATURE [Part::Revolution] Revolve129  label="plugHousing049"
  Angle = 360
  Axis = (0,1,0)
  Base = (0,0,0)
  FaceMakerClass = Part::FaceMakerBullseye
  Placement = pos=(0,0,36.15) rot=(0,0,1;0rad)
  Solid = false
  Source = -> Face125
  Symmetric = false
FEATURE [Part::Feature] Face126
  shape: bbox 10 x 16.5 x 2e-07 mm, 1 faces, 0 solids (baked)
FEATURE [Part::Revolution] Revolve131  label="plugHousing058"
  Angle = 360
  Axis = (0,1,0)
  Base = (0,0,0)
  FaceMakerClass = Part::FaceMakerBullseye
  Placement = pos=(0,0,36.15) rot=(0,0,1;0rad)
  Solid = false
  Source = -> Face120
  Symmetric = false
FEATURE [Part::MultiFuse] Fusion099  label="plugHousing053"
  Placement = pos=(0,0,0) rot=(0,0,1;1.5708rad)
  Shapes = -> [Revolve127,Revolve131]
FEATURE [Part::MultiFuse] Fusion102  label="plugHousing056"
  Placement = pos=(0,19,0) rot=(0,0,1;3.14159rad)
  Shapes = -> [Fusion100,Fusion099]
FEATURE [Part::Revolution] Revolve132  label="plugHousing059"
  Angle = 360
  Axis = (0,1,0)
  Base = (0,0,0)
  FaceMakerClass = Part::FaceMakerBullseye
  Placement = pos=(0,0,36.15) rot=(0,0,1;0rad)
  Solid = false
  Source = -> Face126
  Symmetric = false
FEATURE [Part::Revolution] Revolve133  label="plugHousing060"
  Angle = 360
  Axis = (0,1,0)
  Base = (0,0,0)
  FaceMakerClass = Part::FaceMakerBullseye
  Placement = pos=(0,0,36.15) rot=(0,0,1;0rad)
  Solid = false
  Source = -> Face122
  Symmetric = false
FEATURE [Part::MultiFuse] Fusion097  label="plugHousing051"
  Placement = pos=(0,0,0) rot=(0,0,1;1.5708rad)
  Shapes = -> [Revolve133,Revolve132]
FEATURE [Part::Revolution] Revolve134  label="plugHousing061"
  Angle = 360
  Axis = (0,1,0)
  Base = (0,0,0)
  FaceMakerClass = Part::FaceMakerBullseye
  Placement = pos=(0,0,36.15) rot=(0,0,1;0rad)
  Solid = false
  Source = -> Face124
  Symmetric = false
FEATURE [Part::MultiFuse] Fusion101  label="plugHousing055"
  Placement = pos=(0,0,0) rot=(0,0,1;1.5708rad)
  Shapes = -> [Revolve129,Revolve134]
FEATURE [Part::MultiFuse] Fusion098  label="plugHousing052"
  Placement = pos=(0,19,0) rot=(0,0,1;3.14159rad)
  Shapes = -> [Fusion097,Fusion101]
FEATURE [Part::MultiFuse] Fusion103  label="plugHousing057"
  Placement = pos=(122.621,0,-0.15) rot=(0,0,1;0rad)
  Shapes = -> [Fusion102,Fusion098]
FEATURE [Part::Box] Box028  label="Cube015"
  AttacherType = Attacher::AttachEngine3D
  Height = 28
  Length = 3
  Placement = pos=(110.7,19,22) rot=(0,0,1;0rad)
  Width = 15.7
FEATURE [Part::Cylinder] Cylinder044
  Angle = 360
  AttacherType = Attacher::AttachEngine3D
  Height = 20
  Placement = pos=(0,0,36.15) rot=(0,0,1;0rad)
  Radius = 10.3
FEATURE [Part::Cylinder] Cylinder045
  Angle = 360
  AttacherType = Attacher::AttachEngine3D
  Height = 10
  Placement = pos=(0,0,36.15) rot=(0,0,1;0rad)
  Radius = 4
FEATURE [Part::MultiFuse] Fusion104  label="removeToCreteHoleForPlugHousing040"
  Placement = pos=(70,19,36) rot=(0,1,0;1.5708rad)
  Shapes = -> [Cylinder044,Cylinder045]
FEATURE [Part::Cut] Cut046  label="plugHousingTab003"
  Base = -> Box028
  Tool = -> Fusion104
FEATURE [Part::MultiFuse] Fusion105  label="plugHousing062"
  Shapes = -> [Fusion103,Cut046]
FEATURE [Part::Fillet] Fillet042
  Base = -> Fusion105
  Edges = 1 edges r=2: [Edge25]
FEATURE [Part::Fillet] Fillet043  label="plugHousing063"
  Base = -> Fillet042
  Edges = 1 edges r=2: [Edge8]
  Placement = pos=(7,0,0) rot=(0,0,1;0rad)
FEATURE [Part::Feature] Face127
  shape: bbox 10 x 16.5 x 2e-07 mm, 1 faces, 0 solids (baked)
FEATURE [Part::Feature] Face128
  shape: bbox 10 x 16.5 x 2e-07 mm, 1 faces, 0 solids (baked)
FEATURE [Part::Revolution] Revolve137  label="plugHousing070"
  Angle = 360
  Axis = (0,1,0)
  Base = (0,0,0)
  FaceMakerClass = Part::FaceMakerBullseye
  Placement = pos=(0,0,36.15) rot=(0,0,1;0rad)
  Solid = false
  Source = -> Face127
  Symmetric = false
FEATURE [Part::Revolution] Revolve140  label="plugHousing073"
  Angle = 360
  Axis = (0,1,0)
  Base = (0,0,0)
  FaceMakerClass = Part::FaceMakerBullseye
  Placement = pos=(0,0,36.15) rot=(0,0,1;0rad)
  Solid = false
  Source = -> Face128
  Symmetric = false
FEATURE [Part::Feature] Face129
  shape: bbox 10 x 16.5 x 2e-07 mm, 1 faces, 0 solids (baked)
FEATURE [Part::Revolution] Revolve138  label="plugHousing071"
  Angle = 360
  Axis = (0,1,0)
  Base = (0,0,0)
  FaceMakerClass = Part::FaceMakerBullseye
  Placement = pos=(0,0,36.15) rot=(0,0,1;0rad)
  Solid = false
  Source = -> Face129
  Symmetric = false
FEATURE [Part::Feature] Face130
  shape: bbox 10 x 16.5 x 2e-07 mm, 1 faces, 0 solids (baked)
FEATURE [Part::Revolution] Revolve139  label="plugHousing072"
  Angle = 360
  Axis = (0,1,0)
  Base = (0,0,0)
  FaceMakerClass = Part::FaceMakerBullseye
  Placement = pos=(0,0,36.15) rot=(0,0,1;0rad)
  Solid = false
  Source = -> Face130
  Symmetric = false
FEATURE [Part::Feature] Face131
  shape: bbox 10 x 16.5 x 2e-07 mm, 1 faces, 0 solids (baked)
FEATURE [Part::Revolution] Revolve135  label="plugHousing068"
  Angle = 360
  Axis = (0,1,0)
  Base = (0,0,0)
  FaceMakerClass = Part::FaceMakerBullseye
  Placement = pos=(0,0,36.15) rot=(0,0,1;0rad)
  Solid = false
  Source = -> Face131
  Symmetric = false
FEATURE [Part::MultiFuse] Fusion112  label="plugHousing078"
  Placement = pos=(0,0,0) rot=(0,0,1;1.5708rad)
  Shapes = -> [Revolve135,Revolve139]
FEATURE [Part::Feature] Face132
  shape: bbox 10 x 16.5 x 2e-07 mm, 1 faces, 0 solids (baked)
FEATURE [Part::Revolution] Revolve141  label="plugHousing074"
  Angle = 360
  Axis = (0,1,0)
  Base = (0,0,0)
  FaceMakerClass = Part::FaceMakerBullseye
  Placement = pos=(0,0,36.15) rot=(0,0,1;0rad)
  Solid = false
  Source = -> Face132
  Symmetric = false
FEATURE [Part::MultiFuse] Fusion110  label="plugHousing076"
  Placement = pos=(0,0,0) rot=(0,0,1;1.5708rad)
  Shapes = -> [Revolve141,Revolve140]
FEATURE [Part::Feature] Face133
  shape: bbox 10 x 16.5 x 2e-07 mm, 1 faces, 0 solids (baked)
FEATURE [Part::Revolution] Revolve136  label="plugHousing069"
  Angle = 360
  Axis = (0,1,0)
  Base = (0,0,0)
  FaceMakerClass = Part::FaceMakerBullseye
  Placement = pos=(0,0,36.15) rot=(0,0,1;0rad)
  Solid = false
  Source = -> Face133
  Symmetric = false
FEATURE [Part::MultiFuse] Fusion106  label="plugHousing064"
  Placement = pos=(0,0,0) rot=(0,0,1;1.5708rad)
  Shapes = -> [Revolve138,Revolve136]
FEATURE [Part::MultiFuse] Fusion108  label="plugHousing066"
  Placement = pos=(0,19,0) rot=(0,0,1;3.14159rad)
  Shapes = -> [Fusion106,Fusion112]
FEATURE [Part::Feature] Face134
  shape: bbox 10 x 16.5 x 2e-07 mm, 1 faces, 0 solids (baked)
FEATURE [Part::Revolution] Revolve142  label="plugHousing075"
  Angle = 360
  Axis = (0,1,0)
  Base = (0,0,0)
  FaceMakerClass = Part::FaceMakerBullseye
  Placement = pos=(0,0,36.15) rot=(0,0,1;0rad)
  Solid = false
  Source = -> Face134
  Symmetric = false
FEATURE [Part::MultiFuse] Fusion107  label="plugHousing065"
  Placement = pos=(0,0,0) rot=(0,0,1;1.5708rad)
  Shapes = -> [Revolve137,Revolve142]
FEATURE [Part::MultiFuse] Fusion111  label="plugHousing077"
  Placement = pos=(0,19,0) rot=(0,0,1;3.14159rad)
  Shapes = -> [Fusion110,Fusion107]
FEATURE [Part::MultiFuse] Fusion109  label="plugHousing067"
  Placement = pos=(131.236,0,-0.15) rot=(0,0,1;0rad)
  Shapes = -> [Fusion108,Fusion111]
FEATURE [Part::MultiFuse] Fusion113  label="plugHousing079"
  Shapes = -> [Fillet043,Fusion109]
FEATURE [Part::Feature] Face135
  shape: bbox 3.5 x 17.8 x 2e-07 mm, 1 faces, 0 solids (baked)
FEATURE [Part::Revolution] Revolve143  label="removeToCreateScrewAndThreadedInsertHole049"
  Angle = 360
  Axis = (0,1,0)
  Base = (0,0,0)
  FaceMakerClass = Part::FaceMakerBullseye
  Placement = pos=(12.5,0,10) rot=(0,0,1;0rad)
  Solid = false
  Source = -> Face135
  Symmetric = false
FEATURE [Part::Feature] Face136
  shape: bbox 3.5 x 17.8 x 2e-07 mm, 1 faces, 0 solids (baked)
FEATURE [Part::Revolution] Revolve144  label="removeToCreateScrewAndThreadedInsertHole050"
  Angle = 360
  Axis = (0,1,0)
  Base = (0,0,0)
  FaceMakerClass = Part::FaceMakerBullseye
  Placement = pos=(12.5,0,62) rot=(0,0,1;0rad)
  Solid = false
  Source = -> Face136
  Symmetric = false
FEATURE [Part::Feature] Face137
  shape: bbox 3.5 x 17.8 x 2e-07 mm, 1 faces, 0 solids (baked)
FEATURE [Part::Revolution] Revolve145  label="removeToCreateScrewAndThreadedInsertHole051"
  Angle = 360
  Axis = (0,1,0)
  Base = (0,0,0)
  FaceMakerClass = Part::FaceMakerBullseye
  Placement = pos=(89.5,0,68.5) rot=(0,0,1;0rad)
  Solid = false
  Source = -> Face137
  Symmetric = false
FEATURE [Part::Feature] Face138
  shape: bbox 3.5 x 17.8 x 2e-07 mm, 1 faces, 0 solids (baked)
FEATURE [Part::Revolution] Revolve146  label="removeToCreateScrewAndThreadedInsertHole052"
  Angle = 360
  Axis = (0,1,0)
  Base = (0,0,0)
  FaceMakerClass = Part::FaceMakerBullseye
  Placement = pos=(89.5,0,3.5) rot=(0,0,1;0rad)
  Solid = false
  Source = -> Face138
  Symmetric = false
FEATURE [Part::Feature] Face139
  shape: bbox 3.5 x 17.8 x 2e-07 mm, 1 faces, 0 solids (baked)
FEATURE [Part::Revolution] Revolve147  label="removeToCreateScrewAndThreadedInsertHole053"
  Angle = 360
  Axis = (0,1,0)
  Base = (0,0,0)
  FaceMakerClass = Part::FaceMakerBullseye
  Placement = pos=(109.5,4.7,3.5) rot=(0,0,1;0rad)
  Solid = false
  Source = -> Face139
  Symmetric = false
FEATURE [Part::Feature] Face140
  shape: bbox 3.5 x 17.8 x 2e-07 mm, 1 faces, 0 solids (baked)
FEATURE [Part::Revolution] Revolve148  label="removeToCreateScrewAndThreadedInsertHole054"
  Angle = 360
  Axis = (0,1,0)
  Base = (0,0,0)
  FaceMakerClass = Part::FaceMakerBullseye
  Placement = pos=(109.5,4.7,68.5) rot=(0,0,1;0rad)
  Solid = false
  Source = -> Face140
  Symmetric = false
FEATURE [Part::MultiFuse] Fusion114  label="removeToCreateScrewAndThreadedInsertHole055"
  Shapes = -> [Revolve148,Revolve147,Revolve146,Revolve145,Revolve144,Revolve143]
FEATURE [Part::Cut] Cut047  label="casePillars004"
  Base = -> Cut037
  Tool = -> Fusion114
FEATURE [Part::Feature] Face141
  shape: bbox 3.5 x 17.8 x 2e-07 mm, 1 faces, 0 solids (baked)
FEATURE [Part::Feature] Face142
  shape: bbox 3.5 x 17.8 x 2e-07 mm, 1 faces, 0 solids (baked)
FEATURE [Part::Feature] Face143
  shape: bbox 3.5 x 17.8 x 2e-07 mm, 1 faces, 0 solids (baked)
FEATURE [Part::Revolution] Revolve149  label="removeToCreateScrewAndThreadedInsertHole057"
  Angle = 360
  Axis = (0,1,0)
  Base = (0,0,0)
  FaceMakerClass = Part::FaceMakerBullseye
  Placement = pos=(12.5,0,10) rot=(0,0,1;0rad)
  Solid = false
  Source = -> Face141
  Symmetric = false
FEATURE [Part::Feature] Face144
  shape: bbox 3.5 x 17.8 x 2e-07 mm, 1 faces, 0 solids (baked)
FEATURE [Part::Feature] Face145
  shape: bbox 3.5 x 17.8 x 2e-07 mm, 1 faces, 0 solids (baked)
FEATURE [Part::Feature] Face146
  shape: bbox 3.5 x 17.8 x 2e-07 mm, 1 faces, 0 solids (baked)
FEATURE [Part::Revolution] Revolve150  label="removeToCreateScrewAndThreadedInsertHole058"
  Angle = 360
  Axis = (0,1,0)
  Base = (0,0,0)
  FaceMakerClass = Part::FaceMakerBullseye
  Placement = pos=(12.5,0,62) rot=(0,0,1;0rad)
  Solid = false
  Source = -> Face146
  Symmetric = false
FEATURE [Part::Revolution] Revolve151  label="removeToCreateScrewAndThreadedInsertHole059"
  Angle = 360
  Axis = (0,1,0)
  Base = (0,0,0)
  FaceMakerClass = Part::FaceMakerBullseye
  Placement = pos=(89.5,0,68.5) rot=(0,0,1;0rad)
  Solid = false
  Source = -> Face143
  Symmetric = false
FEATURE [Part::Revolution] Revolve152  label="removeToCreateScrewAndThreadedInsertHole060"
  Angle = 360
  Axis = (0,1,0)
  Base = (0,0,0)
  FaceMakerClass = Part::FaceMakerBullseye
  Placement = pos=(89.5,0,3.5) rot=(0,0,1;0rad)
  Solid = false
  Source = -> Face142
  Symmetric = false
FEATURE [Part::Revolution] Revolve153  label="removeToCreateScrewAndThreadedInsertHole061"
  Angle = 360
  Axis = (0,1,0)
  Base = (0,0,0)
  FaceMakerClass = Part::FaceMakerBullseye
  Placement = pos=(109.5,4.7,3.5) rot=(0,0,1;0rad)
  Solid = false
  Source = -> Face145
  Symmetric = false
FEATURE [Part::Revolution] Revolve154  label="removeToCreateScrewAndThreadedInsertHole062"
  Angle = 360
  Axis = (0,1,0)
  Base = (0,0,0)
  FaceMakerClass = Part::FaceMakerBullseye
  Placement = pos=(109.5,4.7,68.5) rot=(0,0,1;0rad)
  Solid = false
  Source = -> Face144
  Symmetric = false
FEATURE [Part::MultiFuse] Fusion115  label="removeToCreateScrewAndThreadedInsertHole056"
  Shapes = -> [Revolve154,Revolve153,Revolve152,Revolve151,Revolve150,Revolve149]
FEATURE [Part::Feature] Face147
  shape: bbox 9.8 x 26.5 x 2e-07 mm, 1 faces, 0 solids (baked)
FEATURE [Part::Revolution] Revolve155
  Angle = 360
  Axis = (0,1,0)
  Base = (0,0,0)
  FaceMakerClass = Part::FaceMakerBullseye
  Placement = pos=(0,0,0) rot=(0,0,1;1.5708rad)
  Solid = false
  Source = -> Face147
  Symmetric = false
FEATURE [Part::Feature] Face148
  shape: bbox 9.8 x 26.5 x 2e-07 mm, 1 faces, 0 solids (baked)
FEATURE [Part::Revolution] Revolve156
  Angle = 360
  Axis = (0,1,0)
  Base = (0,0,0)
  FaceMakerClass = Part::FaceMakerBullseye
  Placement = pos=(0,0,0) rot=(0,0,1;1.5708rad)
  Solid = false
  Source = -> Face148
  Symmetric = false
FEATURE [Part::MultiFuse] Fusion116
  Placement = pos=(-18,19,36) rot=(0,0,1;0rad)
  Shapes = -> [Revolve156,Revolve155]
FEATURE [Part::Box] Box029  label="Cube016"
  AttacherType = Attacher::AttachEngine3D
  Height = 28
  Length = 3
  Placement = pos=(110.7,19,22) rot=(0,0,1;0rad)
  Width = 15.7
FEATURE [Part::Cylinder] Cylinder046
  Angle = 360
  AttacherType = Attacher::AttachEngine3D
  Height = 10
  Placement = pos=(0,0,36.15) rot=(0,0,1;0rad)
  Radius = 4
FEATURE [Part::Cylinder] Cylinder047
  Angle = 360
  AttacherType = Attacher::AttachEngine3D
  Height = 20
  Placement = pos=(0,0,36.15) rot=(0,0,1;0rad)
  Radius = 10.3
FEATURE [Part::MultiFuse] Fusion117  label="removeToCreteHoleForPlugHousing041"
  Placement = pos=(70,19,36) rot=(0,1,0;1.5708rad)
  Shapes = -> [Cylinder047,Cylinder046]
FEATURE [Part::Cut] Cut049  label="plugHousingTab004"
  Base = -> Box029
  Placement = pos=(-107.4,-14,0) rot=(0,0,1;0rad)
  Tool = -> Fusion117
FEATURE [Part::Box] Box030  label="Cube017"
  AttacherType = Attacher::AttachEngine3D
  Height = 28
  Length = 3
  Placement = pos=(110.7,19,22) rot=(0,0,1;0rad)
  Width = 15.7
FEATURE [Part::Cylinder] Cylinder048
  Angle = 360
  AttacherType = Attacher::AttachEngine3D
  Height = 10
  Placement = pos=(0,0,36.15) rot=(0,0,1;0rad)
  Radius = 4
FEATURE [Part::Cylinder] Cylinder049
  Angle = 360
  AttacherType = Attacher::AttachEngine3D
  Height = 20
  Placement = pos=(0,0,36.15) rot=(0,0,1;0rad)
  Radius = 10.3
FEATURE [Part::MultiFuse] Fusion118  label="removeToCreteHoleForPlugHousing042"
  Placement = pos=(70,19,36) rot=(0,1,0;1.5708rad)
  Shapes = -> [Cylinder049,Cylinder048]
FEATURE [Part::Cut] Cut050  label="plugHousingTab005"
  Base = -> Box030
  Placement = pos=(-107.4,-14,0) rot=(0,0,1;0rad)
  Tool = -> Fusion118
FEATURE [Part::MultiFuse] Fusion119
  Placement = pos=(9.6,23,0) rot=(0,0,1;3.14159rad)
  Shapes = -> [Cut049,Cut050]
FEATURE [Part::Box] Box031  label="Cube018"
  AttacherType = Attacher::AttachEngine3D
  Height = 10
  Length = 3
  Placement = pos=(3.3,4,12) rot=(0,0,1;0rad)
  Width = 10
FEATURE [Part::Fillet] Fillet044
  Base = -> Box031
  Edges = 1 edges r=2: [Edge11]
FEATURE [Part::Box] Box032  label="Cube019"
  AttacherType = Attacher::AttachEngine3D
  Height = 10
  Length = 3
  Placement = pos=(3.3,4,50) rot=(0,0,1;0rad)
  Width = 10
FEATURE [Part::Fillet] Fillet045
  Base = -> Box032
  Edges = 1 edges r=2: [Edge12]
FEATURE [Part::Box] Box033  label="Cube020"
  AttacherType = Attacher::AttachEngine3D
  Height = 28
  Length = 4
  Placement = pos=(5,0,22) rot=(0,0,1;0rad)
  Width = 10
FEATURE [Part::Fillet] Fillet046
  Base = -> Box033
  Edges = 1 edges r=1: [Edge7]
FEATURE [Part::Fillet] Fillet047
  Base = -> Fillet046
  Edges = 1 edges r=2: [Edge5]
FEATURE [Part::Fillet] Fillet048
  Base = -> Fillet047
  Edges = 1 edges r=2: [Edge2]
FEATURE [Part::Cylinder] Cylinder050
  Angle = 360
  AttacherType = Attacher::AttachEngine3D
  Height = 20
  Placement = pos=(0,0,36.15) rot=(0,0,1;0rad)
  Radius = 8.2
FEATURE [Part::Cylinder] Cylinder051
  Angle = 360
  AttacherType = Attacher::AttachEngine3D
  Height = 10
  Placement = pos=(0,0,36.15) rot=(0,0,1;0rad)
  Radius = 4
FEATURE [Part::MultiFuse] Fusion120  label="removeToCreteHoleForPlugHousing043"
  Placement = pos=(-42,19,36) rot=(0,1,0;1.5708rad)
  Shapes = -> [Cylinder050,Cylinder051]
FEATURE [Sketcher::SketchObject] Sketch067  label="topSketch018"
  FullyConstrained = true
  sketch-geometry (4):
    g0: LineSegment StartX=16.8446 StartY=31.512 StartZ=0 EndX=16.3251 EndY=34.4666 EndZ=0
    g1: ArcOfCircle CenterX=19 CenterY=19.2524 CenterZ=0 NormalX=0 NormalY=0 NormalZ=1 AngleXU=0 Radius=15.4476 StartAngle=1.74483 EndAngle=2.72717
    g2: ArcOfCircle CenterX=19 CenterY=19.2524 CenterZ=0 NormalX=0 NormalY=0 NormalZ=1 AngleXU=0 Radius=12.4476 StartAngle=1.74483 EndAngle=2.73189
    g3: LineSegment StartX=4.86004 StartY=25.4725 StartZ=0 EndX=7.58253 EndY=24.2107 EndZ=0
  constraints (7):
    c: Block(g0)
    c: Coincident(g1,g0)
    c: Coincident(g2,g0)
    c: Coincident(g3,g1)
    c: Coincident(g3,g2)
    c: Block(g1)
    c: Block(g2)
FEATURE [Part::Extrusion] Extrude058
  Base = -> Sketch067
  Dir = (0,0,1)
  DirMode = 2
  FaceMakerClass = Part::FaceMakerBullseye
  LengthFwd = 10
  LengthRev = 0
  Placement = pos=(0,0,31) rot=(0,0,1;0rad)
  Solid = true
  Symmetric = false
FEATURE [Part::Cut] Cut051
  Base = -> Extrude058
  Tool = -> Fusion120
FEATURE [Part::Fillet] Fillet049
  Base = -> Cut051
  Edges = 1 edges r=2: [Edge1]
FEATURE [Part::Fillet] Fillet050
  Base = -> Fillet049
  Edges = 1 edges r=2.5: [Edge1]
FEATURE [Part::Fillet] Fillet051
  Base = -> Fillet050
  Edges = 1 edges r=2.5: [Edge2]
FEATURE [Part::MultiFuse] Fusion121  label="wireHolder003"
  Shapes = -> [Fusion116,Fillet051]
FEATURE [Part::MultiFuse] Fusion122
  Shapes = -> [Fillet045,Fusion121]
FEATURE [Part::MultiFuse] Fusion123  label="wireHolder004"
  Shapes = -> [Fusion122,Fillet048]
FEATURE [Part::MultiFuse] Fusion124  label="wireHolder005"
  Shapes = -> [Fillet044,Fusion119,Fusion123]
FEATURE [Sketcher::SketchObject] Sketch068  label="topSketch019"
  FullyConstrained = true
  sketch-geometry (6):
    g0: LineSegment StartX=19 StartY=38 StartZ=0 EndX=117 EndY=38 EndZ=0
    g1: ArcOfCircle CenterX=19 CenterY=19 CenterZ=0 NormalX=0 NormalY=0 NormalZ=1 AngleXU=0 Radius=19 StartAngle=1.5708 EndAngle=3.14159
    g2: LineSegment StartX=117 StartY=38 StartZ=0 EndX=117 EndY=19 EndZ=0
    g3: LineSegment StartX=98 StartY=1.0161e-12 StartZ=0 EndX=5.22862e-06 EndY=1.0161e-12 EndZ=0
    g4: LineSegment StartX=5.22862e-06 StartY=19 StartZ=0 EndX=5.22862e-06 EndY=1.0161e-12 EndZ=0
    g5: ArcOfCircle CenterX=98 CenterY=19 CenterZ=0 NormalX=0 NormalY=0 NormalZ=1 AngleXU=0 Radius=19 StartAngle=4.71239 EndAngle=6.28319
  constraints (16):
    c: Horizontal(g0)
    c: Distance(g0) = 98
    c: Coincident(g1,g0)
    c: Block(g1)
    c: Coincident(g2,g0)
    c: Vertical(g2)
    c: Distance(g2) = 19
    c: Horizontal(g3)
    c: Coincident(g4,g1)
    c: Vertical(g4)
    c: Coincident(g3,g4)
    c: Block(g3)
    c: Coincident(g5,g2)
    c: Coincident(g5,g3)
    c: Block(g0)
    c: Block(g5)
FEATURE [Part::Extrusion] Extrude059  label="sideA002"
  Base = -> Sketch068
  Dir = (0,0,1)
  DirMode = 2
  FaceMakerClass = Part::FaceMakerBullseye
  LengthFwd = 3
  LengthRev = 0
  Placement = pos=(0,0,-2.7) rot=(0,0,1;0rad)
  Solid = true
  Symmetric = false
FEATURE [Sketcher::SketchObject] Sketch069  label="topSketch020"
  FullyConstrained = true
  sketch-geometry (6):
    g0: LineSegment StartX=19 StartY=38 StartZ=0 EndX=117 EndY=38 EndZ=0
    g1: ArcOfCircle CenterX=19 CenterY=19 CenterZ=0 NormalX=0 NormalY=0 NormalZ=1 AngleXU=0 Radius=19 StartAngle=1.5708 EndAngle=3.14159
    g2: LineSegment StartX=117 StartY=38 StartZ=0 EndX=117 EndY=19 EndZ=0
    g3: LineSegment StartX=98 StartY=1.0161e-12 StartZ=0 EndX=5.22862e-06 EndY=1.0161e-12 EndZ=0
    g4: LineSegment StartX=5.22862e-06 StartY=19 StartZ=0 EndX=5.22862e-06 EndY=1.0161e-12 EndZ=0
    g5: ArcOfCircle CenterX=98 CenterY=19 CenterZ=0 NormalX=0 NormalY=0 NormalZ=1 AngleXU=0 Radius=19 StartAngle=4.71239 EndAngle=6.28319
  constraints (16):
    c: Horizontal(g0)
    c: Distance(g0) = 98
    c: Coincident(g1,g0)
    c: Block(g1)
    c: Coincident(g2,g0)
    c: Vertical(g2)
    c: Distance(g2) = 19
    c: Horizontal(g3)
    c: Coincident(g4,g1)
    c: Vertical(g4)
    c: Coincident(g3,g4)
    c: Block(g3)
    c: Coincident(g5,g2)
    c: Coincident(g5,g3)
    c: Block(g0)
    c: Block(g5)
FEATURE [Part::Extrusion] Extrude060  label="sideB002"
  Base = -> Sketch069
  Dir = (0,0,1)
  DirMode = 2
  FaceMakerClass = Part::FaceMakerBullseye
  LengthFwd = 3
  LengthRev = 0
  Placement = pos=(0,0,71.7) rot=(0,0,1;0rad)
  Solid = true
  Symmetric = false
FEATURE [Part::MultiFuse] Fusion127  label="removeFromBottom001"
  Placement = pos=(2,0,0) rot=(0,0,1;0rad)
  Shapes = -> [Extrude059,Extrude060]
FEATURE [Part::Cylinder] Cylinder052
  Angle = 360
  AttacherType = Attacher::AttachEngine3D
  Height = 20
  Placement = pos=(0,0,36.15) rot=(0,0,1;0rad)
  Radius = 14
FEATURE [Part::Cylinder] Cylinder053
  Angle = 360
  AttacherType = Attacher::AttachEngine3D
  Height = 10
  Placement = pos=(0,0,36.15) rot=(0,0,1;0rad)
  Radius = 4
FEATURE [Part::MultiFuse] Fusion128  label="removeToCreteHoleForPlugHousing044"
  Placement = pos=(70,19,36) rot=(0,1,0;1.5708rad)
  Shapes = -> [Cylinder052,Cylinder053]
FEATURE [Part::Cut] Cut052  label="bottom011"
  Base = -> Extrude043
  Tool = -> Fusion128
FEATURE [Part::Cut] Cut054  label="bottom012"
  Base = -> Cut052
  Tool = -> Fusion115
FEATURE [Sketcher::SketchObject] Sketch070
  FullyConstrained = true
  Placement = pos=(117,19,0) rot=(0.57735,0.57735,0.57735;2.0944rad)
  sketch-geometry (48):
    g0: LineSegment StartX=-49.19 StartY=69.25 StartZ=0 EndX=-49.19 EndY=66.25 EndZ=0
    g1: LineSegment StartX=-49.19 StartY=63.5 StartZ=0 EndX=-49.19 EndY=60.5 EndZ=0
    g2: LineSegment StartX=-49.19 StartY=57.75 StartZ=0 EndX=-49.19 EndY=54.75 EndZ=0
    g3: LineSegment StartX=-49.19 StartY=52 StartZ=0 EndX=-49.19 EndY=49 EndZ=0
    g4: LineSegment StartX=-49.19 StartY=46.25 StartZ=0 EndX=-49.19 EndY=43.25 EndZ=0
    g5: LineSegment StartX=-49.19 StartY=40.5 StartZ=0 EndX=-49.19 EndY=37.5 EndZ=0
    g6: LineSegment StartX=-49.19 StartY=34.5 StartZ=0 EndX=-49.19 EndY=31.5 EndZ=0
    g7: LineSegment StartX=-49.19 StartY=28.75 StartZ=0 EndX=-49.19 EndY=25.75 EndZ=0
    g8: LineSegment StartX=-49.19 StartY=23 StartZ=0 EndX=-49.19 EndY=20 EndZ=0
    g9: LineSegment StartX=-49.19 StartY=17.25 StartZ=0 EndX=-49.19 EndY=14.25 EndZ=0
    g10: LineSegment StartX=-49.19 StartY=11.5 StartZ=0 EndX=-49.19 EndY=8.5 EndZ=0
    g11: LineSegment StartX=-49.19 StartY=5.75 StartZ=0 EndX=-49.19 EndY=2.75 EndZ=0
    g12: ArcOfCircle CenterX=-1.5 CenterY=67.75 CenterZ=0 NormalX=0 NormalY=0 NormalZ=1 AngleXU=0 Radius=1.5 StartAngle=4.71239 EndAngle=7.85398
    g13: ArcOfCircle CenterX=-1.5 CenterY=62 CenterZ=0 NormalX=0 NormalY=0 NormalZ=1 AngleXU=0 Radius=1.5 StartAngle=4.71239 EndAngle=7.85398
    g14: ArcOfCircle CenterX=-1.5 CenterY=56.25 CenterZ=0 NormalX=0 NormalY=0 NormalZ=1 AngleXU=0 Radius=1.5 StartAngle=4.71239 EndAngle=7.85398
    g15: ArcOfCircle CenterX=-11.49 CenterY=50.5 CenterZ=0 NormalX=0 NormalY=0 NormalZ=1 AngleXU=0 Radius=1.5 StartAngle=4.71239 EndAngle=7.85398
    g16: ArcOfCircle CenterX=-16.28 CenterY=44.75 CenterZ=0 NormalX=0 NormalY=0 NormalZ=1 AngleXU=0 Radius=1.5 StartAngle=4.71239 EndAngle=7.85398
    g17: ArcOfCircle CenterX=-18.2337 CenterY=39 CenterZ=0 NormalX=0 NormalY=0 NormalZ=1 AngleXU=0 Radius=1.5 StartAngle=4.71485 EndAngle=7.85398
    g18: ArcOfCircle CenterX=-16.2837 CenterY=27.25 CenterZ=0 NormalX=0 NormalY=0 NormalZ=1 AngleXU=0 Radius=1.5 StartAngle=4.71485 EndAngle=7.85398
    g19: ArcOfCircle CenterX=-18.2337 CenterY=33 CenterZ=0 NormalX=0 NormalY=0 NormalZ=1 AngleXU=0 Radius=1.5 StartAngle=4.71485 EndAngle=7.85398
    g20: ArcOfCircle CenterX=-11.49 CenterY=21.5 CenterZ=0 NormalX=0 NormalY=0 NormalZ=1 AngleXU=0 Radius=1.5 StartAngle=4.71239 EndAngle=7.85398
    g21: ArcOfCircle CenterX=-1.5 CenterY=4.25 CenterZ=0 NormalX=0 NormalY=0 NormalZ=1 AngleXU=0 Radius=1.5 StartAngle=4.71239 EndAngle=7.85398
    g22: ArcOfCircle CenterX=-1.5 CenterY=10 CenterZ=0 NormalX=0 NormalY=0 NormalZ=1 AngleXU=0 Radius=1.5 StartAngle=4.71239 EndAngle=7.85398
    g23: ArcOfCircle CenterX=-1.5 CenterY=15.75 CenterZ=0 NormalX=0 NormalY=0 NormalZ=1 AngleXU=0 Radius=1.5 StartAngle=4.71239 EndAngle=7.85398
    g24: LineSegment StartX=-49.19 StartY=69.25 StartZ=0 EndX=-1.5 EndY=69.25 EndZ=0
    g25: LineSegment StartX=-49.19 StartY=66.25 StartZ=0 EndX=-1.5 EndY=66.25 EndZ=0
    g26: LineSegment StartX=-49.19 StartY=63.5 StartZ=0 EndX=-1.5 EndY=63.5 EndZ=0
    g27: LineSegment StartX=-49.19 StartY=60.5 StartZ=0 EndX=-1.5 EndY=60.5 EndZ=0
    g28: LineSegment StartX=-49.19 StartY=57.75 StartZ=0 EndX=-1.5 EndY=57.75 EndZ=0
    g29: LineSegment StartX=-49.19 StartY=54.75 StartZ=0 EndX=-1.5 EndY=54.75 EndZ=0
    g30: LineSegment StartX=-49.19 StartY=52 StartZ=0 EndX=-11.49 EndY=52 EndZ=0
    g31: LineSegment StartX=-49.19 StartY=49 StartZ=0 EndX=-11.49 EndY=49 EndZ=0
    g32: LineSegment StartX=-49.19 StartY=46.25 StartZ=0 EndX=-16.28 EndY=46.25 EndZ=0
    g33: LineSegment StartX=-49.19 StartY=43.25 StartZ=0 EndX=-16.28 EndY=43.25 EndZ=0
    g34: LineSegment StartX=-49.19 StartY=40.5 StartZ=0 EndX=-18.2337 EndY=40.5 EndZ=0
    g35: LineSegment StartX=-49.19 StartY=37.5 StartZ=0 EndX=-18.23 EndY=37.5 EndZ=0
    g36: LineSegment StartX=-49.19 StartY=34.5 StartZ=0 EndX=-18.2337 EndY=34.5 EndZ=0
    g37: LineSegment StartX=-49.19 StartY=31.5 StartZ=0 EndX=-18.23 EndY=31.5 EndZ=0
    g38: LineSegment StartX=-49.19 StartY=28.75 StartZ=0 EndX=-16.2837 EndY=28.75 EndZ=0
    g39: LineSegment StartX=-49.19 StartY=25.75 StartZ=0 EndX=-16.28 EndY=25.75 EndZ=0
    g40: LineSegment StartX=-49.19 StartY=23 StartZ=0 EndX=-11.49 EndY=23 EndZ=0
    g41: LineSegment StartX=-49.19 StartY=20 StartZ=0 EndX=-11.49 EndY=20 EndZ=0
    g42: LineSegment StartX=-49.19 StartY=17.25 StartZ=0 EndX=-1.5 EndY=17.25 EndZ=0
    g43: LineSegment StartX=-49.19 StartY=14.25 StartZ=0 EndX=-1.5 EndY=14.25 EndZ=0
    g44: LineSegment StartX=-49.19 StartY=11.5 StartZ=0 EndX=-1.5 EndY=11.5 EndZ=0
    g45: LineSegment StartX=-49.19 StartY=8.5 StartZ=0 EndX=-1.5 EndY=8.5 EndZ=0
    g46: LineSegment StartX=-49.19 StartY=5.75 StartZ=0 EndX=-1.5 EndY=5.75 EndZ=0
    g47: LineSegment StartX=-49.19 StartY=2.75 StartZ=0 EndX=-1.5 EndY=2.75 EndZ=0
  constraints (120):
    c: Vertical(g0)
    c: Distance(g0) = 3
    c: Block(g0)
    c: Vertical(g1)
    c: Distance(g1) = 3
    c: Vertical(g2)
    c: Equal(g0,g2) = 3
    c: Block(g2)
    c: Vertical(g3)
    c: Equal(g1,g3) = 3
    c: Vertical(g4)
    c: Equal(g0,g4) = 3
    c: Block(g4)
    c: Vertical(g5)
    c: Equal(g1,g5) = 3
    c: Vertical(g6)
    c: Equal(g0,g6) = 3
    c: Block(g6)
    c: Vertical(g7)
    c: Equal(g1,g7) = 3
    c: Vertical(g8)
    c: Equal(g0,g8) = 3
    c: Block(g8)
    c: Vertical(g9)
    c: Equal(g1,g9) = 3
    c: Vertical(g10)
    c: Equal(g0,g10) = 3
    c: Block(g10)
    c: Vertical(g11)
    c: Equal(g1,g11) = 3
    c: Block(g12)
    c: Block(g13)
    c: Block(g14)
    c: Block(g15)
    c: Block(g16)
    c: Block(g17)
    c: Block(g18)
    c: Block(g19)
    c: Block(g20)
    c: Block(g21)
    c: Block(g22)
    c: Block(g23)
    c: Block(g11)
    c: Block(g9)
    c: Block(g7)
    c: Block(g5)
    c: Block(g3)
    c: Block(g1)
    c: Coincident(g24,g0)
    c: Coincident(g24,g12)
    c: Horizontal(g24)
    c: Coincident(g25,g0)
    c: Coincident(g25,g12)
    c: Horizontal(g25)
    c: Coincident(g26,g1)
    c: Coincident(g26,g13)
    c: Horizontal(g26)
    c: Coincident(g27,g1)
    c: Coincident(g27,g13)
    c: Horizontal(g27)
    c: Coincident(g28,g2)
    c: Coincident(g28,g14)
    c: Horizontal(g28)
    c: Coincident(g29,g2)
    c: Coincident(g29,g14)
    c: Horizontal(g29)
    c: Coincident(g30,g3)
    c: Coincident(g30,g15)
    c: Horizontal(g30)
    c: Coincident(g31,g3)
    c: Coincident(g31,g15)
    c: Horizontal(g31)
    c: Coincident(g32,g4)
    c: Coincident(g32,g16)
    c: Horizontal(g32)
    c: Coincident(g33,g4)
    c: Coincident(g33,g16)
    c: Horizontal(g33)
    c: Coincident(g34,g5)
    c: Coincident(g34,g17)
    c: Horizontal(g34)
    c: Coincident(g35,g5)
    c: Coincident(g35,g17)
    c: Horizontal(g35)
    c: Coincident(g36,g6)
    c: Coincident(g36,g19)
    c: Horizontal(g36)
    c: Coincident(g37,g6)
    c: Coincident(g37,g19)
    c: Horizontal(g37)
    c: Coincident(g38,g7)
    c: Coincident(g38,g18)
    c: Horizontal(g38)
    c: Coincident(g39,g7)
    c: Coincident(g39,g18)
    c: Horizontal(g39)
    c: Coincident(g40,g8)
    c: Coincident(g40,g20)
    c: Horizontal(g40)
    c: Coincident(g41,g8)
    c: Coincident(g41,g20)
    c: Horizontal(g41)
    c: Coincident(g42,g9)
    c: Coincident(g42,g23)
    c: Horizontal(g42)
    c: Coincident(g43,g9)
    c: Coincident(g43,g23)
    c: Horizontal(g43)
    c: Coincident(g44,g10)
    c: Coincident(g44,g22)
    c: Horizontal(g44)
    c: Coincident(g45,g10)
    c: Coincident(g45,g22)
    c: Horizontal(g45)
    c: Coincident(g46,g11)
    c: Coincident(g46,g21)
    c: Horizontal(g46)
    c: Coincident(g47,g11)
    c: Coincident(g47,g21)
    c: Horizontal(g47)
FEATURE [Part::Extrusion] Extrude061
  Base = -> Sketch070
  Dir = (1,0,0)
  DirMode = 2
  FaceMakerClass = Part::FaceMakerBullseye
  LengthFwd = 23
  LengthRev = 0
  Placement = pos=(-19,0,0) rot=(0,0,1;0rad)
  Solid = true
  Symmetric = false
FEATURE [Part::Fillet] Fillet052  label="removeToCreateVentalationHoles002"
  Base = -> Extrude061
  Edges = <same value as first occurrence — deduplicated (x6 in doc)>
  Placement = pos=(7,0.02,0) rot=(0,0,1;0rad)
FEATURE [Part::MultiFuse] Fusion130  label="bottom013"
  Shapes = -> [Cut054,Cut034]
FEATURE [Part::Cut] Cut055
  Base = -> Fusion130
  Tool = -> Fillet052
FEATURE [Part::Cylinder] Cylinder054
  Angle = 360
  AttacherType = Attacher::AttachEngine3D
  Height = 20
  Placement = pos=(0,0,36.15) rot=(0,0,1;0rad)
  Radius = 4
FEATURE [Sketcher::SketchObject] Sketch071  label="bottomSketch002"
  FullyConstrained = true
  sketch-geometry (32):
    g0: LineSegment StartX=3.3 StartY=-6.03275e-07 StartZ=0 EndX=98 EndY=-6.03275e-07 EndZ=0
    g1: ArcOfCircle CenterX=98 CenterY=19 CenterZ=0 NormalX=0 NormalY=0 NormalZ=1 AngleXU=0 Radius=19 StartAngle=4.71239 EndAngle=5.71103
    g2: LineSegment StartX=6.3 StartY=8 StartZ=0 EndX=3.3 EndY=8 EndZ=0
    g3: LineSegment StartX=3.3 StartY=8 StartZ=0 EndX=3.3 EndY=-6.03275e-07 EndZ=0
    g4: ArcOfCircle CenterX=8.3 CenterY=5 CenterZ=0 NormalX=0 NormalY=0 NormalZ=1 AngleXU=0 Radius=2 StartAngle=3.14159 EndAngle=4.71239
    g5: LineSegment StartX=6.3 StartY=8 StartZ=0 EndX=6.3 EndY=5 EndZ=0
    g6: ArcOfCircle CenterX=98 CenterY=19 CenterZ=0 NormalX=0 NormalY=0 NormalZ=1 AngleXU=0 Radius=12.7 StartAngle=4.71239 EndAngle=6.28319
    g7: LineSegment StartX=94.7 StartY=3 StartZ=0 EndX=8.3 EndY=3 EndZ=0
    g8-g12: Circle x5 (B-spline internal-alignment scaffolding for g13; pole/knot coordinates omitted)
    g13: BSplineCurve PolesCount=5 KnotsCount=3 Degree=3 IsPeriodic=0
    g14: GeomPoint X=98 Y=6.3 Z=0
    g15: GeomPoint X=96.3938 Y=4.71946 Z=0
    g16: GeomPoint X=94.7 Y=3 Z=0
    g17-g23: Circle x7 (B-spline internal-alignment scaffolding for g24; pole/knot coordinates omitted)
    g24: BSplineCurve PolesCount=7 KnotsCount=5 Degree=3 IsPeriodic=0
    g25-g29: GeomPoint x5 (B-spline internal-alignment scaffolding for g24; pole/knot coordinates omitted)
    g30: ArcOfCircle CenterX=98 CenterY=19 CenterZ=0 NormalX=0 NormalY=0 NormalZ=1 AngleXU=0 Radius=15.7 StartAngle=5.81226 EndAngle=6.28319
    g31: LineSegment StartX=110.7 StartY=19 StartZ=0 EndX=113.7 EndY=19 EndZ=0
  constraints (41):
    c: Horizontal(g0)
    c: Coincident(g1,g0)
    c: Block(g1)
    c: Horizontal(g2)
    c: Distance(g2) = 3
    c: Coincident(g3,g2)
    c: Vertical(g3)
    c: Coincident(g3,g0)
    c: Block(g4)
    c: Block(g2)
    c: Coincident(g5,g2)
    c: Coincident(g5,g4)
    c: Vertical(g5)
    c: Coincident(g6,g1)
    c: Block(g6)
    c: Coincident(g7,g4)
    c: Horizontal(g7)
    c: Block(g0)
    c: Block(g7)
    c: Block(g3)
    c: Coincident(g13,g6)
    c: Weight(g8) = 1
    c: Equal(g8, g9-g12) x4
    c: Coincident(g13,g7)
    c: InternalAlignment(g8-g12 -> g13) x5
    c: InternalAlignment(g14,g13)
    c: InternalAlignment(g15,g13)
    c: InternalAlignment(g16,g13)
    c: Block(g13)
    c: Weight(g17) = 1
    c: Equal(g17, g18-g23) x6
    c: Coincident(g24,g1)
    c: InternalAlignment(g17-g23 -> g24) x7
    c: InternalAlignment(g25-g29 -> g24) x5
    c: Block(g24)
    c: Coincident(g30,g24)
    c: Coincident(g31,g6)
    c: Coincident(g31,g30)
    c: Horizontal(g31)
    c: Block(g31)
    c: Block(g30)
FEATURE [Part::Extrusion] Extrude062  label="bottom014"
  Base = -> Sketch071
  Dir = (0,0,1)
  DirMode = 2
  FaceMakerClass = Part::FaceMakerBullseye
  LengthFwd = 71.4
  LengthRev = 0
  Placement = pos=(0,0,0.3) rot=(0,0,1;0rad)
  Solid = true
  Symmetric = false
FEATURE [Part::Fillet] Fillet054
  Base = -> Extrude062
  Edges = 1 edges r=2.4: [Edge17]
FEATURE [Part::Fillet] Fillet055  label="bottom015"
  Base = -> Fillet054
  Edges = 1 edges r=2.4: [Edge36]
FEATURE [Part::Cylinder] Cylinder055
  Angle = 360
  AttacherType = Attacher::AttachEngine3D
  Height = 10
  Placement = pos=(0,0,36.15) rot=(0,0,1;0rad)
  Radius = 4
FEATURE [Part::MultiFuse] Fusion131  label="removeToCreateHoleForPlugHousing002"
  Placement = pos=(70,19,36.15) rot=(0,1,0;1.5708rad)
  Shapes = -> [Cylinder054,Cylinder055]
FEATURE [Part::Cut] Cut056  label="Bottom001"
  Base = -> Fillet055
  Placement = pos=(9,0,0) rot=(0,0,1;0rad)
  Tool = -> Fusion131
FEATURE [Part::Cut] Cut057
  Base = -> Cut055
  Tool = -> Cut056
FEATURE [Sketcher::SketchObject] Sketch072  label="topSketch021"
  FullyConstrained = true
  sketch-geometry (4):
    g0: ArcOfCircle CenterX=105 CenterY=19 CenterZ=0 NormalX=0 NormalY=0 NormalZ=1 AngleXU=0 Radius=20.6155 StartAngle=5.54125 EndAngle=6.28319
    g1: ArcOfCircle CenterX=105 CenterY=19 CenterZ=0 NormalX=0 NormalY=0 NormalZ=1 AngleXU=0 Radius=13 StartAngle=5.54125 EndAngle=6.28319
    g2: LineSegment StartX=118 StartY=19 StartZ=0 EndX=125.616 EndY=19 EndZ=0
    g3: LineSegment StartX=114.583 StartY=10.2157 StartZ=0 EndX=120.197 EndY=5.06982 EndZ=0
  constraints (7):
    c: Block(g0)
    c: Block(g1)
    c: Coincident(g2,g1)
    c: Coincident(g2,g0)
    c: Horizontal(g2)
    c: Coincident(g3,g1)
    c: Coincident(g3,g0)
FEATURE [Part::Extrusion] Extrude063  label="bottomPlugHousingBit003"
  Base = -> Sketch072
  Dir = (0,0,1)
  DirMode = 2
  FaceMakerClass = Part::FaceMakerBullseye
  LengthFwd = 72
  LengthRev = 0
  Solid = true
  Symmetric = false
FEATURE [Part::Cylinder] Cylinder056
  Angle = 360
  AttacherType = Attacher::AttachEngine3D
  Height = 20
  Placement = pos=(0,0,36.15) rot=(0,0,1;0rad)
  Radius = 14.3
FEATURE [Part::Cylinder] Cylinder057
  Angle = 360
  AttacherType = Attacher::AttachEngine3D
  Height = 10
  Placement = pos=(0,0,36.15) rot=(0,0,1;0rad)
  Radius = 4
FEATURE [Part::Box] Box034  label="removeToCreteHoleForPlugHousing047"
  AttacherType = Attacher::AttachEngine3D
  Height = 28.6
  Length = 20
  Placement = pos=(106.15,0,21.7) rot=(0,0,1;0rad)
  Width = 19
FEATURE [Part::Cylinder] Cylinder058
  Angle = 360
  AttacherType = Attacher::AttachEngine3D
  Height = 20
  Placement = pos=(0,0,36.15) rot=(0,0,1;0rad)
  Radius = 14.3
FEATURE [Part::Cylinder] Cylinder059
  Angle = 360
  AttacherType = Attacher::AttachEngine3D
  Height = 10
  Placement = pos=(0,0,36.15) rot=(0,0,1;0rad)
  Radius = 4
FEATURE [Part::MultiFuse] Fusion134  label="removeToCreteHoleForPlugHousing046"
  Placement = pos=(70,19,36) rot=(0,1,0;1.5708rad)
  Shapes = -> [Cylinder058,Cylinder059]
FEATURE [Part::Cylinder] Cylinder060
  Angle = 360
  AttacherType = Attacher::AttachEngine3D
  Height = 20
  Placement = pos=(0,0,36.15) rot=(0,0,1;0rad)
  Radius = 14
FEATURE [Part::Cylinder] Cylinder061
  Angle = 360
  AttacherType = Attacher::AttachEngine3D
  Height = 10
  Placement = pos=(0,0,36.15) rot=(0,0,1;0rad)
  Radius = 4
FEATURE [Part::MultiFuse] Fusion135  label="removeToCreteHoleForPlugHousing048"
  Placement = pos=(70,19,36) rot=(0,1,0;1.5708rad)
  Shapes = -> [Cylinder060,Cylinder061]
FEATURE [Part::Box] Box035  label="removeToCreteHoleForPlugHousing049"
  AttacherType = Attacher::AttachEngine3D
  Height = 28.6
  Length = 20
  Placement = pos=(106.15,0,21.7) rot=(0,0,1;0rad)
  Width = 19
FEATURE [Part::MultiFuse] Fusion133  label="removeToCreteHoleForPlugHousing045"
  Placement = pos=(0,0,-28.3) rot=(0,0,1;0rad)
  Shapes = -> [Box035,Fusion134]
FEATURE [Part::MultiFuse] Fusion138  label="removeToCreteHoleForPlugHousing051"
  Placement = pos=(70,19,36) rot=(0,1,0;1.5708rad)
  Shapes = -> [Cylinder056,Cylinder057]
FEATURE [Part::MultiFuse] Fusion137  label="removeToCreteHoleForPlugHousing050"
  Placement = pos=(0,0,28.3) rot=(0,0,1;0rad)
  Shapes = -> [Box034,Fusion138]
FEATURE [Part::MultiFuse] Fusion132  label="removeToCreatePlugHousingBottomBit002"
  Shapes = -> [Fusion133,Fusion137]
FEATURE [Part::MultiFuse] Fusion136  label="removeToCreatePlugHousingBottomBit003"
  Shapes = -> [Fusion135,Fusion132]
FEATURE [Part::Cut] Cut058  label="bottomPlugHousingBit002"
  Base = -> Extrude063
  Placement = pos=(-0.09,0,0) rot=(0,0,1;0rad)
  Tool = -> Fusion136
FEATURE [Sketcher::SketchObject] Sketch073  label="bottomSketch003"
  FullyConstrained = true
  sketch-geometry (45):
    g0: LineSegment StartX=6.29999 StartY=8 StartZ=0 EndX=3.29999 EndY=8 EndZ=0
    g1: LineSegment StartX=3.29999 StartY=8 StartZ=0 EndX=3.29999 EndY=-6.03275e-07 EndZ=0
    g2: ArcOfCircle CenterX=8.29999 CenterY=5 CenterZ=0 NormalX=0 NormalY=0 NormalZ=1 AngleXU=0 Radius=2 StartAngle=3.14159 EndAngle=4.71239
    g3: LineSegment StartX=6.29999 StartY=8 StartZ=0 EndX=6.29999 EndY=5 EndZ=0
    g4: ArcOfCircle CenterX=105 CenterY=19 CenterZ=0 NormalX=0 NormalY=0 NormalZ=1 AngleXU=0 Radius=12.7 StartAngle=4.71239 EndAngle=5.94289
    g5-g11: Circle x7 (B-spline internal-alignment scaffolding for g12; pole/knot coordinates omitted)
    g12: BSplineCurve PolesCount=7 KnotsCount=5 Degree=3 IsPeriodic=0
    g13-g17: GeomPoint x5 (B-spline internal-alignment scaffolding for g12; pole/knot coordinates omitted)
    g18: ArcOfCircle CenterX=105 CenterY=19 CenterZ=0 NormalX=0 NormalY=0 NormalZ=1 AngleXU=0 Radius=15.7 StartAngle=5.81226 EndAngle=6.28319
    g19: BSplineCurve PolesCount=5 KnotsCount=3 Degree=3 IsPeriodic=0
    g20: LineSegment StartX=8.29999 StartY=3 StartZ=0 EndX=101.7 EndY=3 EndZ=0
    g21: LineSegment StartX=3.29999 StartY=-6.03275e-07 StartZ=0 EndX=105 EndY=-6.03275e-07 EndZ=0
    g22: LineSegment StartX=120.974 StartY=8.71251 StartZ=0 EndX=122.332 EndY=7.83778 EndZ=0
    g23: LineSegment StartX=105 StartY=-6.03274e-07 StartZ=0 EndX=113 EndY=-6.03274e-07 EndZ=0
    g24: ArcOfCircle CenterX=105 CenterY=19 CenterZ=0 NormalX=0 NormalY=0 NormalZ=1 AngleXU=0 Radius=20.6155 StartAngle=5.11091 EndAngle=5.71103
    g25: ArcOfCircle CenterX=117.7 CenterY=19 CenterZ=0 NormalX=0 NormalY=0 NormalZ=1 AngleXU=0 Radius=3 StartAngle=1.2e-15 EndAngle=2.10468
    g26: Circle CenterX=116.345 CenterY=16.3232 CenterZ=0 NormalX=0 NormalY=0 NormalZ=1 AngleXU=0 Radius=1
    g27: Circle CenterX=117.24 CenterY=15.7584 CenterZ=0 NormalX=0 NormalY=0 NormalZ=1 AngleXU=0 Radius=1
    g28: Circle CenterX=116.972 CenterY=14.7612 CenterZ=0 NormalX=0 NormalY=0 NormalZ=1 AngleXU=0 Radius=1
    g29: BSplineCurve PolesCount=3 KnotsCount=2 Degree=2 IsPeriodic=0
    g30: GeomPoint X=116.345 Y=16.3232 Z=0
    g31: GeomPoint X=116.972 Y=14.7612 Z=0
    g32: Circle CenterX=115.828 CenterY=17.157 CenterZ=0 NormalX=0 NormalY=0 NormalZ=1 AngleXU=0 Radius=1
    g33: Circle CenterX=115.841 CenterY=16.639 CenterZ=0 NormalX=0 NormalY=0 NormalZ=1 AngleXU=0 Radius=1
    g34: Circle CenterX=116.345 CenterY=16.3232 CenterZ=0 NormalX=0 NormalY=0 NormalZ=1 AngleXU=0 Radius=1
    g35: BSplineCurve PolesCount=3 KnotsCount=2 Degree=2 IsPeriodic=0
    g36: GeomPoint X=115.828 Y=17.157 Z=0
    g37: GeomPoint X=116.345 Y=16.3232 Z=0
    g38: LineSegment StartX=115.828 StartY=17.157 StartZ=0 EndX=115.828 EndY=20.8307 EndZ=0
    g39: Circle CenterX=115.828 CenterY=20.8307 CenterZ=0 NormalX=0 NormalY=0 NormalZ=1 AngleXU=0 Radius=1
    g40: Circle CenterX=115.831 CenterY=21.3396 CenterZ=0 NormalX=0 NormalY=0 NormalZ=1 AngleXU=0 Radius=1
    g41: Circle CenterX=116.173 CenterY=21.5825 CenterZ=0 NormalX=0 NormalY=0 NormalZ=1 AngleXU=0 Radius=1
    g42: BSplineCurve PolesCount=3 KnotsCount=2 Degree=2 IsPeriodic=0
    g43: GeomPoint X=115.828 Y=20.8307 Z=0
    g44: GeomPoint X=116.173 Y=21.5825 Z=0
  constraints (70):
    c: Horizontal(g0)
    c: Distance(g0) = 3
    c: Coincident(g1,g0)
    c: Vertical(g1)
    c: Block(g2)
    c: Block(g0)
    c: Coincident(g3,g0)
    c: Coincident(g3,g2)
    c: Vertical(g3)
    c: Block(g1)
    c: Block(g4)
    c: Coincident(g19,g4)
    c: Block(g19)
    c: Equal(g5, g6-g11) x6
    c: InternalAlignment(g5-g11 -> g12) x7
    c: InternalAlignment(g13-g17 -> g12) x5
    c: Block(g12)
    c: Coincident(g18,g12)
    c: Block(g18)
    c: Coincident(g20,g2)
    c: Coincident(g20,g19)
    c: Horizontal(g20)
    c: Distance(g20) = 93.4
    c: Coincident(g21,g1)
    c: Horizontal(g21)
    c: Distance(g21) = 101.7
    c: Horizontal(g23)
    c: Distance(g23) = 8
    c: Coincident(g24,g23)
    c: Block(g23)
    c: Coincident(g22,g24)
    c: Block(g24)
    c: Block(g22)
    c: Distance(g22) = 1.61553
    c: Coincident(g25,g18)
    c: Block(g25)
    c: Weight(g26) = 1
    c: Equal(g26,g27)
    c: Equal(g26,g28)
    c: Coincident(g29,g4)
    c: InternalAlignment(g26,g29)
    c: InternalAlignment(g27,g29)
    c: InternalAlignment(g28,g29)
    c: InternalAlignment(g30,g29)
    c: InternalAlignment(g31,g29)
    c: Block(g29)
    c: Weight(g32) = 1
    c: Equal(g32,g33)
    c: Equal(g32,g34)
    c: Coincident(g35,g29)
    c: InternalAlignment(g32,g35)
    c: InternalAlignment(g33,g35)
    c: InternalAlignment(g34,g35)
    c: InternalAlignment(g36,g35)
    c: InternalAlignment(g37,g35)
    c: Block(g35)
    c: Coincident(g38,g35)
    c: Vertical(g38)
    c: Block(g38)
    c: Coincident(g42,g38)
    c: Weight(g39) = 1
    c: Equal(g39,g40)
    c: Equal(g39,g41)
    c: Coincident(g42,g25)
    c: InternalAlignment(g39,g42)
    c: InternalAlignment(g40,g42)
    c: InternalAlignment(g41,g42)
    c: InternalAlignment(g43,g42)
    c: InternalAlignment(g44,g42)
    c: Block(g42)
FEATURE [Part::Extrusion] Extrude064  label="bottom016"
  Base = -> Sketch073
  Dir = (0,0,1)
  DirMode = 2
  FaceMakerClass = Part::FaceMakerBullseye
  LengthFwd = 71.4
  LengthRev = 0
  Placement = pos=(0,0,0.3) rot=(0,0,1;0rad)
  Solid = true
  Symmetric = false
FEATURE [Part::Revolution] Revolve157  label="removeToCreateScrewAndThreadedInsertHole063"
  Angle = 360
  Axis = (0,1,0)
  Base = (0,0,0)
  FaceMakerClass = Part::FaceMakerBullseye
  Placement = pos=(12.5,0,10) rot=(0,0,1;0rad)
  Solid = false
  Source = -> Face141
  Symmetric = false
FEATURE [Sketcher::SketchObject] Sketch074
  FullyConstrained = true
  Placement = pos=(117,19,0) rot=(0.57735,0.57735,0.57735;2.0944rad)
  sketch-geometry (48):
    g0: LineSegment StartX=-49.19 StartY=69.25 StartZ=0 EndX=-49.19 EndY=66.25 EndZ=0
    g1: LineSegment StartX=-49.19 StartY=63.5 StartZ=0 EndX=-49.19 EndY=60.5 EndZ=0
    g2: LineSegment StartX=-49.19 StartY=57.75 StartZ=0 EndX=-49.19 EndY=54.75 EndZ=0
    g3: LineSegment StartX=-49.19 StartY=52 StartZ=0 EndX=-49.19 EndY=49 EndZ=0
    g4: LineSegment StartX=-49.19 StartY=46.25 StartZ=0 EndX=-49.19 EndY=43.25 EndZ=0
    g5: LineSegment StartX=-49.19 StartY=40.5 StartZ=0 EndX=-49.19 EndY=37.5 EndZ=0
    g6: LineSegment StartX=-49.19 StartY=34.5 StartZ=0 EndX=-49.19 EndY=31.5 EndZ=0
    g7: LineSegment StartX=-49.19 StartY=28.75 StartZ=0 EndX=-49.19 EndY=25.75 EndZ=0
    g8: LineSegment StartX=-49.19 StartY=23 StartZ=0 EndX=-49.19 EndY=20 EndZ=0
    g9: LineSegment StartX=-49.19 StartY=17.25 StartZ=0 EndX=-49.19 EndY=14.25 EndZ=0
    g10: LineSegment StartX=-49.19 StartY=11.5 StartZ=0 EndX=-49.19 EndY=8.5 EndZ=0
    g11: LineSegment StartX=-49.19 StartY=5.75 StartZ=0 EndX=-49.19 EndY=2.75 EndZ=0
    g12: ArcOfCircle CenterX=-1.5 CenterY=67.75 CenterZ=0 NormalX=0 NormalY=0 NormalZ=1 AngleXU=0 Radius=1.5 StartAngle=4.71239 EndAngle=7.85398
    g13: ArcOfCircle CenterX=-1.5 CenterY=62 CenterZ=0 NormalX=0 NormalY=0 NormalZ=1 AngleXU=0 Radius=1.5 StartAngle=4.71239 EndAngle=7.85398
    g14: ArcOfCircle CenterX=-1.5 CenterY=56.25 CenterZ=0 NormalX=0 NormalY=0 NormalZ=1 AngleXU=0 Radius=1.5 StartAngle=4.71239 EndAngle=7.85398
    g15: ArcOfCircle CenterX=-11.49 CenterY=50.5 CenterZ=0 NormalX=0 NormalY=0 NormalZ=1 AngleXU=0 Radius=1.5 StartAngle=4.71239 EndAngle=7.85398
    g16: ArcOfCircle CenterX=-16.28 CenterY=44.75 CenterZ=0 NormalX=0 NormalY=0 NormalZ=1 AngleXU=0 Radius=1.5 StartAngle=4.71239 EndAngle=7.85398
    g17: ArcOfCircle CenterX=-18.2337 CenterY=39 CenterZ=0 NormalX=0 NormalY=0 NormalZ=1 AngleXU=0 Radius=1.5 StartAngle=4.71485 EndAngle=7.85398
    g18: ArcOfCircle CenterX=-16.2837 CenterY=27.25 CenterZ=0 NormalX=0 NormalY=0 NormalZ=1 AngleXU=0 Radius=1.5 StartAngle=4.71485 EndAngle=7.85398
    g19: ArcOfCircle CenterX=-18.2337 CenterY=33 CenterZ=0 NormalX=0 NormalY=0 NormalZ=1 AngleXU=0 Radius=1.5 StartAngle=4.71485 EndAngle=7.85398
    g20: ArcOfCircle CenterX=-11.49 CenterY=21.5 CenterZ=0 NormalX=0 NormalY=0 NormalZ=1 AngleXU=0 Radius=1.5 StartAngle=4.71239 EndAngle=7.85398
    g21: ArcOfCircle CenterX=-1.5 CenterY=4.25 CenterZ=0 NormalX=0 NormalY=0 NormalZ=1 AngleXU=0 Radius=1.5 StartAngle=4.71239 EndAngle=7.85398
    g22: ArcOfCircle CenterX=-1.5 CenterY=10 CenterZ=0 NormalX=0 NormalY=0 NormalZ=1 AngleXU=0 Radius=1.5 StartAngle=4.71239 EndAngle=7.85398
    g23: ArcOfCircle CenterX=-1.5 CenterY=15.75 CenterZ=0 NormalX=0 NormalY=0 NormalZ=1 AngleXU=0 Radius=1.5 StartAngle=4.71239 EndAngle=7.85398
    g24: LineSegment StartX=-49.19 StartY=69.25 StartZ=0 EndX=-1.5 EndY=69.25 EndZ=0
    g25: LineSegment StartX=-49.19 StartY=66.25 StartZ=0 EndX=-1.5 EndY=66.25 EndZ=0
    g26: LineSegment StartX=-49.19 StartY=63.5 StartZ=0 EndX=-1.5 EndY=63.5 EndZ=0
    g27: LineSegment StartX=-49.19 StartY=60.5 StartZ=0 EndX=-1.5 EndY=60.5 EndZ=0
    g28: LineSegment StartX=-49.19 StartY=57.75 StartZ=0 EndX=-1.5 EndY=57.75 EndZ=0
    g29: LineSegment StartX=-49.19 StartY=54.75 StartZ=0 EndX=-1.5 EndY=54.75 EndZ=0
    g30: LineSegment StartX=-49.19 StartY=52 StartZ=0 EndX=-11.49 EndY=52 EndZ=0
    g31: LineSegment StartX=-49.19 StartY=49 StartZ=0 EndX=-11.49 EndY=49 EndZ=0
    g32: LineSegment StartX=-49.19 StartY=46.25 StartZ=0 EndX=-16.28 EndY=46.25 EndZ=0
    g33: LineSegment StartX=-49.19 StartY=43.25 StartZ=0 EndX=-16.28 EndY=43.25 EndZ=0
    g34: LineSegment StartX=-49.19 StartY=40.5 StartZ=0 EndX=-18.2337 EndY=40.5 EndZ=0
    g35: LineSegment StartX=-49.19 StartY=37.5 StartZ=0 EndX=-18.23 EndY=37.5 EndZ=0
    g36: LineSegment StartX=-49.19 StartY=34.5 StartZ=0 EndX=-18.2337 EndY=34.5 EndZ=0
    g37: LineSegment StartX=-49.19 StartY=31.5 StartZ=0 EndX=-18.23 EndY=31.5 EndZ=0
    g38: LineSegment StartX=-49.19 StartY=28.75 StartZ=0 EndX=-16.2837 EndY=28.75 EndZ=0
    g39: LineSegment StartX=-49.19 StartY=25.75 StartZ=0 EndX=-16.28 EndY=25.75 EndZ=0
    g40: LineSegment StartX=-49.19 StartY=23 StartZ=0 EndX=-11.49 EndY=23 EndZ=0
    g41: LineSegment StartX=-49.19 StartY=20 StartZ=0 EndX=-11.49 EndY=20 EndZ=0
    g42: LineSegment StartX=-49.19 StartY=17.25 StartZ=0 EndX=-1.5 EndY=17.25 EndZ=0
    g43: LineSegment StartX=-49.19 StartY=14.25 StartZ=0 EndX=-1.5 EndY=14.25 EndZ=0
    g44: LineSegment StartX=-49.19 StartY=11.5 StartZ=0 EndX=-1.5 EndY=11.5 EndZ=0
    g45: LineSegment StartX=-49.19 StartY=8.5 StartZ=0 EndX=-1.5 EndY=8.5 EndZ=0
    g46: LineSegment StartX=-49.19 StartY=5.75 StartZ=0 EndX=-1.5 EndY=5.75 EndZ=0
    g47: LineSegment StartX=-49.19 StartY=2.75 StartZ=0 EndX=-1.5 EndY=2.75 EndZ=0
  constraints (120):
    c: Vertical(g0)
    c: Distance(g0) = 3
    c: Block(g0)
    c: Vertical(g1)
    c: Distance(g1) = 3
    c: Vertical(g2)
    c: Equal(g0,g2) = 3
    c: Block(g2)
    c: Vertical(g3)
    c: Equal(g1,g3) = 3
    c: Vertical(g4)
    c: Equal(g0,g4) = 3
    c: Block(g4)
    c: Vertical(g5)
    c: Equal(g1,g5) = 3
    c: Vertical(g6)
    c: Equal(g0,g6) = 3
    c: Block(g6)
    c: Vertical(g7)
    c: Equal(g1,g7) = 3
    c: Vertical(g8)
    c: Equal(g0,g8) = 3
    c: Block(g8)
    c: Vertical(g9)
    c: Equal(g1,g9) = 3
    c: Vertical(g10)
    c: Equal(g0,g10) = 3
    c: Block(g10)
    c: Vertical(g11)
    c: Equal(g1,g11) = 3
    c: Block(g12)
    c: Block(g13)
    c: Block(g14)
    c: Block(g15)
    c: Block(g16)
    c: Block(g17)
    c: Block(g18)
    c: Block(g19)
    c: Block(g20)
    c: Block(g21)
    c: Block(g22)
    c: Block(g23)
    c: Block(g11)
    c: Block(g9)
    c: Block(g7)
    c: Block(g5)
    c: Block(g3)
    c: Block(g1)
    c: Coincident(g24,g0)
    c: Coincident(g24,g12)
    c: Horizontal(g24)
    c: Coincident(g25,g0)
    c: Coincident(g25,g12)
    c: Horizontal(g25)
    c: Coincident(g26,g1)
    c: Coincident(g26,g13)
    c: Horizontal(g26)
    c: Coincident(g27,g1)
    c: Coincident(g27,g13)
    c: Horizontal(g27)
    c: Coincident(g28,g2)
    c: Coincident(g28,g14)
    c: Horizontal(g28)
    c: Coincident(g29,g2)
    c: Coincident(g29,g14)
    c: Horizontal(g29)
    c: Coincident(g30,g3)
    c: Coincident(g30,g15)
    c: Horizontal(g30)
    c: Coincident(g31,g3)
    c: Coincident(g31,g15)
    c: Horizontal(g31)
    c: Coincident(g32,g4)
    c: Coincident(g32,g16)
    c: Horizontal(g32)
    c: Coincident(g33,g4)
    c: Coincident(g33,g16)
    c: Horizontal(g33)
    c: Coincident(g34,g5)
    c: Coincident(g34,g17)
    c: Horizontal(g34)
    c: Coincident(g35,g5)
    c: Coincident(g35,g17)
    c: Horizontal(g35)
    c: Coincident(g36,g6)
    c: Coincident(g36,g19)
    c: Horizontal(g36)
    c: Coincident(g37,g6)
    c: Coincident(g37,g19)
    c: Horizontal(g37)
    c: Coincident(g38,g7)
    c: Coincident(g38,g18)
    c: Horizontal(g38)
    c: Coincident(g39,g7)
    c: Coincident(g39,g18)
    c: Horizontal(g39)
    c: Coincident(g40,g8)
    c: Coincident(g40,g20)
    c: Horizontal(g40)
    c: Coincident(g41,g8)
    c: Coincident(g41,g20)
    c: Horizontal(g41)
    c: Coincident(g42,g9)
    c: Coincident(g42,g23)
    c: Horizontal(g42)
    c: Coincident(g43,g9)
    c: Coincident(g43,g23)
    c: Horizontal(g43)
    c: Coincident(g44,g10)
    c: Coincident(g44,g22)
    c: Horizontal(g44)
    c: Coincident(g45,g10)
    c: Coincident(g45,g22)
    c: Horizontal(g45)
    c: Coincident(g46,g11)
    c: Coincident(g46,g21)
    c: Horizontal(g46)
    c: Coincident(g47,g11)
    c: Coincident(g47,g21)
    c: Horizontal(g47)
FEATURE [Part::Extrusion] Extrude065
  Base = -> Sketch074
  Dir = (1,0,0)
  DirMode = 2
  FaceMakerClass = Part::FaceMakerBullseye
  LengthFwd = 23
  LengthRev = 0
  Placement = pos=(-19,0,0) rot=(0,0,1;0rad)
  Solid = true
  Symmetric = false
FEATURE [Part::Fillet] Fillet056  label="removeToCreateVentalationHoles003"
  Base = -> Extrude065
  Edges = <same value as first occurrence — deduplicated (x6 in doc)>
  Placement = pos=(7,0.02,0) rot=(0,0,1;0rad)
FEATURE [Part::Revolution] Revolve158  label="removeToCreateScrewAndThreadedInsertHole065"
  Angle = 360
  Axis = (0,1,0)
  Base = (0,0,0)
  FaceMakerClass = Part::FaceMakerBullseye
  Placement = pos=(12.5,0,62) rot=(0,0,1;0rad)
  Solid = false
  Source = -> Face146
  Symmetric = false
FEATURE [Part::Revolution] Revolve159  label="removeToCreateScrewAndThreadedInsertHole066"
  Angle = 360
  Axis = (0,1,0)
  Base = (0,0,0)
  FaceMakerClass = Part::FaceMakerBullseye
  Placement = pos=(89.5,0,68.5) rot=(0,0,1;0rad)
  Solid = false
  Source = -> Face143
  Symmetric = false
FEATURE [Part::Revolution] Revolve160  label="removeToCreateScrewAndThreadedInsertHole067"
  Angle = 360
  Axis = (0,1,0)
  Base = (0,0,0)
  FaceMakerClass = Part::FaceMakerBullseye
  Placement = pos=(89.5,0,3.5) rot=(0,0,1;0rad)
  Solid = false
  Source = -> Face142
  Symmetric = false
FEATURE [Part::Revolution] Revolve161  label="removeToCreateScrewAndThreadedInsertHole068"
  Angle = 360
  Axis = (0,1,0)
  Base = (0,0,0)
  FaceMakerClass = Part::FaceMakerBullseye
  Placement = pos=(109.5,4.7,3.5) rot=(0,0,1;0rad)
  Solid = false
  Source = -> Face145
  Symmetric = false
FEATURE [Part::Revolution] Revolve162  label="removeToCreateScrewAndThreadedInsertHole069"
  Angle = 360
  Axis = (0,1,0)
  Base = (0,0,0)
  FaceMakerClass = Part::FaceMakerBullseye
  Placement = pos=(109.5,4.7,68.5) rot=(0,0,1;0rad)
  Solid = false
  Source = -> Face144
  Symmetric = false
FEATURE [Part::MultiFuse] Fusion141  label="removeToCreateScrewAndThreadedInsertHole064"
  Shapes = -> [Revolve162,Revolve161,Revolve160,Revolve159,Revolve158,Revolve157]
FEATURE [Part::Cylinder] Cylinder062
  Angle = 360
  AttacherType = Attacher::AttachEngine3D
  Height = 20
  Placement = pos=(0,0,36.15) rot=(0,0,1;0rad)
  Radius = 14
FEATURE [Part::Cylinder] Cylinder063
  Angle = 360
  AttacherType = Attacher::AttachEngine3D
  Height = 10
  Placement = pos=(0,0,36.15) rot=(0,0,1;0rad)
  Radius = 4
FEATURE [Part::MultiFuse] Fusion139  label="removeToCreteHoleForPlugHousing052"
  Placement = pos=(70,19,36) rot=(0,1,0;1.5708rad)
  Shapes = -> [Cylinder062,Cylinder063]
FEATURE [Part::Cut] Cut060  label="bottom017"
  Base = -> Extrude064
  Tool = -> Fusion139
FEATURE [Part::Cut] Cut061  label="bottom019"
  Base = -> Cut060
  Tool = -> Fusion141
FEATURE [Part::MultiFuse] Fusion140  label="bottom018"
  Shapes = -> [Cut061,Cut058]
FEATURE [Part::Cut] Cut059  label="bottom020"
  Base = -> Fusion140
  Tool = -> Fillet056
FEATURE [Part::Box] Box036  label="Cube021"
  AttacherType = Attacher::AttachEngine3D
  Height = 80
  Length = 26
  Placement = pos=(0,-1,-5) rot=(0,0,1;0rad)
  Width = 11
FEATURE [Part::Cut] Cut062  label="removeFromBottom002"
  Base = -> Cut057
  Tool = -> Box036
FEATURE [Part::Cut] Cut063
  Base = -> Cut059
  Tool = -> Cut062
FEATURE [Part::Cut] Cut064  label="pcbStands"
  Base = -> Fusion095
  Tool = -> Fusion127
FEATURE [Sketcher::SketchObject] Sketch075  label="topSketch022"
  FullyConstrained = true
  sketch-geometry (6):
    g0: LineSegment StartX=19 StartY=38 StartZ=0 EndX=117 EndY=38 EndZ=0
    g1: ArcOfCircle CenterX=19 CenterY=19 CenterZ=0 NormalX=0 NormalY=0 NormalZ=1 AngleXU=0 Radius=19 StartAngle=1.5708 EndAngle=3.14159
    g2: LineSegment StartX=117 StartY=38 StartZ=0 EndX=117 EndY=19 EndZ=0
    g3: LineSegment StartX=98 StartY=1.0161e-12 StartZ=0 EndX=5.22862e-06 EndY=1.0161e-12 EndZ=0
    g4: LineSegment StartX=5.22862e-06 StartY=19 StartZ=0 EndX=5.22862e-06 EndY=1.0161e-12 EndZ=0
    g5: ArcOfCircle CenterX=98 CenterY=19 CenterZ=0 NormalX=0 NormalY=0 NormalZ=1 AngleXU=0 Radius=19 StartAngle=4.71239 EndAngle=6.28319
  constraints (16):
    c: Horizontal(g0)
    c: Distance(g0) = 98
    c: Coincident(g1,g0)
    c: Block(g1)
    c: Coincident(g2,g0)
    c: Vertical(g2)
    c: Distance(g2) = 19
    c: Horizontal(g3)
    c: Coincident(g4,g1)
    c: Vertical(g4)
    c: Coincident(g3,g4)
    c: Block(g3)
    c: Coincident(g5,g2)
    c: Coincident(g5,g3)
    c: Block(g0)
    c: Block(g5)
FEATURE [Part::Extrusion] Extrude067  label="sideB003"
  Base = -> Sketch075
  Dir = (0,0,1)
  DirMode = 2
  FaceMakerClass = Part::FaceMakerBullseye
  LengthFwd = 3
  LengthRev = 0
  Placement = pos=(0,0,71.7) rot=(0,0,1;0rad)
  Solid = true
  Symmetric = false
FEATURE [Sketcher::SketchObject] Sketch076  label="topSketch023"
  FullyConstrained = true
  sketch-geometry (6):
    g0: LineSegment StartX=19 StartY=38 StartZ=0 EndX=117 EndY=38 EndZ=0
    g1: ArcOfCircle CenterX=19 CenterY=19 CenterZ=0 NormalX=0 NormalY=0 NormalZ=1 AngleXU=0 Radius=19 StartAngle=1.5708 EndAngle=3.14159
    g2: LineSegment StartX=117 StartY=38 StartZ=0 EndX=117 EndY=19 EndZ=0
    g3: LineSegment StartX=98 StartY=1.0161e-12 StartZ=0 EndX=5.22862e-06 EndY=1.0161e-12 EndZ=0
    g4: LineSegment StartX=5.22862e-06 StartY=19 StartZ=0 EndX=5.22862e-06 EndY=1.0161e-12 EndZ=0
    g5: ArcOfCircle CenterX=98 CenterY=19 CenterZ=0 NormalX=0 NormalY=0 NormalZ=1 AngleXU=0 Radius=19 StartAngle=4.71239 EndAngle=6.28319
  constraints (16):
    c: Horizontal(g0)
    c: Distance(g0) = 98
    c: Coincident(g1,g0)
    c: Block(g1)
    c: Coincident(g2,g0)
    c: Vertical(g2)
    c: Distance(g2) = 19
    c: Horizontal(g3)
    c: Coincident(g4,g1)
    c: Vertical(g4)
    c: Coincident(g3,g4)
    c: Block(g3)
    c: Coincident(g5,g2)
    c: Coincident(g5,g3)
    c: Block(g0)
    c: Block(g5)
FEATURE [Part::Extrusion] Extrude066  label="sideA003"
  Base = -> Sketch076
  Dir = (0,0,1)
  DirMode = 2
  FaceMakerClass = Part::FaceMakerBullseye
  LengthFwd = 3
  LengthRev = 0
  Placement = pos=(0,0,-2.7) rot=(0,0,1;0rad)
  Solid = true
  Symmetric = false
FEATURE [Part::MultiFuse] Fusion142  label="removeFromBottom003"
  Placement = pos=(2,0,0) rot=(0,0,1;0rad)
  Shapes = -> [Extrude066,Extrude067]
FEATURE [Part::Cut] Cut065  label="screwRetainers002"
  Base = -> Fusion096
  Tool = -> Fusion142
FEATURE [Sketcher::SketchObject] Sketch077
  FullyConstrained = true
  Placement = pos=(117,19,0) rot=(0.57735,0.57735,0.57735;2.0944rad)
  sketch-geometry (8):
    g0: LineSegment StartX=-49.19 StartY=63.5 StartZ=0 EndX=-49.19 EndY=60.5 EndZ=0
    g1: LineSegment StartX=-49.19 StartY=11.5 StartZ=0 EndX=-49.19 EndY=8.5 EndZ=0
    g2: ArcOfCircle CenterX=-1.5 CenterY=62 CenterZ=0 NormalX=0 NormalY=0 NormalZ=1 AngleXU=0 Radius=1.5 StartAngle=4.71239 EndAngle=7.85398
    g3: ArcOfCircle CenterX=-1.5 CenterY=10 CenterZ=0 NormalX=0 NormalY=0 NormalZ=1 AngleXU=0 Radius=1.5 StartAngle=4.71239 EndAngle=7.85398
    g4: LineSegment StartX=-49.19 StartY=63.5 StartZ=0 EndX=-1.5 EndY=63.5 EndZ=0
    g5: LineSegment StartX=-49.19 StartY=60.5 StartZ=0 EndX=-1.5 EndY=60.5 EndZ=0
    g6: LineSegment StartX=-49.19 StartY=11.5 StartZ=0 EndX=-1.5 EndY=11.5 EndZ=0
    g7: LineSegment StartX=-49.19 StartY=8.5 StartZ=0 EndX=-1.5 EndY=8.5 EndZ=0
  constraints (19):
    c: Vertical(g0)
    c: Distance(g0) = 3
    c: Vertical(g1)
    c: Block(g1)
    c: Block(g2)
    c: Block(g3)
    c: Block(g0)
    c: Coincident(g4,g0)
    c: Coincident(g4,g2)
    c: Horizontal(g4)
    c: Coincident(g5,g0)
    c: Coincident(g5,g2)
    c: Horizontal(g5)
    c: Coincident(g6,g1)
    c: Coincident(g6,g3)
    c: Horizontal(g6)
    c: Coincident(g7,g1)
    c: Coincident(g7,g3)
    c: Horizontal(g7)
FEATURE [Part::Extrusion] Extrude068
  Base = -> Sketch077
  Dir = (1,0,0)
  DirMode = 2
  FaceMakerClass = Part::FaceMakerBullseye
  LengthFwd = 10
  LengthRev = 0
  Solid = true
  Symmetric = false
FEATURE [Part::Fillet] Fillet057  label="removeFromtMoreFrontCaseScrewRetainers002"
  Base = -> Extrude068
  Edges = 4 edges r=1.49: [Edge6,Edge11,Edge18,Edge23]
  Placement = pos=(-12,0,0) rot=(0,0,1;0rad)
FEATURE [Sketcher::SketchObject] Sketch078
  FullyConstrained = true
  Placement = pos=(117,19,0) rot=(0.57735,0.57735,0.57735;2.0944rad)
  sketch-geometry (8):
    g0: LineSegment StartX=-49.19 StartY=69.25 StartZ=0 EndX=-49.19 EndY=66.25 EndZ=0
    g1: LineSegment StartX=-49.19 StartY=5.75 StartZ=0 EndX=-49.19 EndY=2.75 EndZ=0
    g2: ArcOfCircle CenterX=-1.5 CenterY=67.75 CenterZ=0 NormalX=0 NormalY=0 NormalZ=1 AngleXU=0 Radius=1.5 StartAngle=4.71239 EndAngle=7.85398
    g3: ArcOfCircle CenterX=-1.5 CenterY=4.25 CenterZ=0 NormalX=0 NormalY=0 NormalZ=1 AngleXU=0 Radius=1.5 StartAngle=4.71239 EndAngle=7.85398
    g4: LineSegment StartX=-49.19 StartY=69.25 StartZ=0 EndX=-1.5 EndY=69.25 EndZ=0
    g5: LineSegment StartX=-49.19 StartY=66.25 StartZ=0 EndX=-1.5 EndY=66.25 EndZ=0
    g6: LineSegment StartX=-49.19 StartY=5.75 StartZ=0 EndX=-1.5 EndY=5.75 EndZ=0
    g7: LineSegment StartX=-49.19 StartY=2.75 StartZ=0 EndX=-1.5 EndY=2.75 EndZ=0
  constraints (19):
    c: Vertical(g0)
    c: Distance(g0) = 3
    c: Block(g0)
    c: Vertical(g1)
    c: Block(g2)
    c: Block(g3)
    c: Block(g1)
    c: Coincident(g4,g0)
    c: Coincident(g4,g2)
    c: Horizontal(g4)
    c: Coincident(g5,g0)
    c: Coincident(g5,g2)
    c: Horizontal(g5)
    c: Coincident(g6,g1)
    c: Coincident(g6,g3)
    c: Horizontal(g6)
    c: Coincident(g7,g1)
    c: Coincident(g7,g3)
    c: Horizontal(g7)
FEATURE [Part::Extrusion] Extrude069
  Base = -> Sketch078
  Dir = (1,0,0)
  DirMode = 2
  FaceMakerClass = Part::FaceMakerBullseye
  LengthFwd = 10
  LengthRev = 0
  Solid = true
  Symmetric = false
FEATURE [Part::Fillet] Fillet058  label="removeFromtMoreFrontCaseScrewRetainers003"
  Base = -> Extrude069
  Edges = 4 edges r=1.49: [Edge6,Edge11,Edge18,Edge23]
  Placement = pos=(-4,0,0) rot=(0,0,1;0rad)
FEATURE [Part::Cut] Cut066
  Base = -> Cut065
  Tool = -> Fillet058
FEATURE [Part::Cut] Cut067  label="screwPillars"
  Base = -> Cut066
  Tool = -> Fillet057
FEATURE [Part::MultiFuse] Fusion143  label="bottom021"
  Shapes = -> [Cut031,Cut063]
FEATURE [Part::Cylinder] Cylinder
  Angle = 360
  AttacherType = Attacher::AttachEngine3D
  Height = 10
  Placement = pos=(20.65,12,4.68) rot=(1,0,0;1.5708rad)
  Radius = 2
FEATURE [Part::Cylinder] Cylinder064
  Angle = 360
  AttacherType = Attacher::AttachEngine3D
  Height = 10
  Placement = pos=(20.65,12,67.38) rot=(1,0,0;1.5708rad)
  Radius = 2
FEATURE [Part::Cylinder] Cylinder065
  Angle = 360
  AttacherType = Attacher::AttachEngine3D
  Height = 10
  Placement = pos=(77.15,12,67.38) rot=(1,0,0;1.5708rad)
  Radius = 2
FEATURE [Part::Cylinder] Cylinder066
  Angle = 360
  AttacherType = Attacher::AttachEngine3D
  Height = 10
  Placement = pos=(77.15,12,4.68) rot=(1,0,0;1.5708rad)
  Radius = 2
FEATURE [Part::MultiFuse] Fusion144  label="removeFromThreadedInsertHousing"
  Shapes = -> [Cylinder065,Cylinder064,Cylinder,Cylinder066]
FEATURE [Part::Cut] Cut068  label="pcbStands001"
  Base = -> Cut064
  Tool = -> Fusion144
FEATURE [Part::MultiFuse] Fusion145
  Shapes = -> [Cut068,Fusion143]
FEATURE [Part::MultiFuse] Fusion146
  Shapes = -> [Fusion145]
FEATURE [Part::MultiFuse] Fusion147  label="bottom022"
  Shapes = -> [Cut067,Fusion146]
FEATURE [Part::MultiFuse] Fusion148  label="casePillars005"
  Shapes = -> [Cut047,Fusion092]
FEATURE [Part::MultiFuse] Fusion149  label="bottom023"
  Shapes = -> [Fusion124,Fusion113,Fusion147]
FEATURE [Part::MultiFuse] Fusion150  label="topBits"
  Shapes = -> [Cut025,Fusion148,Cut030,Fillet034]
FEATURE [Part::Feature] Face149 .. Face152  x4 (patterned run collapsed; names and placements below)
  shape: bbox 3.2 x 1.5 x 2e-07 mm, 1 faces, 0 solids (baked)
FEATURE [Part::Feature] Face153
  shape: bbox 3.6 x 3.2 x 2e-07 mm, 1 faces, 0 solids (baked)
FEATURE [Part::Feature] Face154
  shape: bbox 3.6 x 3.2 x 2e-07 mm, 1 faces, 0 solids (baked)
FEATURE [Sketcher::SketchObject] Sketch079  label="topSketch024"
  FullyConstrained = true
  sketch-geometry (6):
    g0: LineSegment StartX=19 StartY=38 StartZ=0 EndX=117 EndY=38 EndZ=0
    g1: ArcOfCircle CenterX=19 CenterY=19 CenterZ=0 NormalX=0 NormalY=0 NormalZ=1 AngleXU=0 Radius=19 StartAngle=1.5708 EndAngle=3.14159
    g2: LineSegment StartX=117 StartY=38 StartZ=0 EndX=117 EndY=19 EndZ=0
    g3: LineSegment StartX=98 StartY=1.0161e-12 StartZ=0 EndX=5.22862e-06 EndY=1.0161e-12 EndZ=0
    g4: LineSegment StartX=5.22862e-06 StartY=19 StartZ=0 EndX=5.22862e-06 EndY=1.0161e-12 EndZ=0
    g5: ArcOfCircle CenterX=98 CenterY=19 CenterZ=0 NormalX=0 NormalY=0 NormalZ=1 AngleXU=0 Radius=19 StartAngle=4.71239 EndAngle=6.28319
  constraints (16):
    c: Horizontal(g0)
    c: Distance(g0) = 98
    c: Coincident(g1,g0)
    c: Block(g1)
    c: Coincident(g2,g0)
    c: Vertical(g2)
    c: Distance(g2) = 19
    c: Horizontal(g3)
    c: Coincident(g4,g1)
    c: Vertical(g4)
    c: Coincident(g3,g4)
    c: Block(g3)
    c: Coincident(g5,g2)
    c: Coincident(g5,g3)
    c: Block(g0)
    c: Block(g5)
FEATURE [Sketcher::SketchObject] Sketch080  label="topSketch025"
  FullyConstrained = true
  sketch-geometry (6):
    g0: LineSegment StartX=19 StartY=38 StartZ=0 EndX=117 EndY=38 EndZ=0
    g1: ArcOfCircle CenterX=19 CenterY=19 CenterZ=0 NormalX=0 NormalY=0 NormalZ=1 AngleXU=0 Radius=19 StartAngle=1.5708 EndAngle=3.14159
    g2: LineSegment StartX=117 StartY=38 StartZ=0 EndX=117 EndY=19 EndZ=0
    g3: LineSegment StartX=98 StartY=1.0161e-12 StartZ=0 EndX=5.22862e-06 EndY=1.0161e-12 EndZ=0
    g4: LineSegment StartX=5.22862e-06 StartY=19 StartZ=0 EndX=5.22862e-06 EndY=1.0161e-12 EndZ=0
    g5: ArcOfCircle CenterX=98 CenterY=19 CenterZ=0 NormalX=0 NormalY=0 NormalZ=1 AngleXU=0 Radius=19 StartAngle=4.71239 EndAngle=6.28319
  constraints (16):
    c: Horizontal(g0)
    c: Distance(g0) = 98
    c: Coincident(g1,g0)
    c: Block(g1)
    c: Coincident(g2,g0)
    c: Vertical(g2)
    c: Distance(g2) = 19
    c: Horizontal(g3)
    c: Coincident(g4,g1)
    c: Vertical(g4)
    c: Coincident(g3,g4)
    c: Block(g3)
    c: Coincident(g5,g2)
    c: Coincident(g5,g3)
    c: Block(g0)
    c: Block(g5)
FEATURE [Part::Extrusion] Extrude070  label="sideA004"
  Base = -> Sketch080
  Dir = (0,0,1)
  DirMode = 2
  FaceMakerClass = Part::FaceMakerBullseye
  LengthFwd = 3
  LengthRev = 0
  Placement = pos=(0,0,-2.7) rot=(0,0,1;0rad)
  Solid = true
  Symmetric = false
FEATURE [Sketcher::SketchObject] Sketch081
  FullyConstrained = true
  Placement = pos=(117,19,0) rot=(0.57735,0.57735,0.57735;2.0944rad)
  sketch-geometry (8):
    g0: LineSegment StartX=-49.19 StartY=63.5 StartZ=0 EndX=-49.19 EndY=60.5 EndZ=0
    g1: LineSegment StartX=-49.19 StartY=11.5 StartZ=0 EndX=-49.19 EndY=8.5 EndZ=0
    g2: ArcOfCircle CenterX=-1.5 CenterY=62 CenterZ=0 NormalX=0 NormalY=0 NormalZ=1 AngleXU=0 Radius=1.5 StartAngle=4.71239 EndAngle=7.85398
    g3: ArcOfCircle CenterX=-1.5 CenterY=10 CenterZ=0 NormalX=0 NormalY=0 NormalZ=1 AngleXU=0 Radius=1.5 StartAngle=4.71239 EndAngle=7.85398
    g4: LineSegment StartX=-49.19 StartY=63.5 StartZ=0 EndX=-1.5 EndY=63.5 EndZ=0
    g5: LineSegment StartX=-49.19 StartY=60.5 StartZ=0 EndX=-1.5 EndY=60.5 EndZ=0
    g6: LineSegment StartX=-49.19 StartY=11.5 StartZ=0 EndX=-1.5 EndY=11.5 EndZ=0
    g7: LineSegment StartX=-49.19 StartY=8.5 StartZ=0 EndX=-1.5 EndY=8.5 EndZ=0
  constraints (19):
    c: Vertical(g0)
    c: Distance(g0) = 3
    c: Vertical(g1)
    c: Block(g1)
    c: Block(g2)
    c: Block(g3)
    c: Block(g0)
    c: Coincident(g4,g0)
    c: Coincident(g4,g2)
    c: Horizontal(g4)
    c: Coincident(g5,g0)
    c: Coincident(g5,g2)
    c: Horizontal(g5)
    c: Coincident(g6,g1)
    c: Coincident(g6,g3)
    c: Horizontal(g6)
    c: Coincident(g7,g1)
    c: Coincident(g7,g3)
    c: Horizontal(g7)
FEATURE [Part::Extrusion] Extrude071  label="sideB004"
  Base = -> Sketch079
  Dir = (0,0,1)
  DirMode = 2
  FaceMakerClass = Part::FaceMakerBullseye
  LengthFwd = 3
  LengthRev = 0
  Placement = pos=(0,0,71.7) rot=(0,0,1;0rad)
  Solid = true
  Symmetric = false
FEATURE [Part::MultiFuse] Fusion152  label="removeFromBottom004"
  Placement = pos=(2,0,0) rot=(0,0,1;0rad)
  Shapes = -> [Extrude070,Extrude071]
FEATURE [Part::Extrusion] Extrude072
  Base = -> Sketch081
  Dir = (1,0,0)
  DirMode = 2
  FaceMakerClass = Part::FaceMakerBullseye
  LengthFwd = 10
  LengthRev = 0
  Solid = true
  Symmetric = false
FEATURE [Part::Fillet] Fillet059  label="removeFromtMoreFrontCaseScrewRetainers004"
  Base = -> Extrude072
  Edges = 4 edges r=1.49: [Edge6,Edge11,Edge18,Edge23]
  Placement = pos=(-12,0,0) rot=(0,0,1;0rad)
FEATURE [Sketcher::SketchObject] Sketch082
  FullyConstrained = true
  Placement = pos=(117,19,0) rot=(0.57735,0.57735,0.57735;2.0944rad)
  sketch-geometry (8):
    g0: LineSegment StartX=-49.19 StartY=69.25 StartZ=0 EndX=-49.19 EndY=66.25 EndZ=0
    g1: LineSegment StartX=-49.19 StartY=5.75 StartZ=0 EndX=-49.19 EndY=2.75 EndZ=0
    g2: ArcOfCircle CenterX=-1.5 CenterY=67.75 CenterZ=0 NormalX=0 NormalY=0 NormalZ=1 AngleXU=0 Radius=1.5 StartAngle=4.71239 EndAngle=7.85398
    g3: ArcOfCircle CenterX=-1.5 CenterY=4.25 CenterZ=0 NormalX=0 NormalY=0 NormalZ=1 AngleXU=0 Radius=1.5 StartAngle=4.71239 EndAngle=7.85398
    g4: LineSegment StartX=-49.19 StartY=69.25 StartZ=0 EndX=-1.5 EndY=69.25 EndZ=0
    g5: LineSegment StartX=-49.19 StartY=66.25 StartZ=0 EndX=-1.5 EndY=66.25 EndZ=0
    g6: LineSegment StartX=-49.19 StartY=5.75 StartZ=0 EndX=-1.5 EndY=5.75 EndZ=0
    g7: LineSegment StartX=-49.19 StartY=2.75 StartZ=0 EndX=-1.5 EndY=2.75 EndZ=0
  constraints (19):
    c: Vertical(g0)
    c: Distance(g0) = 3
    c: Block(g0)
    c: Vertical(g1)
    c: Block(g2)
    c: Block(g3)
    c: Block(g1)
    c: Coincident(g4,g0)
    c: Coincident(g4,g2)
    c: Horizontal(g4)
    c: Coincident(g5,g0)
    c: Coincident(g5,g2)
    c: Horizontal(g5)
    c: Coincident(g6,g1)
    c: Coincident(g6,g3)
    c: Horizontal(g6)
    c: Coincident(g7,g1)
    c: Coincident(g7,g3)
    c: Horizontal(g7)
FEATURE [Part::Extrusion] Extrude073
  Base = -> Sketch082
  Dir = (1,0,0)
  DirMode = 2
  FaceMakerClass = Part::FaceMakerBullseye
  LengthFwd = 10
  LengthRev = 0
  Solid = true
  Symmetric = false
FEATURE [Part::Fillet] Fillet060  label="removeFromtMoreFrontCaseScrewRetainers005"
  Base = -> Extrude073
  Edges = 4 edges r=1.49: [Edge6,Edge11,Edge18,Edge23]
  Placement = pos=(-4,0,0) rot=(0,0,1;0rad)
FEATURE [Part::Revolution] Revolve163  label="backCaseScrewRetainer004"
  Angle = 360
  Axis = (0,1,0)
  Base = (0,0,0)
  FaceMakerClass = Part::FaceMakerBullseye
  Placement = pos=(12.5,3,62) rot=(0,0,1;0rad)
  Solid = false
  Source = -> Face149
  Symmetric = false
FEATURE [Part::Revolution] Revolve164  label="frontCaseScrewRetainer006"
  Angle = 360
  Axis = (0,1,0)
  Base = (0,0,0)
  FaceMakerClass = Part::FaceMakerBullseye
  Placement = pos=(89.5,3,68.5) rot=(0,0,1;0rad)
  Solid = false
  Source = -> Face151
  Symmetric = false
FEATURE [Part::Revolution] Revolve165  label="frontCaseScrewRetainer007"
  Angle = 360
  Axis = (0,1,0)
  Base = (0,0,0)
  FaceMakerClass = Part::FaceMakerBullseye
  Placement = pos=(89.5,3,3.5) rot=(0,0,1;0rad)
  Solid = false
  Source = -> Face152
  Symmetric = false
FEATURE [Part::Revolution] Revolve166  label="backCaseScrewRetainer005"
  Angle = 360
  Axis = (0,1,0)
  Base = (0,0,0)
  FaceMakerClass = Part::FaceMakerBullseye
  Placement = pos=(12.5,3,10) rot=(0,0,1;0rad)
  Solid = false
  Source = -> Face150
  Symmetric = false
FEATURE [Part::Revolution] Revolve167  label="moreFrontCaseScrewRetainer006"
  Angle = 360
  Axis = (0,1,0)
  Base = (0,0,0)
  FaceMakerClass = Part::FaceMakerBullseye
  Placement = pos=(109.5,4.5,68.5) rot=(0,0,1;0rad)
  Solid = false
  Source = -> Face153
  Symmetric = false
FEATURE [Part::Revolution] Revolve168  label="moreFrontCaseScrewRetainer007"
  Angle = 360
  Axis = (0,1,0)
  Base = (0,0,0)
  FaceMakerClass = Part::FaceMakerBullseye
  Placement = pos=(109.5,4.5,3.5) rot=(0,0,1;0rad)
  Solid = false
  Source = -> Face154
  Symmetric = false
FEATURE [Part::MultiFuse] Fusion151  label="screwRetainers003"
  Shapes = -> [Revolve168,Revolve167,Revolve166,Revolve165,Revolve164,Revolve163]
FEATURE [Part::Cut] Cut069  label="screwRetainers004"
  Base = -> Fusion151
  Tool = -> Fusion152
FEATURE [Part::Cut] Cut070
  Base = -> Cut069
  Tool = -> Fillet060
FEATURE [Part::Cut] Cut071  label="screwPillars001"
  Base = -> Cut070
  Tool = -> Fillet059
FEATURE [Part::MultiFuse] Fusion153  label="bottom024"
  Shapes = -> [Fusion149,Cut071]
FEATURE [Part::Cylinder] Cylinder067
  Angle = 360
  AttacherType = Attacher::AttachEngine3D
  Height = 10
  Placement = pos=(20.65,12,4.68) rot=(1,0,0;1.5708rad)
  Radius = 2
FEATURE [Part::Cylinder] Cylinder068
  Angle = 360
  AttacherType = Attacher::AttachEngine3D
  Height = 10
  Placement = pos=(20.65,12,67.38) rot=(1,0,0;1.5708rad)
  Radius = 2
FEATURE [Part::Cylinder] Cylinder069
  Angle = 360
  AttacherType = Attacher::AttachEngine3D
  Height = 10
  Placement = pos=(77.15,12,67.38) rot=(1,0,0;1.5708rad)
  Radius = 2
FEATURE [Part::Cylinder] Cylinder070
  Angle = 360
  AttacherType = Attacher::AttachEngine3D
  Height = 10
  Placement = pos=(77.15,12,4.68) rot=(1,0,0;1.5708rad)
  Radius = 2
FEATURE [Part::MultiFuse] Fusion154  label="removeFromThreadedInsertHousing001"
  Shapes = -> [Cylinder069,Cylinder068,Cylinder067,Cylinder070]
FEATURE [Part::Cut] Cut072  label="bottom025"
  Base = -> Fusion153
  Tool = -> Fusion154
FEATURE [Image::ImagePlane] ImagePlane
  XSize = 339
  YSize = 72
FEATURE [Sketcher::SketchObject] Sketch083
  FullyConstrained = true
  MapMode = 5
  Support = -> [XY_Plane]
  sketch-geometry (205):
    g0: LineSegment StartX=-151.619 StartY=28.8932 StartZ=0 EndX=-140.819 EndY=28.8932 EndZ=0
    g1: LineSegment StartX=-151.619 StartY=24.0313 StartZ=0 EndX=-151.619 EndY=28.8932 EndZ=0
    g2: LineSegment StartX=-140.819 StartY=17.7713 StartZ=0 EndX=-151.619 EndY=17.7713 EndZ=0
    g3: LineSegment StartX=-151.619 StartY=17.7713 StartZ=0 EndX=-151.619 EndY=22.6313 EndZ=0
    g4: LineSegment StartX=-151.619 StartY=22.6313 StartZ=0 EndX=-145.128 EndY=22.6313 EndZ=0
    g5: LineSegment StartX=-145.128 StartY=24.0313 StartZ=0 EndX=-140.819 EndY=28.8932 EndZ=0
    g6: LineSegment StartX=-145.128 StartY=22.6313 StartZ=0 EndX=-140.819 EndY=17.7713 EndZ=0
    g7: ArcOfCircle CenterX=-155.157 CenterY=23.3323 CenterZ=0 NormalX=0 NormalY=0 NormalZ=1 AngleXU=0 Radius=6.92354 StartAngle=1.03434 EndAngle=5.24885
    g8: ArcOfCircle CenterX=-155.157 CenterY=23.3323 CenterZ=0 NormalX=0 NormalY=0 NormalZ=1 AngleXU=0 Radius=12.6269 StartAngle=1.28675 EndAngle=4.99643
    g9: LineSegment StartX=-151.619 StartY=35.4532 StartZ=0 EndX=-151.619 EndY=29.2832 EndZ=0
    g10: LineSegment StartX=-151.619 StartY=17.3813 StartZ=0 EndX=-151.619 EndY=11.2113 EndZ=0
    g11-g21: Circle x11 (B-spline internal-alignment scaffolding for g22; pole/knot coordinates omitted)
    g22: BSplineCurve PolesCount=11 KnotsCount=9 Degree=3 IsPeriodic=0
    g23-g31: GeomPoint x9 (B-spline internal-alignment scaffolding for g22; pole/knot coordinates omitted)
    g32-g49: Circle x18 (B-spline internal-alignment scaffolding for g50; pole/knot coordinates omitted)
    g50: BSplineCurve PolesCount=18 KnotsCount=16 Degree=3 IsPeriodic=0
    g51-g66: GeomPoint x16 (B-spline internal-alignment scaffolding for g50; pole/knot coordinates omitted)
    g67: LineSegment StartX=-117.124 StartY=30.093 StartZ=0 EndX=-117.603 EndY=26.5272 EndZ=0
    g68: LineSegment StartX=-117.603 StartY=17.8472 StartZ=0 EndX=-117.124 EndY=14.2659 EndZ=0
    g69: Ellipse CenterX=-109.671 CenterY=20.025 CenterZ=0 NormalX=0 NormalY=0 NormalZ=1 MajorRadius=3.34798 MinorRadius=2.71052 AngleXU=-1.56793
    g70: GeomPoint X=-109.666 Y=18.0598 Z=0
    g71: GeomPoint X=-109.677 Y=21.9902 Z=0
    g72: Ellipse CenterX=-109.671 CenterY=20.0123 CenterZ=0 NormalX=0 NormalY=0 NormalZ=1 MajorRadius=6.93002 MinorRadius=6.36273 AngleXU=-3.13976
    g73: GeomPoint X=-112.417 Y=20.0073 Z=0
    g74: GeomPoint X=-106.925 Y=20.0173 Z=0
    g75: Ellipse CenterX=-51.7682 CenterY=20.1463 CenterZ=0 NormalX=0 NormalY=0 NormalZ=1 MajorRadius=3.19279 MinorRadius=2.71052 AngleXU=-1.52774
    g76: GeomPoint X=-51.6955 Y=18.4606 Z=0
    g77: GeomPoint X=-51.8408 Y=21.832 Z=0
    g78: GeomPoint X=-54.5142 Y=20.1413 Z=0
    g79: GeomPoint X=-49.0221 Y=20.1513 Z=0
    g80: Ellipse CenterX=-51.7682 CenterY=20.1463 CenterZ=0 NormalX=0 NormalY=0 NormalZ=1 MajorRadius=6.93002 MinorRadius=6.36273 AngleXU=-3.13976
    g81: Ellipse CenterX=-22.8436 CenterY=20.1783 CenterZ=0 NormalX=0 NormalY=0 NormalZ=1 MajorRadius=3.31512 MinorRadius=2.71052 AngleXU=-1.60214
    g82: GeomPoint X=-22.9034 Y=18.2706 Z=0
    g83: GeomPoint X=-22.7838 Y=22.0861 Z=0
    g84: GeomPoint X=-25.5897 Y=20.1733 Z=0
    g85: GeomPoint X=-20.0976 Y=20.1833 Z=0
    g86: Ellipse CenterX=-22.8436 CenterY=20.1783 CenterZ=0 NormalX=0 NormalY=0 NormalZ=1 MajorRadius=6.93002 MinorRadius=6.36273 AngleXU=-3.13976
    g87: LineSegment StartX=-101.889 StartY=14.1107 StartZ=0 EndX=-97.7455 EndY=14.1107 EndZ=0
    g88: LineSegment StartX=-93.8155 StartY=14.1107 StartZ=0 EndX=-89.6755 EndY=14.1107 EndZ=0
    g89: LineSegment StartX=-85.7455 StartY=14.1107 StartZ=0 EndX=-81.6055 EndY=14.1107 EndZ=0
    g90: LineSegment StartX=-101.889 StartY=14.1107 StartZ=0 EndX=-101.889 EndY=25.9907 EndZ=0
    g91: LineSegment StartX=-101.889 StartY=25.9907 StartZ=0 EndX=-97.8594 EndY=25.9907 EndZ=0
    g92: LineSegment StartX=-97.8594 StartY=25.9907 StartZ=0 EndX=-97.8594 EndY=24.0907 EndZ=0
    g93: LineSegment StartX=-97.7455 StartY=14.1107 StartZ=0 EndX=-97.7455 EndY=19.9107 EndZ=0
    g94: LineSegment StartX=-89.6755 StartY=14.1107 StartZ=0 EndX=-89.6755 EndY=19.9107 EndZ=0
    g95: LineSegment StartX=-93.8155 StartY=14.1107 StartZ=0 EndX=-93.8155 EndY=21.0107 EndZ=0
    g96-g106: Circle x11 (B-spline internal-alignment scaffolding for g107; pole/knot coordinates omitted)
    g107: BSplineCurve PolesCount=11 KnotsCount=9 Degree=3 IsPeriodic=0
    g108-g116: GeomPoint x9 (B-spline internal-alignment scaffolding for g107; pole/knot coordinates omitted)
    g117: BSplineCurve PolesCount=11 KnotsCount=9 Degree=3 IsPeriodic=0
    g118-g125: Circle x8 (B-spline internal-alignment scaffolding for g126; pole/knot coordinates omitted)
    g126: BSplineCurve PolesCount=8 KnotsCount=6 Degree=3 IsPeriodic=0
    g127-g132: GeomPoint x6 (B-spline internal-alignment scaffolding for g126; pole/knot coordinates omitted)
    g133: BSplineCurve PolesCount=8 KnotsCount=6 Degree=3 IsPeriodic=0
    g134: LineSegment StartX=-85.7455 StartY=21.0107 StartZ=0 EndX=-85.7455 EndY=14.1107 EndZ=0
    g135: LineSegment StartX=-80.0879 StartY=14.1107 StartZ=0 EndX=-75.944 EndY=14.1107 EndZ=0
    g136: LineSegment StartX=-72.014 StartY=14.1107 StartZ=0 EndX=-67.874 EndY=14.1107 EndZ=0
    g137: LineSegment StartX=-63.944 StartY=14.1107 StartZ=0 EndX=-59.804 EndY=14.1107 EndZ=0
    g138: LineSegment StartX=-80.0879 StartY=14.1107 StartZ=0 EndX=-80.0879 EndY=25.9907 EndZ=0
    g139: LineSegment StartX=-80.0879 StartY=25.9907 StartZ=0 EndX=-76.0579 EndY=25.9907 EndZ=0
    g140: LineSegment StartX=-76.0579 StartY=25.9907 StartZ=0 EndX=-76.0579 EndY=24.0907 EndZ=0
    g141: LineSegment StartX=-75.944 StartY=14.1107 StartZ=0 EndX=-75.944 EndY=19.9107 EndZ=0
    g142: LineSegment StartX=-67.874 StartY=14.1107 StartZ=0 EndX=-67.874 EndY=19.9107 EndZ=0
    g143: LineSegment StartX=-72.014 StartY=14.1107 StartZ=0 EndX=-72.014 EndY=21.0107 EndZ=0
    g144-g148: Circle x5 (B-spline internal-alignment scaffolding for g149; pole/knot coordinates omitted)
    g149: BSplineCurve PolesCount=11 KnotsCount=9 Degree=3 IsPeriodic=0
    g150-g158: GeomPoint x9 (B-spline internal-alignment scaffolding for g149; pole/knot coordinates omitted)
    g159: BSplineCurve PolesCount=11 KnotsCount=9 Degree=3 IsPeriodic=0
    g160-g167: Circle x8 (B-spline internal-alignment scaffolding for g168; pole/knot coordinates omitted)
    g168: BSplineCurve PolesCount=8 KnotsCount=6 Degree=3 IsPeriodic=0
    g169-g174: GeomPoint x6 (B-spline internal-alignment scaffolding for g168; pole/knot coordinates omitted)
    g175: BSplineCurve PolesCount=8 KnotsCount=6 Degree=3 IsPeriodic=0
    g176: LineSegment StartX=-63.944 StartY=21.0107 StartZ=0 EndX=-63.944 EndY=14.1107 EndZ=0
    g177: LineSegment StartX=-59.804 StartY=14.1107 StartZ=0 EndX=-59.804 EndY=21.5868 EndZ=0
    g178: BSplineCurve PolesCount=4 KnotsCount=2 Degree=3 IsPeriodic=0
    g179: GeomPoint X=-59.804 Y=21.5868 Z=0
    g180: GeomPoint X=-60.2379 Y=24.0907 Z=0
    g181: LineSegment StartX=-81.6055 StartY=14.1107 StartZ=0 EndX=-81.6055 EndY=21.5868 EndZ=0
    g182: LineSegment StartX=-151.619 StartY=24.0313 StartZ=0 EndX=-145.128 EndY=24.0313 EndZ=0
    g183: Circle CenterX=-82.0394 CenterY=24.0907 CenterZ=0 NormalX=0 NormalY=0 NormalZ=1 AngleXU=0 Radius=1
    g184: Circle CenterX=-81.7131 CenterY=23.2736 CenterZ=0 NormalX=0 NormalY=0 NormalZ=1 AngleXU=0 Radius=1
    g185: Circle CenterX=-81.6055 CenterY=21.5868 CenterZ=0 NormalX=0 NormalY=0 NormalZ=1 AngleXU=0 Radius=1
    g186: BSplineCurve PolesCount=3 KnotsCount=2 Degree=2 IsPeriodic=0
    g187: GeomPoint X=-82.0394 Y=24.0907 Z=0
    g188: GeomPoint X=-81.6055 Y=21.5868 Z=0
    g189: Ellipse CenterX=-37.3522 CenterY=19.9515 CenterZ=0 NormalX=0 NormalY=0 NormalZ=1 MajorRadius=2.99755 MinorRadius=2.49 AngleXU=1.5708
    g190: GeomPoint X=-37.3522 Y=21.6203 Z=0
    g191: GeomPoint X=-37.3522 Y=18.2826 Z=0
    g192: ArcOfEllipse CenterX=-38.7647 CenterY=20.06 CenterZ=0 NormalX=0 NormalY=0 NormalZ=1 MajorRadius=6.30025 MinorRadius=5.3849 AngleXU=1.57276 StartAngle=5.50632 EndAngle=10.3035
    g193: GeomPoint X=-38.7711 Y=23.3304 Z=0
    g194: GeomPoint X=-38.7583 Y=16.7895 Z=0
    g195: LineSegment StartX=-34.6109 StartY=14.1107 StartZ=0 EndX=-30.8984 EndY=14.1107 EndZ=0
    g196: LineSegment StartX=-30.8984 StartY=14.1107 StartZ=0 EndX=-30.8984 EndY=31.1784 EndZ=0
    g197: LineSegment StartX=-30.8984 StartY=31.1784 StartZ=0 EndX=-34.9984 EndY=31.1784 EndZ=0
    g198: LineSegment StartX=-34.9984 StartY=24.5602 StartZ=0 EndX=-34.9984 EndY=31.1784 EndZ=0
    g199: LineSegment StartX=-34.6109 StartY=16.0476 StartZ=0 EndX=-34.6109 EndY=14.1107 EndZ=0
    g200: LineSegment StartX=-14.8781 StartY=14.1107 StartZ=0 EndX=-10.5106 EndY=14.1107 EndZ=0
    g201: LineSegment StartX=-14.8781 StartY=14.1107 StartZ=0 EndX=-14.8781 EndY=25.8504 EndZ=0
    g202: LineSegment StartX=-14.8781 StartY=25.8504 StartZ=0 EndX=-10.8534 EndY=25.8504 EndZ=0
    g203: LineSegment StartX=-10.8534 StartY=25.8504 StartZ=0 EndX=-10.8534 EndY=24.0923 EndZ=0
    g204: LineSegment StartX=-10.5106 StartY=14.1107 StartZ=0 EndX=-10.5106 EndY=19.7752 EndZ=0
  constraints (209):
    c: Coincident(g1,g0)
    c: Horizontal(g0)
    c: Vertical(g1)
    c: Coincident(g2,g3)
    c: Coincident(g3,g4)
    c: Horizontal(g4)
    c: Horizontal(g2)
    c: Vertical(g3)
    c: Block(g1)
    c: Distance(g3) = 4.86
    c: Block(g4)
    c: Distance(g0) = 10.8
    c: Distance(g2) = 10.8
    c: Coincident(g5,g0)
    c: Coincident(g6,g4)
    c: Coincident(g6,g2)
    c: Block(g8)
    c: Block(g7)
    c: Coincident(g9,g8)
    c: Coincident(g9,g7)
    c: Vertical(g9)
    c: Coincident(g10,g7)
    c: Coincident(g10,g8)
    c: Vertical(g10)
    c: Weight(g11) = 1
    c: Equal(g11, g12-g21) x10
    c: InternalAlignment(g11-g21 -> g22) x11
    c: InternalAlignment(g23-g31 -> g22) x9
    c: Block(g22)
    c: Weight(g32) = 1
    c: Equal(g32, g33-g49) x17
    c: InternalAlignment(g32-g49 -> g50) x18
    c: InternalAlignment(g51-g66 -> g50) x16
    c: Block(g50)
    c: Coincident(g67,g50)
    c: Coincident(g67,g22)
    c: Coincident(g68,g22)
    c: Coincident(g68,g50)
    c: InternalAlignment(g70,g69)
    c: InternalAlignment(g71,g69)
    c: Block(g69)
    c: InternalAlignment(g73,g72)
    c: InternalAlignment(g74,g72)
    c: Block(g72)
    c: InternalAlignment(g76,g75)
    c: InternalAlignment(g77,g75)
    c: InternalAlignment(g78,g80)
    c: InternalAlignment(g79,g80)
    c: Block(g80)
    c: Coincident(g75,g80)
    c: Block(g75)
    c: InternalAlignment(g82,g81)
    c: InternalAlignment(g83,g81)
    c: InternalAlignment(g84,g86)
    c: InternalAlignment(g85,g86)
    c: Block(g86)
    c: Coincident(g81,g86)
    c: Block(g81)
    c: Horizontal(g87)
    c: Block(g87)
    c: Horizontal(g88)
    c: Distance(g88) = 4.14
    c: Horizontal(g89)
    c: Equal(g88,g89) = 4.14
    c: Block(g89)
    c: Block(g88)
    c: Coincident(g90,g87)
    c: Vertical(g90)
    c: Distance(g90) = 11.88
    c: Coincident(g91,g90)
    c: Horizontal(g91)
    c: Coincident(g92,g91)
    c: Vertical(g92)
    c: Distance(g91) = 4.03
    c: Distance(g92) = 1.9
    c: Coincident(g93,g87)
    c: Vertical(g93)
    c: Vertical(g94)
    c: Coincident(g94,g88)
    c: Distance(g93) = 5.8
    c: Distance(g94) = 5.8
    c: Vertical(g95)
    c: Coincident(g95,g88)
    c: Distance(g95) = 6.9
    c: Coincident(g107,g92)
    c: Weight(g96) = 1
    c: Equal(g96, g97-g106) x10
    c: InternalAlignment(g96-g106 -> g107) x11
    c: InternalAlignment(g108-g116 -> g107) x9
    c: Block(g107)
    c: Block(g117)
    c: Coincident(g126,g93)
    c: Weight(g118) = 1
    c: Equal(g118, g119-g125) x7
    c: Coincident(g126,g95)
    c: InternalAlignment(g118-g125 -> g126) x8
    c: InternalAlignment(g127-g132 -> g126) x6
    c: Coincident(g133,g94)
    c: Block(g126)
    c: Block(g133)
    c: Coincident(g134,g133)
    c: Coincident(g134,g89)
    c: Vertical(g134)
    c: Horizontal(g135)
    c: Block(g135)
    c: Horizontal(g136)
    c: Equal(g88,g136) = 4.14
    c: Horizontal(g137)
    c: Equal(g136,g137) = 4.14
    c: Block(g137)
    c: Block(g136)
    c: Coincident(g138,g135)
    c: Vertical(g138)
    c: Equal(g90,g138) = 11.88
    c: Coincident(g139,g138)
    c: Horizontal(g139)
    c: Coincident(g140,g139)
    c: Vertical(g140)
    c: Equal(g91,g139) = 4.03
    c: Equal(g92,g140) = 1.9
    c: Coincident(g141,g135)
    c: Vertical(g141)
    c: Vertical(g142)
    c: Coincident(g142,g136)
    c: Equal(g93,g141) = 5.8
    c: Equal(g94,g142) = 5.8
    c: Vertical(g143)
    c: Coincident(g143,g136)
    c: Equal(g95,g143) = 6.9
    c: Coincident(g149,g140)
    c: Equal(g96,g144) = 1
    c: Equal(g144, g145-g148) x4
    c: InternalAlignment(g144-g148 -> g149) x5
    c: InternalAlignment(g150-g158 -> g149) x9
    c: Block(g149)
    c: Block(g159)
    c: Coincident(g168,g141)
    c: Equal(g118,g160) = 1
    c: Equal(g160, g161-g167) x7
    c: Coincident(g168,g143)
    c: InternalAlignment(g160-g167 -> g168) x8
    c: InternalAlignment(g169-g174 -> g168) x6
    c: Coincident(g175,g142)
    c: Block(g168)
    c: Block(g175)
    c: Coincident(g176,g175)
    c: Coincident(g176,g137)
    c: Vertical(g176)
    c: Coincident(g177,g137)
    c: Vertical(g177)
    c: Coincident(g178,g177)
    c: Coincident(g178,g159)
    c: InternalAlignment(g179,g178)
    c: InternalAlignment(g180,g178)
    c: Block(g178)
    c: Vertical(g181)
    c: Coincident(g181,g89)
    c: Block(g5)
    c: Coincident(g182,g1)
    c: Coincident(g182,g5)
    c: Horizontal(g182)
    c: Coincident(g186,g117)
    c: Weight(g183) = 1
    c: Equal(g183,g184)
    c: Equal(g183,g185)
    c: Coincident(g186,g181)
    c: InternalAlignment(g183,g186)
    c: InternalAlignment(g184,g186)
    c: InternalAlignment(g185,g186)
    c: InternalAlignment(g187,g186)
    c: InternalAlignment(g188,g186)
    c: Block(g186)
    c: InternalAlignment(g190,g189)
    c: InternalAlignment(g191,g189)
    c: Block(g189)
    c: InternalAlignment(g193,g192)
    c: InternalAlignment(g194,g192)
    c: Block(g192)
    c: Horizontal(g195)
    c: Block(g195)
    c: Coincident(g196,g195)
    c: Vertical(g196)
    c: Block(g196)
    c: Distance(g195) = 3.71244
    c: Coincident(g197,g196)
    c: Horizontal(g197)
    c: Distance(g197) = 4.1
    c: Coincident(g198,g192)
    c: Coincident(g198,g197)
    c: Vertical(g198)
    c: Block(g198)
    c: Coincident(g199,g192)
    c: Coincident(g199,g195)
    c: Vertical(g199)
    c: Block(g199)
    c: Horizontal(g200)
    c: Block(g200)
    c: Coincident(g201,g200)
    c: Vertical(g201)
    c: Block(g201)
    c: Coincident(g202,g201)
    c: Horizontal(g202)
    c: Block(g202)
    c: Coincident(g203,g202)
    c: Vertical(g203)
    c: Block(g203)
    c: Coincident(g204,g200)
    c: Vertical(g204)
    c: Block(g204)
FEATURE [PartDesign::Body] Body
  Group = -> [Sketch083]
  Origin = -> Origin
FEATURE [Sketcher::SketchObject] Sketch084
  FullyConstrained = true
  MapMode = 5
  Support = -> [XY_Plane001]
FEATURE [PartDesign::Body] Body001
  Group = -> [Sketch084]
  Origin = -> Origin001
